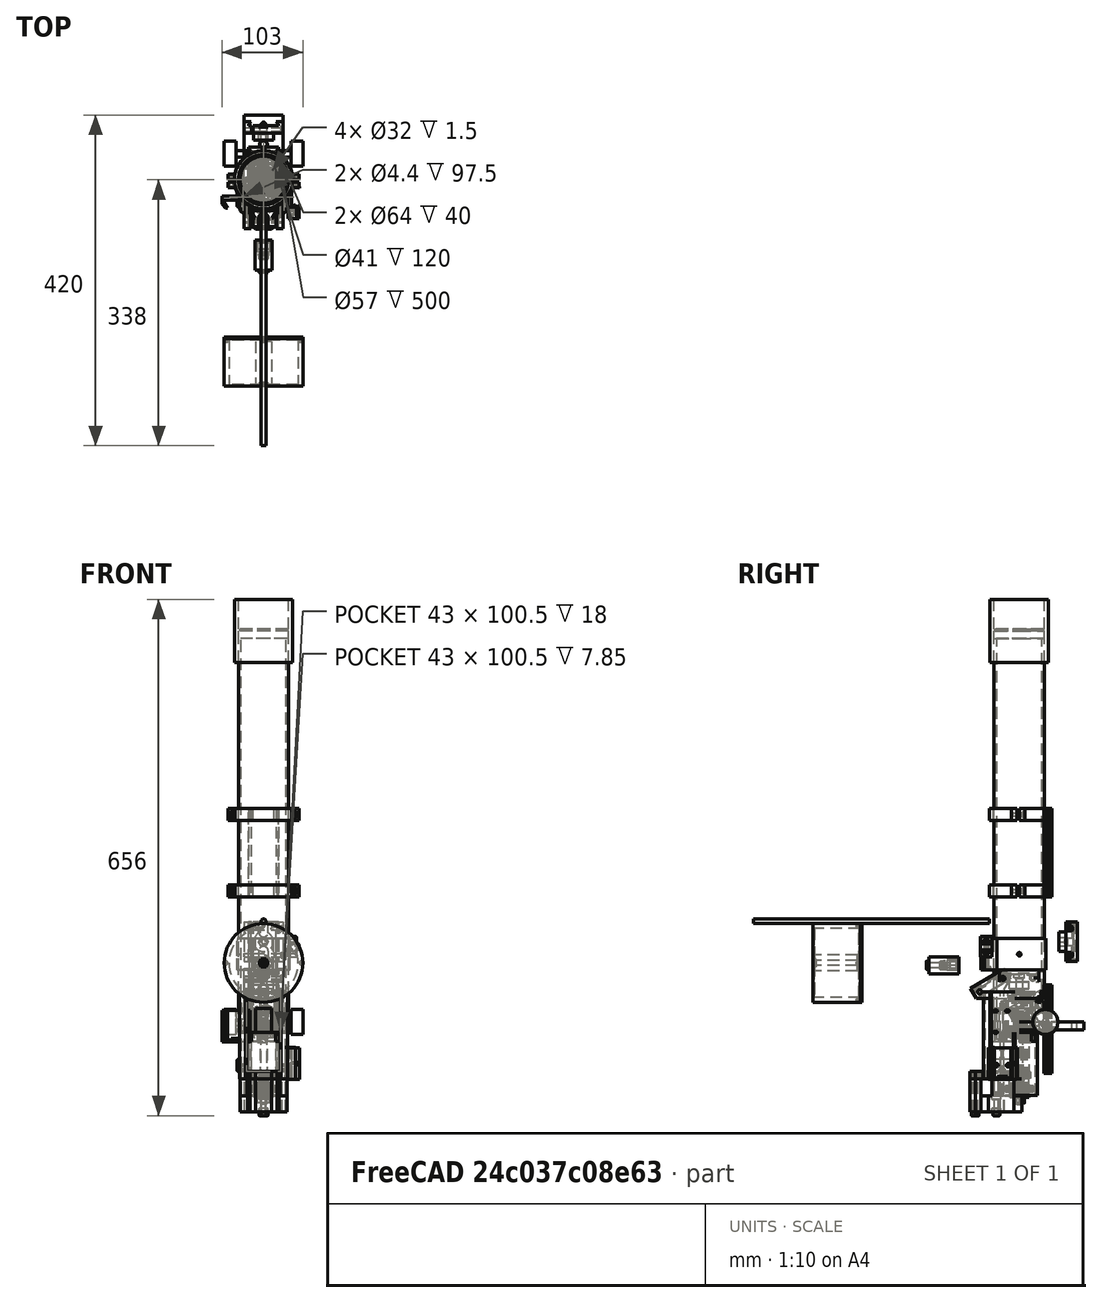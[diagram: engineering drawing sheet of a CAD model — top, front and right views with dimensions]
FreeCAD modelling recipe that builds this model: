
FCSTD DOCUMENT  (FreeCAD 0.17R12619 (Git))
Label: eq-mount-V1.2
License: All rights reserved
LicenseURL: http://en.wikipedia.org/wiki/All_rights_reserved
objects: Part::Cylinder×507, Part::MultiFuse×390, Part::Feature×377, Part::Cut×280, Part::Box×135, Part::FeaturePython×76, Part::Extrusion×70, App::Part×57, Sketcher::SketchObject×44, Part::Chamfer×20, Part::RegularPolygon×11, Part::Fillet×9
note: 1919 computed .brp shape members not serialized (recipe doc carries the construction recipe); baked Part::Feature solids carry a one-line shape summary decoded from their .brp

FEATURE [Part::FeaturePython] InvoluteGear007  # WARN: FeaturePython — macro-defined, semantics opaque (R4)
  backlash = 0
  beta = 0
  clearance = 0.25
  double_helix = false
  head = 0
  height = 5.5
  module = 1.2
  numpoints = 6
  pressure_angle = 20
  reversed_backlash = false
  shift = 0
  simple = false
  teeth = 27
  undercut = false
FEATURE [Part::FeaturePython] InvoluteGear006  # WARN: FeaturePython — macro-defined, semantics opaque (R4)
  backlash = 0
  beta = 0
  clearance = 0.25
  double_helix = false
  head = 0
  height = 5.5
  module = 1.2
  numpoints = 6
  pressure_angle = 20
  reversed_backlash = false
  shift = 0
  simple = false
  teeth = 27
  undercut = false
FEATURE [Part::FeaturePython] InvoluteGear005  # WARN: FeaturePython — macro-defined, semantics opaque (R4)
  backlash = 0
  beta = 0
  clearance = 0.25
  double_helix = false
  head = 0
  height = 5.5
  module = 1.2
  numpoints = 6
  pressure_angle = 20
  reversed_backlash = false
  shift = 0
  simple = false
  teeth = 27
  undercut = false
FEATURE [Part::Cylinder] Cylinder007  label="Válec007"
  Angle = 360
  AttacherType = Attacher::AttachEngine3D
  Height = 1.5
  Radius = 20
FEATURE [Part::Cylinder] Cylinder008  label="Válec008"
  Angle = 360
  AttacherType = Attacher::AttachEngine3D
  Height = 1.5
  Radius = 16
FEATURE [Part::Cylinder] Cylinder006  label="Válec006"
  Angle = 360
  AttacherType = Attacher::AttachEngine3D
  Height = 1.5
  Radius = 16
FEATURE [Part::Cut] Cut  label="Ring2"
  Base = -> Cylinder007
  Placement = pos=(0,0,5.5) rot=(0,0,1;0rad)
  Tool = -> Cylinder006
FEATURE [Part::Cylinder] Cylinder009  label="Válec009"
  Angle = 360
  AttacherType = Attacher::AttachEngine3D
  Height = 1.5
  Radius = 20
FEATURE [Part::Cut] Cut003  label="Ring003"
  Base = -> Cylinder009
  Placement = pos=(0,0,-1.5) rot=(0,0,1;0rad)
  Tool = -> Cylinder008
FEATURE [Part::Cylinder] Cylinder005  label="Válec005"
  Angle = 360
  AttacherType = Attacher::AttachEngine3D
  Height = 5.5
  Radius = 20
FEATURE [Part::Cut] Cut002  label="ring 001"
  Base = -> Cylinder005
  Tool = -> InvoluteGear005
FEATURE [Part::MultiFuse] Fusion  label="Ring zaklad Fin"
  Shapes = -> [Cut002,Cut,Cut003]
FEATURE [Sketcher::SketchObject] Sketch001
  MapMode = 45
  Placement = pos=(44.88,21.011,5.40003) rot=(0.707106,0.001666,0.707106;3.13826rad)
  sketch-geometry (7):
    g0: LineSegment StartX=5 StartY=0 StartZ=0 EndX=2.5 EndY=4.33013 EndZ=0
    g1: LineSegment StartX=2.5 StartY=4.33013 StartZ=0 EndX=-2.5 EndY=4.33013 EndZ=0
    g2: LineSegment StartX=-2.5 StartY=4.33013 StartZ=0 EndX=-5 EndY=0 EndZ=0
    g3: LineSegment StartX=-5 StartY=0 StartZ=0 EndX=-2.5 EndY=-4.33013 EndZ=0
    g4: LineSegment StartX=-2.5 StartY=-4.33013 StartZ=0 EndX=2.5 EndY=-4.33013 EndZ=0
    g5: LineSegment StartX=2.5 StartY=-4.33013 StartZ=0 EndX=5 EndY=0 EndZ=0
    g6: Circle [constr] CenterX=0 CenterY=0 CenterZ=0 NormalX=0 NormalY=0 NormalZ=1 AngleXU=0 Radius=5
  constraints (14):
    c: Coincident(g0,g1)
    c: Coincident(g1,g2)
    c: Coincident(g2,g3)
    c: Coincident(g3,g4)
    c: Coincident(g4,g5)
    c: Coincident(g5,g0)
    c: Equal(g0, g1-g5) x5
    c: PointOnObject(g0,g6)
    c: PointOnObject(g1,g6)
    c: PointOnObject(g2,g6)
    c: PointOnObject(g3,g6)
    c: PointOnObject(g4,g6)
    c: PointOnObject(g5,g6)
    c: PointOnObject(g6,g-1)
FEATURE [Part::Feature] Cut005_solid001_cs
  Placement = pos=(0,0,-11.25) rot=(0,0,1;0rad)
  shape: bbox 41 x 41 x 3e-07 mm, 0 faces, 0 solids (baked)
FEATURE [Part::Feature] Screw_solid003  label="M2x4-Screw (Solid)003"
  Placement = pos=(0,0,0) rot=(0,0,1;1.0472rad)
  shape: bbox 3.6 x 3.6 x 4 mm, 12 faces (baked)
FEATURE [Part::Feature] Cylinder014002  label="Válec014"
  Placement = pos=(0,0,0) rot=(0,0,1;4.18879rad)
  shape: bbox 16 x 16 x 10 mm, 3 faces (baked)
FEATURE [Part::Feature] Screw_solid004  label="M2x4-Screw (Solid)004"
  Placement = pos=(0,0,0) rot=(0,0,-1;1.0472rad)
  shape: bbox 3.6 x 3.6 x 4 mm, 12 faces (baked)
FEATURE [Part::Feature] Screw_solid005  label="M2x4-Screw (Solid)005"
  Placement = pos=(0,0,0) rot=(0,0,1;3.14159rad)
  shape: bbox 3.6 x 3.6 x 4 mm, 12 faces (baked)
FEATURE [Part::MultiFuse] Fusion004  label="srouby002"
  Shapes = -> [Screw_solid003,Screw_solid004,Screw_solid005]
FEATURE [Part::Feature] Cut008_solid  label="Planet001"
  shape: bbox 12.9 x 13.1 x 5 mm, 57 faces (baked)
FEATURE [Part::Feature] Cylinder014001  label="Válec013"
  Placement = pos=(0,0,0) rot=(0,0,1;2.0944rad)
  shape: bbox 16 x 16 x 10 mm, 3 faces (baked)
FEATURE [Part::Cylinder] Cylinder014005010  label="Unasec vrch001"
  Angle = 360
  AttacherType = Attacher::AttachEngine3D
  Height = 1.5
  Placement = pos=(0,0,5.5) rot=(0,0,1;0rad)
  Radius = 15.5
FEATURE [Part::Cylinder] Cylinder010  label="unasec spodek"
  Angle = 360
  AttacherType = Attacher::AttachEngine3D
  Height = 1.5
  Placement = pos=(0,0,-1.5) rot=(0,0,1;0rad)
  Radius = 15.5
FEATURE [Part::Cylinder] Cylinder  label="Válec"
  Angle = 360
  AttacherType = Attacher::AttachEngine3D
  Height = 10
  Placement = pos=(0,0,-3) rot=(0,0,1;0rad)
  Radius = 7
FEATURE [Part::Cylinder] Cylinder014005007  label="Válec024"
  Angle = 360
  AttacherType = Attacher::AttachEngine3D
  Height = 7.5
  Placement = pos=(0,0,-7) rot=(0,0,1;0rad)
  Radius = 6.5
FEATURE [Part::Cylinder] Cylinder013  label="Válec011"
  Angle = 360
  AttacherType = Attacher::AttachEngine3D
  Height = 10
  Placement = pos=(10.5,0,0) rot=(0,0,1;0rad)
  Radius = 8
FEATURE [Part::MultiFuse] Fusion001
  Shapes = -> [Cylinder,Cylinder013,Cylinder014002,Cylinder014001]
FEATURE [Part::Cylinder] Cylinder011  label="unasec stred"
  Angle = 360
  AttacherType = Attacher::AttachEngine3D
  Height = 7
  Placement = pos=(0,0,-1.5) rot=(0,0,1;0rad)
  Radius = 13.5
FEATURE [Part::MultiFuse] Fusion002
  Shapes = -> [Cylinder011,Cylinder010]
FEATURE [Part::Cut] Cut004  label="unasec spodek001"
  Base = -> Fusion002
  Tool = -> Fusion001
FEATURE [Part::Cut] Cut006  label="Uasec spodek"
  Base = -> Cut004
  Tool = -> Fusion004
FEATURE [Part::Cylinder] Cylinder014005008  label="Válec025"
  Angle = 360
  AttacherType = Attacher::AttachEngine3D
  Height = 15
  Placement = pos=(0,0,-8) rot=(0,0,1;0rad)
  Radius = 2.65
FEATURE [Part::Cylinder] Cylinder014005009  label="Válec026"
  Angle = 360
  AttacherType = Attacher::AttachEngine3D
  Height = 7
  Placement = pos=(0,0,-7) rot=(0,0,1;0rad)
  Radius = 12
FEATURE [Part::Extrusion] Extrude  label="box"
  Base = -> Cut005_solid001_cs
  Dir = (0,0,1)
  DirMode = 2
  FaceMakerClass = Part::FaceMakerBullseye
  LengthFwd = 19
  LengthRev = 0
  Placement = pos=(0,0,-11.5) rot=(0,0,1;0rad)
  Solid = true
  Symmetric = false
FEATURE [Part::RegularPolygon] RegularPolygon  label="Pravidelný n-úhelník"
  AttacherType = Attacher::AttachEngine3D
  Circumradius = 6
  Polygon = 6
FEATURE [Part::Extrusion] Extrude006
  Base = -> RegularPolygon
  Dir = (0,0,1)
  DirMode = 2
  FaceMakerClass = Part::FaceMakerBullseye
  LengthFwd = 8
  LengthRev = 0
  Placement = pos=(0,0,13) rot=(0,0,1;0rad)
  Solid = true
  Symmetric = false
FEATURE [Part::Extrusion] Extrude007
  Base = -> Sketch001
  Dir = (1,0,0)
  DirMode = 2
  FaceMakerClass = Part::FaceMakerBullseye
  LengthFwd = 5
  LengthRev = 0
  Placement = pos=(0,0,0.25) rot=(0,0,1;0rad)
  Solid = true
  Symmetric = false
FEATURE [Part::FeaturePython] InvoluteGear012  # WARN: FeaturePython — macro-defined, semantics opaque (R4)
  backlash = 0
  beta = 0
  clearance = 0.25
  double_helix = false
  head = 0
  height = 5.5
  module = 1.2
  numpoints = 6
  pressure_angle = 20
  reversed_backlash = false
  shift = 0
  simple = false
  teeth = 27
  undercut = false
FEATURE [Part::FeaturePython] InvoluteGear013  # WARN: FeaturePython — macro-defined, semantics opaque (R4)
  backlash = 0
  beta = 0
  clearance = 0.25
  double_helix = false
  head = 0
  height = 5.5
  module = 1.2
  numpoints = 6
  pressure_angle = 20
  reversed_backlash = false
  shift = 0
  simple = false
  teeth = 27
  undercut = false
FEATURE [Part::Feature] Cylinder014005025  label="Válec038"
  Placement = pos=(0,0,0) rot=(0,0,1;2.0944rad)
  shape: bbox 5 x 5 x 7 mm, 3 faces (baked)
FEATURE [Part::Feature] Cylinder014005026  label="Válec039"
  Placement = pos=(0,0,0) rot=(0,0,1;2.0944rad)
  shape: bbox 16 x 16 x 10 mm, 3 faces (baked)
FEATURE [Part::Feature] Cylinder014005024  label="Válec037"
  Placement = pos=(0,0,0) rot=(0,0,1;4.18879rad)
  shape: bbox 16 x 16 x 10 mm, 3 faces (baked)
FEATURE [Part::Feature] Screw_solid006  label="M2x4-Screw (Solid)006"
  Placement = pos=(0,0,0) rot=(0,0,1;1.0472rad)
  shape: bbox 3.6 x 3.6 x 4 mm, 12 faces (baked)
FEATURE [Part::Feature] Screw_solid007  label="M2x4-Screw (Solid)007"
  Placement = pos=(0,0,0) rot=(0,0,-1;1.0472rad)
  shape: bbox 3.6 x 3.6 x 4 mm, 12 faces (baked)
FEATURE [Part::Feature] Cylinder014005006  label="Válec023"
  Placement = pos=(0,0,0) rot=(0,0,1;4.18879rad)
  shape: bbox 5 x 5 x 7 mm, 3 faces (baked)
FEATURE [Part::Feature] Cut008_solid001  label="Planet002"
  Placement = pos=(0,0,0) rot=(0,0,1;2.0944rad)
  shape: bbox 12.9 x 13.1 x 5 mm, 57 faces (baked)
FEATURE [Part::Feature] Cut008_solid002  label="Planet003"
  Placement = pos=(0,0,0) rot=(0,0,1;4.18879rad)
  shape: bbox 12.9 x 13.1 x 5 mm, 57 faces (baked)
FEATURE [Part::Feature] Cut007_solid  label="Sun1"
  shape: bbox 12.9 x 13.1 x 5 mm, 57 faces (baked)
FEATURE [Part::MultiFuse] Fusion010
  Shapes = -> [Cut007_solid,Cylinder014005007,Cylinder014005009]
FEATURE [Part::Feature] Screw_solid008  label="M2x4-Screw (Solid)008"
  Placement = pos=(0,0,0) rot=(0,0,1;3.14159rad)
  shape: bbox 3.6 x 3.6 x 4 mm, 12 faces (baked)
FEATURE [Part::MultiFuse] Fusion011  label="srouby003"
  Placement = pos=(0,0,0.5) rot=(0,0,1;0rad)
  Shapes = -> [Screw_solid006,Screw_solid007,Screw_solid008]
FEATURE [Part::Cut] Cut012  label="unasec vrch001"
  Base = -> Cylinder014005010
  Tool = -> Fusion011
FEATURE [Part::Feature] Cylinder014005005  label="Válec022"
  Placement = pos=(0,0,0) rot=(0,0,1;2.0944rad)
  shape: bbox 5 x 5 x 7 mm, 3 faces (baked)
FEATURE [Part::Feature] Cylinder014005013  label="Válec029"
  Placement = pos=(0,0,0) rot=(0,0,1;2.0944rad)
  shape: bbox 5 x 5 x 7 mm, 3 faces (baked)
FEATURE [Part::Feature] Cylinder014005004  label="Válec021"
  shape: bbox 5 x 5 x 7 mm, 3 faces (baked)
FEATURE [Part::MultiFuse] Fusion006
  Shapes = -> [Cylinder014005006,Cylinder014005004,Cylinder014005005]
FEATURE [Part::MultiFuse] Fusion008  label="Unasec spdek final"
  Shapes = -> [Cut006,Fusion006]
FEATURE [Part::Feature] Cylinder014005012  label="Válec028"
  shape: bbox 5 x 5 x 7 mm, 3 faces (baked)
FEATURE [Part::Feature] Cylinder014005014  label="Válec030"
  Placement = pos=(0,0,0) rot=(0,0,1;4.18879rad)
  shape: bbox 5 x 5 x 7 mm, 3 faces (baked)
FEATURE [Part::MultiFuse] Fusion012
  Shapes = -> [Cylinder014005014,Cylinder014005012,Cylinder014005013]
FEATURE [Part::Feature] Cut008_solid003  label="Planet004"
  Placement = pos=(0,0,0) rot=(0,0,1;4.18879rad)
  shape: bbox 12.9 x 13.1 x 5 mm, 57 faces (baked)
FEATURE [Part::Cylinder] Cylinder014005016  label="unasec spodek003"
  Angle = 360
  AttacherType = Attacher::AttachEngine3D
  Height = 1.5
  Placement = pos=(0,0,-1.5) rot=(0,0,1;0rad)
  Radius = 15.5
FEATURE [Part::Cylinder] Cylinder014005035  label="Válec048"
  Angle = 360
  AttacherType = Attacher::AttachEngine3D
  Height = 18
  Radius = 2.6
FEATURE [Part::Cylinder] Cylinder014005032  label="Válec045"
  Angle = 360
  AttacherType = Attacher::AttachEngine3D
  Height = 1.5
  Radius = 16
FEATURE [Part::Cylinder] Cylinder014005015  label="Válec031"
  Angle = 360
  AttacherType = Attacher::AttachEngine3D
  Height = 10
  Placement = pos=(0,0,-3) rot=(0,0,1;0rad)
  Radius = 7
FEATURE [Part::Cylinder] Cylinder014005029  label="Válec042"
  Angle = 360
  AttacherType = Attacher::AttachEngine3D
  Height = 1.5
  Radius = 16
FEATURE [Part::Cylinder] Cylinder014005031  label="Válec044"
  Angle = 360
  AttacherType = Attacher::AttachEngine3D
  Height = 1.5
  Radius = 20
FEATURE [Part::Cut] Cut017  label="Ring005"
  Base = -> Cylinder014005031
  Placement = pos=(0,0,-1.5) rot=(0,0,1;0rad)
  Tool = -> Cylinder014005032
FEATURE [Part::Cylinder] Cylinder014005034  label="Válec047"
  Angle = 360
  AttacherType = Attacher::AttachEngine3D
  Height = 4
  Placement = pos=(0,0,7) rot=(0,0,1;0rad)
  Radius = 6.5
FEATURE [Part::Cylinder] Cylinder014005036  label="Válec049"
  Angle = 360
  AttacherType = Attacher::AttachEngine3D
  Height = 4
  Placement = pos=(0,0,7) rot=(0,0,1;0rad)
  Radius = 6.5
FEATURE [Part::Cylinder] Cylinder014005041  label="Unasec vrch003"
  Angle = 360
  AttacherType = Attacher::AttachEngine3D
  Height = 1.5
  Placement = pos=(0,0,5.5) rot=(0,0,1;0rad)
  Radius = 15.5
FEATURE [Part::Cylinder] Cylinder014005011  label="Válec027"
  Angle = 360
  AttacherType = Attacher::AttachEngine3D
  Height = 7
  Radius = 2.6
FEATURE [Part::MultiFuse] Fusion013
  Placement = pos=(0,0,1) rot=(0,0,1;0rad)
  Shapes = -> [Fusion012,Cylinder014005011]
FEATURE [Part::Cut] Cut011  label="Unasec Vrch zaklad001"
  Base = -> Cut012
  Tool = -> Fusion013
FEATURE [Part::Cylinder] Cylinder014005017  label="unasec stred001"
  Angle = 360
  AttacherType = Attacher::AttachEngine3D
  Height = 7
  Placement = pos=(0,0,-1.5) rot=(0,0,1;0rad)
  Radius = 13.5
FEATURE [Part::Cylinder] Cylinder014005018  label="Válec032"
  Angle = 360
  AttacherType = Attacher::AttachEngine3D
  Height = 10
  Placement = pos=(10.5,0,0) rot=(0,0,1;0rad)
  Radius = 8
FEATURE [Part::MultiFuse] Fusion017
  Shapes = -> [Cylinder014005015,Cylinder014005018,Cylinder014005024,Cylinder014005026]
FEATURE [Part::Cylinder] Cylinder014005030  label="Válec043"
  Angle = 360
  AttacherType = Attacher::AttachEngine3D
  Height = 1.5
  Radius = 20
FEATURE [Part::Cut] Cut014  label="Ring004"
  Base = -> Cylinder014005030
  Placement = pos=(0,0,5.5) rot=(0,0,1;0rad)
  Tool = -> Cylinder014005029
FEATURE [Part::Cylinder] Cylinder014005033  label="Válec046"
  Angle = 360
  AttacherType = Attacher::AttachEngine3D
  Height = 5.5
  Radius = 20
FEATURE [Part::Cut] Cut015  label="ring 002"
  Base = -> Cylinder014005033
  Tool = -> InvoluteGear006
FEATURE [Part::Cylinder] Cylinder014005037  label="Válec050"
  Angle = 360
  AttacherType = Attacher::AttachEngine3D
  Height = 18
  Radius = 2.6
FEATURE [Part::Cylinder] Cylinder014005051  label="Válec063"
  Angle = 360
  AttacherType = Attacher::AttachEngine3D
  Height = 7
  Radius = 2.6
FEATURE [Part::Cylinder] Cylinder014005052  label="Válec064"
  Angle = 360
  AttacherType = Attacher::AttachEngine3D
  Height = 10
  Placement = pos=(0,0,-3) rot=(0,0,1;0rad)
  Radius = 7
FEATURE [Part::Cylinder] Cylinder014005042  label="Válec054"
  Angle = 360
  AttacherType = Attacher::AttachEngine3D
  Height = 7
  Radius = 2.6
FEATURE [Part::Cylinder] Cylinder014005054  label="Válec065"
  Angle = 360
  AttacherType = Attacher::AttachEngine3D
  Height = 10
  Placement = pos=(10.5,0,0) rot=(0,0,1;0rad)
  Radius = 8
FEATURE [Part::Cylinder] Cylinder014005056  label="Válec066"
  Angle = 360
  AttacherType = Attacher::AttachEngine3D
  Height = 1.5
  Radius = 16
FEATURE [Part::Cylinder] Cylinder014005053  label="unasec stred002"
  Angle = 360
  AttacherType = Attacher::AttachEngine3D
  Height = 7
  Placement = pos=(0,0,-1.5) rot=(0,0,1;0rad)
  Radius = 13.5
FEATURE [Part::Cylinder] Cylinder014005057  label="Válec067"
  Angle = 360
  AttacherType = Attacher::AttachEngine3D
  Height = 4
  Placement = pos=(0,0,7) rot=(0,0,1;0rad)
  Radius = 6.5
FEATURE [Part::Cylinder] Cylinder014005055  label="unasec spodek005"
  Angle = 360
  AttacherType = Attacher::AttachEngine3D
  Height = 1.5
  Placement = pos=(0,0,-1.5) rot=(0,0,1;0rad)
  Radius = 15.5
FEATURE [Part::Feature] Screw_solid016  label="M2x4-Screw (Solid)016"
  Placement = pos=(0,0,0) rot=(0,0,1;3.14159rad)
  shape: bbox 3.6 x 3.6 x 4 mm, 12 faces (baked)
FEATURE [Part::Feature] Screw_solid014  label="M2x4-Screw (Solid)014"
  Placement = pos=(0,0,0) rot=(0,0,-1;1.0472rad)
  shape: bbox 3.6 x 3.6 x 4 mm, 12 faces (baked)
FEATURE [Part::Feature] Cylinder014005027  label="Válec040"
  shape: bbox 5 x 5 x 7 mm, 3 faces (baked)
FEATURE [Part::Feature] Screw_solid015  label="M2x4-Screw (Solid)015"
  Placement = pos=(0,0,0) rot=(0,0,-1;1.0472rad)
  shape: bbox 3.6 x 3.6 x 4 mm, 12 faces (baked)
FEATURE [Part::Feature] Screw_solid011  label="M2x4-Screw (Solid)011"
  Placement = pos=(0,0,0) rot=(0,0,1;3.14159rad)
  shape: bbox 3.6 x 3.6 x 4 mm, 12 faces (baked)
FEATURE [Part::Feature] Cut008_solid004  label="Planet005"
  shape: bbox 12.9 x 13.1 x 5 mm, 57 faces (baked)
FEATURE [Part::Feature] Cylinder014005028  label="Válec041"
  Placement = pos=(0,0,0) rot=(0,0,1;4.18879rad)
  shape: bbox 5 x 5 x 7 mm, 3 faces (baked)
FEATURE [Part::Feature] Cut007_solid001  label="Sun2"
  Placement = pos=(0,0,10.5) rot=(0,0,1;0rad)
  shape: bbox 12.9 x 13.1 x 5 mm, 57 faces (baked)
FEATURE [Part::Feature] Cut008_solid005  label="Planet006"
  Placement = pos=(0,0,0) rot=(0,0,1;2.0944rad)
  shape: bbox 12.9 x 13.1 x 5 mm, 57 faces (baked)
FEATURE [Part::Feature] Cut007_solid002  label="Sun003"
  Placement = pos=(0,0,10.5) rot=(0,0,1;0rad)
  shape: bbox 12.9 x 13.1 x 5 mm, 57 faces (baked)
FEATURE [Part::Feature] Screw_solid013  label="M2x4-Screw (Solid)013"
  Placement = pos=(0,0,0) rot=(0,0,1;1.0472rad)
  shape: bbox 3.6 x 3.6 x 4 mm, 12 faces (baked)
FEATURE [Part::MultiFuse] Fusion018
  Shapes = -> [Cylinder014005017,Cylinder014005016]
FEATURE [Part::Cut] Cut016  label="unasec spodek002"
  Base = -> Fusion018
  Tool = -> Fusion017
FEATURE [Part::MultiFuse] Fusion028  label="Tělo I"
  Shapes = -> [Extrude,Fusion]
FEATURE [Part::MultiFuse] Fusion019  label="srouby005"
  Shapes = -> [Screw_solid013,Screw_solid014,Screw_solid011]
FEATURE [Part::Cut] Cut018  label="Uasec spodek001"
  Base = -> Cut016
  Tool = -> Fusion019
FEATURE [Part::MultiFuse] Fusion023  label="unasec vrhch 2"
  Shapes = -> [Cut011,Cut007_solid001,Cylinder014005034]
FEATURE [Part::Cut] Cut020  label="Unasec + Sun"
  Base = -> Fusion023
  Tool = -> Cylinder014005035
FEATURE [Part::MultiFuse] Fusion021
  Shapes = -> [Cylinder014005028,Cylinder014005027,Cylinder014005025]
FEATURE [Part::MultiFuse] Fusion020  label="Unasec spdek final001"
  Shapes = -> [Cut018,Fusion021]
FEATURE [Part::MultiFuse] Fusion030
  Shapes = -> [Cylinder014005053,Cylinder014005055]
FEATURE [Part::MultiFuse] Fusion022  label="Ring zaklad Fin001"
  Shapes = -> [Cut015,Cut014,Cut017]
FEATURE [Part::Feature] Cut008_solid007  label="Planet008"
  shape: bbox 12.9 x 13.1 x 5 mm, 57 faces (baked)
FEATURE [Part::Feature] Screw_solid022  label="M2x4-Screw (Solid)022"
  Placement = pos=(0,0,0) rot=(0,0,1;3.14159rad)
  shape: bbox 3.6 x 3.6 x 4 mm, 12 faces (baked)
FEATURE [Part::Feature] Cylinder014005048  label="Válec060"
  Placement = pos=(0,0,0) rot=(0,0,1;4.18879rad)
  shape: bbox 16 x 16 x 10 mm, 3 faces (baked)
FEATURE [Part::Feature] Cylinder014005049  label="Válec061"
  Placement = pos=(0,0,0) rot=(0,0,1;2.0944rad)
  shape: bbox 5 x 5 x 7 mm, 3 faces (baked)
FEATURE [Part::Feature] Cylinder014005050  label="Válec062"
  Placement = pos=(0,0,0) rot=(0,0,1;2.0944rad)
  shape: bbox 16 x 16 x 10 mm, 3 faces (baked)
FEATURE [Part::MultiFuse] Fusion031
  Shapes = -> [Cylinder014005052,Cylinder014005054,Cylinder014005048,Cylinder014005050]
FEATURE [Part::Cut] Cut030  label="unasec spodek004"
  Base = -> Fusion030
  Tool = -> Fusion031
FEATURE [Part::Feature] Cylinder014005040  label="Válec053"
  Placement = pos=(0,0,0) rot=(0,0,1;2.0944rad)
  shape: bbox 5 x 5 x 7 mm, 3 faces (baked)
FEATURE [Part::Feature] Cylinder014005039  label="Válec052"
  shape: bbox 5 x 5 x 7 mm, 3 faces (baked)
FEATURE [Part::Feature] Screw_solid019  label="M2x4-Screw (Solid)019"
  Placement = pos=(0,0,0) rot=(0,0,-1;1.0472rad)
  shape: bbox 3.6 x 3.6 x 4 mm, 12 faces (baked)
FEATURE [Part::Feature] Cut008_solid008  label="Planet009"
  Placement = pos=(0,0,0) rot=(0,0,1;4.18879rad)
  shape: bbox 12.9 x 13.1 x 5 mm, 57 faces (baked)
FEATURE [Part::Feature] Cut005_solid001_cs003
  Placement = pos=(0,0,-11.25) rot=(0,0,1;0rad)
  shape: bbox 41 x 41 x 3e-07 mm, 0 faces, 0 solids (baked)
FEATURE [Part::Extrusion] Extrude002  label="box002"
  Base = -> Cut005_solid001_cs003
  Dir = (0,0,1)
  DirMode = 2
  FaceMakerClass = Part::FaceMakerBullseye
  LengthFwd = 10.5
  LengthRev = 0
  Placement = pos=(0,0,-3) rot=(0,0,1;0rad)
  Solid = true
  Symmetric = false
FEATURE [Part::Feature] Screw_solid023  label="M2x4-Screw (Solid)023"
  Placement = pos=(0,0,0) rot=(0,0,1;1.0472rad)
  shape: bbox 3.6 x 3.6 x 4 mm, 12 faces (baked)
FEATURE [Part::Feature] Cylinder014005046  label="Válec058"
  Placement = pos=(0,0,0) rot=(0,0,1;4.18879rad)
  shape: bbox 5 x 5 x 7 mm, 3 faces (baked)
FEATURE [Part::Feature] Cut005_solid001_cs002
  Placement = pos=(0,0,-11.25) rot=(0,0,1;0rad)
  shape: bbox 41 x 41 x 3e-07 mm, 0 faces, 0 solids (baked)
FEATURE [Part::Extrusion] Extrude001  label="box001"
  Base = -> Cut005_solid001_cs002
  Dir = (0,0,1)
  DirMode = 2
  FaceMakerClass = Part::FaceMakerBullseye
  LengthFwd = 10.5
  LengthRev = 0
  Placement = pos=(0,0,-3) rot=(0,0,1;0rad)
  Solid = true
  Symmetric = false
FEATURE [Part::MultiFuse] Fusion029  label="teloII"
  Shapes = -> [Fusion022,Extrude001]
FEATURE [Part::Feature] Screw_solid017  label="M2x4-Screw (Solid)017"
  Placement = pos=(0,0,0) rot=(0,0,1;1.0472rad)
  shape: bbox 3.6 x 3.6 x 4 mm, 12 faces (baked)
FEATURE [Part::MultiFuse] Fusion027  label="srouby006"
  Placement = pos=(0,0,0.5) rot=(0,0,1;0rad)
  Shapes = -> [Screw_solid017,Screw_solid015,Screw_solid016]
FEATURE [Part::Cut] Cut021  label="unasec vrch003"
  Base = -> Cylinder014005041
  Tool = -> Fusion027
FEATURE [Part::Feature] Cylinder014005045  label="Válec057"
  Placement = pos=(0,0,0) rot=(0,0,1;4.18879rad)
  shape: bbox 5 x 5 x 7 mm, 3 faces (baked)
FEATURE [Part::Feature] Cut007_solid003  label="Sun004"
  Placement = pos=(0,0,10.5) rot=(0,0,1;0rad)
  shape: bbox 12.9 x 13.1 x 5 mm, 57 faces (baked)
FEATURE [Part::Feature] Cylinder014005047  label="Válec059"
  shape: bbox 5 x 5 x 7 mm, 3 faces (baked)
FEATURE [Part::MultiFuse] Fusion033
  Shapes = -> [Cylinder014005045,Cylinder014005047,Cylinder014005049]
FEATURE [Part::Feature] Screw_solid021  label="M2x4-Screw (Solid)021"
  Placement = pos=(0,0,0) rot=(0,0,-1;1.0472rad)
  shape: bbox 3.6 x 3.6 x 4 mm, 12 faces (baked)
FEATURE [Part::MultiFuse] Fusion039  label="srouby008"
  Shapes = -> [Screw_solid023,Screw_solid021,Screw_solid022]
FEATURE [Part::Cut] Cut031  label="Uasec spodek002"
  Base = -> Cut030
  Tool = -> Fusion039
FEATURE [Part::MultiFuse] Fusion040  label="Unasec spdek final002"
  Shapes = -> [Cut031,Fusion033]
FEATURE [Part::Feature] Cylinder014005044  label="Válec056"
  Placement = pos=(0,0,0) rot=(0,0,1;2.0944rad)
  shape: bbox 5 x 5 x 7 mm, 3 faces (baked)
FEATURE [Part::Feature] Cylinder014005038  label="Válec051"
  Placement = pos=(0,0,0) rot=(0,0,1;4.18879rad)
  shape: bbox 5 x 5 x 7 mm, 3 faces (baked)
FEATURE [Part::MultiFuse] Fusion026
  Shapes = -> [Cylinder014005038,Cylinder014005039,Cylinder014005040]
FEATURE [Part::MultiFuse] Fusion025
  Placement = pos=(0,0,1) rot=(0,0,1;0rad)
  Shapes = -> [Fusion026,Cylinder014005042]
FEATURE [Part::Cut] Cut022  label="Unasec Vrch zaklad003"
  Base = -> Cut021
  Tool = -> Fusion025
FEATURE [Part::MultiFuse] Fusion024  label="unasec vrhch 003"
  Shapes = -> [Cut022,Cut007_solid002,Cylinder014005036]
FEATURE [Part::Cut] Cut023  label="Unasec + Sun001"
  Base = -> Fusion024
  Tool = -> Cylinder014005037
FEATURE [App::Part] Part  label="Part071"
  Group = -> [Cut016,Cut018,Cylinder014005015,Cylinder014005016,Cylinder014005017,Cylinder014005018,Cylinder014005024,Cylinder014005025,Cylinder014005026,Screw_solid011,Cylinder014005027,Screw_solid013,Cylinder014005028,Screw_solid014,Fusion017,Fusion018,Fusion019,Fusion021,Fusion020,Cut008_solid004,Cut008_solid005,Cut008_solid003,Screw_solid017,Cylinder014005039,Cylinder014005040,Screw_solid015,Screw_solid016,+26 more]
  License = CC BY 3.0
  LicenseURL = http://creativecommons.org/licenses/by/3.0/
  Origin = -> Origin
  Placement = pos=(0,0,10.5) rot=(0,0,1;0rad)
FEATURE [Part::Feature] Cut008_solid006  label="Planet007"
  Placement = pos=(0,0,0) rot=(0,0,1;2.0944rad)
  shape: bbox 12.9 x 13.1 x 5 mm, 57 faces (baked)
FEATURE [Part::Feature] Screw_solid020  label="M2x4-Screw (Solid)020"
  Placement = pos=(0,0,0) rot=(0,0,1;3.14159rad)
  shape: bbox 3.6 x 3.6 x 4 mm, 12 faces (baked)
FEATURE [Part::Feature] Cylinder014005043  label="Válec055"
  shape: bbox 5 x 5 x 7 mm, 3 faces (baked)
FEATURE [Part::MultiFuse] Fusion038
  Shapes = -> [Cylinder014005046,Cylinder014005043,Cylinder014005044]
FEATURE [Part::MultiFuse] Fusion035
  Placement = pos=(0,0,1) rot=(0,0,1;0rad)
  Shapes = -> [Fusion038,Cylinder014005051]
FEATURE [Part::Feature] Screw_solid018  label="M2x4-Screw (Solid)018"
  Placement = pos=(0,0,0) rot=(0,0,1;1.0472rad)
  shape: bbox 3.6 x 3.6 x 4 mm, 12 faces (baked)
FEATURE [Part::MultiFuse] Fusion036  label="srouby007"
  Placement = pos=(0,0,0.5) rot=(0,0,1;0rad)
  Shapes = -> [Screw_solid018,Screw_solid019,Screw_solid020]
FEATURE [Part::Cylinder] Cylinder014005060  label="Válec070"
  Angle = 360
  AttacherType = Attacher::AttachEngine3D
  Height = 5.5
  Radius = 20
FEATURE [Part::Cut] Cut024  label="ring 003"
  Base = -> Cylinder014005060
  Tool = -> InvoluteGear007
FEATURE [Part::Cylinder] Cylinder014005063  label="Válec072"
  Angle = 360
  AttacherType = Attacher::AttachEngine3D
  Height = 1.5
  Radius = 20
FEATURE [Part::Cut] Cut029  label="Ring007"
  Base = -> Cylinder014005063
  Placement = pos=(0,0,5.5) rot=(0,0,1;0rad)
  Tool = -> Cylinder014005056
FEATURE [Part::Cylinder] Cylinder014005058  label="Válec068"
  Angle = 360
  AttacherType = Attacher::AttachEngine3D
  Height = 1.5
  Radius = 16
FEATURE [Part::Cylinder] Cylinder014005059  label="Válec069"
  Angle = 360
  AttacherType = Attacher::AttachEngine3D
  Height = 18
  Radius = 2.6
FEATURE [Part::Cylinder] Cylinder014005062  label="Válec071"
  Angle = 360
  AttacherType = Attacher::AttachEngine3D
  Height = 1.5
  Radius = 20
FEATURE [Part::Cut] Cut025  label="Ring006"
  Base = -> Cylinder014005062
  Placement = pos=(0,0,-1.5) rot=(0,0,1;0rad)
  Tool = -> Cylinder014005058
FEATURE [Part::MultiFuse] Fusion034  label="Ring zaklad Fin002"
  Shapes = -> [Cut024,Cut029,Cut025]
FEATURE [Part::MultiFuse] Fusion032  label="teloII001"
  Shapes = -> [Fusion034,Extrude002]
FEATURE [Part::Cylinder] Cylinder014005061  label="Unasec vrch004"
  Angle = 360
  AttacherType = Attacher::AttachEngine3D
  Height = 1.5
  Placement = pos=(0,0,5.5) rot=(0,0,1;0rad)
  Radius = 15.5
FEATURE [Part::Cut] Cut028  label="unasec vrch004"
  Base = -> Cylinder014005061
  Tool = -> Fusion036
FEATURE [Part::Cut] Cut027  label="Unasec Vrch zaklad004"
  Base = -> Cut028
  Tool = -> Fusion035
FEATURE [Part::MultiFuse] Fusion037  label="unasec vrhch 004"
  Shapes = -> [Cut027,Cut007_solid003,Cylinder014005057]
FEATURE [Part::Cut] Cut026  label="Unasec + Sun002"
  Base = -> Fusion037
  Tool = -> Cylinder014005059
FEATURE [App::Part] Part002  label="Part070"
  Group = -> [Cut030,Cut031,Cylinder014005052,Cylinder014005055,Cylinder014005053,Cylinder014005054,Cylinder014005048,Cylinder014005049,Cylinder014005050,Screw_solid022,Cylinder014005047,Screw_solid023,Cylinder014005045,Screw_solid021,Fusion031,Fusion030,Fusion039,Fusion033,Fusion040,Cut008_solid007,Cut008_solid006,Cut008_solid008,Screw_solid018,Cylinder014005043,Cylinder014005044,Screw_solid019,Screw_solid020,+26 more]
  License = CC BY 3.0
  LicenseURL = http://creativecommons.org/licenses/by/3.0/
  Origin = -> Origin002
  Placement = pos=(0,0,21) rot=(0,0,1;0rad)
FEATURE [Part::Feature] Cut007_solid005  label="Sun006"
  Placement = pos=(0,0,10.5) rot=(0,0,1;0rad)
  shape: bbox 12.9 x 13.1 x 5 mm, 57 faces (baked)
FEATURE [Part::Feature] Cylinder014005109  label="Válec111"
  Placement = pos=(0,0,0) rot=(0,0,1;2.0944rad)
  shape: bbox 16 x 16 x 10 mm, 3 faces (baked)
FEATURE [Part::Feature] Cylinder014005108  label="Válec110"
  Placement = pos=(0,0,0) rot=(0,0,1;2.0944rad)
  shape: bbox 5 x 5 x 7 mm, 3 faces (baked)
FEATURE [Part::Feature] Cut008_solid013  label="Planet014"
  Placement = pos=(0,0,0) rot=(0,0,1;4.18879rad)
  shape: bbox 12.9 x 13.1 x 5 mm, 57 faces (baked)
FEATURE [Part::Feature] Cut008_solid014  label="Planet015"
  shape: bbox 12.9 x 13.1 x 5 mm, 57 faces (baked)
FEATURE [Part::Feature] Screw_solid038  label="M2x4-Screw (Solid)038"
  Placement = pos=(0,0,0) rot=(0,0,1;1.0472rad)
  shape: bbox 3.6 x 3.6 x 4 mm, 12 faces (baked)
FEATURE [Part::Feature] Cut005_solid001_cs005
  Placement = pos=(0,0,-11.25) rot=(0,0,1;0rad)
  shape: bbox 41 x 41 x 3e-07 mm, 0 faces, 0 solids (baked)
FEATURE [Part::Extrusion] Extrude004  label="box004"
  Base = -> Cut005_solid001_cs005
  Dir = (0,0,1)
  DirMode = 2
  FaceMakerClass = Part::FaceMakerBullseye
  LengthFwd = 10.5
  LengthRev = 0
  Placement = pos=(0,0,-3) rot=(0,0,1;0rad)
  Solid = true
  Symmetric = false
FEATURE [Part::Feature] Cylinder014005118  label="Válec119"
  shape: bbox 5 x 5 x 7 mm, 3 faces (baked)
FEATURE [Part::Feature] Cut007_solid006  label="Sun007"
  Placement = pos=(0,0,10.5) rot=(0,0,1;0rad)
  shape: bbox 12.9 x 13.1 x 5 mm, 57 faces (baked)
FEATURE [Part::Feature] Cylinder014005103  label="Válec105"
  Placement = pos=(0,0,0) rot=(0,0,1;2.0944rad)
  shape: bbox 5 x 5 x 7 mm, 3 faces (baked)
FEATURE [Part::Feature] Screw_solid035  label="M2x4-Screw (Solid)035"
  Placement = pos=(0,0,0) rot=(0,0,1;3.14159rad)
  shape: bbox 3.6 x 3.6 x 4 mm, 12 faces (baked)
FEATURE [Part::Feature] Cylinder014005102  label="Válec104"
  Placement = pos=(0,0,0) rot=(0,0,1;4.18879rad)
  shape: bbox 5 x 5 x 7 mm, 3 faces (baked)
FEATURE [Part::Feature] Cylinder014005106  label="Válec108"
  Placement = pos=(0,0,0) rot=(0,0,1;4.18879rad)
  shape: bbox 5 x 5 x 7 mm, 3 faces (baked)
FEATURE [Part::Feature] Screw_solid033  label="M2x4-Screw (Solid)033"
  Placement = pos=(0,0,0) rot=(0,0,1;1.0472rad)
  shape: bbox 3.6 x 3.6 x 4 mm, 12 faces (baked)
FEATURE [Part::Feature] Cut008_solid012  label="Planet013"
  Placement = pos=(0,0,0) rot=(0,0,1;2.0944rad)
  shape: bbox 12.9 x 13.1 x 5 mm, 57 faces (baked)
FEATURE [Part::Feature] Screw_solid036  label="M2x4-Screw (Solid)036"
  Placement = pos=(0,0,0) rot=(0,0,-1;1.0472rad)
  shape: bbox 3.6 x 3.6 x 4 mm, 12 faces (baked)
FEATURE [Part::Feature] Cylinder014005107  label="Válec109"
  shape: bbox 5 x 5 x 7 mm, 3 faces (baked)
FEATURE [Part::MultiFuse] Fusion063
  Shapes = -> [Cylinder014005106,Cylinder014005107,Cylinder014005103]
FEATURE [Part::Feature] Cylinder014005105  label="Válec107"
  Placement = pos=(0,0,0) rot=(0,0,1;4.18879rad)
  shape: bbox 16 x 16 x 10 mm, 3 faces (baked)
FEATURE [Part::Feature] Cylinder014005104  label="Válec106"
  shape: bbox 5 x 5 x 7 mm, 3 faces (baked)
FEATURE [Part::MultiFuse] Fusion062
  Shapes = -> [Cylinder014005102,Cylinder014005104,Cylinder014005108]
FEATURE [Part::Feature] Screw_solid037  label="M2x4-Screw (Solid)037"
  Placement = pos=(0,0,0) rot=(0,0,-1;1.0472rad)
  shape: bbox 3.6 x 3.6 x 4 mm, 12 faces (baked)
FEATURE [Part::MultiFuse] Fusion066  label="srouby013"
  Placement = pos=(0,0,0.5) rot=(0,0,1;0rad)
  Shapes = -> [Screw_solid033,Screw_solid037,Screw_solid035]
FEATURE [Part::Feature] Screw_solid034  label="M2x4-Screw (Solid)034"
  Placement = pos=(0,0,0) rot=(0,0,1;3.14159rad)
  shape: bbox 3.6 x 3.6 x 4 mm, 12 faces (baked)
FEATURE [Part::MultiFuse] Fusion065  label="srouby012"
  Shapes = -> [Screw_solid038,Screw_solid036,Screw_solid034]
FEATURE [Part::Cylinder] Cylinder014005101  label="Válec103"
  Angle = 360
  AttacherType = Attacher::AttachEngine3D
  Height = 10
  Placement = pos=(10.5,0,0) rot=(0,0,1;0rad)
  Radius = 8
FEATURE [Part::Cylinder] Cylinder014005110  label="Válec112"
  Angle = 360
  AttacherType = Attacher::AttachEngine3D
  Height = 1.5
  Radius = 16
FEATURE [Part::Cylinder] Cylinder014005098  label="Válec102"
  Angle = 360
  AttacherType = Attacher::AttachEngine3D
  Height = 10
  Placement = pos=(0,0,-3) rot=(0,0,1;0rad)
  Radius = 7
FEATURE [Part::MultiFuse] Fusion059
  Shapes = -> [Cylinder014005098,Cylinder014005101,Cylinder014005105,Cylinder014005109]
FEATURE [Part::Cylinder] Cylinder014005112  label="Válec114"
  Angle = 360
  AttacherType = Attacher::AttachEngine3D
  Height = 1.5
  Radius = 20
FEATURE [Part::Cylinder] Cylinder014005117  label="Válec118"
  Angle = 360
  AttacherType = Attacher::AttachEngine3D
  Height = 18
  Radius = 2.6
FEATURE [Part::Cylinder] Cylinder014005114  label="Válec116"
  Angle = 360
  AttacherType = Attacher::AttachEngine3D
  Height = 1.5
  Radius = 20
FEATURE [Part::Cut] Cut046  label="Ring011"
  Base = -> Cylinder014005114
  Placement = pos=(0,0,-1.5) rot=(0,0,1;0rad)
  Tool = -> Cylinder014005110
FEATURE [Part::Cylinder] Cylinder014005121  label="Válec122"
  Angle = 360
  AttacherType = Attacher::AttachEngine3D
  Height = 1.5
  Radius = 16
FEATURE [Part::Cylinder] Cylinder014005111  label="Válec113"
  Angle = 360
  AttacherType = Attacher::AttachEngine3D
  Height = 5.5
  Radius = 20
FEATURE [Part::Cut] Cut045  label="ring 005"
  Base = -> Cylinder014005111
  Tool = -> InvoluteGear012
FEATURE [Part::Cylinder] Cylinder014005119  label="Válec120"
  Angle = 360
  AttacherType = Attacher::AttachEngine3D
  Height = 1.5
  Radius = 20
FEATURE [Part::Cut] Cut054  label="Ring013"
  Base = -> Cylinder014005119
  Placement = pos=(0,0,5.5) rot=(0,0,1;0rad)
  Tool = -> Cylinder014005121
FEATURE [Part::Cylinder] Cylinder014005099  label="unasec stred005"
  Angle = 360
  AttacherType = Attacher::AttachEngine3D
  Height = 7
  Placement = pos=(0,0,-1.5) rot=(0,0,1;0rad)
  Radius = 13.5
FEATURE [Part::Cylinder] Cylinder014005097  label="Válec101"
  Angle = 360
  AttacherType = Attacher::AttachEngine3D
  Height = 7
  Radius = 2.6
FEATURE [Part::MultiFuse] Fusion068
  Placement = pos=(0,0,1) rot=(0,0,1;0rad)
  Shapes = -> [Fusion063,Cylinder014005097]
FEATURE [Part::Cylinder] Cylinder014005100  label="unasec spodek011"
  Angle = 360
  AttacherType = Attacher::AttachEngine3D
  Height = 1.5
  Placement = pos=(0,0,-1.5) rot=(0,0,1;0rad)
  Radius = 15.5
FEATURE [Part::MultiFuse] Fusion058
  Shapes = -> [Cylinder014005099,Cylinder014005100]
FEATURE [Part::Cut] Cut044  label="unasec spodek010"
  Base = -> Fusion058
  Tool = -> Fusion059
FEATURE [Part::Cut] Cut050  label="Uasec spodek005"
  Base = -> Cut044
  Tool = -> Fusion065
FEATURE [Part::MultiFuse] Fusion064  label="Unasec spdek final004"
  Shapes = -> [Cut050,Fusion062]
FEATURE [Part::Cylinder] Cylinder014005113  label="Válec115"
  Angle = 360
  AttacherType = Attacher::AttachEngine3D
  Height = 1.5
  Radius = 16
FEATURE [Part::Cut] Cut043  label="Ring010"
  Base = -> Cylinder014005112
  Placement = pos=(0,0,5.5) rot=(0,0,1;0rad)
  Tool = -> Cylinder014005113
FEATURE [Part::MultiFuse] Fusion061  label="Ring zaklad Fin004"
  Shapes = -> [Cut045,Cut043,Cut046]
FEATURE [Part::MultiFuse] Fusion060  label="teloII003"
  Shapes = -> [Fusion061,Extrude004]
FEATURE [Part::Cylinder] Cylinder014005115  label="Unasec vrch006"
  Angle = 360
  AttacherType = Attacher::AttachEngine3D
  Height = 1.5
  Placement = pos=(0,0,5.5) rot=(0,0,1;0rad)
  Radius = 15.5
FEATURE [Part::Cut] Cut049  label="unasec vrch006"
  Base = -> Cylinder014005115
  Tool = -> Fusion066
FEATURE [Part::Cut] Cut048  label="Unasec Vrch zaklad006"
  Base = -> Cut049
  Tool = -> Fusion068
FEATURE [Part::Cylinder] Cylinder014005116  label="Válec117"
  Angle = 360
  AttacherType = Attacher::AttachEngine3D
  Height = 4
  Placement = pos=(0,0,7) rot=(0,0,1;0rad)
  Radius = 6.5
FEATURE [Part::MultiFuse] Fusion067  label="unasec vrhch 006"
  Shapes = -> [Cut048,Cut007_solid005,Cylinder014005116]
FEATURE [Part::Cut] Cut047  label="Unasec + Sun004"
  Base = -> Fusion067
  Tool = -> Cylinder014005117
FEATURE [App::Part] Part004
  Group = -> [Cut044,Cut050,Cylinder014005098,Cylinder014005100,Cylinder014005099,Cylinder014005101,Cylinder014005105,Cylinder014005108,Cylinder014005109,Screw_solid034,Cylinder014005104,Screw_solid038,Cylinder014005102,Screw_solid036,Fusion059,Fusion058,Fusion065,Fusion062,Fusion064,Cut008_solid014,Cut008_solid012,Cut008_solid013,Screw_solid033,Cylinder014005107,Cylinder014005103,Screw_solid037,Screw_solid035,+26 more]
  License = CC BY 3.0
  LicenseURL = http://creativecommons.org/licenses/by/3.0/
  Origin = -> Origin004
  Placement = pos=(0,0,31.5) rot=(0,0,1;0rad)
FEATURE [Part::Cylinder] Cylinder014005120  label="Válec121"
  Angle = 360
  AttacherType = Attacher::AttachEngine3D
  Height = 5.5
  Radius = 20
FEATURE [Part::Cut] Cut051  label="ring 006"
  Base = -> Cylinder014005120
  Tool = -> InvoluteGear013
FEATURE [Part::Cylinder] Cylinder014005123  label="Válec124"
  Angle = 360
  AttacherType = Attacher::AttachEngine3D
  Height = 1.5
  Radius = 16
FEATURE [Part::Cylinder] Cylinder014005127  label="Válec127"
  Angle = 360
  AttacherType = Attacher::AttachEngine3D
  Height = 18
  Radius = 2.6
FEATURE [Part::Cylinder] Cylinder014005124  label="Válec125"
  Angle = 360
  AttacherType = Attacher::AttachEngine3D
  Height = 1.5
  Radius = 20
FEATURE [Part::Cut] Cut053  label="Ring012"
  Base = -> Cylinder014005124
  Placement = pos=(0,0,-1.5) rot=(0,0,1;0rad)
  Tool = -> Cylinder014005123
FEATURE [Part::MultiFuse] Fusion076  label="Ring zaklad Fin005"
  Shapes = -> [Cut051,Cut054,Cut053]
FEATURE [Part::Cylinder] Cylinder014005125  label="Unasec vrch007"
  Angle = 360
  AttacherType = Attacher::AttachEngine3D
  Height = 1.5
  Placement = pos=(0,0,5.5) rot=(0,0,1;0rad)
  Radius = 15.5
FEATURE [Part::Cylinder] Cylinder014005133  label="unasec stred006"
  Angle = 360
  AttacherType = Attacher::AttachEngine3D
  Height = 7
  Placement = pos=(0,0,-1.5) rot=(0,0,1;0rad)
  Radius = 13.5
FEATURE [Part::Cylinder] Cylinder014005122  label="Válec123"
  Angle = 360
  AttacherType = Attacher::AttachEngine3D
  Height = 10
  Placement = pos=(10.5,0,0) rot=(0,0,1;0rad)
  Radius = 8
FEATURE [Part::Cylinder] Cylinder014005126  label="Válec126"
  Angle = 360
  AttacherType = Attacher::AttachEngine3D
  Height = 4
  Placement = pos=(0,0,7) rot=(0,0,1;0rad)
  Radius = 6.5
FEATURE [Part::Cylinder] Cylinder014005134  label="unasec spodek013"
  Angle = 360
  AttacherType = Attacher::AttachEngine3D
  Height = 1.5
  Placement = pos=(0,0,-1.5) rot=(0,0,1;0rad)
  Radius = 15.5
FEATURE [Part::MultiFuse] Fusion077
  Shapes = -> [Cylinder014005133,Cylinder014005134]
FEATURE [Part::Feature] Cylinder014005131  label="Válec131"
  Placement = pos=(0,0,0) rot=(0,0,1;4.18879rad)
  shape: bbox 16 x 16 x 10 mm, 3 faces (baked)
FEATURE [Part::Feature] Cylinder014005138  label="Válec136"
  Placement = pos=(0,0,0) rot=(0,0,1;2.0944rad)
  shape: bbox 16 x 16 x 10 mm, 3 faces (baked)
FEATURE [Part::Feature] Screw_solid044  label="M2x4-Screw (Solid)044"
  Placement = pos=(0,0,0) rot=(0,0,1;1.0472rad)
  shape: bbox 3.6 x 3.6 x 4 mm, 12 faces (baked)
FEATURE [Part::Feature] Screw_solid043  label="M2x4-Screw (Solid)043"
  Placement = pos=(0,0,0) rot=(0,0,-1;1.0472rad)
  shape: bbox 3.6 x 3.6 x 4 mm, 12 faces (baked)
FEATURE [Part::Feature] Screw_solid042  label="M2x4-Screw (Solid)042"
  Placement = pos=(0,0,0) rot=(0,0,1;3.14159rad)
  shape: bbox 3.6 x 3.6 x 4 mm, 12 faces (baked)
FEATURE [Part::Feature] Screw_solid047  label="M2x4-Screw (Solid)047"
  Placement = pos=(0,0,0) rot=(0,0,-1;1.0472rad)
  shape: bbox 3.6 x 3.6 x 4 mm, 12 faces (baked)
FEATURE [Part::Feature] Cylinder014005128  label="Válec128"
  Placement = pos=(0,0,0) rot=(0,0,1;2.0944rad)
  shape: bbox 5 x 5 x 7 mm, 3 faces (baked)
FEATURE [Part::Feature] Cylinder014005129  label="Válec129"
  shape: bbox 5 x 5 x 7 mm, 3 faces (baked)
FEATURE [Part::Feature] Cut008_solid017  label="Planet018"
  shape: bbox 12.9 x 13.1 x 5 mm, 57 faces (baked)
FEATURE [Part::Feature] Cut061001  label="SUN I Final"
  shape: bbox 24 x 24 x 12.25 mm, 99 faces (baked)
FEATURE [App::Part] Part001
  Group = -> [Cut008_solid,Cut008_solid001,Cut008_solid002,Cylinder010,Cylinder,Cylinder013,Fusion001,Fusion002,Cylinder014005006,Cylinder014005005,Cylinder014002,Cylinder014001,Cylinder014005004,Cylinder011,Cut004,Cut006,Screw_solid005,Screw_solid003,Screw_solid004,Fusion006,Fusion004,Fusion008,Cylinder014005034,Cylinder014005035,Cut007_solid001,Cut012,Cut011,Screw_solid007,Screw_solid008,Cylinder014005014,+29 more]
  License = CC BY 3.0
  LicenseURL = http://creativecommons.org/licenses/by/3.0/
  Origin = -> Origin001
FEATURE [Part::Feature] Screw_solid045  label="M2x4-Screw (Solid)045"
  Placement = pos=(0,0,0) rot=(0,0,1;3.14159rad)
  shape: bbox 3.6 x 3.6 x 4 mm, 12 faces (baked)
FEATURE [Part::Feature] Cylinder014005130  label="Válec130"
  Placement = pos=(0,0,0) rot=(0,0,1;4.18879rad)
  shape: bbox 5 x 5 x 7 mm, 3 faces (baked)
FEATURE [Part::Feature] Screw_solid046  label="M2x4-Screw (Solid)046"
  Placement = pos=(0,0,0) rot=(0,0,1;1.0472rad)
  shape: bbox 3.6 x 3.6 x 4 mm, 12 faces (baked)
FEATURE [Part::MultiFuse] Fusion085  label="srouby016"
  Placement = pos=(0,0,0.5) rot=(0,0,1;0rad)
  Shapes = -> [Screw_solid046,Screw_solid047,Screw_solid045]
FEATURE [Part::Feature] Screw_solid040  label="M2x4-Screw (Solid)040"
  Placement = pos=(0,0,0) rot=(0,0,1;3.14159rad)
  shape: bbox 3.6 x 3.6 x 4 mm, 12 faces (baked)
FEATURE [Part::Feature] Cylinder014005132  label="Válec132"
  Placement = pos=(0,0,0) rot=(0,0,1;4.18879rad)
  shape: bbox 5 x 5 x 7 mm, 3 faces (baked)
FEATURE [Part::MultiFuse] Fusion075
  Shapes = -> [Cylinder014005132,Cylinder014005118,Cylinder014005128]
FEATURE [Part::Feature] Cut008_solid015  label="Planet016"
  Placement = pos=(0,0,0) rot=(0,0,1;2.0944rad)
  shape: bbox 12.9 x 13.1 x 5 mm, 57 faces (baked)
FEATURE [Part::Feature] Screw_solid041  label="M2x4-Screw (Solid)041"
  Placement = pos=(0,0,0) rot=(0,0,-1;1.0472rad)
  shape: bbox 3.6 x 3.6 x 4 mm, 12 faces (baked)
FEATURE [Part::MultiFuse] Fusion073  label="srouby015"
  Shapes = -> [Screw_solid044,Screw_solid041,Screw_solid042]
FEATURE [Part::Feature] Cut008_solid016  label="Planet017"
  Placement = pos=(0,0,0) rot=(0,0,1;4.18879rad)
  shape: bbox 12.9 x 13.1 x 5 mm, 57 faces (baked)
FEATURE [Part::Feature] Cylinder014005137  label="Válec135"
  Placement = pos=(0,0,0) rot=(0,0,1;2.0944rad)
  shape: bbox 5 x 5 x 7 mm, 3 faces (baked)
FEATURE [Part::MultiFuse] Fusion072
  Shapes = -> [Cylinder014005130,Cylinder014005129,Cylinder014005137]
FEATURE [Part::Feature] Cylinder014005149  label="Válec146"
  Placement = pos=(0,0,0) rot=(0,0,1;2.0944rad)
  shape: bbox 5 x 5 x 7 mm, 3 faces (baked)
FEATURE [Part::Feature] Cylinder014005150  label="Válec147"
  shape: bbox 5 x 5 x 7 mm, 3 faces (baked)
FEATURE [Part::Feature] Screw_solid039  label="M2x4-Screw (Solid)039"
  Placement = pos=(0,0,0) rot=(0,0,1;1.0472rad)
  shape: bbox 3.6 x 3.6 x 4 mm, 12 faces (baked)
FEATURE [Part::MultiFuse] Fusion071  label="srouby014"
  Placement = pos=(0,0,0.5) rot=(0,0,1;0rad)
  Shapes = -> [Screw_solid039,Screw_solid043,Screw_solid040]
FEATURE [Part::Cut] Cut057  label="unasec vrch007"
  Base = -> Cylinder014005125
  Tool = -> Fusion071
FEATURE [Part::Feature] Cut005_solid001_cs006
  Placement = pos=(0,0,-11.25) rot=(0,0,1;0rad)
  shape: bbox 41 x 41 x 3e-07 mm, 0 faces, 0 solids (baked)
FEATURE [Part::Extrusion] Extrude005  label="box005"
  Base = -> Cut005_solid001_cs006
  Dir = (0,0,1)
  DirMode = 2
  FaceMakerClass = Part::FaceMakerBullseye
  LengthFwd = 10.5
  LengthRev = 0
  Placement = pos=(0,0,-3) rot=(0,0,1;0rad)
  Solid = true
  Symmetric = false
FEATURE [Part::MultiFuse] Fusion078  label="teloII004"
  Shapes = -> [Fusion076,Extrude005]
FEATURE [Part::Cylinder] Cylinder014005135  label="Válec133"
  Angle = 360
  AttacherType = Attacher::AttachEngine3D
  Height = 7
  Radius = 2.6
FEATURE [Part::MultiFuse] Fusion079
  Placement = pos=(0,0,1) rot=(0,0,1;0rad)
  Shapes = -> [Fusion075,Cylinder014005135]
FEATURE [Part::Cylinder] Cylinder014005136  label="Válec134"
  Angle = 360
  AttacherType = Attacher::AttachEngine3D
  Height = 10
  Placement = pos=(0,0,-3) rot=(0,0,1;0rad)
  Radius = 7
FEATURE [Part::MultiFuse] Fusion069
  Shapes = -> [Cylinder014005136,Cylinder014005122,Cylinder014005131,Cylinder014005138]
FEATURE [Part::Cut] Cut052  label="unasec spodek012"
  Base = -> Fusion077
  Tool = -> Fusion069
FEATURE [Part::Cut] Cut056  label="Uasec spodek006"
  Base = -> Cut052
  Tool = -> Fusion073
FEATURE [Part::MultiFuse] Fusion074  label="Unasec spdek final005"
  Shapes = -> [Cut056,Fusion072]
FEATURE [Part::Cut] Cut058  label="Unasec Vrch zaklad007"
  Base = -> Cut057
  Tool = -> Fusion079
FEATURE [Part::MultiFuse] Fusion070  label="unasec vrhch 007"
  Shapes = -> [Cut058,Cut007_solid006,Cylinder014005126]
FEATURE [Part::Cut] Cut055  label="Unasec + Sun005 old"
  Base = -> Fusion070
  Tool = -> Cylinder014005127
FEATURE [Part::Cylinder] Cylinder014005148  label="Válec145"
  Angle = 360
  AttacherType = Attacher::AttachEngine3D
  Height = 22
  Radius = 2.6
FEATURE [Part::MultiFuse] Fusion090
  Shapes = -> [Cylinder014005148,Extrude007]
FEATURE [Part::Cylinder] Cylinder014005147  label="Válec144"
  Angle = 360
  AttacherType = Attacher::AttachEngine3D
  Height = 6
  Placement = pos=(0,0,7) rot=(0,0,1;0rad)
  Radius = 6.5
FEATURE [Part::Cylinder] Cylinder014005145  label="Válec143"
  Angle = 360
  AttacherType = Attacher::AttachEngine3D
  Height = 7
  Radius = 2.6
FEATURE [Part::Cylinder] Cylinder014005146  label="Unasec vrch008"
  Angle = 360
  AttacherType = Attacher::AttachEngine3D
  Height = 1.5
  Placement = pos=(0,0,5.5) rot=(0,0,1;0rad)
  Radius = 15.5
FEATURE [Part::Cut] Cut061004  label="unasec vrch008"
  Base = -> Cylinder014005146
  Tool = -> Fusion085
FEATURE [Part::Feature] Cylinder014005151  label="Válec148"
  Placement = pos=(0,0,0) rot=(0,0,1;4.18879rad)
  shape: bbox 5 x 5 x 7 mm, 3 faces (baked)
FEATURE [Part::MultiFuse] Fusion087
  Shapes = -> [Cylinder014005151,Cylinder014005150,Cylinder014005149]
FEATURE [Part::MultiFuse] Fusion088
  Placement = pos=(0,0,1) rot=(0,0,1;0rad)
  Shapes = -> [Fusion087,Cylinder014005145]
FEATURE [Part::Cut] Cut061003  label="Unasec Vrch zaklad008"
  Base = -> Cut061004
  Tool = -> Fusion088
FEATURE [Part::MultiFuse] Fusion089
  Shapes = -> [Cut061003,Cylinder014005147,Extrude006]
FEATURE [Part::Cut] Cut061005  label="unasec top"
  Base = -> Fusion089
  Tool = -> Fusion090
FEATURE [App::Part] Part005
  Group = -> [Cut052,Cut056,Cylinder014005136,Cylinder014005134,Cylinder014005133,Cylinder014005122,Cylinder014005131,Cylinder014005137,Cylinder014005138,Screw_solid042,Cylinder014005129,Screw_solid044,Cylinder014005130,Screw_solid041,Fusion069,Fusion077,Fusion073,Fusion072,Fusion074,Cut008_solid017,Cut008_solid015,Cut008_solid016,Screw_solid039,Cylinder014005118,Cylinder014005128,Screw_solid043,Screw_solid040,+48 more]
  License = CC BY 3.0
  LicenseURL = http://creativecommons.org/licenses/by/3.0/
  Origin = -> Origin005
  Placement = pos=(0,0,42) rot=(0,0,1;0rad)
FEATURE [App::Part] Part007  label="GearBOX 1024:1a"
  Group = -> [Part001,Part,Part002,Part004,Part005]
  License = CC BY 3.0
  LicenseURL = http://creativecommons.org/licenses/by/3.0/
  Origin = -> Origin007
FEATURE [Part::Box] Box009  label="Krychle008"
  AttacherType = Attacher::AttachEngine3D
  Height = 40
  Length = 41
  Placement = pos=(-20.5,-20.5,0) rot=(0,0,1;0rad)
  Width = 41
FEATURE [Part::Cylinder] Cylinder003  label="Válec003"
  Angle = 360
  AttacherType = Attacher::AttachEngine3D
  Height = 50
  Placement = pos=(-15.5,15.5,0) rot=(0,0,1;0rad)
  Radius = 1.6
FEATURE [Part::Cylinder] Cylinder002  label="Válec002"
  Angle = 360
  AttacherType = Attacher::AttachEngine3D
  Height = 50
  Placement = pos=(15.5,15.5,0) rot=(0,0,1;0rad)
  Radius = 1.6
FEATURE [Part::Cylinder] Cylinder014005153  label="Válec150"
  Angle = 360
  AttacherType = Attacher::AttachEngine3D
  Height = 50
  Placement = pos=(-15.5,-15.5,0) rot=(0,0,1;0rad)
  Radius = 1.6
FEATURE [Part::Cylinder] Cylinder004  label="Válec004"
  Angle = 360
  AttacherType = Attacher::AttachEngine3D
  Height = 50
  Placement = pos=(15.5,-15.5,0) rot=(0,0,1;0rad)
  Radius = 1.6
FEATURE [Part::MultiFuse] Fusion091  label="diry"
  Shapes = -> [Cylinder003,Cylinder002,Cylinder014005153,Cylinder004]
FEATURE [Part::Chamfer] Chamfer
  Base = -> Box009
  Edges = 4 edges r=5: [Edge1,Edge3,Edge5,Edge7]
FEATURE [Part::Cut] Cut061006
  Base = -> Chamfer
  Tool = -> Fusion091
FEATURE [App::Part] Part008  label="NEAM17  motor- 40mm"
  Group = -> [Chamfer,Fusion091,Box009,Cylinder003,Cylinder002,Cylinder014005153,Cylinder004,Cut061006]
  License = CC BY 3.0
  LicenseURL = http://creativecommons.org/licenses/by/3.0/
  Origin = -> Origin008
  Placement = pos=(0,0,-51.5) rot=(0,0,1;0rad)
FEATURE [Part::Box] Box010  label="Krychle009"
  AttacherType = Attacher::AttachEngine3D
  Height = 10
  Length = 43
  Placement = pos=(-21.5,-20.5,0) rot=(0,0,1;0rad)
  Width = 42
FEATURE [Part::Chamfer] Chamfer001
  Base = -> Box010
  Edges = 2 edges r=5: [Edge1,Edge5]
FEATURE [Part::Cylinder] Cylinder014005154  label="Válec151"
  Angle = 360
  AttacherType = Attacher::AttachEngine3D
  Height = 50
  Placement = pos=(-15.5,15.5,0) rot=(0,0,1;0rad)
  Radius = 1.6
FEATURE [Part::Cylinder] Cylinder014005155  label="Válec152"
  Angle = 360
  AttacherType = Attacher::AttachEngine3D
  Height = 50
  Placement = pos=(15.5,15.5,0) rot=(0,0,1;0rad)
  Radius = 1.6
FEATURE [Part::Cylinder] Cylinder014005156  label="dira stred001"
  Angle = 360
  AttacherType = Attacher::AttachEngine3D
  Height = 50
  Radius = 13
FEATURE [Part::Cylinder] Cylinder014005157  label="Válec153"
  Angle = 360
  AttacherType = Attacher::AttachEngine3D
  Height = 50
  Placement = pos=(-15.5,-15.5,0) rot=(0,0,1;0rad)
  Radius = 1.6
FEATURE [Part::Cylinder] Cylinder014005158  label="Válec154"
  Angle = 360
  AttacherType = Attacher::AttachEngine3D
  Height = 50
  Placement = pos=(15.5,-15.5,0) rot=(0,0,1;0rad)
  Radius = 1.6
FEATURE [Part::MultiFuse] Fusion092  label="diry001"
  Shapes = -> [Cylinder014005154,Cylinder014005155,Cylinder014005156,Cylinder014005157,Cylinder014005158]
FEATURE [Part::Cut] Cut061007  label="Horni ucjyt"
  Base = -> Chamfer001
  Placement = pos=(0,0,49.5) rot=(0,0,1;0rad)
  Tool = -> Fusion092
FEATURE [Part::Cylinder] Cylinder014005159  label="Válec155"
  Angle = 360
  AttacherType = Attacher::AttachEngine3D
  Height = 50
  Placement = pos=(15.5,-15.5,0) rot=(0,0,1;0rad)
  Radius = 1.6
FEATURE [Part::Cylinder] Cylinder014005160  label="Válec156"
  Angle = 360
  AttacherType = Attacher::AttachEngine3D
  Height = 50
  Placement = pos=(-15.5,-15.5,0) rot=(0,0,1;0rad)
  Radius = 1.6
FEATURE [Part::Box] Box011  label="Krychle010"
  AttacherType = Attacher::AttachEngine3D
  Height = 0.45
  Length = 41
  Placement = pos=(-20.5,-20.5,0) rot=(0,0,1;0rad)
  Width = 41
FEATURE [Part::Chamfer] Chamfer002
  Base = -> Box011
  Edges = 4 edges r=5: [Edge1,Edge3,Edge5,Edge7]
FEATURE [Part::Cylinder] Cylinder014005161  label="Válec157"
  Angle = 360
  AttacherType = Attacher::AttachEngine3D
  Height = 50
  Placement = pos=(-15.5,15.5,0) rot=(0,0,1;0rad)
  Radius = 1.6
FEATURE [Part::Cylinder] Cylinder014005162  label="dira stred002"
  Angle = 360
  AttacherType = Attacher::AttachEngine3D
  Height = 50
  Radius = 18
FEATURE [Part::Cylinder] Cylinder014005163  label="Válec158"
  Angle = 360
  AttacherType = Attacher::AttachEngine3D
  Height = 50
  Placement = pos=(15.5,15.5,0) rot=(0,0,1;0rad)
  Radius = 1.6
FEATURE [Part::MultiFuse] Fusion093  label="diry002"
  Shapes = -> [Cylinder014005161,Cylinder014005163,Cylinder014005162,Cylinder014005160,Cylinder014005159]
FEATURE [Part::Cut] Cut061008
  Base = -> Chamfer002
  Tool = -> Fusion093
FEATURE [Part::Box] Box  label="deska"
  AttacherType = Attacher::AttachEngine3D
  Height = 111
  Length = 43
  Placement = pos=(-21.5,21.5,-51.5) rot=(0,0,1;0rad)
  Width = 10
FEATURE [Part::Box] Box012  label="deska001"
  AttacherType = Attacher::AttachEngine3D
  Height = 111
  Length = 9
  Placement = pos=(-30.5,-14.5,-51.5) rot=(0,0,1;0rad)
  Width = 46
FEATURE [Part::Box] Box013  label="deska002"
  AttacherType = Attacher::AttachEngine3D
  Height = 111
  Length = 9
  Placement = pos=(21.5,-14.5,-51.5) rot=(0,0,1;0rad)
  Width = 46
FEATURE [Part::MultiFuse] Fusion094  label="motor drazak"
  Shapes = -> [Cut061007,Box013,Box,Box012]
FEATURE [Part::Box] Box014  label="Krychle"
  AttacherType = Attacher::AttachEngine3D
  Height = 112
  Length = 38
  Placement = pos=(-19,32,-52) rot=(0,0,1;0rad)
  Width = 10
FEATURE [Part::Box] Box015  label="Krychle011"
  AttacherType = Attacher::AttachEngine3D
  Height = 112
  Length = 38
  Placement = pos=(-19,34,-52) rot=(0,0,1;0rad)
  Width = 6
FEATURE [Part::Cut] Cut061009
  Base = -> Box014
  Tool = -> Box015
FEATURE [Sketcher::SketchObject] Sketch
  MapMode = 5
  Placement = pos=(0,0,60) rot=(0,0,1;0rad)
  sketch-geometry (6):
    g0: LineSegment StartX=-18.9734 StartY=34.0308 StartZ=0 EndX=-16.0253 EndY=36.9748 EndZ=0
    g1: LineSegment StartX=18.996 StartY=34.0308 StartZ=0 EndX=16.044 EndY=36.9748 EndZ=0
    g2: LineSegment StartX=18.996 StartY=34.0308 StartZ=0 EndX=-18.9734 EndY=34.0308 EndZ=0
    g3: LineSegment StartX=-18.9734 StartY=40.0311 StartZ=0 EndX=-16.0253 EndY=36.9748 EndZ=0
    g4: LineSegment StartX=16.044 StartY=36.9748 StartZ=0 EndX=18.9109 EndY=40.0311 EndZ=0
    g5: LineSegment StartX=-18.9734 StartY=40.0311 StartZ=0 EndX=18.9109 EndY=40.0311 EndZ=0
  constraints (7):
    c: Coincident(g2,g1)
    c: Coincident(g2,g0)
    c: Horizontal(g2)
    c: Coincident(g3,g0)
    c: Coincident(g5,g3)
    c: Coincident(g5,g4)
    c: Horizontal(g5)
FEATURE [Part::Extrusion] Extrude009
  Base = -> Sketch
  Dir = (0,0,1)
  DirMode = 2
  FaceMakerClass = Part::FaceMakerBullseye
  LengthFwd = -112
  LengthRev = 0
  Solid = true
  Symmetric = false
FEATURE [Part::MultiFuse] Fusion095  label="Arca plate base"
  Placement = pos=(0,-0.5,0) rot=(0,0,1;0rad)
  Shapes = -> [Extrude009,Cut061009]
FEATURE [Part::Box] Box016  label="Krychle012"
  AttacherType = Attacher::AttachEngine3D
  Height = 112
  Length = 38
  Placement = pos=(-19,32,-52) rot=(0,0,1;0rad)
  Width = 10
FEATURE [Part::Box] Box017  label="Krychle013"
  AttacherType = Attacher::AttachEngine3D
  Height = 112
  Length = 38
  Placement = pos=(-19,34,-52) rot=(0,0,1;0rad)
  Width = 6
FEATURE [Part::Cut] Cut061010
  Base = -> Box016
  Tool = -> Box017
FEATURE [Sketcher::SketchObject] Sketch002
  MapMode = 5
  Placement = pos=(0,0,60) rot=(0,0,1;0rad)
  sketch-geometry (6):
    g0: LineSegment StartX=-18.9734 StartY=34.0308 StartZ=0 EndX=-16.0253 EndY=36.9748 EndZ=0
    g1: LineSegment StartX=18.996 StartY=34.0308 StartZ=0 EndX=16.044 EndY=36.9748 EndZ=0
    g2: LineSegment StartX=18.996 StartY=34.0308 StartZ=0 EndX=-18.9734 EndY=34.0308 EndZ=0
    g3: LineSegment StartX=-18.9734 StartY=40.0311 StartZ=0 EndX=-16.0253 EndY=36.9748 EndZ=0
    g4: LineSegment StartX=16.044 StartY=36.9748 StartZ=0 EndX=18.9109 EndY=40.0311 EndZ=0
    g5: LineSegment StartX=-18.9734 StartY=40.0311 StartZ=0 EndX=18.9109 EndY=40.0311 EndZ=0
  constraints (7):
    c: Coincident(g2,g1)
    c: Coincident(g2,g0)
    c: Horizontal(g2)
    c: Coincident(g3,g0)
    c: Coincident(g5,g3)
    c: Coincident(g5,g4)
    c: Horizontal(g5)
FEATURE [Part::Extrusion] Extrude010
  Base = -> Sketch002
  Dir = (0,0,1)
  DirMode = 2
  FaceMakerClass = Part::FaceMakerBullseye
  LengthFwd = -112
  LengthRev = 0
  Solid = true
  Symmetric = false
FEATURE [Part::MultiFuse] Fusion096  label="Arca plate base001"
  Placement = pos=(0,-0.5,0) rot=(0,0,1;0rad)
  Shapes = -> [Extrude010,Cut061010]
FEATURE [Part::Cylinder] Cylinder014005164  label="DIRA8,2"
  Angle = 360
  AttacherType = Attacher::AttachEngine3D
  Height = 200
  Placement = pos=(0,29,-100) rot=(0,0,1;0rad)
  Radius = 4.2
FEATURE [Part::Cylinder] Cylinder014005165  label="Válec160"
  Angle = 360
  AttacherType = Attacher::AttachEngine3D
  Height = 10
  Placement = pos=(0,43,54.5) rot=(1,0,0;1.5708rad)
  Radius = 4
FEATURE [Part::Cylinder] Cylinder014005166  label="Válec161"
  Angle = 360
  AttacherType = Attacher::AttachEngine3D
  Height = 10
  Placement = pos=(0,43,-47) rot=(1,0,0;1.5708rad)
  Radius = 4
FEATURE [Part::MultiFuse] Fusion098  label="drzak s arca"
  Shapes = -> [Fusion094,Fusion096,Cylinder014005165,Cylinder014005166]
FEATURE [Part::Cylinder] Cylinder014005167  label="Válec162"
  Angle = 360
  AttacherType = Attacher::AttachEngine3D
  Height = 65
  Placement = pos=(-32,0,0) rot=(0,1,0;1.5708rad)
  Radius = 1.35
FEATURE [Part::Cylinder] Cylinder014005168  label="Válec163"
  Angle = 360
  AttacherType = Attacher::AttachEngine3D
  Height = 65
  Placement = pos=(-32,0,42) rot=(0,1,0;1.5708rad)
  Radius = 1.35
FEATURE [Part::Cylinder] Cylinder014005169  label="Válec164"
  Angle = 360
  AttacherType = Attacher::AttachEngine3D
  Height = 65
  Placement = pos=(-32,0,-27) rot=(0,1,0;1.5708rad)
  Radius = 1.35
FEATURE [Part::Box] Box024  label="Krychle017"
  AttacherType = Attacher::AttachEngine3D
  Height = 112
  Length = 38
  Placement = pos=(-19,32,-52) rot=(0,0,1;0rad)
  Width = 10
FEATURE [Part::Box] Box025  label="Krychle018"
  AttacherType = Attacher::AttachEngine3D
  Height = 112
  Length = 38
  Placement = pos=(-19,34,-52) rot=(0,0,1;0rad)
  Width = 6
FEATURE [Part::Cut] Cut061015
  Base = -> Box024
  Tool = -> Box025
FEATURE [Sketcher::SketchObject] Sketch004
  MapMode = 5
  Placement = pos=(0,0,60) rot=(0,0,1;0rad)
  sketch-geometry (6):
    g0: LineSegment StartX=-18.9734 StartY=34.0308 StartZ=0 EndX=-16.0253 EndY=36.9748 EndZ=0
    g1: LineSegment StartX=18.996 StartY=34.0308 StartZ=0 EndX=16.044 EndY=36.9748 EndZ=0
    g2: LineSegment StartX=18.996 StartY=34.0308 StartZ=0 EndX=-18.9734 EndY=34.0308 EndZ=0
    g3: LineSegment StartX=-18.9734 StartY=40.0311 StartZ=0 EndX=-16.0253 EndY=36.9748 EndZ=0
    g4: LineSegment StartX=16.044 StartY=36.9748 StartZ=0 EndX=18.9109 EndY=40.0311 EndZ=0
    g5: LineSegment StartX=-18.9734 StartY=40.0311 StartZ=0 EndX=18.9109 EndY=40.0311 EndZ=0
  constraints (7):
    c: Coincident(g2,g1)
    c: Coincident(g2,g0)
    c: Horizontal(g2)
    c: Coincident(g3,g0)
    c: Coincident(g5,g3)
    c: Coincident(g5,g4)
    c: Horizontal(g5)
FEATURE [Part::Extrusion] Extrude012
  Base = -> Sketch004
  Dir = (0,0,1)
  DirMode = 2
  FaceMakerClass = Part::FaceMakerBullseye
  LengthFwd = -112
  LengthRev = 0
  Solid = true
  Symmetric = false
FEATURE [Part::MultiFuse] Fusion108  label="Arca plate base003"
  Placement = pos=(0,-6.5,115.5) rot=(-1,0,0;1.5708rad)
  Shapes = -> [Extrude012,Cut061015]
FEATURE [Part::Box] Box026  label="Krychle019"
  AttacherType = Attacher::AttachEngine3D
  Height = 15
  Length = 50
  Placement = pos=(-25,-25,64) rot=(0,0,1;0rad)
  Width = 50
FEATURE [Part::Cut] Cut061016  label="Arca sw 1"
  Base = -> Box026
  Tool = -> Fusion108
FEATURE [Part::Box] Box027  label="Krychle020"
  AttacherType = Attacher::AttachEngine3D
  Height = 15
  Length = 2
  Placement = pos=(-15.5,-26,61) rot=(0,0,1;0rad)
  Width = 52
FEATURE [Part::Cut] Cut061017
  Base = -> Cut061016
  Tool = -> Box027
FEATURE [Sketcher::SketchObject] Sketch005
  MapMode = 45
  Placement = pos=(44.88,21.011,5.40003) rot=(0.707106,0.001666,0.707106;3.13826rad)
  sketch-geometry (7):
    g0: LineSegment StartX=5.21891 StartY=0.0364138 StartZ=0 EndX=2.62121 EndY=4.46293 EndZ=0
    g1: LineSegment StartX=2.62121 StartY=4.46293 StartZ=0 EndX=-2.51111 EndY=4.42651 EndZ=0
    g2: LineSegment StartX=-2.51111 StartY=4.42651 StartZ=0 EndX=-5.04574 EndY=-0.0364138 EndZ=0
    g3: LineSegment StartX=-5.04574 StartY=-0.0364138 StartZ=0 EndX=-2.44804 EndY=-4.46293 EndZ=0
    g4: LineSegment StartX=-2.44804 StartY=-4.46293 StartZ=0 EndX=2.68428 EndY=-4.42651 EndZ=0
    g5: LineSegment StartX=2.68428 StartY=-4.42651 StartZ=0 EndX=5.21891 EndY=0.0364138 EndZ=0
    g6: Circle [constr] CenterX=0.0865834 CenterY=0 CenterZ=0 NormalX=0 NormalY=0 NormalZ=1 AngleXU=0 Radius=5.13245
  constraints (14):
    c: Coincident(g0,g1)
    c: Coincident(g1,g2)
    c: Coincident(g2,g3)
    c: Coincident(g3,g4)
    c: Coincident(g4,g5)
    c: Coincident(g5,g0)
    c: Equal(g0, g1-g5) x5
    c: PointOnObject(g0,g6)
    c: PointOnObject(g1,g6)
    c: PointOnObject(g2,g6)
    c: PointOnObject(g3,g6)
    c: PointOnObject(g4,g6)
    c: PointOnObject(g5,g6)
    c: PointOnObject(g6,g-1)
FEATURE [Part::RegularPolygon] RegularPolygon001  label="Pravidelný n-úhelník001"
  AttacherType = Attacher::AttachEngine3D
  Circumradius = 6
  Polygon = 6
FEATURE [Part::Extrusion] Extrude013
  Base = -> Sketch005
  Dir = (1,0,0)
  DirMode = 2
  FaceMakerClass = Part::FaceMakerBullseye
  LengthFwd = 5
  LengthRev = 0
  Placement = pos=(0,0,0.25) rot=(0,0,1;0rad)
  Solid = true
  Symmetric = false
FEATURE [Part::Extrusion] Extrude014
  Base = -> RegularPolygon001
  Dir = (0,0,1)
  DirMode = 2
  FaceMakerClass = Part::FaceMakerBullseye
  LengthFwd = 8
  LengthRev = 0
  Placement = pos=(0,0,13) rot=(0,0,1;0rad)
  Solid = true
  Symmetric = false
FEATURE [Part::Feature] Screw_solid048  label="M2x4-Screw (Solid)048"
  Placement = pos=(0,0,0) rot=(0,0,1;3.14159rad)
  shape: bbox 3.6 x 3.6 x 4 mm, 12 faces (baked)
FEATURE [Part::Feature] Screw_solid049  label="M2x4-Screw (Solid)049"
  Placement = pos=(0,0,0) rot=(0,0,-1;1.0472rad)
  shape: bbox 3.6 x 3.6 x 4 mm, 12 faces (baked)
FEATURE [Part::Cylinder] Cylinder014005181  label="Válec175"
  Angle = 360
  AttacherType = Attacher::AttachEngine3D
  Height = 6
  Placement = pos=(0,0,7) rot=(0,0,1;0rad)
  Radius = 6.5
FEATURE [Part::Cylinder] Cylinder014005182  label="Válec176"
  Angle = 360
  AttacherType = Attacher::AttachEngine3D
  Height = 22
  Radius = 2.6
FEATURE [Part::MultiFuse] Fusion110
  Shapes = -> [Cylinder014005182,Extrude013]
FEATURE [Part::Cylinder] Cylinder014005183  label="Válec177"
  Angle = 360
  AttacherType = Attacher::AttachEngine3D
  Height = 7
  Radius = 2.6
FEATURE [Part::Cylinder] Cylinder014005184  label="Unasec vrch009"
  Angle = 360
  AttacherType = Attacher::AttachEngine3D
  Height = 1.5
  Placement = pos=(0,0,5.5) rot=(0,0,1;0rad)
  Radius = 15.5
FEATURE [Part::Feature] Cylinder014005185  label="Válec178"
  shape: bbox 5 x 5 x 7 mm, 3 faces (baked)
FEATURE [Part::Feature] Cylinder014005186  label="Válec179"
  Placement = pos=(0,0,0) rot=(0,0,1;2.0944rad)
  shape: bbox 5 x 5 x 7 mm, 3 faces (baked)
FEATURE [Part::Feature] Screw_solid050  label="M2x4-Screw (Solid)050"
  Placement = pos=(0,0,0) rot=(0,0,1;1.0472rad)
  shape: bbox 3.6 x 3.6 x 4 mm, 12 faces (baked)
FEATURE [Part::MultiFuse] Fusion112  label="srouby017"
  Placement = pos=(0,0,0.5) rot=(0,0,1;0rad)
  Shapes = -> [Screw_solid050,Screw_solid049,Screw_solid048]
FEATURE [Part::Cut] Cut061020  label="unasec vrch009"
  Base = -> Cylinder014005184
  Tool = -> Fusion112
FEATURE [Part::Feature] Cylinder014005187  label="Válec180"
  Placement = pos=(0,0,0) rot=(0,0,1;4.18879rad)
  shape: bbox 5 x 5 x 7 mm, 3 faces (baked)
FEATURE [Part::MultiFuse] Fusion109
  Shapes = -> [Cylinder014005187,Cylinder014005185,Cylinder014005186]
FEATURE [Part::MultiFuse] Fusion113
  Placement = pos=(0,0,1) rot=(0,0,1;0rad)
  Shapes = -> [Fusion109,Cylinder014005183]
FEATURE [Part::Cut] Cut061019  label="Unasec Vrch zaklad009"
  Base = -> Cut061020
  Tool = -> Fusion113
FEATURE [Part::MultiFuse] Fusion111
  Shapes = -> [Cut061019,Cylinder014005181,Extrude014]
FEATURE [Part::Cut] Cut061018  label="unasec top001"
  Base = -> Fusion111
  Placement = pos=(0,0,42) rot=(0,0,1;0rad)
  Tool = -> Fusion110
FEATURE [Part::Cylinder] Cylinder014005188  label="Válec181"
  Angle = 360
  AttacherType = Attacher::AttachEngine3D
  Height = 10
  Placement = pos=(0,0,55) rot=(0,0,1;0rad)
  Radius = 12.5
FEATURE [Part::Cylinder] Cylinder014005189  label="Válec182"
  Angle = 360
  AttacherType = Attacher::AttachEngine3D
  Height = 55
  Placement = pos=(0,0,35) rot=(0,0,1;0rad)
  Radius = 2.7
FEATURE [Part::Cylinder] Cylinder014005190  label="Válec183"
  Angle = 360
  AttacherType = Attacher::AttachEngine3D
  Height = 8
  Placement = pos=(0,0,66) rot=(0,0,1;0rad)
  Radius = 4.5
FEATURE [Part::MultiFuse] Fusion114
  Shapes = -> [Cylinder014005188,Cut061017]
FEATURE [Part::MultiFuse] Fusion115
  Shapes = -> [Cylinder014005189,Cut061018,Cylinder014005190]
FEATURE [Part::Cut] Cut061021
  Base = -> Fusion114
  Tool = -> Fusion115
FEATURE [Part::Cylinder] Cylinder014005191  label="Válec184"
  Angle = 360
  AttacherType = Attacher::AttachEngine3D
  Height = 60
  Placement = pos=(-30,17,69) rot=(0,1,0;1.5708rad)
  Radius = 2.7
FEATURE [Part::Cylinder] Cylinder014005192  label="Válec185"
  Angle = 360
  AttacherType = Attacher::AttachEngine3D
  Height = 60
  Placement = pos=(-30,-17,69) rot=(0,1,0;1.5708rad)
  Radius = 2.7
FEATURE [Part::FeaturePython] Nut005  label="M2-Nut"  # Fasteners workbench fastener (typed FeaturePython)
  Placement = pos=(22,17,69) rot=(0,1,0;1.5708rad)
  diameter = 2
  invert = false
  matchOuter = false
  offset = 0
  thread = false
  type = 1
FEATURE [Part::FeaturePython] Nut006  label="M2-Nut001"  # Fasteners workbench fastener (typed FeaturePython)
  Placement = pos=(22,-17,69) rot=(0,1,0;1.5708rad)
  diameter = 2
  invert = false
  matchOuter = false
  offset = 0
  thread = false
  type = 1
FEATURE [Part::MultiFuse] Fusion116
  Shapes = -> [Cylinder014005191,Cylinder014005192,Nut005,Nut006]
FEATURE [Part::Cut] Cut061022
  Base = -> Cut061021
  Tool = -> Fusion116
FEATURE [Part::Cylinder] Cylinder014005324  label="Válec300"
  Angle = 360
  AttacherType = Attacher::AttachEngine3D
  Height = 2.5
  Placement = pos=(0,-12,71) rot=(0,0,1;0rad)
  Radius = 6
FEATURE [Part::Box] Box033  label="Krychle026"
  AttacherType = Attacher::AttachEngine3D
  Height = 2.5
  Length = 12
  Placement = pos=(-6,-25,71) rot=(0,0,1;0rad)
  Width = 13
FEATURE [Part::MultiFuse] Fusion188
  Placement = pos=(0,-4,1) rot=(0,0,1;0rad)
  Shapes = -> [Box033,Cylinder014005324]
FEATURE [Part::Cylinder] Cylinder014005325  label="Válec301"
  Angle = 360
  AttacherType = Attacher::AttachEngine3D
  Height = 2.5
  Placement = pos=(0,-12,71) rot=(0,0,1;0rad)
  Radius = 6
FEATURE [Part::Box] Box034  label="Krychle027"
  AttacherType = Attacher::AttachEngine3D
  Height = 2.5
  Length = 12
  Placement = pos=(-6,-25,71) rot=(0,0,1;0rad)
  Width = 13
FEATURE [Part::MultiFuse] Fusion189
  Placement = pos=(0,4,1) rot=(0,0,1;3.14159rad)
  Shapes = -> [Box034,Cylinder014005325]
FEATURE [Part::MultiFuse] Fusion190
  Shapes = -> [Fusion188,Fusion189]
FEATURE [Part::Cut] Cut061076  label="Swis Arca1"
  Base = -> Cut061022
  Tool = -> Fusion190
FEATURE [Part::RegularPolygon] RegularPolygon004  label="Pravidelný n-úhelník004"
  AttacherType = Attacher::AttachEngine3D
  Circumradius = 6
  Polygon = 6
FEATURE [Part::Extrusion] Extrude027
  Base = -> RegularPolygon004
  Dir = (0,0,1)
  DirMode = 2
  FaceMakerClass = Part::FaceMakerBullseye
  LengthFwd = 8
  LengthRev = 0
  Placement = pos=(0,0,13) rot=(0,0,1;0rad)
  Solid = true
  Symmetric = false
FEATURE [Part::FeaturePython] Nut007  label="M4-Nut002"  # Fasteners workbench fastener (typed FeaturePython)
  Placement = pos=(22,17,69) rot=(0,1,0;1.5708rad)
  diameter = 6
  invert = false
  matchOuter = false
  offset = 0
  thread = false
  type = 1
FEATURE [Part::FeaturePython] Nut008  label="M4-Nut003"  # Fasteners workbench fastener (typed FeaturePython)
  Placement = pos=(22,-17,69) rot=(0,1,0;1.5708rad)
  diameter = 6
  invert = false
  matchOuter = false
  offset = 0
  thread = false
  type = 1
FEATURE [Sketcher::SketchObject] Sketch009
  MapMode = 5
  Placement = pos=(0,0,60) rot=(0,0,1;0rad)
  sketch-geometry (6):
    g0: LineSegment StartX=-18.9734 StartY=34.0308 StartZ=0 EndX=-16.0253 EndY=36.9748 EndZ=0
    g1: LineSegment StartX=18.996 StartY=34.0308 StartZ=0 EndX=16.044 EndY=36.9748 EndZ=0
    g2: LineSegment StartX=18.996 StartY=34.0308 StartZ=0 EndX=-18.9734 EndY=34.0308 EndZ=0
    g3: LineSegment StartX=-18.9734 StartY=40.0311 StartZ=0 EndX=-16.0253 EndY=36.9748 EndZ=0
    g4: LineSegment StartX=16.044 StartY=36.9748 StartZ=0 EndX=18.9109 EndY=40.0311 EndZ=0
    g5: LineSegment StartX=-18.9734 StartY=40.0311 StartZ=0 EndX=18.9109 EndY=40.0311 EndZ=0
  constraints (7):
    c: Coincident(g2,g1)
    c: Coincident(g2,g0)
    c: Horizontal(g2)
    c: Coincident(g3,g0)
    c: Coincident(g5,g3)
    c: Coincident(g5,g4)
    c: Horizontal(g5)
FEATURE [Part::Extrusion] Extrude025
  Base = -> Sketch009
  Dir = (0,0,1)
  DirMode = 2
  FaceMakerClass = Part::FaceMakerBullseye
  LengthFwd = -112
  LengthRev = 0
  Solid = true
  Symmetric = false
FEATURE [Sketcher::SketchObject] Sketch010
  MapMode = 45
  Placement = pos=(44.88,21.011,5.40003) rot=(0.707106,0.001666,0.707106;3.13826rad)
  sketch-geometry (7):
    g0: LineSegment StartX=5.21891 StartY=0.0364138 StartZ=0 EndX=2.62121 EndY=4.46293 EndZ=0
    g1: LineSegment StartX=2.62121 StartY=4.46293 StartZ=0 EndX=-2.51111 EndY=4.42651 EndZ=0
    g2: LineSegment StartX=-2.51111 StartY=4.42651 StartZ=0 EndX=-5.04574 EndY=-0.0364138 EndZ=0
    g3: LineSegment StartX=-5.04574 StartY=-0.0364138 StartZ=0 EndX=-2.44804 EndY=-4.46293 EndZ=0
    g4: LineSegment StartX=-2.44804 StartY=-4.46293 StartZ=0 EndX=2.68428 EndY=-4.42651 EndZ=0
    g5: LineSegment StartX=2.68428 StartY=-4.42651 StartZ=0 EndX=5.21891 EndY=0.0364138 EndZ=0
    g6: Circle [constr] CenterX=0.0865834 CenterY=0 CenterZ=0 NormalX=0 NormalY=0 NormalZ=1 AngleXU=0 Radius=5.13245
  constraints (14):
    c: Coincident(g0,g1)
    c: Coincident(g1,g2)
    c: Coincident(g2,g3)
    c: Coincident(g3,g4)
    c: Coincident(g4,g5)
    c: Coincident(g5,g0)
    c: Equal(g0, g1-g5) x5
    c: PointOnObject(g0,g6)
    c: PointOnObject(g1,g6)
    c: PointOnObject(g2,g6)
    c: PointOnObject(g3,g6)
    c: PointOnObject(g4,g6)
    c: PointOnObject(g5,g6)
    c: PointOnObject(g6,g-1)
FEATURE [Part::Extrusion] Extrude026
  Base = -> Sketch010
  Dir = (1,0,0)
  DirMode = 2
  FaceMakerClass = Part::FaceMakerBullseye
  LengthFwd = 5
  LengthRev = 0
  Placement = pos=(0,0,0.25) rot=(0,0,1;0rad)
  Solid = true
  Symmetric = false
FEATURE [Part::Feature] Screw_solid087  label="M2x4-Screw (Solid)087"
  Placement = pos=(0,0,0) rot=(0,0,1;3.14159rad)
  shape: bbox 3.6 x 3.6 x 4 mm, 12 faces (baked)
FEATURE [Part::Feature] Cylinder014005326  label="Válec302"
  Placement = pos=(0,0,0) rot=(0,0,1;2.0944rad)
  shape: bbox 5 x 5 x 7 mm, 3 faces (baked)
FEATURE [Part::Feature] Cylinder014005327  label="Válec303"
  Placement = pos=(0,0,0) rot=(0,0,1;4.18879rad)
  shape: bbox 5 x 5 x 7 mm, 3 faces (baked)
FEATURE [Part::Feature] Screw_solid088  label="M2x4-Screw (Solid)088"
  Placement = pos=(0,0,0) rot=(0,0,1;1.0472rad)
  shape: bbox 3.6 x 3.6 x 4 mm, 12 faces (baked)
FEATURE [Part::Feature] Cylinder014005328  label="Válec304"
  shape: bbox 5 x 5 x 7 mm, 3 faces (baked)
FEATURE [Part::MultiFuse] Fusion196
  Shapes = -> [Cylinder014005327,Cylinder014005328,Cylinder014005326]
FEATURE [Part::Feature] Screw_solid089  label="M2x4-Screw (Solid)089"
  Placement = pos=(0,0,0) rot=(0,0,-1;1.0472rad)
  shape: bbox 3.6 x 3.6 x 4 mm, 12 faces (baked)
FEATURE [Part::MultiFuse] Fusion199  label="srouby030"
  Placement = pos=(0,0,0.5) rot=(0,0,1;0rad)
  Shapes = -> [Screw_solid088,Screw_solid089,Screw_solid087]
FEATURE [Part::Box] Box035  label="Krychle028"
  AttacherType = Attacher::AttachEngine3D
  Height = 112
  Length = 38
  Placement = pos=(-19,32,-52) rot=(0,0,1;0rad)
  Width = 10
FEATURE [Part::Box] Box036  label="Krychle029"
  AttacherType = Attacher::AttachEngine3D
  Height = 112
  Length = 38
  Placement = pos=(-19,34,-52) rot=(0,0,1;0rad)
  Width = 6
FEATURE [Part::Cylinder] Cylinder014005329  label="Válec305"
  Angle = 360
  AttacherType = Attacher::AttachEngine3D
  Height = 22
  Radius = 2.6
FEATURE [Part::MultiFuse] Fusion195
  Shapes = -> [Cylinder014005329,Extrude026]
FEATURE [Part::Cylinder] Cylinder014005330  label="Válec306"
  Angle = 360
  AttacherType = Attacher::AttachEngine3D
  Height = 7
  Radius = 2.6
FEATURE [Part::MultiFuse] Fusion198
  Placement = pos=(0,0,1) rot=(0,0,1;0rad)
  Shapes = -> [Fusion196,Cylinder014005330]
FEATURE [Part::Cylinder] Cylinder014005331  label="Válec307"
  Angle = 360
  AttacherType = Attacher::AttachEngine3D
  Height = 8
  Placement = pos=(0,0,66) rot=(0,0,1;0rad)
  Radius = 4.5
FEATURE [Part::Box] Box037  label="Krychle030"
  AttacherType = Attacher::AttachEngine3D
  Height = 15
  Length = 50
  Placement = pos=(-25,-25,64) rot=(0,0,1;0rad)
  Width = 50
FEATURE [Part::Cylinder] Cylinder014005332  label="Válec308"
  Angle = 360
  AttacherType = Attacher::AttachEngine3D
  Height = 6
  Placement = pos=(0,0,7) rot=(0,0,1;0rad)
  Radius = 6.5
FEATURE [Part::Box] Box038  label="Krychle031"
  AttacherType = Attacher::AttachEngine3D
  Height = 15
  Length = 2
  Placement = pos=(-15.5,-26,61) rot=(0,0,1;0rad)
  Width = 52
FEATURE [Part::Cylinder] Cylinder014005333  label="Unasec vrch017"
  Angle = 360
  AttacherType = Attacher::AttachEngine3D
  Height = 1.5
  Placement = pos=(0,0,5.5) rot=(0,0,1;0rad)
  Radius = 15.5
FEATURE [Part::Cylinder] Cylinder014005334  label="Válec309"
  Angle = 360
  AttacherType = Attacher::AttachEngine3D
  Height = 55
  Placement = pos=(0,0,35) rot=(0,0,1;0rad)
  Radius = 2.7
FEATURE [Part::Cylinder] Cylinder014005335  label="Válec310"
  Angle = 360
  AttacherType = Attacher::AttachEngine3D
  Height = 9
  Placement = pos=(0,0,55) rot=(0,0,1;0rad)
  Radius = 12.5
FEATURE [Part::Cut] Cut061079  label="unasec vrch017"
  Base = -> Cylinder014005333
  Tool = -> Fusion199
FEATURE [Part::Cut] Cut061080
  Base = -> Box035
  Tool = -> Box036
FEATURE [Part::MultiFuse] Fusion194  label="Arca plate base004"
  Placement = pos=(0,-6.5,115.5) rot=(-1,0,0;1.5708rad)
  Shapes = -> [Extrude025,Cut061080]
FEATURE [Part::Cut] Cut061077  label="Arca sw 002"
  Base = -> Box037
  Tool = -> Fusion194
FEATURE [Part::Cut] Cut061083
  Base = -> Cut061077
  Tool = -> Box038
FEATURE [Part::MultiFuse] Fusion192
  Shapes = -> [Cylinder014005335,Cut061083]
FEATURE [Part::Cut] Cut061084  label="Unasec Vrch zaklad017"
  Base = -> Cut061079
  Tool = -> Fusion198
FEATURE [Part::MultiFuse] Fusion197
  Shapes = -> [Cut061084,Cylinder014005332,Extrude027]
FEATURE [Part::Cut] Cut061081  label="unasec top004"
  Base = -> Fusion197
  Placement = pos=(0,0,42) rot=(0,0,1;0rad)
  Tool = -> Fusion195
FEATURE [Part::MultiFuse] Fusion191
  Shapes = -> [Cylinder014005334,Cut061081,Cylinder014005331]
FEATURE [Part::Cut] Cut061082
  Base = -> Fusion192
  Tool = -> Fusion191
FEATURE [Part::Cylinder] Cylinder014005336  label="Válec311"
  Angle = 360
  AttacherType = Attacher::AttachEngine3D
  Height = 60
  Placement = pos=(-30,17,69) rot=(0,1,0;1.5708rad)
  Radius = 2.1
FEATURE [Part::Cylinder] Cylinder014005337  label="Válec312"
  Angle = 360
  AttacherType = Attacher::AttachEngine3D
  Height = 60
  Placement = pos=(-30,-17,69) rot=(0,1,0;1.5708rad)
  Radius = 2.1
FEATURE [Part::MultiFuse] Fusion193
  Shapes = -> [Cylinder014005336,Cylinder014005337,Nut007,Nut008]
FEATURE [Part::Cut] Cut061078
  Base = -> Cut061082
  Tool = -> Fusion193
FEATURE [Part::Cylinder] Cylinder014005338  label="Válec313"
  Angle = 360
  AttacherType = Attacher::AttachEngine3D
  Height = 2.5
  Placement = pos=(0,-12,71) rot=(0,0,1;0rad)
  Radius = 6
FEATURE [Part::Box] Box039  label="Krychle032"
  AttacherType = Attacher::AttachEngine3D
  Height = 2.5
  Length = 12
  Placement = pos=(-6,-25,71) rot=(0,0,1;0rad)
  Width = 13
FEATURE [Part::MultiFuse] Fusion201
  Placement = pos=(0,0,1) rot=(0,0,1;3.14159rad)
  Shapes = -> [Box039,Cylinder014005338]
FEATURE [Part::Cylinder] Cylinder014005339  label="Válec314"
  Angle = 360
  AttacherType = Attacher::AttachEngine3D
  Height = 2.5
  Placement = pos=(0,-12,71) rot=(0,0,1;0rad)
  Radius = 6
FEATURE [Part::Box] Box040  label="Krychle033"
  AttacherType = Attacher::AttachEngine3D
  Height = 2.5
  Length = 12
  Placement = pos=(-6,-25,71) rot=(0,0,1;0rad)
  Width = 13
FEATURE [Part::MultiFuse] Fusion200
  Placement = pos=(0,0,1) rot=(0,0,1;0rad)
  Shapes = -> [Box040,Cylinder014005339]
FEATURE [Part::MultiFuse] Fusion202
  Shapes = -> [Fusion200,Fusion201]
FEATURE [Part::Cut] Cut061085  label="Swis Arca002"
  Base = -> Cut061078
  Placement = pos=(0,-5,115) rot=(-1,0,0;1.5708rad)
  Tool = -> Fusion202
FEATURE [Part::Box] Box041  label="Krychle034"
  AttacherType = Attacher::AttachEngine3D
  Height = 2
  Length = 80
  Placement = pos=(-40,-30,59) rot=(0,0,1;0rad)
  Width = 80
FEATURE [Part::Box] Box042  label="Krychle035"
  AttacherType = Attacher::AttachEngine3D
  Height = 2
  Length = 80
  Placement = pos=(-40,-30,-53) rot=(0,0,1;0rad)
  Width = 80
FEATURE [Part::MultiFuse] Fusion203  label="Orez"
  Shapes = -> [Box041,Box042]
FEATURE [Part::Box] Box002  label="Krychle002"
  AttacherType = Attacher::AttachEngine3D
  Height = 3
  Length = 13
  Placement = pos=(-6.5,0,-3) rot=(0,0,1;0rad)
  Width = 4
FEATURE [Sketcher::SketchObject] Sketch011
  MapMode = 5
  Placement = pos=(0,40,0) rot=(0,0.707107,0.707107;3.14159rad)
  sketch-geometry (6):
    g0: LineSegment StartX=0 StartY=0 StartZ=0 EndX=0 EndY=3 EndZ=0
    g1: LineSegment StartX=0 StartY=3 StartZ=0 EndX=-4 EndY=10 EndZ=0
    g2: LineSegment StartX=-4 StartY=10 StartZ=0 EndX=-26 EndY=10 EndZ=0
    g3: LineSegment StartX=-26 StartY=10 StartZ=0 EndX=-30 EndY=3 EndZ=0
    g4: LineSegment StartX=-30 StartY=3 StartZ=0 EndX=-30 EndY=0 EndZ=0
    g5: LineSegment StartX=-30 StartY=0 StartZ=0 EndX=0 EndY=0 EndZ=0
  constraints (11):
    c: Coincident(g-1,g0)
    c: PointOnObject(g0,g-2)
    c: Coincident(g0,g1)
    c: Coincident(g1,g2)
    c: Horizontal(g2)
    c: Coincident(g2,g3)
    c: Coincident(g3,g4)
    c: PointOnObject(g4,g-1)
    c: Vertical(g4)
    c: Coincident(g4,g5)
    c: Coincident(g5,g0)
FEATURE [Part::Extrusion] Extrude028
  Base = -> Sketch011
  Dir = (0,1,0)
  DirMode = 2
  FaceMakerClass = Part::FaceMakerBullseye
  LengthFwd = -40
  LengthRev = 0
  Placement = pos=(-15,0,0) rot=(0,0,1;0rad)
  Solid = true
  Symmetric = false
FEATURE [Part::MultiFuse] Fusion206  label="Dovetal profile001"
  Shapes = -> [Extrude028,Box002]
FEATURE [Part::Cylinder] Cylinder014005340  label="Válec315"
  Angle = 360
  AttacherType = Attacher::AttachEngine3D
  Height = 10
  Placement = pos=(12,20,4) rot=(0,1,0;0.785398rad)
  Radius = 1.4
FEATURE [Part::Cylinder] Cylinder001  label="Válec001"
  Angle = 360
  AttacherType = Attacher::AttachEngine3D
  Height = 10
  Placement = pos=(-12,20,4) rot=(0,-1,0;0.785398rad)
  Radius = 1.4
FEATURE [Part::MultiFuse] Fusion205
  Shapes = -> [Cylinder014005340,Cylinder001]
FEATURE [Part::Box] Box001  label="Krychle001"
  AttacherType = Attacher::AttachEngine3D
  Height = 15
  Length = 36
  Placement = pos=(-18,0,-5) rot=(0,0,1;0rad)
  Width = 40
FEATURE [Part::Cut] Cut061088
  Base = -> Box001
  Tool = -> Fusion206
FEATURE [Part::Chamfer] Chamfer007
  Base = -> Cut061088
  Edges = 2 edges r=5: [Edge2,Edge29]
FEATURE [Part::Cut] Cut001  label="Dov holder"
  Base = -> Chamfer007
  Placement = pos=(-35,-26,-12) rot=(1,0,0;1.5708rad)
  Tool = -> Fusion205
FEATURE [Part::Cylinder] Cylinder014005345  label="tyč závaží"
  Angle = 360
  AttacherType = Attacher::AttachEngine3D
  Height = 300
  Placement = pos=(0,-38,141) rot=(1,0,0;1.5708rad)
  Radius = 3
FEATURE [Part::Cylinder] Cylinder014005346  label="Válec317"
  Angle = 360
  AttacherType = Attacher::AttachEngine3D
  Height = 60
  Placement = pos=(0,-200,88) rot=(1,0,0;1.5708rad)
  Radius = 50
FEATURE [Part::Cylinder] Cylinder014005347  label="Válec318"
  Angle = 360
  AttacherType = Attacher::AttachEngine3D
  Height = 58
  Placement = pos=(0,-200,88) rot=(1,0,0;1.5708rad)
  Radius = 44
FEATURE [Part::Cut] Cut061093
  Base = -> Cylinder014005346
  Tool = -> Cylinder014005347
FEATURE [Part::Cylinder] Cylinder014005348  label="Válec319"
  Angle = 360
  AttacherType = Attacher::AttachEngine3D
  Height = 56
  Placement = pos=(0,-203.5,88) rot=(1,0,0;1.5708rad)
  Radius = 10
FEATURE [Part::MultiFuse] Fusion217  label="Zavazí dno"
  Placement = pos=(0,-2,0) rot=(0,0,1;0rad)
  Shapes = -> [Cut061093,Cylinder014005348]
FEATURE [Part::Cylinder] Cylinder014005349  label="Válec320"
  Angle = 360
  AttacherType = Attacher::AttachEngine3D
  Height = 2
  Placement = pos=(0,-200,88) rot=(1,0,0;1.5708rad)
  Radius = 50
FEATURE [Part::Cylinder] Cylinder014005350  label="Válec321"
  Angle = 360
  AttacherType = Attacher::AttachEngine3D
  Height = 3.5
  Placement = pos=(0,-200,88) rot=(1,0,0;1.5708rad)
  Radius = 44
FEATURE [Part::MultiFuse] Fusion218  label="zaazi vyko"
  Shapes = -> [Cylinder014005350,Cylinder014005349]
FEATURE [Part::Cylinder] Cylinder014005351  label="tyč závaží001"
  Angle = 360
  AttacherType = Attacher::AttachEngine3D
  Height = 350
  Placement = pos=(0,85,88) rot=(1,0,0;1.5708rad)
  Radius = 3
FEATURE [Part::FeaturePython] Nut013  label="M6-Nut006"  # Fasteners workbench fastener (typed FeaturePython)
  Placement = pos=(0,-258,88) rot=(1,0,0;1.5708rad)
  diameter = 8
  invert = false
  matchOuter = false
  offset = 0
  thread = false
  type = 1
FEATURE [Part::Feature] Screw006_solid  label="vyko M2.5x8"
  Placement = pos=(0,0,10) rot=(0,0,1;0rad)
  shape: bbox 4.5 x 8.524 x 4.5 mm, 11 faces (baked)
FEATURE [Part::Feature] Screw006_solid001  label="vyko M2.5x009"
  Placement = pos=(0,0,104) rot=(0,0,1;0rad)
  shape: bbox 4.5 x 8.524 x 4.5 mm, 11 faces (baked)
FEATURE [Part::Feature] Screw006_solid002  label="vyko M2.5x010"
  Placement = pos=(47,0,57) rot=(0,0,1;0rad)
  shape: bbox 4.5 x 8.524 x 4.5 mm, 11 faces (baked)
FEATURE [Part::Feature] Screw006_solid003  label="vyko M2.5x011"
  Placement = pos=(-47,0,57) rot=(0,0,1;0rad)
  shape: bbox 4.5 x 8.524 x 4.5 mm, 11 faces (baked)
FEATURE [Part::MultiFuse] Fusion219  label="srouby diry zavazi"
  Shapes = -> [Cylinder014005351,Screw006_solid,Screw006_solid001,Screw006_solid002,Screw006_solid003,Nut013]
FEATURE [Part::Cut] Cut061094  label="Weight  bottom"
  Base = -> Fusion217
  Tool = -> Fusion219
FEATURE [Part::FeaturePython] Nut014  label="M6-Nut005"  # Fasteners workbench fastener (typed FeaturePython)
  Placement = pos=(0,-238,88) rot=(1,0,0;1.5708rad)
  diameter = 8
  invert = false
  matchOuter = false
  offset = 0
  thread = false
  type = 1
FEATURE [Part::Cylinder] Cylinder014005352  label="tyč závaží002"
  Angle = 360
  AttacherType = Attacher::AttachEngine3D
  Height = 300
  Placement = pos=(0,55,88) rot=(1,0,0;1.5708rad)
  Radius = 3
FEATURE [Part::Feature] Screw006_solid004  label="vyko M2.5x012"
  Placement = pos=(0,0,104) rot=(0,0,1;0rad)
  shape: bbox 4.5 x 8.524 x 4.5 mm, 11 faces (baked)
FEATURE [Part::Feature] Screw006_solid005  label="vyko M2.5x013"
  Placement = pos=(47,0,57) rot=(0,0,1;0rad)
  shape: bbox 4.5 x 8.524 x 4.5 mm, 11 faces (baked)
FEATURE [Part::Feature] Screw006_solid006  label="vyko M2.5x014"
  Placement = pos=(-47,0,57) rot=(0,0,1;0rad)
  shape: bbox 4.5 x 8.524 x 4.5 mm, 11 faces (baked)
FEATURE [Part::Feature] Screw006_solid007  label="vyko M2.5x015"
  Placement = pos=(0,0,10) rot=(0,0,1;0rad)
  shape: bbox 4.5 x 8.524 x 4.5 mm, 11 faces (baked)
FEATURE [Part::MultiFuse] Fusion220  label="srouby diry zavazi001"
  Shapes = -> [Cylinder014005352,Screw006_solid007,Screw006_solid004,Screw006_solid005,Screw006_solid006,Nut014]
FEATURE [Part::Cut] Cut061095  label="Weight top"
  Base = -> Fusion218
  Tool = -> Fusion220
FEATURE [App::Part] Part019  label="DriveA"
  Group = -> [Part008,Part007]
  License = CC BY 3.0
  LicenseURL = http://creativecommons.org/licenses/by/3.0/
  Origin = -> Origin019
  Placement = pos=(0,-29,0) rot=(1,0,0;3.14159rad)
FEATURE [App::Part] Part021  label="Weights"
  Group = -> [Fusion217,Nut013,Screw006_solid,Screw006_solid003,Screw006_solid001,Screw006_solid002,Cut061093,Cylinder014005351,Cylinder014005347,Cylinder014005346,Cylinder014005348,Fusion219,Cut061094,Nut014,Screw006_solid007,Screw006_solid004,Screw006_solid006,Screw006_solid005,Cylinder014005350,Cylinder014005349,Cylinder014005352,Fusion218,Fusion220,Cut061095]
  License = CC BY 3.0
  LicenseURL = http://creativecommons.org/licenses/by/3.0/
  Origin = -> Origin021
  Placement = pos=(0,-27,52) rot=(0,0,1;0rad)
FEATURE [Part::Cylinder] Cylinder014005356  label="Válec322"
  Angle = 360
  AttacherType = Attacher::AttachEngine3D
  Height = 200
  Placement = pos=(0,0,-100) rot=(0,0,1;0rad)
  Radius = 3.9
FEATURE [Sketcher::SketchObject] Sketch013
  MapMode = 45
  Placement = pos=(44.88,21.011,5.40003) rot=(0.707106,0.001666,0.707106;3.13826rad)
  sketch-geometry (7):
    g0: LineSegment StartX=5.21891 StartY=0.0364138 StartZ=0 EndX=2.62121 EndY=4.46293 EndZ=0
    g1: LineSegment StartX=2.62121 StartY=4.46293 StartZ=0 EndX=-2.51111 EndY=4.42651 EndZ=0
    g2: LineSegment StartX=-2.51111 StartY=4.42651 StartZ=0 EndX=-5.04574 EndY=-0.0364138 EndZ=0
    g3: LineSegment StartX=-5.04574 StartY=-0.0364138 StartZ=0 EndX=-2.44804 EndY=-4.46293 EndZ=0
    g4: LineSegment StartX=-2.44804 StartY=-4.46293 StartZ=0 EndX=2.68428 EndY=-4.42651 EndZ=0
    g5: LineSegment StartX=2.68428 StartY=-4.42651 StartZ=0 EndX=5.21891 EndY=0.0364138 EndZ=0
    g6: Circle [constr] CenterX=0.0865834 CenterY=0 CenterZ=0 NormalX=0 NormalY=0 NormalZ=1 AngleXU=0 Radius=5.13245
  constraints (14):
    c: Coincident(g0,g1)
    c: Coincident(g1,g2)
    c: Coincident(g2,g3)
    c: Coincident(g3,g4)
    c: Coincident(g4,g5)
    c: Coincident(g5,g0)
    c: Equal(g0, g1-g5) x5
    c: PointOnObject(g0,g6)
    c: PointOnObject(g1,g6)
    c: PointOnObject(g2,g6)
    c: PointOnObject(g3,g6)
    c: PointOnObject(g4,g6)
    c: PointOnObject(g5,g6)
    c: PointOnObject(g6,g-1)
FEATURE [Part::Extrusion] Extrude030
  Base = -> Sketch013
  Dir = (1,0,0)
  DirMode = 2
  FaceMakerClass = Part::FaceMakerBullseye
  LengthFwd = 5
  LengthRev = 0
  Placement = pos=(0,0,0.25) rot=(0,0,1;0rad)
  Solid = true
  Symmetric = false
FEATURE [Part::RegularPolygon] RegularPolygon005  label="Pravidelný n-úhelník005"
  AttacherType = Attacher::AttachEngine3D
  Circumradius = 6
  Polygon = 6
FEATURE [Part::Extrusion] Extrude031
  Base = -> RegularPolygon005
  Dir = (0,0,1)
  DirMode = 2
  FaceMakerClass = Part::FaceMakerBullseye
  LengthFwd = 8
  LengthRev = 0
  Placement = pos=(0,0,13) rot=(0,0,1;0rad)
  Solid = true
  Symmetric = false
FEATURE [Part::Feature] Screw_solid090  label="M2x4-Screw (Solid)090"
  Placement = pos=(0,0,0) rot=(0,0,-1;1.0472rad)
  shape: bbox 3.6 x 3.6 x 4 mm, 12 faces (baked)
FEATURE [Part::Feature] Cylinder014005357  label="Válec323"
  shape: bbox 5 x 5 x 7 mm, 3 faces (baked)
FEATURE [Part::Feature] Cylinder014005358  label="Válec324"
  Placement = pos=(0,0,0) rot=(0,0,1;4.18879rad)
  shape: bbox 5 x 5 x 7 mm, 3 faces (baked)
FEATURE [Part::Feature] Cylinder014005359  label="Válec325"
  Placement = pos=(0,0,0) rot=(0,0,1;2.0944rad)
  shape: bbox 5 x 5 x 7 mm, 3 faces (baked)
FEATURE [Part::MultiFuse] Fusion223
  Shapes = -> [Cylinder014005358,Cylinder014005357,Cylinder014005359]
FEATURE [Part::Feature] Screw_solid091  label="M2x4-Screw (Solid)091"
  Placement = pos=(0,0,0) rot=(0,0,1;1.0472rad)
  shape: bbox 3.6 x 3.6 x 4 mm, 12 faces (baked)
FEATURE [Part::Feature] Screw_solid092  label="M2x4-Screw (Solid)092"
  Placement = pos=(0,0,0) rot=(0,0,1;3.14159rad)
  shape: bbox 3.6 x 3.6 x 4 mm, 12 faces (baked)
FEATURE [Part::MultiFuse] Fusion226  label="srouby031"
  Placement = pos=(0,0,0.5) rot=(0,0,1;0rad)
  Shapes = -> [Screw_solid091,Screw_solid090,Screw_solid092]
FEATURE [Part::Cylinder] Cylinder014005360  label="Válec326"
  Angle = 360
  AttacherType = Attacher::AttachEngine3D
  Height = 6
  Placement = pos=(0,0,7) rot=(0,0,1;0rad)
  Radius = 6.5
FEATURE [Part::Cylinder] Cylinder014005361  label="Válec327"
  Angle = 360
  AttacherType = Attacher::AttachEngine3D
  Height = 7
  Radius = 2.6
FEATURE [Part::MultiFuse] Fusion222
  Placement = pos=(0,0,1) rot=(0,0,1;0rad)
  Shapes = -> [Fusion223,Cylinder014005361]
FEATURE [Part::Cylinder] Cylinder014005362  label="Válec328"
  Angle = 360
  AttacherType = Attacher::AttachEngine3D
  Height = 22
  Radius = 2.6
FEATURE [Part::MultiFuse] Fusion224
  Shapes = -> [Cylinder014005362,Extrude030]
FEATURE [Part::Cylinder] Cylinder014005363  label="Válec329"
  Angle = 360
  AttacherType = Attacher::AttachEngine3D
  Height = 55
  Placement = pos=(0,0,-82) rot=(0,0,1;0rad)
  Radius = 2.7
FEATURE [Part::Cylinder] Cylinder014005364  label="Unasec vrch018"
  Angle = 360
  AttacherType = Attacher::AttachEngine3D
  Height = 1.5
  Placement = pos=(0,0,5.5) rot=(0,0,1;0rad)
  Radius = 15.5
FEATURE [Part::Cut] Cut061100  label="unasec vrch018"
  Base = -> Cylinder014005364
  Tool = -> Fusion226
FEATURE [Part::Cut] Cut061099  label="Unasec Vrch zaklad018"
  Base = -> Cut061100
  Tool = -> Fusion222
FEATURE [Part::MultiFuse] Fusion225
  Shapes = -> [Cut061099,Cylinder014005360,Extrude031]
FEATURE [Part::Cylinder] Cylinder014005366  label="Válec331"
  Angle = 360
  AttacherType = Attacher::AttachEngine3D
  Height = 12.5
  Placement = pos=(0,0,-68) rot=(0,0,1;0rad)
  Radius = 12.5
FEATURE [Part::Cylinder] Cylinder014005367  label="Válec332"
  Angle = 360
  AttacherType = Attacher::AttachEngine3D
  Height = 11.5
  Placement = pos=(0,0,-76.1) rot=(0,0,1;0rad)
  Radius = 11
FEATURE [Part::Cut] Cut061098  label="unasec top005"
  Base = -> Fusion225
  Placement = pos=(0,0,-42) rot=(1,0,0;3.14159rad)
  Tool = -> Fusion224
FEATURE [Part::Cylinder] Cylinder014005368  label="Válec333"
  Angle = 360
  AttacherType = Attacher::AttachEngine3D
  Height = 9
  Placement = pos=(0,0,-77) rot=(0,0,1;0rad)
  Radius = 4.5
FEATURE [Part::MultiFuse] Fusion228
  Shapes = -> [Cylinder014005368,Cut061098,Cylinder014005363]
FEATURE [Part::Cylinder] Cylinder014005369  label="Lozisko1"
  Angle = 360
  AttacherType = Attacher::AttachEngine3D
  Height = 4
  Placement = pos=(0,29,-52.1) rot=(0,0,1;0rad)
  Radius = 7
FEATURE [Part::Cylinder] Cylinder014005370  label="Lozisko002"
  Angle = 360
  AttacherType = Attacher::AttachEngine3D
  Height = 4
  Placement = pos=(0,29,56) rot=(0,0,1;0rad)
  Radius = 7
FEATURE [Part::FeaturePython] InvoluteGear020  # WARN: FeaturePython — macro-defined, semantics opaque (R4)
  Placement = pos=(0,0,-71.9) rot=(0,0,1;0rad)
  backlash = 0
  beta = -20
  clearance = 0.25
  double_helix = true
  head = 0
  height = 8.2
  module = 1.16
  numpoints = 6
  pressure_angle = 20
  reversed_backlash = false
  shift = 0
  simple = false
  teeth = 20
  undercut = false
FEATURE [Part::Cylinder] Cylinder014005365  label="Válec330"
  Angle = 360
  AttacherType = Attacher::AttachEngine3D
  Height = 15
  Placement = pos=(0,0,-76.1) rot=(0,0,1;0rad)
  Radius = 5
FEATURE [Part::MultiFuse] Fusion229
  Shapes = -> [Cylinder014005365,Cylinder014005366,InvoluteGear020]
FEATURE [Part::Cut] Cut061101  label="Pinion"
  Base = -> Fusion229
  Tool = -> Fusion228
FEATURE [App::Part] Part022  label="Pinion20 A"
  Group = -> [Sketch013,Extrude030,RegularPolygon005,Extrude031,Cut061100,Cut061099,Cut061098,Cylinder014005361,Cylinder014005360,Cylinder014005368,Cylinder014005363,Cylinder014005364,Cylinder014005365,Cylinder014005366,Cylinder014005362,Screw_solid090,Screw_solid092,Cylinder014005358,Cylinder014005357,Screw_solid091,Cylinder014005359,Fusion225,Fusion224,Fusion228,Fusion223,Fusion222,Fusion226,InvoluteGear020,+2 more]
  License = CC BY 3.0
  LicenseURL = http://creativecommons.org/licenses/by/3.0/
  Origin = -> Origin022
  Placement = pos=(0,-29,0) rot=(0,0,1;0.017453rad)
FEATURE [Part::MultiFuse] Fusion230  label="DIRA OSA"
  Shapes = -> [Cylinder014005164,Cylinder014005369,Cylinder014005370]
FEATURE [Part::Cylinder] Cylinder014005371  label="Lozisko003"
  Angle = 360
  AttacherType = Attacher::AttachEngine3D
  Height = 4
  Placement = pos=(0,0,48) rot=(0,0,1;0rad)
  Radius = 7
FEATURE [Part::Cylinder] Cylinder014005372  label="Lozisko004"
  Angle = 360
  AttacherType = Attacher::AttachEngine3D
  Height = 4
  Placement = pos=(0,0,-60) rot=(0,0,1;0rad)
  Radius = 7
FEATURE [Part::Cylinder] Cylinder014005373  label="Válec334"
  Angle = 360
  AttacherType = Attacher::AttachEngine3D
  Height = 65
  Placement = pos=(-32,15,-27) rot=(0,1,0;1.5708rad)
  Radius = 1.35
FEATURE [Part::Cylinder] Cylinder014005374  label="Válec335"
  Angle = 360
  AttacherType = Attacher::AttachEngine3D
  Height = 65
  Placement = pos=(-32,15,42) rot=(0,1,0;1.5708rad)
  Radius = 1.35
FEATURE [Part::MultiFuse] Fusion231  label="diry 2,8"
  Shapes = -> [Cylinder014005374,Cylinder014005167,Cylinder014005168,Cylinder014005169,Cylinder014005373]
FEATURE [Part::MultiFuse] Fusion232  label="Diry orez"
  Shapes = -> [Fusion231,Fusion230,Fusion203]
FEATURE [Part::Cut] Cut061102  label="Blok A"
  Base = -> Fusion098
  Tool = -> Fusion232
FEATURE [Part::Chamfer] Chamfer008  label="Axis 1"
  Base = -> Cut061102
  Edges = 4 edges r=8: [Edge132,Edge133,Edge152,Edge153]
  Placement = pos=(0,-31,0) rot=(0,1,0;3.14159rad)
FEATURE [App::Part] Part023  label="Axis 002"
  Group = -> [Extrude010,Chamfer001,Sketch002,Fusion094,Fusion092,Fusion096,Fusion098,Fusion203,Cut061010,Cut061007,Cylinder014005154,Box010,Cylinder014005158,Cylinder014005157,Box,Cylinder014005156,Cylinder014005155,Box013,Box012,Box016,Box017,Cylinder014005166,Cylinder014005167,Cylinder014005165,Cylinder014005164,Cylinder014005168,Cylinder014005169,Box041,Box042,Cylinder014005370,Cylinder014005369,Fusion230,+6 more]
  License = CC BY 3.0
  LicenseURL = http://creativecommons.org/licenses/by/3.0/
  Origin = -> Origin023
FEATURE [Part::FeaturePython] Nut  label="M8-Nut"  # Fasteners workbench fastener (typed FeaturePython)
  Placement = pos=(0,0,-80) rot=(0,0,1;0rad)
  diameter = 9
  invert = false
  matchOuter = false
  offset = 0
  thread = false
  type = 3
FEATURE [Part::Cylinder] Cylinder014005375  label="Válec336"
  Angle = 360
  AttacherType = Attacher::AttachEngine3D
  Height = 15
  Placement = pos=(0,0,55) rot=(0,0,1;0rad)
  Radius = 11
FEATURE [Part::Cylinder] Cylinder014005376  label="Válec337"
  Angle = 360
  AttacherType = Attacher::AttachEngine3D
  Height = 15
  Placement = pos=(0,0,52) rot=(0,0,1;0rad)
  Radius = 5.5
FEATURE [Part::MultiFuse] Fusion233
  Shapes = -> [Cylinder014005375,Cylinder014005376,Cut061076]
FEATURE [Part::FeaturePython] Screw008  label="M8x160-Screw001"  # Fasteners workbench fastener (typed FeaturePython)
  Placement = pos=(0,0,68.4) rot=(0,0,1;0rad)
  diameter = 9
  invert = false
  length = 16
  matchOuter = false
  offset = 0
  thread = false
  type = 13
FEATURE [Part::Cut] Cut061103  label="Swiss Acra V2"
  Base = -> Fusion233
  Tool = -> Screw008
FEATURE [App::Part] Part024  label="Swiss arca A"
  Group = -> [Extrude013,Extrude012,Extrude014,RegularPolygon001,Nut005,Nut006,Sketch004,Sketch005,Screw008,Fusion189,Fusion190,Fusion188,Fusion108,Fusion109,Fusion111,Fusion114,Fusion110,Fusion116,Fusion115,Fusion113,Fusion112,Cut061019,Cut061016,Cut061021,Cut061022,Cut061018,Cut061020,Cut061017,Cut061015,Screw_solid050,Screw_solid049,Cylinder014005185,Screw_solid048,Cylinder014005187,Cylinder014005186,Box025,+22 more]
  License = CC BY 3.0
  LicenseURL = http://creativecommons.org/licenses/by/3.0/
  Origin = -> Origin024
FEATURE [Part::Cylinder] Cylinder014005377  label="diist podl"
  Angle = 360
  AttacherType = Attacher::AttachEngine3D
  Height = 4
  Placement = pos=(0,0,-64) rot=(0,0,1;0rad)
  Radius = 5.5
FEATURE [Part::FeaturePython] Nut015  label="M8-Nut007"  # Fasteners workbench fastener (typed FeaturePython)
  Placement = pos=(0,-88,85) rot=(1,0,0;1.5708rad)
  diameter = 9
  invert = false
  matchOuter = false
  offset = 0
  thread = false
  type = 3
FEATURE [Part::Cylinder] Cylinder014005378  label="diist podl001"
  Angle = 360
  AttacherType = Attacher::AttachEngine3D
  Height = 4
  Placement = pos=(0,0,-64) rot=(0,0,1;0rad)
  Radius = 4.2
FEATURE [Part::Cut] Cut061104  label="dist-11x8x4"
  Base = -> Cylinder014005377
  Tool = -> Cylinder014005378
FEATURE [Part::FeaturePython] Nut016  label="M8-Nut002"  # Fasteners workbench fastener (typed FeaturePython)
  Placement = pos=(0,0,-68) rot=(0,0,1;0rad)
  diameter = 9
  invert = false
  matchOuter = false
  offset = 0
  thread = false
  type = 3
FEATURE [Part::FeaturePython] InvoluteGear021  # WARN: FeaturePython — macro-defined, semantics opaque (R4)
  Placement = pos=(0,0,-72) rot=(0,0,1;0rad)
  backlash = 0
  beta = 20
  clearance = 0.25
  double_helix = true
  head = 0
  height = 8
  module = 1.16
  numpoints = 6
  pressure_angle = 20
  reversed_backlash = false
  shift = 0
  simple = false
  teeth = 27
  undercut = false
FEATURE [Part::MultiFuse] Fusion236
  Shapes = -> [Cylinder014005367,InvoluteGear021]
FEATURE [Sketcher::SketchObject] Sketch014
  MapMode = 5
  Placement = pos=(0,0,-64.6) rot=(0,0,1;0rad)
  Support = -> [Fusion236]
  sketch-geometry (7):
    g0: LineSegment StartX=-3.8831 StartY=6.55674 StartZ=0 EndX=-7.61986 EndY=-0.0844932 EndZ=0
    g1: LineSegment StartX=-7.61986 StartY=-0.0844932 StartZ=0 EndX=-3.73676 EndY=-6.64124 EndZ=0
    g2: LineSegment StartX=-3.73676 StartY=-6.64124 StartZ=0 EndX=3.8831 EndY=-6.55674 EndZ=0
    g3: LineSegment StartX=3.8831 StartY=-6.55674 StartZ=0 EndX=7.61986 EndY=0.0844932 EndZ=0
    g4: LineSegment StartX=7.61986 StartY=0.0844932 StartZ=0 EndX=3.73676 EndY=6.64124 EndZ=0
    g5: LineSegment StartX=3.73676 StartY=6.64124 StartZ=0 EndX=-3.8831 EndY=6.55674 EndZ=0
    g6: Circle [constr] CenterX=0 CenterY=0 CenterZ=0 NormalX=0 NormalY=0 NormalZ=1 AngleXU=0 Radius=7.62033
  constraints (14):
    c: Coincident(g0,g1)
    c: Coincident(g1,g2)
    c: Coincident(g2,g3)
    c: Coincident(g3,g4)
    c: Coincident(g4,g5)
    c: Coincident(g5,g0)
    c: Equal(g0, g1-g5) x5
    c: PointOnObject(g0,g6)
    c: PointOnObject(g1,g6)
    c: PointOnObject(g2,g6)
    c: PointOnObject(g3,g6)
    c: PointOnObject(g4,g6)
    c: PointOnObject(g5,g6)
    c: Coincident(g6,g-1)
FEATURE [Part::Extrusion] Extrude032
  Base = -> Sketch014
  Dir = (0,0,1)
  DirMode = 2
  FaceMakerClass = Part::FaceMakerBullseye
  LengthFwd = 5
  LengthRev = 0
  Placement = pos=(0,0,-5) rot=(0,0,1;0rad)
  Solid = true
  Symmetric = false
FEATURE [Part::MultiFuse] Fusion237
  Shapes = -> [Extrude032,Cylinder014005356]
FEATURE [Part::Cut] Cut061105  label="Gear A"
  Base = -> Fusion236
  Tool = -> Fusion237
FEATURE [App::Part] Part025  label="Gear27 A"
  Group = -> [Sketch014,Cylinder014005367,Cylinder014005356,Fusion237,Fusion236,InvoluteGear021,Extrude032,Cut061105,Nut016,Nut,Cylinder014005378,Cylinder014005377,Cut061104,Cylinder014005372]
  License = CC BY 3.0
  LicenseURL = http://creativecommons.org/licenses/by/3.0/
  Origin = -> Origin025
FEATURE [Sketcher::SketchObject] Sketch015
  MapMode = 5
  Placement = pos=(0,0,60) rot=(0,0,1;0rad)
  sketch-geometry (6):
    g0: LineSegment StartX=-18.9734 StartY=34.0308 StartZ=0 EndX=-16.0253 EndY=36.9748 EndZ=0
    g1: LineSegment StartX=18.996 StartY=34.0308 StartZ=0 EndX=16.044 EndY=36.9748 EndZ=0
    g2: LineSegment StartX=18.996 StartY=34.0308 StartZ=0 EndX=-18.9734 EndY=34.0308 EndZ=0
    g3: LineSegment StartX=-18.9734 StartY=40.0311 StartZ=0 EndX=-16.0253 EndY=36.9748 EndZ=0
    g4: LineSegment StartX=16.044 StartY=36.9748 StartZ=0 EndX=18.9109 EndY=40.0311 EndZ=0
    g5: LineSegment StartX=-18.9734 StartY=40.0311 StartZ=0 EndX=18.9109 EndY=40.0311 EndZ=0
  constraints (7):
    c: Coincident(g2,g1)
    c: Coincident(g2,g0)
    c: Horizontal(g2)
    c: Coincident(g3,g0)
    c: Coincident(g5,g3)
    c: Coincident(g5,g4)
    c: Horizontal(g5)
FEATURE [Part::Extrusion] Extrude033
  Base = -> Sketch015
  Dir = (0,0,1)
  DirMode = 2
  FaceMakerClass = Part::FaceMakerBullseye
  LengthFwd = -112
  LengthRev = 0
  Solid = true
  Symmetric = false
FEATURE [Part::Cylinder] Cylinder014005379  label="Válec338"
  Angle = 360
  AttacherType = Attacher::AttachEngine3D
  Height = 50
  Placement = pos=(15.5,15.5,0) rot=(0,0,1;0rad)
  Radius = 1.6
FEATURE [Part::Cylinder] Cylinder014005380  label="Válec339"
  Angle = 360
  AttacherType = Attacher::AttachEngine3D
  Height = 50
  Placement = pos=(-15.5,15.5,0) rot=(0,0,1;0rad)
  Radius = 1.6
FEATURE [Part::Cylinder] Cylinder014005381  label="Válec340"
  Angle = 360
  AttacherType = Attacher::AttachEngine3D
  Height = 50
  Placement = pos=(-15.5,-15.5,0) rot=(0,0,1;0rad)
  Radius = 1.6
FEATURE [Part::Box] Box052  label="Krychle043"
  AttacherType = Attacher::AttachEngine3D
  Height = 10
  Length = 43
  Placement = pos=(-21.5,-20.5,0) rot=(0,0,1;0rad)
  Width = 42
FEATURE [Part::Chamfer] Chamfer010
  Base = -> Box052
  Edges = 2 edges r=5: [Edge1,Edge5]
FEATURE [Part::Cylinder] Cylinder014005382  label="Válec341"
  Angle = 360
  AttacherType = Attacher::AttachEngine3D
  Height = 50
  Placement = pos=(15.5,-15.5,0) rot=(0,0,1;0rad)
  Radius = 1.6
FEATURE [Part::Cylinder] Cylinder014005383  label="dira stred004"
  Angle = 360
  AttacherType = Attacher::AttachEngine3D
  Height = 50
  Radius = 13
FEATURE [Part::MultiFuse] Fusion239  label="diry007"
  Shapes = -> [Cylinder014005380,Cylinder014005379,Cylinder014005383,Cylinder014005381,Cylinder014005382]
FEATURE [Part::Cut] Cut061106  label="Horni ucjyt002"
  Base = -> Chamfer010
  Placement = pos=(0,0,49.5) rot=(0,0,1;0rad)
  Tool = -> Fusion239
FEATURE [Part::Box] Box053  label="deska006"
  AttacherType = Attacher::AttachEngine3D
  Height = 111
  Length = 9
  Placement = pos=(-30.5,-14.5,-51.5) rot=(0,0,1;0rad)
  Width = 46
FEATURE [Part::Cylinder] Cylinder014005384  label="Válec342"
  Angle = 360
  AttacherType = Attacher::AttachEngine3D
  Height = 10
  Placement = pos=(0,43,54.5) rot=(1,0,0;1.5708rad)
  Radius = 4
FEATURE [Part::Box] Box054  label="Krychle044"
  AttacherType = Attacher::AttachEngine3D
  Height = 112
  Length = 38
  Placement = pos=(-19,32,-52) rot=(0,0,1;0rad)
  Width = 10
FEATURE [Part::Box] Box055  label="deska007"
  AttacherType = Attacher::AttachEngine3D
  Height = 111
  Length = 43
  Placement = pos=(-21.5,21.5,-51.5) rot=(0,0,1;0rad)
  Width = 10
FEATURE [Part::Box] Box056  label="deska008"
  AttacherType = Attacher::AttachEngine3D
  Height = 111
  Length = 9
  Placement = pos=(21.5,-14.5,-51.5) rot=(0,0,1;0rad)
  Width = 46
FEATURE [Part::MultiFuse] Fusion242  label="motor drazak002"
  Shapes = -> [Cut061106,Box056,Box055,Box053]
FEATURE [Part::Box] Box057  label="Krychle045"
  AttacherType = Attacher::AttachEngine3D
  Height = 112
  Length = 38
  Placement = pos=(-19,34,-52) rot=(0,0,1;0rad)
  Width = 6
FEATURE [Part::Cut] Cut061107
  Base = -> Box054
  Tool = -> Box057
FEATURE [Part::MultiFuse] Fusion240  label="Arca plate base006"
  Placement = pos=(0,-0.5,0) rot=(0,0,1;0rad)
  Shapes = -> [Extrude033,Cut061107]
FEATURE [Part::Cylinder] Cylinder014005385  label="DIRA8,003"
  Angle = 360
  AttacherType = Attacher::AttachEngine3D
  Height = 200
  Placement = pos=(0,29,-100) rot=(0,0,1;0rad)
  Radius = 4.2
FEATURE [Part::Cylinder] Cylinder014005386  label="Válec343"
  Angle = 360
  AttacherType = Attacher::AttachEngine3D
  Height = 10
  Placement = pos=(0,43,-47) rot=(1,0,0;1.5708rad)
  Radius = 4
FEATURE [Part::MultiFuse] Fusion241  label="drzak s arca002"
  Shapes = -> [Fusion242,Fusion240,Cylinder014005384,Cylinder014005386]
FEATURE [Part::Cylinder] Cylinder014005387  label="Válec344"
  Angle = 360
  AttacherType = Attacher::AttachEngine3D
  Height = 65
  Placement = pos=(-32,0,0) rot=(0,1,0;1.5708rad)
  Radius = 1.35
FEATURE [Part::Cylinder] Cylinder014005388  label="Válec345"
  Angle = 360
  AttacherType = Attacher::AttachEngine3D
  Height = 65
  Placement = pos=(-32,0,42) rot=(0,1,0;1.5708rad)
  Radius = 1.35
FEATURE [Part::Cylinder] Cylinder014005389  label="Válec346"
  Angle = 360
  AttacherType = Attacher::AttachEngine3D
  Height = 65
  Placement = pos=(-32,0,-27) rot=(0,1,0;1.5708rad)
  Radius = 1.35
FEATURE [Part::Box] Box058  label="Krychle046"
  AttacherType = Attacher::AttachEngine3D
  Height = 2
  Length = 80
  Placement = pos=(-40,-30,-53) rot=(0,0,1;0rad)
  Width = 80
FEATURE [Part::Box] Box059  label="Krychle047"
  AttacherType = Attacher::AttachEngine3D
  Height = 2
  Length = 80
  Placement = pos=(-40,-30,59) rot=(0,0,1;0rad)
  Width = 80
FEATURE [Part::MultiFuse] Fusion238  label="Orez001"
  Shapes = -> [Box059,Box058]
FEATURE [Part::Cylinder] Cylinder014005390  label="Lozisko005"
  Angle = 360
  AttacherType = Attacher::AttachEngine3D
  Height = 4
  Placement = pos=(0,29,-52.1) rot=(0,0,1;0rad)
  Radius = 7
FEATURE [Part::Cylinder] Cylinder014005391  label="Válec347"
  Angle = 360
  AttacherType = Attacher::AttachEngine3D
  Height = 65
  Placement = pos=(-32,15,42) rot=(0,1,0;1.5708rad)
  Radius = 1.35
FEATURE [Part::Cylinder] Cylinder014005392  label="Lozisko006"
  Angle = 360
  AttacherType = Attacher::AttachEngine3D
  Height = 4
  Placement = pos=(0,29,56) rot=(0,0,1;0rad)
  Radius = 7
FEATURE [Part::Cylinder] Cylinder014005393  label="Válec348"
  Angle = 360
  AttacherType = Attacher::AttachEngine3D
  Height = 65
  Placement = pos=(-32,15,-27) rot=(0,1,0;1.5708rad)
  Radius = 1.35
FEATURE [Part::MultiFuse] Fusion243  label="diry 2,007"
  Shapes = -> [Cylinder014005391,Cylinder014005387,Cylinder014005388,Cylinder014005389,Cylinder014005393]
FEATURE [Part::MultiFuse] Fusion244  label="DIRA OSA001"
  Shapes = -> [Cylinder014005385,Cylinder014005390,Cylinder014005392]
FEATURE [Part::MultiFuse] Fusion245  label="Diry orez001"
  Shapes = -> [Fusion243,Fusion244,Fusion238]
FEATURE [Part::Cut] Cut061108  label="Blok A001"
  Base = -> Fusion241
  Tool = -> Fusion245
FEATURE [Part::Chamfer] Chamfer009  label="Axis 003"
  Base = -> Cut061108
  Edges = 4 edges r=8: [Edge132,Edge133,Edge152,Edge153]
  Placement = pos=(0,-29,0) rot=(0,1,0;3.14159rad)
FEATURE [Part::FeaturePython] Screw009  label="M8x160-Screw002"  # Fasteners workbench fastener (typed FeaturePython)
  Placement = pos=(0,0,68.4) rot=(0,0,1;0rad)
  diameter = 9
  invert = false
  length = 16
  matchOuter = false
  offset = 0
  thread = false
  type = 13
FEATURE [Part::Cylinder] Cylinder014005394  label="Válec349"
  Angle = 360
  AttacherType = Attacher::AttachEngine3D
  Height = 10
  Placement = pos=(0,0,-3) rot=(0,0,1;0rad)
  Radius = 7
FEATURE [Part::Cylinder] Cylinder014005395  label="Válec350"
  Angle = 360
  AttacherType = Attacher::AttachEngine3D
  Height = 7.5
  Placement = pos=(0,0,-7) rot=(0,0,1;0rad)
  Radius = 6.5
FEATURE [Sketcher::SketchObject] Sketch016
  MapMode = 45
  Placement = pos=(44.88,21.011,5.40003) rot=(0.707106,0.001666,0.707106;3.13826rad)
  sketch-geometry (7):
    g0: LineSegment StartX=5 StartY=0 StartZ=0 EndX=2.5 EndY=4.33013 EndZ=0
    g1: LineSegment StartX=2.5 StartY=4.33013 StartZ=0 EndX=-2.5 EndY=4.33013 EndZ=0
    g2: LineSegment StartX=-2.5 StartY=4.33013 StartZ=0 EndX=-5 EndY=0 EndZ=0
    g3: LineSegment StartX=-5 StartY=0 StartZ=0 EndX=-2.5 EndY=-4.33013 EndZ=0
    g4: LineSegment StartX=-2.5 StartY=-4.33013 StartZ=0 EndX=2.5 EndY=-4.33013 EndZ=0
    g5: LineSegment StartX=2.5 StartY=-4.33013 StartZ=0 EndX=5 EndY=0 EndZ=0
    g6: Circle [constr] CenterX=0 CenterY=0 CenterZ=0 NormalX=0 NormalY=0 NormalZ=1 AngleXU=0 Radius=5
  constraints (14):
    c: Coincident(g0,g1)
    c: Coincident(g1,g2)
    c: Coincident(g2,g3)
    c: Coincident(g3,g4)
    c: Coincident(g4,g5)
    c: Coincident(g5,g0)
    c: Equal(g0, g1-g5) x5
    c: PointOnObject(g0,g6)
    c: PointOnObject(g1,g6)
    c: PointOnObject(g2,g6)
    c: PointOnObject(g3,g6)
    c: PointOnObject(g4,g6)
    c: PointOnObject(g5,g6)
    c: PointOnObject(g6,g-1)
FEATURE [Part::Extrusion] Extrude037
  Base = -> Sketch016
  Dir = (1,0,0)
  DirMode = 2
  FaceMakerClass = Part::FaceMakerBullseye
  LengthFwd = 5
  LengthRev = 0
  Placement = pos=(0,0,0.25) rot=(0,0,1;0rad)
  Solid = true
  Symmetric = false
FEATURE [Part::RegularPolygon] RegularPolygon006  label="Pravidelný n-úhelník006"
  AttacherType = Attacher::AttachEngine3D
  Circumradius = 6
  Polygon = 6
FEATURE [Part::Extrusion] Extrude040
  Base = -> RegularPolygon006
  Dir = (0,0,1)
  DirMode = 2
  FaceMakerClass = Part::FaceMakerBullseye
  LengthFwd = 8
  LengthRev = 0
  Placement = pos=(0,0,13) rot=(0,0,1;0rad)
  Solid = true
  Symmetric = false
FEATURE [Part::RegularPolygon] RegularPolygon007  label="Pravidelný n-úhelník007"
  AttacherType = Attacher::AttachEngine3D
  Circumradius = 6
  Polygon = 6
FEATURE [Part::Extrusion] Extrude043
  Base = -> RegularPolygon007
  Dir = (0,0,1)
  DirMode = 2
  FaceMakerClass = Part::FaceMakerBullseye
  LengthFwd = 8
  LengthRev = 0
  Placement = pos=(0,0,13) rot=(0,0,1;0rad)
  Solid = true
  Symmetric = false
FEATURE [Part::FeaturePython] InvoluteGear022  # WARN: FeaturePython — macro-defined, semantics opaque (R4)
  backlash = 0
  beta = 0
  clearance = 0.25
  double_helix = false
  head = 0
  height = 5.5
  module = 1.2
  numpoints = 6
  pressure_angle = 20
  reversed_backlash = false
  shift = 0
  simple = false
  teeth = 27
  undercut = false
FEATURE [Part::FeaturePython] InvoluteGear023  # WARN: FeaturePython — macro-defined, semantics opaque (R4)
  backlash = 0
  beta = 0
  clearance = 0.25
  double_helix = false
  head = 0
  height = 5.5
  module = 1.2
  numpoints = 6
  pressure_angle = 20
  reversed_backlash = false
  shift = 0
  simple = false
  teeth = 27
  undercut = false
FEATURE [Part::FeaturePython] Nut017  label="M4-Nut008"  # Fasteners workbench fastener (typed FeaturePython)
  Placement = pos=(22,17,69) rot=(0,1,0;1.5708rad)
  diameter = 6
  invert = false
  matchOuter = false
  offset = 0
  thread = false
  type = 1
FEATURE [Part::FeaturePython] Nut018  label="M4-Nut009"  # Fasteners workbench fastener (typed FeaturePython)
  Placement = pos=(22,-17,69) rot=(0,1,0;1.5708rad)
  diameter = 6
  invert = false
  matchOuter = false
  offset = 0
  thread = false
  type = 1
FEATURE [Part::FeaturePython] InvoluteGear024  # WARN: FeaturePython — macro-defined, semantics opaque (R4)
  backlash = 0
  beta = 0
  clearance = 0.25
  double_helix = false
  head = 0
  height = 5.5
  module = 1.2
  numpoints = 6
  pressure_angle = 20
  reversed_backlash = false
  shift = 0
  simple = false
  teeth = 27
  undercut = false
FEATURE [Sketcher::SketchObject] Sketch017
  MapMode = 5
  Placement = pos=(0,0,60) rot=(0,0,1;0rad)
  sketch-geometry (6):
    g0: LineSegment StartX=-18.9734 StartY=34.0308 StartZ=0 EndX=-16.0253 EndY=36.9748 EndZ=0
    g1: LineSegment StartX=18.996 StartY=34.0308 StartZ=0 EndX=16.044 EndY=36.9748 EndZ=0
    g2: LineSegment StartX=18.996 StartY=34.0308 StartZ=0 EndX=-18.9734 EndY=34.0308 EndZ=0
    g3: LineSegment StartX=-18.9734 StartY=40.0311 StartZ=0 EndX=-16.0253 EndY=36.9748 EndZ=0
    g4: LineSegment StartX=16.044 StartY=36.9748 StartZ=0 EndX=18.9109 EndY=40.0311 EndZ=0
    g5: LineSegment StartX=-18.9734 StartY=40.0311 StartZ=0 EndX=18.9109 EndY=40.0311 EndZ=0
  constraints (7):
    c: Coincident(g2,g1)
    c: Coincident(g2,g0)
    c: Horizontal(g2)
    c: Coincident(g3,g0)
    c: Coincident(g5,g3)
    c: Coincident(g5,g4)
    c: Horizontal(g5)
FEATURE [Part::Extrusion] Extrude039
  Base = -> Sketch017
  Dir = (0,0,1)
  DirMode = 2
  FaceMakerClass = Part::FaceMakerBullseye
  LengthFwd = -112
  LengthRev = 0
  Solid = true
  Symmetric = false
FEATURE [Sketcher::SketchObject] Sketch018
  MapMode = 45
  Placement = pos=(44.88,21.011,5.40003) rot=(0.707106,0.001666,0.707106;3.13826rad)
  sketch-geometry (7):
    g0: LineSegment StartX=5.21891 StartY=0.0364138 StartZ=0 EndX=2.62121 EndY=4.46293 EndZ=0
    g1: LineSegment StartX=2.62121 StartY=4.46293 StartZ=0 EndX=-2.51111 EndY=4.42651 EndZ=0
    g2: LineSegment StartX=-2.51111 StartY=4.42651 StartZ=0 EndX=-5.04574 EndY=-0.0364138 EndZ=0
    g3: LineSegment StartX=-5.04574 StartY=-0.0364138 StartZ=0 EndX=-2.44804 EndY=-4.46293 EndZ=0
    g4: LineSegment StartX=-2.44804 StartY=-4.46293 StartZ=0 EndX=2.68428 EndY=-4.42651 EndZ=0
    g5: LineSegment StartX=2.68428 StartY=-4.42651 StartZ=0 EndX=5.21891 EndY=0.0364138 EndZ=0
    g6: Circle [constr] CenterX=0.0865834 CenterY=0 CenterZ=0 NormalX=0 NormalY=0 NormalZ=1 AngleXU=0 Radius=5.13245
  constraints (14):
    c: Coincident(g0,g1)
    c: Coincident(g1,g2)
    c: Coincident(g2,g3)
    c: Coincident(g3,g4)
    c: Coincident(g4,g5)
    c: Coincident(g5,g0)
    c: Equal(g0, g1-g5) x5
    c: PointOnObject(g0,g6)
    c: PointOnObject(g1,g6)
    c: PointOnObject(g2,g6)
    c: PointOnObject(g3,g6)
    c: PointOnObject(g4,g6)
    c: PointOnObject(g5,g6)
    c: PointOnObject(g6,g-1)
FEATURE [Part::Extrusion] Extrude038
  Base = -> Sketch018
  Dir = (1,0,0)
  DirMode = 2
  FaceMakerClass = Part::FaceMakerBullseye
  LengthFwd = 5
  LengthRev = 0
  Placement = pos=(0,0,0.25) rot=(0,0,1;0rad)
  Solid = true
  Symmetric = false
FEATURE [Part::Feature] Cylinder014005396  label="Válec351"
  shape: bbox 5 x 5 x 7 mm, 3 faces (baked)
FEATURE [Part::Feature] Cylinder014005397  label="Válec352"
  Placement = pos=(0,0,0) rot=(0,0,1;4.18879rad)
  shape: bbox 16 x 16 x 10 mm, 3 faces (baked)
FEATURE [Part::Feature] Cylinder014005398  label="Válec353"
  Placement = pos=(0,0,0) rot=(0,0,1;4.18879rad)
  shape: bbox 5 x 5 x 7 mm, 3 faces (baked)
FEATURE [Part::Feature] Screw_solid093  label="M2x4-Screw (Solid)093"
  Placement = pos=(0,0,0) rot=(0,0,1;1.0472rad)
  shape: bbox 3.6 x 3.6 x 4 mm, 12 faces (baked)
FEATURE [Part::Feature] Cylinder014005399  label="Válec354"
  Placement = pos=(0,0,0) rot=(0,0,1;2.0944rad)
  shape: bbox 5 x 5 x 7 mm, 3 faces (baked)
FEATURE [Part::Feature] Cut008_solid033  label="Planet034"
  Placement = pos=(0,0,0) rot=(0,0,1;4.18879rad)
  shape: bbox 12.9 x 13.1 x 5 mm, 57 faces (baked)
FEATURE [Part::Feature] Cut007_solid013  label="Sun014"
  shape: bbox 12.9 x 13.1 x 5 mm, 57 faces (baked)
FEATURE [Part::Feature] Cut008_solid034  label="Planet035"
  shape: bbox 12.9 x 13.1 x 5 mm, 57 faces (baked)
FEATURE [Part::Feature] Screw_solid094  label="M2x4-Screw (Solid)094"
  Placement = pos=(0,0,0) rot=(0,0,1;3.14159rad)
  shape: bbox 3.6 x 3.6 x 4 mm, 12 faces (baked)
FEATURE [Part::Feature] Screw_solid095  label="M2x4-Screw (Solid)095"
  Placement = pos=(0,0,0) rot=(0,0,1;3.14159rad)
  shape: bbox 3.6 x 3.6 x 4 mm, 12 faces (baked)
FEATURE [Part::Feature] Cylinder014005400  label="Válec355"
  Placement = pos=(0,0,0) rot=(0,0,1;2.0944rad)
  shape: bbox 16 x 16 x 10 mm, 3 faces (baked)
FEATURE [Part::Feature] Cylinder014005401  label="Válec356"
  Placement = pos=(0,0,0) rot=(0,0,1;2.0944rad)
  shape: bbox 16 x 16 x 10 mm, 3 faces (baked)
FEATURE [Part::Feature] Cut008_solid035  label="Planet036"
  Placement = pos=(0,0,0) rot=(0,0,1;4.18879rad)
  shape: bbox 12.9 x 13.1 x 5 mm, 57 faces (baked)
FEATURE [Part::Feature] Cylinder014005402  label="Válec357"
  Placement = pos=(0,0,0) rot=(0,0,1;2.0944rad)
  shape: bbox 5 x 5 x 7 mm, 3 faces (baked)
FEATURE [Part::Feature] Screw_solid096  label="M2x4-Screw (Solid)096"
  Placement = pos=(0,0,0) rot=(0,0,-1;1.0472rad)
  shape: bbox 3.6 x 3.6 x 4 mm, 12 faces (baked)
FEATURE [Part::Feature] Cylinder014005403  label="Válec358"
  shape: bbox 5 x 5 x 7 mm, 3 faces (baked)
FEATURE [Part::Feature] Screw_solid097  label="M2x4-Screw (Solid)097"
  Placement = pos=(0,0,0) rot=(0,0,-1;1.0472rad)
  shape: bbox 3.6 x 3.6 x 4 mm, 12 faces (baked)
FEATURE [Part::Feature] Screw_solid098  label="M2x4-Screw (Solid)098"
  Placement = pos=(0,0,0) rot=(0,0,1;3.14159rad)
  shape: bbox 3.6 x 3.6 x 4 mm, 12 faces (baked)
FEATURE [Part::Feature] Screw_solid099  label="M2x4-Screw (Solid)099"
  Placement = pos=(0,0,0) rot=(0,0,1;3.14159rad)
  shape: bbox 3.6 x 3.6 x 4 mm, 12 faces (baked)
FEATURE [Part::Feature] Cylinder014005404  label="Válec359"
  Placement = pos=(0,0,0) rot=(0,0,1;2.0944rad)
  shape: bbox 5 x 5 x 7 mm, 3 faces (baked)
FEATURE [Part::Feature] Screw_solid100  label="M2x4-Screw (Solid)100"
  Placement = pos=(0,0,0) rot=(0,0,-1;1.0472rad)
  shape: bbox 3.6 x 3.6 x 4 mm, 12 faces (baked)
FEATURE [Part::Feature] Cylinder014005405  label="Válec360"
  Placement = pos=(0,0,0) rot=(0,0,1;4.18879rad)
  shape: bbox 5 x 5 x 7 mm, 3 faces (baked)
FEATURE [Part::Feature] Cylinder014005406  label="Válec361"
  shape: bbox 5 x 5 x 7 mm, 3 faces (baked)
FEATURE [Part::Feature] Cut008_solid036  label="Planet037"
  Placement = pos=(0,0,0) rot=(0,0,1;2.0944rad)
  shape: bbox 12.9 x 13.1 x 5 mm, 57 faces (baked)
FEATURE [Part::Cylinder] Cylinder014005407  label="Válec362"
  Angle = 360
  AttacherType = Attacher::AttachEngine3D
  Height = 18
  Radius = 2.6
FEATURE [Part::Cylinder] Cylinder014005408  label="Válec363"
  Angle = 360
  AttacherType = Attacher::AttachEngine3D
  Height = 10
  Placement = pos=(10.5,0,0) rot=(0,0,1;0rad)
  Radius = 8
FEATURE [Part::Cylinder] Cylinder014005409  label="Válec364"
  Angle = 360
  AttacherType = Attacher::AttachEngine3D
  Height = 1.5
  Radius = 16
FEATURE [Part::Cylinder] Cylinder014005410  label="Válec365"
  Angle = 360
  AttacherType = Attacher::AttachEngine3D
  Height = 1.5
  Radius = 16
FEATURE [Part::Cylinder] Cylinder014005411  label="Válec366"
  Angle = 360
  AttacherType = Attacher::AttachEngine3D
  Height = 1.5
  Radius = 20
FEATURE [Part::Cut] Cut061118  label="Ring026"
  Base = -> Cylinder014005411
  Placement = pos=(0,0,-1.5) rot=(0,0,1;0rad)
  Tool = -> Cylinder014005410
FEATURE [Part::Cylinder] Cylinder014005412  label="Válec367"
  Angle = 360
  AttacherType = Attacher::AttachEngine3D
  Height = 4
  Placement = pos=(0,0,7) rot=(0,0,1;0rad)
  Radius = 6.5
FEATURE [Part::Cylinder] Cylinder014005413  label="unasec stred012"
  Angle = 360
  AttacherType = Attacher::AttachEngine3D
  Height = 7
  Placement = pos=(0,0,-1.5) rot=(0,0,1;0rad)
  Radius = 13.5
FEATURE [Part::Cylinder] Cylinder014005414  label="Válec368"
  Angle = 360
  AttacherType = Attacher::AttachEngine3D
  Height = 15
  Placement = pos=(0,0,-8) rot=(0,0,1;0rad)
  Radius = 2.65
FEATURE [Part::Cylinder] Cylinder014005415  label="Válec369"
  Angle = 360
  AttacherType = Attacher::AttachEngine3D
  Height = 10
  Placement = pos=(0,0,-3) rot=(0,0,1;0rad)
  Radius = 7
FEATURE [Part::Cylinder] Cylinder014005416  label="unasec spodek027"
  Angle = 360
  AttacherType = Attacher::AttachEngine3D
  Height = 1.5
  Placement = pos=(0,0,-1.5) rot=(0,0,1;0rad)
  Radius = 15.5
FEATURE [Part::Cylinder] Cylinder014005417  label="Válec370"
  Angle = 360
  AttacherType = Attacher::AttachEngine3D
  Height = 4
  Placement = pos=(0,0,7) rot=(0,0,1;0rad)
  Radius = 6.5
FEATURE [Part::Cylinder] Cylinder014005418  label="Válec371"
  Angle = 360
  AttacherType = Attacher::AttachEngine3D
  Height = 7
  Placement = pos=(0,0,-7) rot=(0,0,1;0rad)
  Radius = 12
FEATURE [Part::FeaturePython] Nut019  label="M8-Nut003"  # Fasteners workbench fastener (typed FeaturePython)
  Placement = pos=(0,0,-68) rot=(0,0,1;0rad)
  diameter = 9
  invert = false
  matchOuter = false
  offset = 0
  thread = false
  type = 3
FEATURE [Part::FeaturePython] InvoluteGear025  # WARN: FeaturePython — macro-defined, semantics opaque (R4)
  backlash = 0
  beta = 0
  clearance = 0.25
  double_helix = false
  head = 0
  height = 5.5
  module = 1.2
  numpoints = 6
  pressure_angle = 20
  reversed_backlash = false
  shift = 0
  simple = false
  teeth = 27
  undercut = false
FEATURE [Part::FeaturePython] InvoluteGear026  # WARN: FeaturePython — macro-defined, semantics opaque (R4)
  backlash = 0
  beta = 0
  clearance = 0.25
  double_helix = false
  head = 0
  height = 5.5
  module = 1.2
  numpoints = 6
  pressure_angle = 20
  reversed_backlash = false
  shift = 0
  simple = false
  teeth = 27
  undercut = false
FEATURE [Part::Feature] Cylinder014005419  label="Válec372"
  Placement = pos=(0,0,0) rot=(0,0,1;4.18879rad)
  shape: bbox 16 x 16 x 10 mm, 3 faces (baked)
FEATURE [Part::Feature] Screw_solid101  label="M2x4-Screw (Solid)101"
  Placement = pos=(0,0,0) rot=(0,0,-1;1.0472rad)
  shape: bbox 3.6 x 3.6 x 4 mm, 12 faces (baked)
FEATURE [Part::Feature] Cut005_solid001_cs012
  Placement = pos=(0,0,-11.25) rot=(0,0,1;0rad)
  shape: bbox 41 x 41 x 3e-07 mm, 0 faces, 0 solids (baked)
FEATURE [Part::Extrusion] Extrude036  label="box013"
  Base = -> Cut005_solid001_cs012
  Dir = (0,0,1)
  DirMode = 2
  FaceMakerClass = Part::FaceMakerBullseye
  LengthFwd = 19
  LengthRev = 0
  Placement = pos=(0,0,-11.5) rot=(0,0,1;0rad)
  Solid = true
  Symmetric = false
FEATURE [Part::Feature] Screw_solid102  label="M2x4-Screw (Solid)102"
  Placement = pos=(0,0,0) rot=(0,0,1;1.0472rad)
  shape: bbox 3.6 x 3.6 x 4 mm, 12 faces (baked)
FEATURE [Part::MultiFuse] Fusion256
  Shapes = -> [Cylinder014005394,Cylinder014005408,Cylinder014005419,Cylinder014005400]
FEATURE [Part::MultiFuse] Fusion260  label="srouby035"
  Placement = pos=(0,0,0.5) rot=(0,0,1;0rad)
  Shapes = -> [Screw_solid093,Screw_solid100,Screw_solid095]
FEATURE [Part::MultiFuse] Fusion261
  Shapes = -> [Cut007_solid013,Cylinder014005395,Cylinder014005418]
FEATURE [Part::MultiFuse] Fusion263
  Shapes = -> [Cylinder014005398,Cylinder014005396,Cylinder014005399]
FEATURE [Part::MultiFuse] Fusion267  label="srouby036"
  Shapes = -> [Screw_solid102,Screw_solid101,Screw_solid099]
FEATURE [Part::MultiFuse] Fusion269
  Shapes = -> [Cylinder014005405,Cylinder014005406,Cylinder014005402]
FEATURE [Part::Cylinder] Cylinder014005420  label="unasec spodek030"
  Angle = 360
  AttacherType = Attacher::AttachEngine3D
  Height = 1.5
  Placement = pos=(0,0,-1.5) rot=(0,0,1;0rad)
  Radius = 15.5
FEATURE [Part::MultiFuse] Fusion266
  Shapes = -> [Cylinder014005413,Cylinder014005420]
FEATURE [Part::Cut] Cut061112  label="unasec spodek025"
  Base = -> Fusion266
  Tool = -> Fusion256
FEATURE [Part::Cut] Cut061117  label="Uasec spodek012"
  Base = -> Cut061112
  Tool = -> Fusion267
FEATURE [Part::MultiFuse] Fusion255  label="Unasec spdek final011"
  Shapes = -> [Cut061117,Fusion269]
FEATURE [Part::Cylinder] Cylinder014005421  label="Válec373"
  Angle = 360
  AttacherType = Attacher::AttachEngine3D
  Height = 1.5
  Radius = 20
FEATURE [Part::Cylinder] Cylinder014005422  label="Válec374"
  Angle = 360
  AttacherType = Attacher::AttachEngine3D
  Height = 1.5
  Radius = 20
FEATURE [Part::Cylinder] Cylinder014005423  label="Válec375"
  Angle = 360
  AttacherType = Attacher::AttachEngine3D
  Height = 1.5
  Radius = 16
FEATURE [Part::Cut] Cut061119  label="Ring027"
  Base = -> Cylinder014005421
  Placement = pos=(0,0,-1.5) rot=(0,0,1;0rad)
  Tool = -> Cylinder014005423
FEATURE [Part::Cylinder] Cylinder014005424  label="Válec376"
  Angle = 360
  AttacherType = Attacher::AttachEngine3D
  Height = 1.5
  Radius = 16
FEATURE [Part::Cut] Cut061110  label="Ring025"
  Base = -> Cylinder014005422
  Placement = pos=(0,0,5.5) rot=(0,0,1;0rad)
  Tool = -> Cylinder014005424
FEATURE [Part::Cylinder] Cylinder014005425  label="Válec377"
  Angle = 360
  AttacherType = Attacher::AttachEngine3D
  Height = 5.5
  Radius = 20
FEATURE [Part::Cut] Cut061115  label="ring 013"
  Base = -> Cylinder014005425
  Tool = -> InvoluteGear024
FEATURE [Part::MultiFuse] Fusion265  label="Ring zaklad Fin011"
  Shapes = -> [Cut061115,Cut061110,Cut061119]
FEATURE [Part::Cylinder] Cylinder014005426  label="Unasec vrch019"
  Angle = 360
  AttacherType = Attacher::AttachEngine3D
  Height = 1.5
  Placement = pos=(0,0,5.5) rot=(0,0,1;0rad)
  Radius = 15.5
FEATURE [Part::Cut] Cut061113  label="unasec vrch019"
  Base = -> Cylinder014005426
  Tool = -> Fusion260
FEATURE [Part::FeaturePython] Screw010  label="M8x160-Screw003"  # Fasteners workbench fastener (typed FeaturePython)
  Placement = pos=(0,0,68.4) rot=(0,0,1;0rad)
  diameter = 9
  invert = false
  length = 16
  matchOuter = false
  offset = 0
  thread = false
  type = 13
FEATURE [Part::Cylinder] Cylinder014005427  label="unasec stred013"
  Angle = 360
  AttacherType = Attacher::AttachEngine3D
  Height = 7
  Placement = pos=(0,0,-1.5) rot=(0,0,1;0rad)
  Radius = 13.5
FEATURE [Part::MultiFuse] Fusion248
  Shapes = -> [Cylinder014005427,Cylinder014005416]
FEATURE [Part::Cylinder] Cylinder014005428  label="Válec378"
  Angle = 360
  AttacherType = Attacher::AttachEngine3D
  Height = 10
  Placement = pos=(10.5,0,0) rot=(0,0,1;0rad)
  Radius = 8
FEATURE [Part::MultiFuse] Fusion257
  Shapes = -> [Cylinder014005415,Cylinder014005428,Cylinder014005397,Cylinder014005401]
FEATURE [Part::Cut] Cut061111  label="unasec spodek024"
  Base = -> Fusion248
  Tool = -> Fusion257
FEATURE [Part::Cylinder] Cylinder014005429  label="Válec379"
  Angle = 360
  AttacherType = Attacher::AttachEngine3D
  Height = 5.5
  Radius = 20
FEATURE [Part::Cut] Cut061114  label="ring 012"
  Base = -> Cylinder014005429
  Tool = -> InvoluteGear026
FEATURE [Part::Cylinder] Cylinder014005430  label="Unasec vrch020"
  Angle = 360
  AttacherType = Attacher::AttachEngine3D
  Height = 1.5
  Placement = pos=(0,0,5.5) rot=(0,0,1;0rad)
  Radius = 15.5
FEATURE [Part::Cylinder] Cylinder014005431  label="Válec380"
  Angle = 360
  AttacherType = Attacher::AttachEngine3D
  Height = 7
  Radius = 2.6
FEATURE [Part::MultiFuse] Fusion262
  Placement = pos=(0,0,1) rot=(0,0,1;0rad)
  Shapes = -> [Fusion263,Cylinder014005431]
FEATURE [Part::Cut] Cut061116  label="Unasec Vrch zaklad019"
  Base = -> Cut061113
  Tool = -> Fusion262
FEATURE [Part::Cylinder] Cylinder014005432  label="Válec381"
  Angle = 360
  AttacherType = Attacher::AttachEngine3D
  Height = 7
  Radius = 2.6
FEATURE [Part::Cylinder] Cylinder014005433  label="Válec382"
  Angle = 360
  AttacherType = Attacher::AttachEngine3D
  Height = 10
  Placement = pos=(0,0,-3) rot=(0,0,1;0rad)
  Radius = 7
FEATURE [Part::Cylinder] Cylinder014005434  label="Válec383"
  Angle = 360
  AttacherType = Attacher::AttachEngine3D
  Height = 18
  Radius = 2.6
FEATURE [Part::Cylinder] Cylinder014005435  label="Válec384"
  Angle = 360
  AttacherType = Attacher::AttachEngine3D
  Height = 1.5
  Radius = 20
FEATURE [Part::Cut] Cut061109  label="Ring024"
  Base = -> Cylinder014005435
  Placement = pos=(0,0,5.5) rot=(0,0,1;0rad)
  Tool = -> Cylinder014005409
FEATURE [Part::Cylinder] Cylinder014005436  label="Válec385"
  Angle = 360
  AttacherType = Attacher::AttachEngine3D
  Height = 1.5
  Radius = 16
FEATURE [Part::Cylinder] Cylinder014005437  label="Válec386"
  Angle = 360
  AttacherType = Attacher::AttachEngine3D
  Height = 7
  Radius = 2.6
FEATURE [Part::Cylinder] Cylinder014005438  label="Válec387"
  Angle = 360
  AttacherType = Attacher::AttachEngine3D
  Height = 10
  Placement = pos=(10.5,0,0) rot=(0,0,1;0rad)
  Radius = 8
FEATURE [Part::Cylinder] Cylinder014005439  label="Unasec vrch021"
  Angle = 360
  AttacherType = Attacher::AttachEngine3D
  Height = 1.5
  Placement = pos=(0,0,5.5) rot=(0,0,1;0rad)
  Radius = 15.5
FEATURE [Part::Cylinder] Cylinder014005440  label="unasec stred014"
  Angle = 360
  AttacherType = Attacher::AttachEngine3D
  Height = 7
  Placement = pos=(0,0,-1.5) rot=(0,0,1;0rad)
  Radius = 13.5
FEATURE [Part::Cylinder] Cylinder014005441  label="Válec388"
  Angle = 360
  AttacherType = Attacher::AttachEngine3D
  Height = 1.5
  Radius = 20
FEATURE [Part::Cylinder] Cylinder014005442  label="Válec389"
  Angle = 360
  AttacherType = Attacher::AttachEngine3D
  Height = 18
  Radius = 2.6
FEATURE [Part::Cylinder] Cylinder014005443  label="Válec390"
  Angle = 360
  AttacherType = Attacher::AttachEngine3D
  Height = 10
  Placement = pos=(10.5,0,0) rot=(0,0,1;0rad)
  Radius = 8
FEATURE [Part::Cylinder] Cylinder014005444  label="Válec391"
  Angle = 360
  AttacherType = Attacher::AttachEngine3D
  Height = 1.5
  Radius = 16
FEATURE [Part::Cylinder] Cylinder014005445  label="Válec392"
  Angle = 360
  AttacherType = Attacher::AttachEngine3D
  Height = 5.5
  Radius = 20
FEATURE [Part::Cut] Cut061120  label="ring 014"
  Base = -> Cylinder014005445
  Tool = -> InvoluteGear025
FEATURE [Part::Cylinder] Cylinder014005446  label="Válec393"
  Angle = 360
  AttacherType = Attacher::AttachEngine3D
  Height = 1.5
  Radius = 20
FEATURE [Part::Cylinder] Cylinder014005447  label="Válec394"
  Angle = 360
  AttacherType = Attacher::AttachEngine3D
  Height = 1.5
  Radius = 20
FEATURE [Part::Cut] Cut061129  label="Ring029"
  Base = -> Cylinder014005447
  Placement = pos=(0,0,5.5) rot=(0,0,1;0rad)
  Tool = -> Cylinder014005436
FEATURE [Part::Cylinder] Cylinder014005448  label="Válec395"
  Angle = 360
  AttacherType = Attacher::AttachEngine3D
  Height = 10
  Placement = pos=(0,0,-3) rot=(0,0,1;0rad)
  Radius = 7
FEATURE [Part::Cylinder] Cylinder014005449  label="unasec spodek031"
  Angle = 360
  AttacherType = Attacher::AttachEngine3D
  Height = 1.5
  Placement = pos=(0,0,-1.5) rot=(0,0,1;0rad)
  Radius = 15.5
FEATURE [Part::Cylinder] Cylinder014005450  label="Válec396"
  Angle = 360
  AttacherType = Attacher::AttachEngine3D
  Height = 4
  Placement = pos=(0,0,7) rot=(0,0,1;0rad)
  Radius = 6.5
FEATURE [Part::Cylinder] Cylinder014005451  label="Válec397"
  Angle = 360
  AttacherType = Attacher::AttachEngine3D
  Height = 1.5
  Radius = 16
FEATURE [Part::Cut] Cut061124  label="Ring028"
  Base = -> Cylinder014005446
  Placement = pos=(0,0,-1.5) rot=(0,0,1;0rad)
  Tool = -> Cylinder014005451
FEATURE [Part::Feature] Cylinder014005452  label="Válec398"
  shape: bbox 5 x 5 x 7 mm, 3 faces (baked)
FEATURE [Part::Feature] Screw_solid103  label="M2x4-Screw (Solid)103"
  Placement = pos=(0,0,0) rot=(0,0,-1;1.0472rad)
  shape: bbox 3.6 x 3.6 x 4 mm, 12 faces (baked)
FEATURE [Part::Feature] Cylinder014005453  label="Válec399"
  Placement = pos=(0,0,0) rot=(0,0,1;4.18879rad)
  shape: bbox 16 x 16 x 10 mm, 3 faces (baked)
FEATURE [Part::Feature] Cut008_solid037  label="Planet038"
  Placement = pos=(0,0,0) rot=(0,0,1;2.0944rad)
  shape: bbox 12.9 x 13.1 x 5 mm, 57 faces (baked)
FEATURE [Part::Feature] Cut007_solid014  label="Sun015"
  Placement = pos=(0,0,10.5) rot=(0,0,1;0rad)
  shape: bbox 12.9 x 13.1 x 5 mm, 57 faces (baked)
FEATURE [Part::Feature] Cylinder014005454  label="Válec400"
  Placement = pos=(0,0,0) rot=(0,0,1;2.0944rad)
  shape: bbox 5 x 5 x 7 mm, 3 faces (baked)
FEATURE [Part::Feature] Cut007_solid015  label="Sun016"
  Placement = pos=(0,0,10.5) rot=(0,0,1;0rad)
  shape: bbox 12.9 x 13.1 x 5 mm, 57 faces (baked)
FEATURE [Part::Feature] Cylinder014005455  label="Válec401"
  Placement = pos=(0,0,0) rot=(0,0,1;2.0944rad)
  shape: bbox 16 x 16 x 10 mm, 3 faces (baked)
FEATURE [Part::Feature] Cut005_solid001_cs013
  Placement = pos=(0,0,-11.25) rot=(0,0,1;0rad)
  shape: bbox 41 x 41 x 3e-07 mm, 0 faces, 0 solids (baked)
FEATURE [Part::Extrusion] Extrude041  label="box014"
  Base = -> Cut005_solid001_cs013
  Dir = (0,0,1)
  DirMode = 2
  FaceMakerClass = Part::FaceMakerBullseye
  LengthFwd = 10.5
  LengthRev = 0
  Placement = pos=(0,0,-3) rot=(0,0,1;0rad)
  Solid = true
  Symmetric = false
FEATURE [Part::Feature] Screw_solid104  label="M2x4-Screw (Solid)104"
  Placement = pos=(0,0,0) rot=(0,0,-1;1.0472rad)
  shape: bbox 3.6 x 3.6 x 4 mm, 12 faces (baked)
FEATURE [Part::Feature] Cylinder014005456  label="Válec402"
  Placement = pos=(0,0,0) rot=(0,0,1;2.0944rad)
  shape: bbox 5 x 5 x 7 mm, 3 faces (baked)
FEATURE [Part::Feature] Cut008_solid038  label="Planet039"
  shape: bbox 12.9 x 13.1 x 5 mm, 57 faces (baked)
FEATURE [Part::Feature] Screw_solid105  label="M2x4-Screw (Solid)105"
  Placement = pos=(0,0,0) rot=(0,0,1;1.0472rad)
  shape: bbox 3.6 x 3.6 x 4 mm, 12 faces (baked)
FEATURE [Part::Feature] Cylinder014005457  label="Válec403"
  Placement = pos=(0,0,0) rot=(0,0,1;4.18879rad)
  shape: bbox 5 x 5 x 7 mm, 3 faces (baked)
FEATURE [Part::Feature] Screw_solid106  label="M2x4-Screw (Solid)106"
  Placement = pos=(0,0,0) rot=(0,0,1;1.0472rad)
  shape: bbox 3.6 x 3.6 x 4 mm, 12 faces (baked)
FEATURE [Part::Feature] Screw_solid107  label="M2x4-Screw (Solid)107"
  Placement = pos=(0,0,0) rot=(0,0,1;3.14159rad)
  shape: bbox 3.6 x 3.6 x 4 mm, 12 faces (baked)
FEATURE [Part::Feature] Cut005_solid001_cs014
  Placement = pos=(0,0,-11.25) rot=(0,0,1;0rad)
  shape: bbox 41 x 41 x 3e-07 mm, 0 faces, 0 solids (baked)
FEATURE [Part::Extrusion] Extrude042  label="box015"
  Base = -> Cut005_solid001_cs014
  Dir = (0,0,1)
  DirMode = 2
  FaceMakerClass = Part::FaceMakerBullseye
  LengthFwd = 10.5
  LengthRev = 0
  Placement = pos=(0,0,-3) rot=(0,0,1;0rad)
  Solid = true
  Symmetric = false
FEATURE [Part::Feature] Cylinder014005458  label="Válec404"
  Placement = pos=(0,0,0) rot=(0,0,1;4.18879rad)
  shape: bbox 5 x 5 x 7 mm, 3 faces (baked)
FEATURE [Part::Feature] Cut008_solid039  label="Planet040"
  Placement = pos=(0,0,0) rot=(0,0,1;4.18879rad)
  shape: bbox 12.9 x 13.1 x 5 mm, 57 faces (baked)
FEATURE [Part::Feature] Cut008_solid040  label="Planet041"
  shape: bbox 12.9 x 13.1 x 5 mm, 57 faces (baked)
FEATURE [Part::Feature] Screw_solid108  label="M2x4-Screw (Solid)108"
  Placement = pos=(0,0,0) rot=(0,0,1;1.0472rad)
  shape: bbox 3.6 x 3.6 x 4 mm, 12 faces (baked)
FEATURE [Part::MultiFuse] Fusion254  label="srouby033"
  Shapes = -> [Screw_solid108,Screw_solid103,Screw_solid107]
FEATURE [Part::Feature] Cylinder014005459  label="Válec405"
  Placement = pos=(0,0,0) rot=(0,0,1;4.18879rad)
  shape: bbox 5 x 5 x 7 mm, 3 faces (baked)
FEATURE [Part::Feature] Cylinder014005460  label="Válec406"
  shape: bbox 5 x 5 x 7 mm, 3 faces (baked)
FEATURE [Part::Feature] Cut007_solid016  label="Sun017"
  Placement = pos=(0,0,10.5) rot=(0,0,1;0rad)
  shape: bbox 12.9 x 13.1 x 5 mm, 57 faces (baked)
FEATURE [Part::MultiFuse] Fusion279
  Shapes = -> [Cylinder014005457,Cylinder014005403,Cylinder014005404]
FEATURE [Part::MultiFuse] Fusion280  label="srouby038"
  Shapes = -> [Screw_solid106,Screw_solid096,Screw_solid098]
FEATURE [Part::Cut] Cut061122  label="Uasec spodek013"
  Base = -> Cut061111
  Tool = -> Fusion280
FEATURE [Part::MultiFuse] Fusion287  label="Tělo I002"
  Shapes = -> [Extrude036,Fusion265]
FEATURE [Part::MultiFuse] Fusion290  label="Unasec spdek final013"
  Shapes = -> [Cut061122,Fusion279]
FEATURE [Part::MultiFuse] Fusion293
  Shapes = -> [Cylinder014005440,Cylinder014005449]
FEATURE [Part::MultiFuse] Fusion294
  Shapes = -> [Cylinder014005458,Cylinder014005452,Cylinder014005454]
FEATURE [Part::MultiFuse] Fusion297  label="srouby040"
  Placement = pos=(0,0,0.5) rot=(0,0,1;0rad)
  Shapes = -> [Screw_solid105,Screw_solid097,Screw_solid094]
FEATURE [Part::Cut] Cut061128  label="unasec vrch020"
  Base = -> Cylinder014005430
  Tool = -> Fusion297
FEATURE [Part::MultiFuse] Fusion298  label="Ring zaklad Fin013"
  Shapes = -> [Cut061120,Cut061129,Cut061124]
FEATURE [Part::MultiFuse] Fusion292  label="teloII011"
  Shapes = -> [Fusion298,Extrude042]
FEATURE [Part::MultiFuse] Fusion301
  Shapes = -> [Cylinder014005433,Cylinder014005438,Cylinder014005453,Cylinder014005455]
FEATURE [Part::Cut] Cut061125  label="unasec spodek026"
  Base = -> Fusion293
  Tool = -> Fusion301
FEATURE [Part::Cut] Cut061126  label="Uasec spodek014"
  Base = -> Cut061125
  Tool = -> Fusion254
FEATURE [Part::MultiFuse] Fusion295  label="Unasec spdek final014"
  Shapes = -> [Cut061126,Fusion294]
FEATURE [Part::MultiFuse] Fusion303  label="unasec vrhch 016"
  Shapes = -> [Cut061116,Cut007_solid015,Cylinder014005417]
FEATURE [Part::Cut] Cut061130  label="Unasec + Sun011"
  Base = -> Fusion303
  Tool = -> Cylinder014005407
FEATURE [Part::MultiFuse] Fusion313  label="Ring zaklad Fin015"
  Shapes = -> [Cut061114,Cut061109,Cut061118]
FEATURE [Part::MultiFuse] Fusion268  label="teloII009"
  Shapes = -> [Fusion313,Extrude041]
FEATURE [Part::Feature] Cut008_solid041  label="Planet042"
  shape: bbox 12.9 x 13.1 x 5 mm, 57 faces (baked)
FEATURE [Part::Feature] Cylinder014005461  label="Válec407"
  shape: bbox 5 x 5 x 7 mm, 3 faces (baked)
FEATURE [Part::Feature] Cut007_solid017  label="Sun018"
  Placement = pos=(0,0,10.5) rot=(0,0,1;0rad)
  shape: bbox 12.9 x 13.1 x 5 mm, 57 faces (baked)
FEATURE [Part::Feature] Screw_solid109  label="M2x4-Screw (Solid)109"
  Placement = pos=(0,0,0) rot=(0,0,1;3.14159rad)
  shape: bbox 3.6 x 3.6 x 4 mm, 12 faces (baked)
FEATURE [Part::Feature] Screw_solid110  label="M2x4-Screw (Solid)110"
  Placement = pos=(0,0,0) rot=(0,0,1;1.0472rad)
  shape: bbox 3.6 x 3.6 x 4 mm, 12 faces (baked)
FEATURE [Part::Feature] Cylinder014005462  label="Válec408"
  Placement = pos=(0,0,0) rot=(0,0,1;2.0944rad)
  shape: bbox 5 x 5 x 7 mm, 3 faces (baked)
FEATURE [Part::Feature] Screw_solid111  label="M2x4-Screw (Solid)111"
  Placement = pos=(0,0,0) rot=(0,0,1;3.14159rad)
  shape: bbox 3.6 x 3.6 x 4 mm, 12 faces (baked)
FEATURE [Part::MultiFuse] Fusion309  label="srouby042"
  Placement = pos=(0,0,0.5) rot=(0,0,1;0rad)
  Shapes = -> [Screw_solid110,Screw_solid104,Screw_solid111]
FEATURE [Part::Cut] Cut061131  label="unasec vrch021"
  Base = -> Cylinder014005439
  Tool = -> Fusion309
FEATURE [Part::Feature] Cut008_solid042  label="Planet043"
  Placement = pos=(0,0,0) rot=(0,0,1;4.18879rad)
  shape: bbox 12.9 x 13.1 x 5 mm, 57 faces (baked)
FEATURE [Part::Feature] Screw_solid112  label="M2x4-Screw (Solid)112"
  Placement = pos=(0,0,0) rot=(0,0,1;1.0472rad)
  shape: bbox 3.6 x 3.6 x 4 mm, 12 faces (baked)
FEATURE [Part::Feature] Cut005_solid001_cs015
  Placement = pos=(0,0,-11.25) rot=(0,0,1;0rad)
  shape: bbox 41 x 41 x 3e-07 mm, 0 faces, 0 solids (baked)
FEATURE [Part::Extrusion] Extrude035  label="box012"
  Base = -> Cut005_solid001_cs015
  Dir = (0,0,1)
  DirMode = 2
  FaceMakerClass = Part::FaceMakerBullseye
  LengthFwd = 10.5
  LengthRev = 0
  Placement = pos=(0,0,-3) rot=(0,0,1;0rad)
  Solid = true
  Symmetric = false
FEATURE [Part::Feature] Cylinder014005463  label="Válec409"
  Placement = pos=(0,0,0) rot=(0,0,1;2.0944rad)
  shape: bbox 16 x 16 x 10 mm, 3 faces (baked)
FEATURE [Part::Feature] Cylinder014005464  label="Válec410"
  Placement = pos=(0,0,0) rot=(0,0,1;2.0944rad)
  shape: bbox 5 x 5 x 7 mm, 3 faces (baked)
FEATURE [Part::Feature] Cylinder014005465  label="Válec411"
  Placement = pos=(0,0,0) rot=(0,0,1;4.18879rad)
  shape: bbox 5 x 5 x 7 mm, 3 faces (baked)
FEATURE [Part::Feature] Cylinder014005466  label="Válec412"
  shape: bbox 5 x 5 x 7 mm, 3 faces (baked)
FEATURE [Part::MultiFuse] Fusion246
  Shapes = -> [Cylinder014005465,Cylinder014005466,Cylinder014005464]
FEATURE [Part::Feature] Screw_solid113  label="M2x4-Screw (Solid)113"
  Placement = pos=(0,0,0) rot=(0,0,1;1.0472rad)
  shape: bbox 3.6 x 3.6 x 4 mm, 12 faces (baked)
FEATURE [Part::Feature] Cut008_solid043  label="Planet044"
  Placement = pos=(0,0,0) rot=(0,0,1;2.0944rad)
  shape: bbox 12.9 x 13.1 x 5 mm, 57 faces (baked)
FEATURE [Part::Feature] Screw_solid114  label="M2x4-Screw (Solid)114"
  Placement = pos=(0,0,0) rot=(0,0,-1;1.0472rad)
  shape: bbox 3.6 x 3.6 x 4 mm, 12 faces (baked)
FEATURE [Part::Feature] Cylinder014005467  label="Válec413"
  Placement = pos=(0,0,0) rot=(0,0,1;4.18879rad)
  shape: bbox 16 x 16 x 10 mm, 3 faces (baked)
FEATURE [Part::MultiFuse] Fusion251
  Shapes = -> [Cylinder014005448,Cylinder014005443,Cylinder014005467,Cylinder014005463]
FEATURE [Part::Feature] Cylinder014005468  label="Válec414"
  Placement = pos=(0,0,0) rot=(0,0,1;4.18879rad)
  shape: bbox 5 x 5 x 7 mm, 3 faces (baked)
FEATURE [Part::MultiFuse] Fusion247
  Shapes = -> [Cylinder014005468,Cylinder014005460,Cylinder014005456]
FEATURE [Part::MultiFuse] Fusion291
  Placement = pos=(0,0,1) rot=(0,0,1;0rad)
  Shapes = -> [Fusion247,Cylinder014005437]
FEATURE [Part::Cut] Cut061127  label="Unasec Vrch zaklad020"
  Base = -> Cut061128
  Tool = -> Fusion291
FEATURE [Part::MultiFuse] Fusion252  label="unasec vrhch 014"
  Shapes = -> [Cut061127,Cut007_solid014,Cylinder014005412]
FEATURE [Part::Cut] Cut061121  label="Unasec + Sun009"
  Base = -> Fusion252
  Tool = -> Cylinder014005434
FEATURE [App::Part] Part030  label="Part074"
  Group = -> [Cut061111,Cut061122,Cylinder014005415,Cylinder014005416,Cylinder014005427,Cylinder014005428,Cylinder014005397,Cylinder014005404,Cylinder014005401,Screw_solid098,Cylinder014005403,Screw_solid106,Cylinder014005457,Screw_solid096,Fusion257,Fusion248,Fusion280,Fusion279,Fusion290,Cut008_solid038,Cut008_solid037,Cut008_solid033,Screw_solid105,Cylinder014005460,Cylinder014005456,Screw_solid097,+27 more]
  License = CC BY 3.0
  LicenseURL = http://creativecommons.org/licenses/by/3.0/
  Origin = -> Origin027
  Placement = pos=(0,0,10.5) rot=(0,0,1;0rad)
FEATURE [Part::Feature] Cylinder014005469  label="Válec415"
  Placement = pos=(0,0,0) rot=(0,0,1;4.18879rad)
  shape: bbox 5 x 5 x 7 mm, 3 faces (baked)
FEATURE [Part::Feature] Cylinder014005470  label="Válec416"
  Placement = pos=(0,0,0) rot=(0,0,1;2.0944rad)
  shape: bbox 5 x 5 x 7 mm, 3 faces (baked)
FEATURE [Part::Feature] Cut007_solid018  label="Sun019"
  Placement = pos=(0,0,10.5) rot=(0,0,1;0rad)
  shape: bbox 12.9 x 13.1 x 5 mm, 57 faces (baked)
FEATURE [Part::Feature] Cut008_solid044  label="Planet045"
  Placement = pos=(0,0,0) rot=(0,0,1;2.0944rad)
  shape: bbox 12.9 x 13.1 x 5 mm, 57 faces (baked)
FEATURE [Part::Feature] Cylinder014005471  label="Válec417"
  shape: bbox 5 x 5 x 7 mm, 3 faces (baked)
FEATURE [Part::MultiFuse] Fusion253
  Shapes = -> [Cylinder014005459,Cylinder014005471,Cylinder014005470]
FEATURE [Part::MultiFuse] Fusion278
  Placement = pos=(0,0,1) rot=(0,0,1;0rad)
  Shapes = -> [Fusion253,Cylinder014005432]
FEATURE [Part::Cut] Cut061132  label="Unasec Vrch zaklad021"
  Base = -> Cut061131
  Tool = -> Fusion278
FEATURE [Part::MultiFuse] Fusion299  label="unasec vrhch 015"
  Shapes = -> [Cut061132,Cut007_solid016,Cylinder014005450]
FEATURE [Part::Cut] Cut061123  label="Unasec + Sun010"
  Base = -> Fusion299
  Tool = -> Cylinder014005442
FEATURE [App::Part] Part029  label="Part073"
  Group = -> [Cut061125,Cut061126,Cylinder014005433,Cylinder014005449,Cylinder014005440,Cylinder014005438,Cylinder014005453,Cylinder014005454,Cylinder014005455,Screw_solid107,Cylinder014005452,Screw_solid108,Cylinder014005458,Screw_solid103,Fusion301,Fusion293,Fusion254,Fusion294,Fusion295,Cut008_solid040,Cut008_solid044,Cut008_solid039,Screw_solid110,Cylinder014005471,Cylinder014005470,Screw_solid104,+27 more]
  License = CC BY 3.0
  LicenseURL = http://creativecommons.org/licenses/by/3.0/
  Origin = -> Origin028
  Placement = pos=(0,0,21) rot=(0,0,1;0rad)
FEATURE [Part::Feature] Screw_solid115  label="M2x4-Screw (Solid)115"
  Placement = pos=(0,0,0) rot=(0,0,1;3.14159rad)
  shape: bbox 3.6 x 3.6 x 4 mm, 12 faces (baked)
FEATURE [Part::MultiFuse] Fusion250  label="srouby032"
  Shapes = -> [Screw_solid112,Screw_solid114,Screw_solid115]
FEATURE [Part::Feature] Screw_solid116  label="M2x4-Screw (Solid)116"
  Placement = pos=(0,0,0) rot=(0,0,1;3.14159rad)
  shape: bbox 3.6 x 3.6 x 4 mm, 12 faces (baked)
FEATURE [Part::Feature] Screw_solid117  label="M2x4-Screw (Solid)117"
  Placement = pos=(0,0,0) rot=(0,0,1;3.14159rad)
  shape: bbox 3.6 x 3.6 x 4 mm, 12 faces (baked)
FEATURE [Part::Feature] Screw_solid118  label="M2x4-Screw (Solid)118"
  Placement = pos=(0,0,0) rot=(0,0,1;1.0472rad)
  shape: bbox 3.6 x 3.6 x 4 mm, 12 faces (baked)
FEATURE [Part::Feature] Cut061152  label="SUN I Final002"
  shape: bbox 24 x 24 x 12.25 mm, 99 faces (baked)
FEATURE [App::Part] Part031
  Group = -> [Cut008_solid034,Cut008_solid036,Cut008_solid035,Cylinder014005420,Cylinder014005394,Cylinder014005408,Fusion256,Fusion266,Cylinder014005405,Cylinder014005402,Cylinder014005419,Cylinder014005400,Cylinder014005406,Cylinder014005413,Cut061112,Cut061117,Screw_solid099,Screw_solid102,Screw_solid101,Fusion269,Fusion267,Fusion255,Cylinder014005417,Cylinder014005407,Cut007_solid015,Cut061113,Cut061116,+32 more]
  License = CC BY 3.0
  LicenseURL = http://creativecommons.org/licenses/by/3.0/
  Origin = -> Origin029
FEATURE [Part::Feature] Screw_solid119  label="M2x4-Screw (Solid)119"
  Placement = pos=(0,0,0) rot=(0,0,1;3.14159rad)
  shape: bbox 3.6 x 3.6 x 4 mm, 12 faces (baked)
FEATURE [Part::Feature] Cylinder014005472  label="Válec418"
  Placement = pos=(0,0,0) rot=(0,0,1;4.18879rad)
  shape: bbox 16 x 16 x 10 mm, 3 faces (baked)
FEATURE [Part::Feature] Screw_solid120  label="M2x4-Screw (Solid)120"
  Placement = pos=(0,0,0) rot=(0,0,1;1.0472rad)
  shape: bbox 3.6 x 3.6 x 4 mm, 12 faces (baked)
FEATURE [Part::Feature] Cylinder014005473  label="Válec419"
  Placement = pos=(0,0,0) rot=(0,0,1;4.18879rad)
  shape: bbox 5 x 5 x 7 mm, 3 faces (baked)
FEATURE [Part::Feature] Cut008_solid045  label="Planet046"
  Placement = pos=(0,0,0) rot=(0,0,1;4.18879rad)
  shape: bbox 12.9 x 13.1 x 5 mm, 57 faces (baked)
FEATURE [Part::Feature] Cut008_solid046  label="Planet047"
  Placement = pos=(0,0,0) rot=(0,0,1;2.0944rad)
  shape: bbox 12.9 x 13.1 x 5 mm, 57 faces (baked)
FEATURE [Part::Feature] Cylinder014005474  label="Válec420"
  Placement = pos=(0,0,0) rot=(0,0,1;4.18879rad)
  shape: bbox 5 x 5 x 7 mm, 3 faces (baked)
FEATURE [Part::Feature] Cylinder014005475  label="Válec421"
  shape: bbox 5 x 5 x 7 mm, 3 faces (baked)
FEATURE [Part::MultiFuse] Fusion300
  Shapes = -> [Cylinder014005469,Cylinder014005475,Cylinder014005462]
FEATURE [Part::Feature] Cylinder014005476  label="Válec422"
  Placement = pos=(0,0,0) rot=(0,0,1;2.0944rad)
  shape: bbox 5 x 5 x 7 mm, 3 faces (baked)
FEATURE [Part::Feature] Cylinder014005477  label="Válec423"
  Placement = pos=(0,0,0) rot=(0,0,1;2.0944rad)
  shape: bbox 5 x 5 x 7 mm, 3 faces (baked)
FEATURE [Part::Feature] Screw_solid121  label="M2x4-Screw (Solid)121"
  Placement = pos=(0,0,0) rot=(0,0,-1;1.0472rad)
  shape: bbox 3.6 x 3.6 x 4 mm, 12 faces (baked)
FEATURE [Part::MultiFuse] Fusion277  label="srouby037"
  Shapes = -> [Screw_solid120,Screw_solid121,Screw_solid116]
FEATURE [Part::Feature] Cylinder014005478  label="Válec424"
  shape: bbox 5 x 5 x 7 mm, 3 faces (baked)
FEATURE [Part::Feature] Screw_solid122  label="M2x4-Screw (Solid)122"
  Placement = pos=(0,0,0) rot=(0,0,-1;1.0472rad)
  shape: bbox 3.6 x 3.6 x 4 mm, 12 faces (baked)
FEATURE [Part::Feature] Screw_solid123  label="M2x4-Screw (Solid)123"
  Placement = pos=(0,0,0) rot=(0,0,-1;1.0472rad)
  shape: bbox 3.6 x 3.6 x 4 mm, 12 faces (baked)
FEATURE [Part::MultiFuse] Fusion306  label="srouby041"
  Placement = pos=(0,0,0.5) rot=(0,0,1;0rad)
  Shapes = -> [Screw_solid113,Screw_solid123,Screw_solid109]
FEATURE [Part::Feature] Cylinder014005479  label="Válec425"
  Placement = pos=(0,0,0) rot=(0,0,1;2.0944rad)
  shape: bbox 16 x 16 x 10 mm, 3 faces (baked)
FEATURE [Part::Feature] Screw_solid124  label="M2x4-Screw (Solid)124"
  Placement = pos=(0,0,0) rot=(0,0,-1;1.0472rad)
  shape: bbox 3.6 x 3.6 x 4 mm, 12 faces (baked)
FEATURE [Part::MultiFuse] Fusion310  label="srouby043"
  Placement = pos=(0,0,0.5) rot=(0,0,1;0rad)
  Shapes = -> [Screw_solid118,Screw_solid124,Screw_solid117]
FEATURE [Part::Feature] Cylinder014005480  label="Válec426"
  Placement = pos=(0,0,0) rot=(0,0,1;2.0944rad)
  shape: bbox 5 x 5 x 7 mm, 3 faces (baked)
FEATURE [Part::MultiFuse] Fusion275
  Shapes = -> [Cylinder014005473,Cylinder014005461,Cylinder014005480]
FEATURE [Part::Feature] Cylinder014005481  label="Válec427"
  shape: bbox 5 x 5 x 7 mm, 3 faces (baked)
FEATURE [Part::MultiFuse] Fusion305
  Shapes = -> [Cylinder014005474,Cylinder014005481,Cylinder014005476]
FEATURE [Part::Feature] Cut008_solid047  label="Planet048"
  shape: bbox 12.9 x 13.1 x 5 mm, 57 faces (baked)
FEATURE [Part::Cylinder] Cylinder014005482  label="Válec428"
  Angle = 360
  AttacherType = Attacher::AttachEngine3D
  Height = 7
  Radius = 2.6
FEATURE [Part::MultiFuse] Fusion288
  Placement = pos=(0,0,1) rot=(0,0,1;0rad)
  Shapes = -> [Fusion246,Cylinder014005482]
FEATURE [Part::Cylinder] Cylinder014005483  label="Válec429"
  Angle = 360
  AttacherType = Attacher::AttachEngine3D
  Height = 4
  Placement = pos=(0,0,7) rot=(0,0,1;0rad)
  Radius = 6.5
FEATURE [Part::Cylinder] Cylinder014005484  label="Válec430"
  Angle = 360
  AttacherType = Attacher::AttachEngine3D
  Height = 5.5
  Radius = 20
FEATURE [Part::Cut] Cut061140  label="ring 016"
  Base = -> Cylinder014005484
  Tool = -> InvoluteGear023
FEATURE [Part::Cylinder] Cylinder014005485  label="Válec431"
  Angle = 360
  AttacherType = Attacher::AttachEngine3D
  Height = 1.5
  Radius = 20
FEATURE [Part::Cylinder] Cylinder014005486  label="Válec432"
  Angle = 360
  AttacherType = Attacher::AttachEngine3D
  Height = 1.5
  Radius = 20
FEATURE [Part::Cut] Cut061137  label="Ring031"
  Base = -> Cylinder014005486
  Placement = pos=(0,0,-1.5) rot=(0,0,1;0rad)
  Tool = -> Cylinder014005444
FEATURE [Part::Cylinder] Cylinder014005487  label="Válec433"
  Angle = 360
  AttacherType = Attacher::AttachEngine3D
  Height = 1.5
  Radius = 16
FEATURE [Part::Cut] Cut061149  label="Ring033"
  Base = -> Cylinder014005485
  Placement = pos=(0,0,5.5) rot=(0,0,1;0rad)
  Tool = -> Cylinder014005487
FEATURE [Part::Cylinder] Cylinder014005488  label="Unasec vrch022"
  Angle = 360
  AttacherType = Attacher::AttachEngine3D
  Height = 1.5
  Placement = pos=(0,0,5.5) rot=(0,0,1;0rad)
  Radius = 15.5
FEATURE [Part::Cut] Cut061139  label="unasec vrch022"
  Base = -> Cylinder014005488
  Tool = -> Fusion306
FEATURE [Part::Cut] Cut061141  label="Unasec Vrch zaklad023"
  Base = -> Cut061139
  Tool = -> Fusion288
FEATURE [Part::MultiFuse] Fusion249  label="unasec vrhch 013"
  Shapes = -> [Cut061141,Cut007_solid018,Cylinder014005483]
FEATURE [Part::Cylinder] Cylinder014005489  label="Válec434"
  Angle = 360
  AttacherType = Attacher::AttachEngine3D
  Height = 18
  Radius = 2.6
FEATURE [Part::Cut] Cut061134  label="Unasec + Sun012"
  Base = -> Fusion249
  Tool = -> Cylinder014005489
FEATURE [Part::Cylinder] Cylinder014005490  label="unasec spodek032"
  Angle = 360
  AttacherType = Attacher::AttachEngine3D
  Height = 1.5
  Placement = pos=(0,0,-1.5) rot=(0,0,1;0rad)
  Radius = 15.5
FEATURE [Part::Cylinder] Cylinder014005491  label="unasec stred015"
  Angle = 360
  AttacherType = Attacher::AttachEngine3D
  Height = 7
  Placement = pos=(0,0,-1.5) rot=(0,0,1;0rad)
  Radius = 13.5
FEATURE [Part::MultiFuse] Fusion286
  Shapes = -> [Cylinder014005491,Cylinder014005490]
FEATURE [Part::Cut] Cut061148  label="unasec spodek028"
  Base = -> Fusion286
  Tool = -> Fusion251
FEATURE [Part::Cut] Cut061135  label="Uasec spodek015"
  Base = -> Cut061148
  Tool = -> Fusion250
FEATURE [Part::MultiFuse] Fusion314  label="Unasec spdek final015"
  Shapes = -> [Cut061135,Fusion300]
FEATURE [Part::Cylinder] Cylinder014005492  label="Válec435"
  Angle = 360
  AttacherType = Attacher::AttachEngine3D
  Height = 1.5
  Radius = 16
FEATURE [Part::Cut] Cut061136  label="Ring030"
  Base = -> Cylinder014005441
  Placement = pos=(0,0,5.5) rot=(0,0,1;0rad)
  Tool = -> Cylinder014005492
FEATURE [Part::Cylinder] Cylinder014005493  label="Válec436"
  Angle = 360
  AttacherType = Attacher::AttachEngine3D
  Height = 5.5
  Radius = 20
FEATURE [Part::Cut] Cut061133  label="ring 015"
  Base = -> Cylinder014005493
  Tool = -> InvoluteGear022
FEATURE [Part::MultiFuse] Fusion302  label="Ring zaklad Fin014"
  Shapes = -> [Cut061133,Cut061136,Cut061137]
FEATURE [Part::MultiFuse] Fusion281  label="teloII010"
  Shapes = -> [Fusion302,Extrude035]
FEATURE [App::Part] Part033
  Group = -> [Cut061148,Cut061135,Cylinder014005448,Cylinder014005490,Cylinder014005491,Cylinder014005443,Cylinder014005467,Cylinder014005462,Cylinder014005463,Screw_solid115,Cylinder014005475,Screw_solid112,Cylinder014005469,Screw_solid114,Fusion251,Fusion286,Fusion250,Fusion300,Fusion314,Cut008_solid041,Cut008_solid043,Cut008_solid042,Screw_solid113,Cylinder014005466,Cylinder014005464,Screw_solid123,+27 more]
  License = CC BY 3.0
  LicenseURL = http://creativecommons.org/licenses/by/3.0/
  Origin = -> Origin033
  Placement = pos=(0,0,31.5) rot=(0,0,1;0rad)
FEATURE [Part::Cylinder] Cylinder014005494  label="Unasec vrch023"
  Angle = 360
  AttacherType = Attacher::AttachEngine3D
  Height = 1.5
  Placement = pos=(0,0,5.5) rot=(0,0,1;0rad)
  Radius = 15.5
FEATURE [Part::Cut] Cut061145  label="unasec vrch024"
  Base = -> Cylinder014005494
  Tool = -> Fusion310
FEATURE [Part::Cylinder] Cylinder014005495  label="Válec437"
  Angle = 360
  AttacherType = Attacher::AttachEngine3D
  Height = 10
  Placement = pos=(0,0,-3) rot=(0,0,1;0rad)
  Radius = 7
FEATURE [Part::Cylinder] Cylinder014005496  label="Válec438"
  Angle = 360
  AttacherType = Attacher::AttachEngine3D
  Height = 6
  Placement = pos=(0,0,7) rot=(0,0,1;0rad)
  Radius = 6.5
FEATURE [Part::Cylinder] Cylinder014005497  label="Válec439"
  Angle = 360
  AttacherType = Attacher::AttachEngine3D
  Height = 1.5
  Radius = 20
FEATURE [Part::Cylinder] Cylinder014005498  label="Válec440"
  Angle = 360
  AttacherType = Attacher::AttachEngine3D
  Height = 4
  Placement = pos=(0,0,7) rot=(0,0,1;0rad)
  Radius = 6.5
FEATURE [Part::Cylinder] Cylinder014005499  label="Válec441"
  Angle = 360
  AttacherType = Attacher::AttachEngine3D
  Height = 18
  Radius = 2.6
FEATURE [Part::Cylinder] Cylinder014005500  label="Válec442"
  Angle = 360
  AttacherType = Attacher::AttachEngine3D
  Height = 7
  Radius = 2.6
FEATURE [Part::MultiFuse] Fusion308
  Placement = pos=(0,0,1) rot=(0,0,1;0rad)
  Shapes = -> [Fusion275,Cylinder014005500]
FEATURE [Part::Cylinder] Cylinder014005501  label="Válec443"
  Angle = 360
  AttacherType = Attacher::AttachEngine3D
  Height = 22
  Radius = 2.6
FEATURE [Part::MultiFuse] Fusion276
  Shapes = -> [Cylinder014005501,Extrude037]
FEATURE [Part::Cylinder] Cylinder014005502  label="Unasec vrch024"
  Angle = 360
  AttacherType = Attacher::AttachEngine3D
  Height = 1.5
  Placement = pos=(0,0,5.5) rot=(0,0,1;0rad)
  Radius = 15.5
FEATURE [Part::Cylinder] Cylinder014005503  label="Válec444"
  Angle = 360
  AttacherType = Attacher::AttachEngine3D
  Height = 1.5
  Radius = 16
FEATURE [Part::Cut] Cut061144  label="Ring032"
  Base = -> Cylinder014005497
  Placement = pos=(0,0,-1.5) rot=(0,0,1;0rad)
  Tool = -> Cylinder014005503
FEATURE [Part::MultiFuse] Fusion283  label="Ring zaklad Fin012"
  Shapes = -> [Cut061140,Cut061149,Cut061144]
FEATURE [Part::Cylinder] Cylinder014005504  label="Válec445"
  Angle = 360
  AttacherType = Attacher::AttachEngine3D
  Height = 10
  Placement = pos=(10.5,0,0) rot=(0,0,1;0rad)
  Radius = 8
FEATURE [Part::MultiFuse] Fusion284
  Shapes = -> [Cylinder014005495,Cylinder014005504,Cylinder014005472,Cylinder014005479]
FEATURE [Part::Cylinder] Cylinder014005505  label="unasec stred016"
  Angle = 360
  AttacherType = Attacher::AttachEngine3D
  Height = 7
  Placement = pos=(0,0,-1.5) rot=(0,0,1;0rad)
  Radius = 13.5
FEATURE [Part::Cylinder] Cylinder014005506  label="unasec spodek033"
  Angle = 360
  AttacherType = Attacher::AttachEngine3D
  Height = 1.5
  Placement = pos=(0,0,-1.5) rot=(0,0,1;0rad)
  Radius = 15.5
FEATURE [Part::MultiFuse] Fusion312
  Shapes = -> [Cylinder014005505,Cylinder014005506]
FEATURE [Part::Cut] Cut061151  label="unasec spodek029"
  Base = -> Fusion312
  Tool = -> Fusion284
FEATURE [Part::Cut] Cut061150  label="Uasec spodek016"
  Base = -> Cut061151
  Tool = -> Fusion277
FEATURE [Part::MultiFuse] Fusion289  label="Unasec spdek final012"
  Shapes = -> [Cut061150,Fusion305]
FEATURE [Part::Cylinder] Cylinder014005507  label="Válec446"
  Angle = 360
  AttacherType = Attacher::AttachEngine3D
  Height = 7
  Radius = 2.6
FEATURE [Part::Box] Box060  label="Krychle048"
  AttacherType = Attacher::AttachEngine3D
  Height = 40
  Length = 41
  Placement = pos=(-20.5,-20.5,0) rot=(0,0,1;0rad)
  Width = 41
FEATURE [Part::Chamfer] Chamfer011
  Base = -> Box060
  Edges = 4 edges r=5: [Edge1,Edge3,Edge5,Edge7]
FEATURE [Part::Cylinder] Cylinder014005508  label="Válec447"
  Angle = 360
  AttacherType = Attacher::AttachEngine3D
  Height = 50
  Placement = pos=(-15.5,-15.5,0) rot=(0,0,1;0rad)
  Radius = 1.6
FEATURE [Part::Cylinder] Cylinder014005509  label="Válec448"
  Angle = 360
  AttacherType = Attacher::AttachEngine3D
  Height = 50
  Placement = pos=(15.5,15.5,0) rot=(0,0,1;0rad)
  Radius = 1.6
FEATURE [Part::Cylinder] Cylinder014005510  label="Válec449"
  Angle = 360
  AttacherType = Attacher::AttachEngine3D
  Height = 50
  Placement = pos=(15.5,-15.5,0) rot=(0,0,1;0rad)
  Radius = 1.6
FEATURE [Part::Cylinder] Cylinder014005511  label="Válec450"
  Angle = 360
  AttacherType = Attacher::AttachEngine3D
  Height = 50
  Placement = pos=(-15.5,15.5,0) rot=(0,0,1;0rad)
  Radius = 1.6
FEATURE [Part::MultiFuse] Fusion315  label="diry008"
  Shapes = -> [Cylinder014005511,Cylinder014005509,Cylinder014005508,Cylinder014005510]
FEATURE [Part::Cut] Cut061155
  Base = -> Chamfer011
  Tool = -> Fusion315
FEATURE [App::Part] Part027  label="NEAM17  motor- 40mm002"
  Group = -> [Chamfer011,Fusion315,Box060,Cylinder014005511,Cylinder014005509,Cylinder014005508,Cylinder014005510,Cut061155]
  License = CC BY 3.0
  LicenseURL = http://creativecommons.org/licenses/by/3.0/
  Origin = -> Origin031
  Placement = pos=(0,0,-51.5) rot=(0,0,1;0rad)
FEATURE [Part::Feature] Screw_solid125  label="M2x4-Screw (Solid)125"
  Placement = pos=(0,0,0) rot=(0,0,1;1.0472rad)
  shape: bbox 3.6 x 3.6 x 4 mm, 12 faces (baked)
FEATURE [Part::MultiFuse] Fusion282  label="srouby039"
  Placement = pos=(0,0,0.5) rot=(0,0,1;0rad)
  Shapes = -> [Screw_solid125,Screw_solid122,Screw_solid119]
FEATURE [Part::Cut] Cut061143  label="unasec vrch023"
  Base = -> Cylinder014005502
  Tool = -> Fusion282
FEATURE [Part::Cut] Cut061146  label="Unasec Vrch zaklad024"
  Base = -> Cut061143
  Tool = -> Fusion308
FEATURE [Part::MultiFuse] Fusion304  label="unasec vrhch 017"
  Shapes = -> [Cut061146,Cut007_solid017,Cylinder014005498]
FEATURE [Part::Cut] Cut061142  label="Unasec + Sun005 old002"
  Base = -> Fusion304
  Tool = -> Cylinder014005499
FEATURE [Part::Feature] Cut005_solid001_cs016
  Placement = pos=(0,0,-11.25) rot=(0,0,1;0rad)
  shape: bbox 41 x 41 x 3e-07 mm, 0 faces, 0 solids (baked)
FEATURE [Part::Extrusion] Extrude034  label="box011"
  Base = -> Cut005_solid001_cs016
  Dir = (0,0,1)
  DirMode = 2
  FaceMakerClass = Part::FaceMakerBullseye
  LengthFwd = 10.5
  LengthRev = 0
  Placement = pos=(0,0,-3) rot=(0,0,1;0rad)
  Solid = true
  Symmetric = false
FEATURE [Part::MultiFuse] Fusion296  label="teloII012"
  Shapes = -> [Fusion283,Extrude034]
FEATURE [Part::Feature] Screw_solid126  label="M2x4-Screw (Solid)126"
  Placement = pos=(0,0,0) rot=(0,0,1;1.0472rad)
  shape: bbox 3.6 x 3.6 x 4 mm, 12 faces (baked)
FEATURE [Part::Feature] Screw_solid127  label="M2x4-Screw (Solid)127"
  Placement = pos=(0,0,0) rot=(0,0,-1;1.0472rad)
  shape: bbox 3.6 x 3.6 x 4 mm, 12 faces (baked)
FEATURE [Part::Feature] Cylinder014005512  label="Válec451"
  shape: bbox 5 x 5 x 7 mm, 3 faces (baked)
FEATURE [Part::Feature] Cylinder014005513  label="Válec452"
  Placement = pos=(0,0,0) rot=(0,0,1;4.18879rad)
  shape: bbox 5 x 5 x 7 mm, 3 faces (baked)
FEATURE [Part::MultiFuse] Fusion311
  Shapes = -> [Cylinder014005513,Cylinder014005478,Cylinder014005477]
FEATURE [Part::MultiFuse] Fusion285
  Placement = pos=(0,0,1) rot=(0,0,1;0rad)
  Shapes = -> [Fusion311,Cylinder014005507]
FEATURE [Part::Cut] Cut061138  label="Unasec Vrch zaklad022"
  Base = -> Cut061145
  Tool = -> Fusion285
FEATURE [Part::MultiFuse] Fusion307
  Shapes = -> [Cut061138,Cylinder014005496,Extrude040]
FEATURE [Part::Cut] Cut061147  label="unasec top006"
  Base = -> Fusion307
  Tool = -> Fusion276
FEATURE [App::Part] Part028  label="Part072"
  Group = -> [Cut061151,Cut061150,Cylinder014005495,Cylinder014005506,Cylinder014005505,Cylinder014005504,Cylinder014005472,Cylinder014005476,Cylinder014005479,Screw_solid116,Cylinder014005481,Screw_solid120,Cylinder014005474,Screw_solid121,Fusion284,Fusion312,Fusion277,Fusion305,Fusion289,Cut008_solid047,Cut008_solid046,Cut008_solid045,Screw_solid125,Cylinder014005461,Cylinder014005480,Screw_solid122,+49 more]
  License = CC BY 3.0
  LicenseURL = http://creativecommons.org/licenses/by/3.0/
  Origin = -> Origin032
  Placement = pos=(0,0,42) rot=(0,0,1;0rad)
FEATURE [App::Part] Part034  label="GearBOX 1024:1a001"
  Group = -> [Part031,Part030,Part029,Part033,Part028]
  License = CC BY 3.0
  LicenseURL = http://creativecommons.org/licenses/by/3.0/
  Origin = -> Origin030
FEATURE [App::Part] Part032  label="DriveA001"
  Group = -> [Part027,Part034]
  License = CC BY 3.0
  LicenseURL = http://creativecommons.org/licenses/by/3.0/
  Origin = -> Origin034
  Placement = pos=(0,-29,0) rot=(1,0,0;3.14159rad)
FEATURE [Part::Feature] Screw_solid128  label="M2x4-Screw (Solid)128"
  Placement = pos=(0,0,0) rot=(0,0,1;3.14159rad)
  shape: bbox 3.6 x 3.6 x 4 mm, 12 faces (baked)
FEATURE [Part::MultiFuse] Fusion324  label="srouby044"
  Placement = pos=(0,0,0.5) rot=(0,0,1;0rad)
  Shapes = -> [Screw_solid126,Screw_solid127,Screw_solid128]
FEATURE [Part::Feature] Cylinder014005514  label="Válec453"
  Placement = pos=(0,0,0) rot=(0,0,1;4.18879rad)
  shape: bbox 5 x 5 x 7 mm, 3 faces (baked)
FEATURE [Part::Feature] Cylinder014005515  label="Válec454"
  Placement = pos=(0,0,0) rot=(0,0,1;2.0944rad)
  shape: bbox 5 x 5 x 7 mm, 3 faces (baked)
FEATURE [Part::MultiFuse] Fusion317
  Shapes = -> [Cylinder014005514,Cylinder014005512,Cylinder014005515]
FEATURE [Part::Box] Box061  label="Krychle049"
  AttacherType = Attacher::AttachEngine3D
  Height = 112
  Length = 38
  Placement = pos=(-19,34,-52) rot=(0,0,1;0rad)
  Width = 6
FEATURE [Part::Box] Box062  label="Krychle050"
  AttacherType = Attacher::AttachEngine3D
  Height = 112
  Length = 38
  Placement = pos=(-19,32,-52) rot=(0,0,1;0rad)
  Width = 10
FEATURE [Part::Cut] Cut061161
  Base = -> Box062
  Tool = -> Box061
FEATURE [Part::MultiFuse] Fusion316  label="Arca plate base007"
  Placement = pos=(0,-6.5,115.5) rot=(-1,0,0;1.5708rad)
  Shapes = -> [Extrude039,Cut061161]
FEATURE [Part::Cylinder] Cylinder014005516  label="Válec455"
  Angle = 360
  AttacherType = Attacher::AttachEngine3D
  Height = 22
  Radius = 2.6
FEATURE [Part::MultiFuse] Fusion320
  Shapes = -> [Cylinder014005516,Extrude038]
FEATURE [Part::Cylinder] Cylinder014005517  label="Unasec vrch025"
  Angle = 360
  AttacherType = Attacher::AttachEngine3D
  Height = 1.5
  Placement = pos=(0,0,5.5) rot=(0,0,1;0rad)
  Radius = 15.5
FEATURE [Part::Cut] Cut061159  label="unasec vrch025"
  Base = -> Cylinder014005517
  Tool = -> Fusion324
FEATURE [Part::Cylinder] Cylinder014005518  label="Válec456"
  Angle = 360
  AttacherType = Attacher::AttachEngine3D
  Height = 8
  Placement = pos=(0,0,66) rot=(0,0,1;0rad)
  Radius = 4.5
FEATURE [Part::Cylinder] Cylinder014005519  label="Válec457"
  Angle = 360
  AttacherType = Attacher::AttachEngine3D
  Height = 6
  Placement = pos=(0,0,7) rot=(0,0,1;0rad)
  Radius = 6.5
FEATURE [Part::Cylinder] Cylinder014005520  label="Válec458"
  Angle = 360
  AttacherType = Attacher::AttachEngine3D
  Height = 10
  Placement = pos=(0,0,55) rot=(0,0,1;0rad)
  Radius = 12.5
FEATURE [Part::Cylinder] Cylinder014005521  label="Válec459"
  Angle = 360
  AttacherType = Attacher::AttachEngine3D
  Height = 55
  Placement = pos=(0,0,35) rot=(0,0,1;0rad)
  Radius = 2.7
FEATURE [Part::Box] Box063  label="Krychle051"
  AttacherType = Attacher::AttachEngine3D
  Height = 15
  Length = 50
  Placement = pos=(-25,-25,64) rot=(0,0,1;0rad)
  Width = 50
FEATURE [Part::Cut] Cut061154  label="Arca sw 003"
  Base = -> Box063
  Tool = -> Fusion316
FEATURE [Part::Cylinder] Cylinder014005522  label="Válec460"
  Angle = 360
  AttacherType = Attacher::AttachEngine3D
  Height = 7
  Radius = 2.6
FEATURE [Part::MultiFuse] Fusion323
  Placement = pos=(0,0,1) rot=(0,0,1;0rad)
  Shapes = -> [Fusion317,Cylinder014005522]
FEATURE [Part::Cut] Cut061153  label="Unasec Vrch zaklad025"
  Base = -> Cut061159
  Tool = -> Fusion323
FEATURE [Part::MultiFuse] Fusion318
  Shapes = -> [Cut061153,Cylinder014005519,Extrude043]
FEATURE [Part::Cut] Cut061158  label="unasec top007"
  Base = -> Fusion318
  Placement = pos=(0,0,42) rot=(0,0,1;0rad)
  Tool = -> Fusion320
FEATURE [Part::MultiFuse] Fusion322
  Shapes = -> [Cylinder014005521,Cut061158,Cylinder014005518]
FEATURE [Part::Box] Box064  label="Krychle052"
  AttacherType = Attacher::AttachEngine3D
  Height = 15
  Length = 2
  Placement = pos=(-15.5,-26,61) rot=(0,0,1;0rad)
  Width = 52
FEATURE [Part::Cut] Cut061160
  Base = -> Cut061154
  Tool = -> Box064
FEATURE [Part::MultiFuse] Fusion319
  Shapes = -> [Cylinder014005520,Cut061160]
FEATURE [Part::Cut] Cut061156
  Base = -> Fusion319
  Tool = -> Fusion322
FEATURE [Part::Cylinder] Cylinder014005523  label="Válec461"
  Angle = 360
  AttacherType = Attacher::AttachEngine3D
  Height = 60
  Placement = pos=(-30,-17,69) rot=(0,1,0;1.5708rad)
  Radius = 2.1
FEATURE [Part::Cylinder] Cylinder014005524  label="Válec462"
  Angle = 360
  AttacherType = Attacher::AttachEngine3D
  Height = 60
  Placement = pos=(-30,17,69) rot=(0,1,0;1.5708rad)
  Radius = 2.1
FEATURE [Part::MultiFuse] Fusion321
  Shapes = -> [Cylinder014005524,Cylinder014005523,Nut017,Nut018]
FEATURE [Part::Cut] Cut061157
  Base = -> Cut061156
  Tool = -> Fusion321
FEATURE [Part::RegularPolygon] RegularPolygon008  label="Pravidelný n-úhelník008"
  AttacherType = Attacher::AttachEngine3D
  Circumradius = 6
  Polygon = 6
FEATURE [Part::Extrusion] Extrude045
  Base = -> RegularPolygon008
  Dir = (0,0,1)
  DirMode = 2
  FaceMakerClass = Part::FaceMakerBullseye
  LengthFwd = 8
  LengthRev = 0
  Placement = pos=(0,0,13) rot=(0,0,1;0rad)
  Solid = true
  Symmetric = false
FEATURE [Part::Cylinder] Cylinder014005525  label="Válec463"
  Angle = 360
  AttacherType = Attacher::AttachEngine3D
  Height = 2.5
  Placement = pos=(0,-12,71) rot=(0,0,1;0rad)
  Radius = 6
FEATURE [Part::Box] Box065  label="Krychle053"
  AttacherType = Attacher::AttachEngine3D
  Height = 2.5
  Length = 12
  Placement = pos=(-6,-25,71) rot=(0,0,1;0rad)
  Width = 13
FEATURE [Part::MultiFuse] Fusion270
  Placement = pos=(0,4,1) rot=(0,0,1;3.14159rad)
  Shapes = -> [Box065,Cylinder014005525]
FEATURE [Part::Cylinder] Cylinder014005526  label="Válec464"
  Angle = 360
  AttacherType = Attacher::AttachEngine3D
  Height = 2.5
  Placement = pos=(0,-12,71) rot=(0,0,1;0rad)
  Radius = 6
FEATURE [Part::Box] Box066  label="Krychle054"
  AttacherType = Attacher::AttachEngine3D
  Height = 2.5
  Length = 12
  Placement = pos=(-6,-25,71) rot=(0,0,1;0rad)
  Width = 13
FEATURE [Part::MultiFuse] Fusion272
  Placement = pos=(0,-4,1) rot=(0,0,1;0rad)
  Shapes = -> [Box066,Cylinder014005526]
FEATURE [Part::MultiFuse] Fusion271
  Shapes = -> [Fusion272,Fusion270]
FEATURE [Part::Cut] Cut061164  label="Swis Arca003"
  Base = -> Cut061157
  Tool = -> Fusion271
FEATURE [Part::Feature] Cylinder014005527  label="Válec465"
  Placement = pos=(0,0,0) rot=(0,0,1;2.0944rad)
  shape: bbox 5 x 5 x 7 mm, 3 faces (baked)
FEATURE [Part::Feature] Screw_solid129  label="M2x4-Screw (Solid)129"
  Placement = pos=(0,0,0) rot=(0,0,1;3.14159rad)
  shape: bbox 3.6 x 3.6 x 4 mm, 12 faces (baked)
FEATURE [Part::Feature] Cylinder014005528  label="Válec466"
  shape: bbox 5 x 5 x 7 mm, 3 faces (baked)
FEATURE [Part::Feature] Cylinder014005529  label="Válec467"
  Placement = pos=(0,0,0) rot=(0,0,1;4.18879rad)
  shape: bbox 5 x 5 x 7 mm, 3 faces (baked)
FEATURE [Part::MultiFuse] Fusion274
  Shapes = -> [Cylinder014005529,Cylinder014005528,Cylinder014005527]
FEATURE [Part::Feature] Screw_solid130  label="M2x4-Screw (Solid)130"
  Placement = pos=(0,0,0) rot=(0,0,-1;1.0472rad)
  shape: bbox 3.6 x 3.6 x 4 mm, 12 faces (baked)
FEATURE [Part::Feature] Screw_solid131  label="M2x4-Screw (Solid)131"
  Placement = pos=(0,0,0) rot=(0,0,1;1.0472rad)
  shape: bbox 3.6 x 3.6 x 4 mm, 12 faces (baked)
FEATURE [Part::MultiFuse] Fusion259  label="srouby034"
  Placement = pos=(0,0,0.5) rot=(0,0,1;0rad)
  Shapes = -> [Screw_solid131,Screw_solid130,Screw_solid129]
FEATURE [Part::FeaturePython] Nut020  label="M8-Nut004"  # Fasteners workbench fastener (typed FeaturePython)
  Placement = pos=(0,0,-80) rot=(0,0,1;0rad)
  diameter = 9
  invert = false
  matchOuter = false
  offset = 0
  thread = false
  type = 3
FEATURE [Part::FeaturePython] InvoluteGear027  # WARN: FeaturePython — macro-defined, semantics opaque (R4)
  Placement = pos=(0,0,-71.9) rot=(0,0,1;0rad)
  backlash = 0
  beta = -20
  clearance = 0.25
  double_helix = true
  head = 0
  height = 8.2
  module = 1.16
  numpoints = 6
  pressure_angle = 20
  reversed_backlash = false
  shift = 0
  simple = false
  teeth = 20
  undercut = false
FEATURE [Part::Cylinder] Cylinder014005530  label="Válec468"
  Angle = 360
  AttacherType = Attacher::AttachEngine3D
  Height = 7
  Radius = 2.6
FEATURE [Part::MultiFuse] Fusion273
  Placement = pos=(0,0,1) rot=(0,0,1;0rad)
  Shapes = -> [Fusion274,Cylinder014005530]
FEATURE [Part::Cylinder] Cylinder014005531  label="Válec469"
  Angle = 360
  AttacherType = Attacher::AttachEngine3D
  Height = 11.5
  Placement = pos=(0,0,-76.1) rot=(0,0,1;0rad)
  Radius = 11
FEATURE [Part::Cylinder] Cylinder014005532  label="Válec470"
  Angle = 360
  AttacherType = Attacher::AttachEngine3D
  Height = 22
  Radius = 2.6
FEATURE [Part::Cylinder] Cylinder014005533  label="Válec471"
  Angle = 360
  AttacherType = Attacher::AttachEngine3D
  Height = 200
  Placement = pos=(0,0,-100) rot=(0,0,1;0rad)
  Radius = 3.9
FEATURE [Part::Cylinder] Cylinder014005534  label="Válec472"
  Angle = 360
  AttacherType = Attacher::AttachEngine3D
  Height = 6
  Placement = pos=(0,0,7) rot=(0,0,1;0rad)
  Radius = 6.5
FEATURE [Part::Cylinder] Cylinder014005535  label="Válec473"
  Angle = 360
  AttacherType = Attacher::AttachEngine3D
  Height = 55
  Placement = pos=(0,0,-82) rot=(0,0,1;0rad)
  Radius = 2.7
FEATURE [Part::Cylinder] Cylinder014005536  label="Unasec vrch026"
  Angle = 360
  AttacherType = Attacher::AttachEngine3D
  Height = 1.5
  Placement = pos=(0,0,5.5) rot=(0,0,1;0rad)
  Radius = 15.5
FEATURE [Part::Cut] Cut061163  label="unasec vrch026"
  Base = -> Cylinder014005536
  Tool = -> Fusion259
FEATURE [Part::Cut] Cut061166  label="Unasec Vrch zaklad026"
  Base = -> Cut061163
  Tool = -> Fusion273
FEATURE [Part::MultiFuse] Fusion264
  Shapes = -> [Cut061166,Cylinder014005534,Extrude045]
FEATURE [Part::Cylinder] Cylinder014005537  label="Válec474"
  Angle = 360
  AttacherType = Attacher::AttachEngine3D
  Height = 12.5
  Placement = pos=(0,0,-68) rot=(0,0,1;0rad)
  Radius = 12.5
FEATURE [Part::Cylinder] Cylinder014005538  label="Lozisko007"
  Angle = 360
  AttacherType = Attacher::AttachEngine3D
  Height = 4
  Placement = pos=(0,0,48) rot=(0,0,1;0rad)
  Radius = 7
FEATURE [Part::Cylinder] Cylinder014005539  label="Válec475"
  Angle = 360
  AttacherType = Attacher::AttachEngine3D
  Height = 9
  Placement = pos=(0,0,-77) rot=(0,0,1;0rad)
  Radius = 4.5
FEATURE [Part::Cylinder] Cylinder014005540  label="Válec476"
  Angle = 360
  AttacherType = Attacher::AttachEngine3D
  Height = 15
  Placement = pos=(0,0,-76.1) rot=(0,0,1;0rad)
  Radius = 5
FEATURE [Part::Cylinder] Cylinder014005541  label="Lozisko008"
  Angle = 360
  AttacherType = Attacher::AttachEngine3D
  Height = 4
  Placement = pos=(0,0,-60) rot=(0,0,1;0rad)
  Radius = 7
FEATURE [Sketcher::SketchObject] Sketch020
  MapMode = 45
  Placement = pos=(44.88,21.011,5.40003) rot=(0.707106,0.001666,0.707106;3.13826rad)
  sketch-geometry (7):
    g0: LineSegment StartX=5.21891 StartY=0.0364138 StartZ=0 EndX=2.62121 EndY=4.46293 EndZ=0
    g1: LineSegment StartX=2.62121 StartY=4.46293 StartZ=0 EndX=-2.51111 EndY=4.42651 EndZ=0
    g2: LineSegment StartX=-2.51111 StartY=4.42651 StartZ=0 EndX=-5.04574 EndY=-0.0364138 EndZ=0
    g3: LineSegment StartX=-5.04574 StartY=-0.0364138 StartZ=0 EndX=-2.44804 EndY=-4.46293 EndZ=0
    g4: LineSegment StartX=-2.44804 StartY=-4.46293 StartZ=0 EndX=2.68428 EndY=-4.42651 EndZ=0
    g5: LineSegment StartX=2.68428 StartY=-4.42651 StartZ=0 EndX=5.21891 EndY=0.0364138 EndZ=0
    g6: Circle [constr] CenterX=0.0865834 CenterY=0 CenterZ=0 NormalX=0 NormalY=0 NormalZ=1 AngleXU=0 Radius=5.13245
  constraints (14):
    c: Coincident(g0,g1)
    c: Coincident(g1,g2)
    c: Coincident(g2,g3)
    c: Coincident(g3,g4)
    c: Coincident(g4,g5)
    c: Coincident(g5,g0)
    c: Equal(g0, g1-g5) x5
    c: PointOnObject(g0,g6)
    c: PointOnObject(g1,g6)
    c: PointOnObject(g2,g6)
    c: PointOnObject(g3,g6)
    c: PointOnObject(g4,g6)
    c: PointOnObject(g5,g6)
    c: PointOnObject(g6,g-1)
FEATURE [Part::Extrusion] Extrude044
  Base = -> Sketch020
  Dir = (1,0,0)
  DirMode = 2
  FaceMakerClass = Part::FaceMakerBullseye
  LengthFwd = 5
  LengthRev = 0
  Placement = pos=(0,0,0.25) rot=(0,0,1;0rad)
  Solid = true
  Symmetric = false
FEATURE [Part::MultiFuse] Fusion258
  Shapes = -> [Cylinder014005532,Extrude044]
FEATURE [Part::Cut] Cut061165  label="unasec top008"
  Base = -> Fusion264
  Placement = pos=(0,0,-42) rot=(1,0,0;3.14159rad)
  Tool = -> Fusion258
FEATURE [Part::MultiFuse] Fusion325
  Shapes = -> [Cylinder014005539,Cut061165,Cylinder014005535]
FEATURE [Part::MultiFuse] Fusion326
  Shapes = -> [Cylinder014005540,Cylinder014005537,InvoluteGear027]
FEATURE [Part::Cut] Cut061162  label="Pinion001"
  Base = -> Fusion326
  Tool = -> Fusion325
FEATURE [App::Part] Part035  label="Pinion20 A001"
  Group = -> [Sketch020,Extrude044,RegularPolygon008,Extrude045,Cut061163,Cut061166,Cut061165,Cylinder014005530,Cylinder014005534,Cylinder014005539,Cylinder014005535,Cylinder014005536,Cylinder014005540,Cylinder014005537,Cylinder014005532,Screw_solid130,Screw_solid129,Cylinder014005529,Cylinder014005528,Screw_solid131,Cylinder014005527,Fusion264,Fusion258,Fusion325,Fusion274,Fusion273,Fusion259,InvoluteGear027,+2 more]
  License = CC BY 3.0
  LicenseURL = http://creativecommons.org/licenses/by/3.0/
  Origin = -> Origin035
  Placement = pos=(0,-29,0) rot=(0,0,1;0.017453rad)
FEATURE [Part::Cylinder] Cylinder014005542  label="diist podl002"
  Angle = 360
  AttacherType = Attacher::AttachEngine3D
  Height = 4
  Placement = pos=(0,0,-64) rot=(0,0,1;0rad)
  Radius = 4.2
FEATURE [Part::Cylinder] Cylinder014005543  label="Válec477"
  Angle = 360
  AttacherType = Attacher::AttachEngine3D
  Height = 15
  Placement = pos=(0,0,55) rot=(0,0,1;0rad)
  Radius = 11
FEATURE [Part::Cylinder] Cylinder014005544  label="Válec478"
  Angle = 360
  AttacherType = Attacher::AttachEngine3D
  Height = 15
  Placement = pos=(0,0,52) rot=(0,0,1;0rad)
  Radius = 5.5
FEATURE [Part::MultiFuse] Fusion329
  Shapes = -> [Cylinder014005543,Cylinder014005544,Cut061164]
FEATURE [Part::Cut] Cut061168  label="Swiss Acra V003"
  Base = -> Fusion329
  Tool = -> Screw010
FEATURE [App::Part] Part036  label="Swiss arca A001"
  Group = -> [Extrude038,Extrude039,Extrude043,RegularPolygon007,Nut017,Nut018,Sketch017,Sketch018,Screw010,Fusion270,Fusion271,Fusion272,Fusion316,Fusion317,Fusion318,Fusion319,Fusion320,Fusion321,Fusion322,Fusion323,Fusion324,Cut061153,Cut061154,Cut061156,Cut061157,Cut061158,Cut061159,Cut061160,Cut061161,Screw_solid126,Screw_solid127,Cylinder014005512,Screw_solid128,Cylinder014005514,Cylinder014005515,Box061,+22 more]
  License = CC BY 3.0
  LicenseURL = http://creativecommons.org/licenses/by/3.0/
  Origin = -> Origin036
FEATURE [Part::Cylinder] Cylinder014005545  label="diist podl003"
  Angle = 360
  AttacherType = Attacher::AttachEngine3D
  Height = 4
  Placement = pos=(0,0,-64) rot=(0,0,1;0rad)
  Radius = 5.5
FEATURE [Part::Cut] Cut061167  label="dist-11x8x005"
  Base = -> Cylinder014005545
  Tool = -> Cylinder014005542
FEATURE [Part::FeaturePython] InvoluteGear028  # WARN: FeaturePython — macro-defined, semantics opaque (R4)
  Placement = pos=(0,0,-72) rot=(0,0,1;0rad)
  backlash = 0
  beta = 20
  clearance = 0.25
  double_helix = true
  head = 0
  height = 8
  module = 1.16
  numpoints = 6
  pressure_angle = 20
  reversed_backlash = false
  shift = 0
  simple = false
  teeth = 27
  undercut = false
FEATURE [Part::MultiFuse] Fusion328
  Shapes = -> [Cylinder014005531,InvoluteGear028]
FEATURE [Sketcher::SketchObject] Sketch019
  MapMode = 5
  Placement = pos=(0,0,-64.6) rot=(0,0,1;0rad)
  Support = -> [Fusion328]
  sketch-geometry (7):
    g0: LineSegment StartX=-3.8831 StartY=6.55674 StartZ=0 EndX=-7.61986 EndY=-0.0844932 EndZ=0
    g1: LineSegment StartX=-7.61986 StartY=-0.0844932 StartZ=0 EndX=-3.73676 EndY=-6.64124 EndZ=0
    g2: LineSegment StartX=-3.73676 StartY=-6.64124 StartZ=0 EndX=3.8831 EndY=-6.55674 EndZ=0
    g3: LineSegment StartX=3.8831 StartY=-6.55674 StartZ=0 EndX=7.61986 EndY=0.0844932 EndZ=0
    g4: LineSegment StartX=7.61986 StartY=0.0844932 StartZ=0 EndX=3.73676 EndY=6.64124 EndZ=0
    g5: LineSegment StartX=3.73676 StartY=6.64124 StartZ=0 EndX=-3.8831 EndY=6.55674 EndZ=0
    g6: Circle [constr] CenterX=0 CenterY=0 CenterZ=0 NormalX=0 NormalY=0 NormalZ=1 AngleXU=0 Radius=7.62033
  constraints (14):
    c: Coincident(g0,g1)
    c: Coincident(g1,g2)
    c: Coincident(g2,g3)
    c: Coincident(g3,g4)
    c: Coincident(g4,g5)
    c: Coincident(g5,g0)
    c: Equal(g0, g1-g5) x5
    c: PointOnObject(g0,g6)
    c: PointOnObject(g1,g6)
    c: PointOnObject(g2,g6)
    c: PointOnObject(g3,g6)
    c: PointOnObject(g4,g6)
    c: PointOnObject(g5,g6)
    c: Coincident(g6,g-1)
FEATURE [Part::FeaturePython] Screw011  label="M8x160-Screw004"  # Fasteners workbench fastener (typed FeaturePython)
  Placement = pos=(0,0,68.4) rot=(0,0,1;0rad)
  diameter = 9
  invert = false
  length = 16
  matchOuter = false
  offset = 0
  thread = false
  type = 13
FEATURE [Part::Extrusion] Extrude046
  Base = -> Sketch019
  Dir = (0,0,1)
  DirMode = 2
  FaceMakerClass = Part::FaceMakerBullseye
  LengthFwd = 5
  LengthRev = 0
  Placement = pos=(0,0,-5) rot=(0,0,1;0rad)
  Solid = true
  Symmetric = false
FEATURE [Part::MultiFuse] Fusion327
  Shapes = -> [Extrude046,Cylinder014005533]
FEATURE [Part::Cut] Cut061169  label="Gear A001"
  Base = -> Fusion328
  Tool = -> Fusion327
FEATURE [App::Part] Part038  label="Gear27 A001"
  Group = -> [Sketch019,Cylinder014005531,Cylinder014005533,Fusion327,Fusion328,InvoluteGear028,Extrude046,Cut061169,Nut019,Nut020,Cylinder014005542,Cylinder014005545,Cut061167,Cylinder014005541]
  License = CC BY 3.0
  LicenseURL = http://creativecommons.org/licenses/by/3.0/
  Origin = -> Origin037
FEATURE [Part::Box] Box067  label="Krychle055"
  AttacherType = Attacher::AttachEngine3D
  Height = 4
  Length = 13
  Placement = pos=(30.5,-27,-59) rot=(0,0,1;1.5708rad)
  Width = 3
FEATURE [Part::Feature] Cut061170  label="Dov holder002"
  Placement = pos=(4.5,14.5,-47) rot=(0,0,1;1.5708rad)
  shape: bbox 15 x 36 x 40 mm, 20 faces (baked)
FEATURE [Part::MultiFuse] Fusion330
  Shapes = -> [Cut061170,Chamfer009]
FEATURE [Part::Cut] Cut061171  label="Axix RA"
  Base = -> Fusion330
  Tool = -> Box067
FEATURE [App::Part] Part039  label="Asix 1 RA"
  Group = -> [Sketch015,Cylinder014005384,Box056,Cylinder014005383,Box053,Box054,Box055,Fusion330,Cut061170,Chamfer009,Chamfer010,Fusion239,Fusion240,Fusion241,Fusion238,Fusion244,Fusion242,Fusion243,Fusion245,Box052,Cylinder014005382,Cylinder014005380,Cylinder014005379,Cylinder014005381,Cut061106,Cut061108,Cut061107,Extrude033,Cylinder014005389,Cylinder014005386,Cylinder014005385,Cylinder014005387,Box057,+9 more]
  License = CC BY 3.0
  LicenseURL = http://creativecommons.org/licenses/by/3.0/
  Origin = -> Origin039
FEATURE [Sketcher::SketchObject] Sketch021
  MapMode = 5
  Placement = pos=(0,40,0) rot=(0,0.707107,0.707107;3.14159rad)
  sketch-geometry (6):
    g0: LineSegment StartX=0 StartY=0 StartZ=0 EndX=0 EndY=3 EndZ=0
    g1: LineSegment StartX=0 StartY=3 StartZ=0 EndX=-4 EndY=10 EndZ=0
    g2: LineSegment StartX=-4 StartY=10 StartZ=0 EndX=-26 EndY=10 EndZ=0
    g3: LineSegment StartX=-26 StartY=10 StartZ=0 EndX=-30 EndY=3 EndZ=0
    g4: LineSegment StartX=-30 StartY=3 StartZ=0 EndX=-30 EndY=0 EndZ=0
    g5: LineSegment StartX=-30 StartY=0 StartZ=0 EndX=0 EndY=0 EndZ=0
  constraints (11):
    c: Coincident(g-1,g0)
    c: PointOnObject(g0,g-2)
    c: Coincident(g0,g1)
    c: Coincident(g1,g2)
    c: Horizontal(g2)
    c: Coincident(g2,g3)
    c: Coincident(g3,g4)
    c: PointOnObject(g4,g-1)
    c: Vertical(g4)
    c: Coincident(g4,g5)
    c: Coincident(g5,g0)
FEATURE [Sketcher::SketchObject] Sketch022
  MapMode = 5
  Placement = pos=(0,0,60) rot=(0,0,1;0rad)
  sketch-geometry (6):
    g0: LineSegment StartX=-18.9734 StartY=34.0308 StartZ=0 EndX=-16.0253 EndY=36.9748 EndZ=0
    g1: LineSegment StartX=18.996 StartY=34.0308 StartZ=0 EndX=16.044 EndY=36.9748 EndZ=0
    g2: LineSegment StartX=18.996 StartY=34.0308 StartZ=0 EndX=-18.9734 EndY=34.0308 EndZ=0
    g3: LineSegment StartX=-18.9734 StartY=40.0311 StartZ=0 EndX=-16.0253 EndY=36.9748 EndZ=0
    g4: LineSegment StartX=16.044 StartY=36.9748 StartZ=0 EndX=18.9109 EndY=40.0311 EndZ=0
    g5: LineSegment StartX=-18.9734 StartY=40.0311 StartZ=0 EndX=18.9109 EndY=40.0311 EndZ=0
  constraints (7):
    c: Coincident(g2,g1)
    c: Coincident(g2,g0)
    c: Horizontal(g2)
    c: Coincident(g3,g0)
    c: Coincident(g5,g3)
    c: Coincident(g5,g4)
    c: Horizontal(g5)
FEATURE [Part::FeaturePython] Screw012  label="M4x20-Screw004"  # Fasteners workbench fastener (typed FeaturePython)
  Placement = pos=(-40.5,-9,53) rot=(1,0,0;1.5708rad)
  diameter = 4
  invert = false
  length = 5
  matchOuter = false
  offset = 0
  thread = false
  type = 5
FEATURE [Part::FeaturePython] Nut021  label="M4-Nut010"  # Fasteners workbench fastener (typed FeaturePython)
  Placement = pos=(-40.2,7,53) rot=(1,0,0;1.5708rad)
  diameter = 6
  invert = false
  matchOuter = false
  offset = 0
  thread = false
  type = 1
FEATURE [Part::Box] Box068  label="Krychle056"
  AttacherType = Attacher::AttachEngine3D
  Height = 15
  Length = 90
  Placement = pos=(-45,-10,45) rot=(0,0,1;0rad)
  Width = 17
FEATURE [Part::Box] Box069  label="mezara002"
  AttacherType = Attacher::AttachEngine3D
  Height = 15
  Length = 90
  Placement = pos=(-45,-3,45) rot=(0,0,1;0rad)
  Width = 3
FEATURE [Part::Cylinder] Cylinder014005546  label="tubus003"
  Angle = 360
  AttacherType = Attacher::AttachEngine3D
  Height = 112
  Placement = pos=(0,-1,-52) rot=(0,0,1;0rad)
  Radius = 32
FEATURE [Part::Cylinder] Cylinder014005547  label="tubus004"
  Angle = 360
  AttacherType = Attacher::AttachEngine3D
  Height = 15
  Placement = pos=(0,-1,-52) rot=(0,0,1;0rad)
  Radius = 37
FEATURE [Part::Cylinder] Cylinder014005548  label="tubus005"
  Angle = 360
  AttacherType = Attacher::AttachEngine3D
  Height = 15
  Placement = pos=(0,-1,45) rot=(0,0,1;0rad)
  Radius = 37
FEATURE [Part::FeaturePython] Screw013  label="M4x20-Screw005"  # Fasteners workbench fastener (typed FeaturePython)
  Placement = pos=(-40.5,-9,53) rot=(1,0,0;1.5708rad)
  diameter = 4
  invert = false
  length = 5
  matchOuter = false
  offset = 0
  thread = false
  type = 5
FEATURE [Part::Box] Box070  label="Krychle057"
  AttacherType = Attacher::AttachEngine3D
  Height = 112
  Length = 38
  Placement = pos=(-19,32,-52) rot=(0,0,1;0rad)
  Width = 10
FEATURE [Part::Box] Box071  label="Krychle058"
  AttacherType = Attacher::AttachEngine3D
  Height = 112
  Length = 38
  Placement = pos=(-19,34,-52) rot=(0,0,1;0rad)
  Width = 6
FEATURE [Part::Cut] Cut061179
  Base = -> Box070
  Tool = -> Box071
FEATURE [Part::Box] Box072  label="mezara003"
  AttacherType = Attacher::AttachEngine3D
  Height = 15
  Length = 90
  Placement = pos=(-45,-3,-52) rot=(0,0,1;0rad)
  Width = 3
FEATURE [Part::Box] Box073  label="Krychle059"
  AttacherType = Attacher::AttachEngine3D
  Height = 15
  Length = 90
  Placement = pos=(-45,-10,-52) rot=(0,0,1;0rad)
  Width = 17
FEATURE [Part::MultiFuse] Fusion097
  Shapes = -> [Box069,Box072,Cylinder014005546]
FEATURE [Part::Extrusion] Extrude047
  Base = -> Sketch022
  Dir = (0,0,1)
  DirMode = 2
  FaceMakerClass = Part::FaceMakerBullseye
  LengthFwd = -112
  LengthRev = 0
  Solid = true
  Symmetric = false
FEATURE [Part::MultiFuse] Fusion335  label="Arca plate base008"
  Placement = pos=(0,-0.5,0) rot=(0,0,1;0rad)
  Shapes = -> [Extrude047,Cut061179]
FEATURE [Part::MultiFuse] Fusion337
  Shapes = -> [Fusion335,Cylinder014005547,Cylinder014005548,Box068,Box073]
FEATURE [Part::Cut] Cut061178
  Base = -> Fusion337
  Tool = -> Fusion097
FEATURE [Part::Extrusion] Extrude003
  Base = -> Sketch021
  Dir = (0,1,0)
  DirMode = 2
  FaceMakerClass = Part::FaceMakerBullseye
  LengthFwd = -40
  LengthRev = 0
  Placement = pos=(-15,0,0) rot=(0,0,1;0rad)
  Solid = true
  Symmetric = false
FEATURE [Part::FeaturePython] Nut022  label="M4-Nut011"  # Fasteners workbench fastener (typed FeaturePython)
  Placement = pos=(-40.2,7,53) rot=(1,0,0;1.5708rad)
  diameter = 6
  invert = false
  matchOuter = false
  offset = 0
  thread = false
  type = 1
FEATURE [Part::MultiFuse] Fusion336  label="Srouby005"
  Placement = pos=(0,0,-0.5) rot=(0,0,1;0rad)
  Shapes = -> [Screw013,Nut022]
FEATURE [Part::FeaturePython] Nut001  label="M4-Nut012"  # Fasteners workbench fastener (typed FeaturePython)
  Placement = pos=(-40.2,7,53) rot=(1,0,0;1.5708rad)
  diameter = 6
  invert = false
  matchOuter = false
  offset = 0
  thread = false
  type = 1
FEATURE [Part::MultiFuse] Fusion099  label="Srouby006"
  Placement = pos=(80.5,0,-0.5) rot=(0,0,1;0rad)
  Shapes = -> [Screw012,Nut001]
FEATURE [Part::FeaturePython] Screw014  label="M4x20-Screw006"  # Fasteners workbench fastener (typed FeaturePython)
  Placement = pos=(-40.5,-9,53) rot=(1,0,0;1.5708rad)
  diameter = 4
  invert = false
  length = 5
  matchOuter = false
  offset = 0
  thread = false
  type = 5
FEATURE [Part::MultiFuse] Fusion100  label="Srouby007"
  Placement = pos=(0,0,-97.5) rot=(0,0,1;0rad)
  Shapes = -> [Screw014,Nut021]
FEATURE [Part::FeaturePython] Screw015  label="M4x20-Screw007"  # Fasteners workbench fastener (typed FeaturePython)
  Placement = pos=(-40.5,-9,53) rot=(1,0,0;1.5708rad)
  diameter = 4
  invert = false
  length = 5
  matchOuter = false
  offset = 0
  thread = false
  type = 5
FEATURE [Part::FeaturePython] Nut023  label="M4-Nut013"  # Fasteners workbench fastener (typed FeaturePython)
  Placement = pos=(-40.2,7,53) rot=(1,0,0;1.5708rad)
  diameter = 6
  invert = false
  matchOuter = false
  offset = 0
  thread = false
  type = 1
FEATURE [Part::MultiFuse] Fusion331  label="Srouby004"
  Placement = pos=(80.5,0,-97.5) rot=(0,0,1;0rad)
  Shapes = -> [Screw015,Nut023]
FEATURE [Part::MultiFuse] Fusion332
  Shapes = -> [Fusion336,Fusion099,Fusion100,Fusion331]
FEATURE [Part::Cut] Cut061172  label="Swiss Arca holder"
  Base = -> Cut061178
  Placement = pos=(0,0,224) rot=(0,0,1;0rad)
  Tool = -> Fusion332
FEATURE [Part::FeaturePython] Screw016  label="M2.5x8-Screw001"  # Fasteners workbench fastener (typed FeaturePython)
  Placement = pos=(-34,0,20) rot=(0,-1,0;1.5708rad)
  diameter = 3
  invert = false
  length = 3
  matchOuter = false
  offset = 0
  thread = false
  type = 12
FEATURE [Part::FeaturePython] Screw017  label="M2.5x8-Screw002"  # Fasteners workbench fastener (typed FeaturePython)
  Placement = pos=(34,0,20) rot=(0,1,0;1.5708rad)
  diameter = 3
  invert = false
  length = 3
  matchOuter = false
  offset = 0
  thread = false
  type = 12
FEATURE [Part::MultiFuse] Fusion009
  Shapes = -> [Screw017,Screw016]
FEATURE [Part::Cylinder] Cylinder014005549  label="Válec479"
  Angle = 360
  AttacherType = Attacher::AttachEngine3D
  Height = 10
  Placement = pos=(-12,20,4) rot=(0,-1,0;0.785398rad)
  Radius = 1.4
FEATURE [Part::Cylinder] Cylinder014005550  label="Válec480"
  Angle = 360
  AttacherType = Attacher::AttachEngine3D
  Height = 10
  Placement = pos=(12,20,4) rot=(0,1,0;0.785398rad)
  Radius = 1.4
FEATURE [Part::MultiFuse] Fusion334
  Shapes = -> [Cylinder014005550,Cylinder014005549]
FEATURE [Part::Box] Box008  label="Krychle060"
  AttacherType = Attacher::AttachEngine3D
  Height = 15
  Length = 36
  Placement = pos=(-18,0,-5) rot=(0,0,1;0rad)
  Width = 40
FEATURE [Part::Cylinder] Cylinder014005551  label="Válec481"
  Angle = 360
  AttacherType = Attacher::AttachEngine3D
  Height = 500
  Radius = 28.5
FEATURE [Part::Cylinder] Cylinder014005552  label="Válec482"
  Angle = 360
  AttacherType = Attacher::AttachEngine3D
  Height = 500
  Radius = 32
FEATURE [Part::Cut] Cut061176  label="tubus !"
  Base = -> Cylinder014005552
  Tool = -> Cylinder014005551
FEATURE [Part::Box] Box074  label="Krychle061"
  AttacherType = Attacher::AttachEngine3D
  Height = 3
  Length = 13
  Placement = pos=(-6.5,0,-3) rot=(0,0,1;0rad)
  Width = 4
FEATURE [Part::MultiFuse] Fusion007  label="Dovecot profile002"
  Shapes = -> [Extrude003,Box074]
FEATURE [Part::Cut] Cut061175
  Base = -> Box008
  Tool = -> Fusion007
FEATURE [Part::Box] Box075  label="Krychle062"
  AttacherType = Attacher::AttachEngine3D
  Height = 30
  Length = 24
  Placement = pos=(-12,25,0) rot=(0,0,1;0rad)
  Width = 12
FEATURE [Part::Box] Box076  label="Krychle063"
  AttacherType = Attacher::AttachEngine3D
  Height = 30
  Length = 20
  Placement = pos=(-10,-32,0) rot=(0,0,1;0rad)
  Width = 5
FEATURE [Part::MultiFuse] Fusion121
  Shapes = -> [Box076,Box075]
FEATURE [Part::Cut] Cut061173  label="Tubus"
  Base = -> Cut061176
  Tool = -> Fusion121
FEATURE [Part::Cylinder] Cylinder014005553  label="Válec483"
  Angle = 360
  AttacherType = Attacher::AttachEngine3D
  Height = 40
  Placement = pos=(0,0,0) rot=(0,0,1;0.872665rad)
  Radius = 32
FEATURE [Part::Box] Box077  label="Krychle064"
  AttacherType = Attacher::AttachEngine3D
  Height = 40
  Length = 36
  Placement = pos=(-18,-36,0) rot=(0,0,1;0rad)
  Width = 10
FEATURE [Part::Cylinder] Cylinder014005554  label="Válec010"
  Angle = 360
  AttacherType = Attacher::AttachEngine3D
  Height = 40
  Placement = pos=(0,0,0) rot=(0,0,1;3.83972rad)
  Radius = 33.5
FEATURE [Part::Chamfer] Chamfer012
  Base = -> Cut061175
  Edges = 2 edges r=5: [Edge2,Edge29]
FEATURE [Part::Cut] Cut005  label="Dov holder003"
  Base = -> Chamfer012
  Placement = pos=(0,-39,0) rot=(1,0,0;1.5708rad)
  Tool = -> Fusion334
FEATURE [Part::MultiFuse] Fusion333
  Shapes = -> [Cylinder014005554,Cut005,Box077]
FEATURE [Part::Cut] Cut061174
  Base = -> Fusion333
  Tool = -> Cylinder014005553
FEATURE [Part::Cut] Cut007  label="Telscop dovetail holder"
  Base = -> Cut061174
  Placement = pos=(0,0,79) rot=(0,0,1;0rad)
  Tool = -> Fusion009
FEATURE [Part::Cylinder] Cylinder014005555  label="Válec484"
  Angle = 360
  AttacherType = Attacher::AttachEngine3D
  Height = 100
  Placement = pos=(-50,33,13) rot=(0,1,0;1.5708rad)
  Radius = 4
FEATURE [Part::Cylinder] Cylinder014005556  label="Válec485"
  Angle = 360
  AttacherType = Attacher::AttachEngine3D
  Height = 15
  Placement = pos=(-50,33,13) rot=(0,1,0;1.5708rad)
  Radius = 16
FEATURE [Part::Cylinder] Cylinder014005557  label="LensH001"
  Angle = 360
  AttacherType = Attacher::AttachEngine3D
  Height = 80
  Placement = pos=(0,0,500) rot=(0,0,1;0rad)
  Radius = 32
FEATURE [Part::Cylinder] Cylinder014005558  label="Lens"
  Angle = 360
  AttacherType = Attacher::AttachEngine3D
  Height = 10
  Placement = pos=(0,0,500) rot=(0,0,1;0rad)
  Radius = 32
FEATURE [Part::Box] Box078  label="Krychle065"
  AttacherType = Attacher::AttachEngine3D
  Height = 30
  Length = 20
  Placement = pos=(-10,-32,0) rot=(0,0,1;0rad)
  Width = 5
FEATURE [Part::Box] Box079  label="Krychle066"
  AttacherType = Attacher::AttachEngine3D
  Height = 30
  Length = 24
  Placement = pos=(-12,25,0) rot=(0,0,1;0rad)
  Width = 12
FEATURE [Part::Cylinder] Cylinder014005559  label="Válec486"
  Angle = 360
  AttacherType = Attacher::AttachEngine3D
  Height = 30
  Radius = 28
FEATURE [Part::MultiFuse] Fusion122
  Shapes = -> [Box079,Box078,Cylinder014005559]
FEATURE [Part::Cylinder] Cylinder014005560  label="Válec487"
  Angle = 360
  AttacherType = Attacher::AttachEngine3D
  Height = 120
  Placement = pos=(0,0,-80) rot=(0,0,1;0rad)
  Radius = 23
FEATURE [Part::Cylinder] Cylinder014005561  label="Válec488"
  Angle = 360
  AttacherType = Attacher::AttachEngine3D
  Height = 30
  Radius = 23
FEATURE [Part::Cut] Cut061177
  Base = -> Fusion122
  Tool = -> Cylinder014005561
FEATURE [Part::Cylinder] Cylinder014005562  label="LensH"
  Angle = 360
  AttacherType = Attacher::AttachEngine3D
  Height = 80
  Placement = pos=(0,0,500) rot=(0,0,1;0rad)
  Radius = 37
FEATURE [Part::Cut] Cut061024
  Base = -> Cylinder014005562
  Placement = pos=(0,0,-30) rot=(0,0,1;0rad)
  Tool = -> Cylinder014005557
FEATURE [Part::Cylinder] Cylinder014005563  label="Válec489"
  Angle = 360
  AttacherType = Attacher::AttachEngine3D
  Height = 15
  Placement = pos=(35,33,13) rot=(0,1,0;1.5708rad)
  Radius = 16
FEATURE [Part::Cylinder] Cylinder014005564  label="Válec490"
  Angle = 360
  AttacherType = Attacher::AttachEngine3D
  Height = 120
  Placement = pos=(0,0,-80) rot=(0,0,1;0rad)
  Radius = 20.5
FEATURE [Part::Cut] Cut061023
  Base = -> Cylinder014005560
  Tool = -> Cylinder014005564
FEATURE [Part::MultiFuse] Fusion123  label="Focuser"
  Shapes = -> [Cut061023,Cut061177,Cylinder014005555,Cylinder014005556,Cylinder014005563]
FEATURE [Part::Cylinder] Cylinder014005565  label="Lens001"
  Angle = 360
  AttacherType = Attacher::AttachEngine3D
  Height = 2
  Placement = pos=(0,0,510) rot=(0,0,1;0rad)
  Radius = 32
FEATURE [Part::Cylinder] Cylinder014005566  label="Lens002"
  Angle = 360
  AttacherType = Attacher::AttachEngine3D
  Height = 2
  Placement = pos=(0,0,510) rot=(0,0,1;0rad)
  Radius = 30
FEATURE [Part::Cut] Cut061025
  Base = -> Cylinder014005565
  Tool = -> Cylinder014005566
FEATURE [Part::MultiFuse] Fusion124
  Shapes = -> [Cut061025,Cut061024]
FEATURE [App::Part] Part040  label="DIY telescope"
  Group = -> [Cut061176,Cylinder014005551,Cylinder014005552,Box076,Box075,Fusion121,Cut061173,Cylinder014005556,Cylinder014005561,Cylinder014005564,Cylinder014005563,Cylinder014005559,Cylinder014005555,Cylinder014005560,Box079,Cut061023,Cut061177,Box078,Fusion122,Fusion123,Cylinder014005558,Cylinder014005562,Cylinder014005565,Cylinder014005557,Cut061024,Cut061025,Cylinder014005566,Fusion124,Fusion097,Fusion099,+48 more]
  License = CC BY 3.0
  LicenseURL = http://creativecommons.org/licenses/by/3.0/
  Origin = -> Origin040
  Placement = pos=(0,115,-142) rot=(0,0,1;3.14159rad)
FEATURE [Part::FeaturePython] Nut024  label="M6-Nut"  # Fasteners workbench fastener (typed FeaturePython)
  Placement = pos=(0,-97,85) rot=(1,0,0;1.5708rad)
  diameter = 8
  invert = false
  matchOuter = false
  offset = 0
  thread = false
  type = 3
FEATURE [Part::FeaturePython] Nut025  label="M6-Nut007"  # Fasteners workbench fastener (typed FeaturePython)
  Placement = pos=(0,-115,85) rot=(1,0,0;1.5708rad)
  diameter = 8
  invert = false
  matchOuter = false
  offset = 0
  thread = false
  type = 3
FEATURE [Part::Cylinder] Cylinder014005567  label="Válec491"
  Angle = 360
  AttacherType = Attacher::AttachEngine3D
  Height = 38
  Placement = pos=(0,-77,85) rot=(1,0,0;1.5708rad)
  Radius = 11
FEATURE [Sketcher::SketchObject] Sketch023
  MapMode = 5
  Placement = pos=(0,-92,85) rot=(1,0,0;1.5708rad)
  Support = -> [Nut015]
  sketch-geometry (7):
    g0: LineSegment StartX=-4 StartY=6.58103 StartZ=0 EndX=-7.69934 EndY=-0.173586 EndZ=0
    g1: LineSegment StartX=-7.69934 StartY=-0.173586 StartZ=0 EndX=-3.69934 EndY=-6.75462 EndZ=0
    g2: LineSegment StartX=-3.69934 StartY=-6.75462 StartZ=0 EndX=4 EndY=-6.58103 EndZ=0
    g3: LineSegment StartX=4 StartY=-6.58103 StartZ=0 EndX=7.69934 EndY=0.173586 EndZ=0
    g4: LineSegment StartX=7.69934 StartY=0.173586 StartZ=0 EndX=3.69934 EndY=6.75462 EndZ=0
    g5: LineSegment StartX=3.69934 StartY=6.75462 StartZ=0 EndX=-4 EndY=6.58103 EndZ=0
    g6: Circle [constr] CenterX=0 CenterY=0 CenterZ=0 NormalX=0 NormalY=0 NormalZ=1 AngleXU=0 Radius=7.7013
  constraints (14):
    c: Coincident(g0,g1)
    c: Coincident(g1,g2)
    c: Coincident(g2,g3)
    c: Coincident(g3,g4)
    c: Coincident(g4,g5)
    c: Coincident(g5,g0)
    c: Equal(g0, g1-g5) x5
    c: PointOnObject(g0,g6)
    c: PointOnObject(g1,g6)
    c: PointOnObject(g2,g6)
    c: PointOnObject(g3,g6)
    c: PointOnObject(g4,g6)
    c: PointOnObject(g5,g6)
    c: Coincident(g6,g-1)
FEATURE [Part::Extrusion] Extrude048
  Base = -> Sketch023
  Dir = (0,-1,0)
  DirMode = 2
  FaceMakerClass = Part::FaceMakerBullseye
  LengthFwd = 18
  LengthRev = 0
  Placement = pos=(0,15,0) rot=(0,0,1;0rad)
  Solid = true
  Symmetric = false
FEATURE [Sketcher::SketchObject] Sketch024
  MapMode = 2
  Placement = pos=(0,-76,85) rot=(1,0,0;1.5708rad)
  sketch-geometry (7):
    g0: LineSegment StartX=-3.75 StartY=6.42629 StartZ=0 EndX=-7.50855 EndY=-0.0738358 EndZ=0
    g1: LineSegment StartX=-7.50855 StartY=-0.0738358 StartZ=0 EndX=-3.75855 EndY=-6.5789 EndZ=0
    g2: LineSegment StartX=-3.75855 StartY=-6.5789 StartZ=0 EndX=3.75 EndY=-6.58384 EndZ=0
    g3: LineSegment StartX=3.75 StartY=-6.58384 StartZ=0 EndX=7.50855 EndY=-0.0837102 EndZ=0
    g4: LineSegment StartX=7.50855 StartY=-0.0837102 StartZ=0 EndX=3.75855 EndY=6.42135 EndZ=0
    g5: LineSegment StartX=3.75855 StartY=6.42135 StartZ=0 EndX=-3.75 EndY=6.42629 EndZ=0
    g6: Circle [constr] CenterX=0 CenterY=-0.078773 CenterZ=0 NormalX=0 NormalY=0 NormalZ=1 AngleXU=0 Radius=7.50855
  constraints (13):
    c: Coincident(g0,g1)
    c: Coincident(g1,g2)
    c: Coincident(g2,g3)
    c: Coincident(g3,g4)
    c: Coincident(g4,g5)
    c: Coincident(g5,g0)
    c: Equal(g0, g1-g5) x5
    c: PointOnObject(g0,g6)
    c: PointOnObject(g1,g6)
    c: PointOnObject(g2,g6)
    c: PointOnObject(g3,g6)
    c: PointOnObject(g4,g6)
    c: PointOnObject(g5,g6)
FEATURE [Part::Extrusion] Extrude049  label="vnitrek"
  Base = -> Sketch024
  Dir = (0,-1,0)
  DirMode = 2
  FaceMakerClass = Part::FaceMakerBullseye
  LengthFwd = 8
  LengthRev = 0
  Placement = pos=(0,-4,0) rot=(0,0,1;0rad)
  Solid = true
  Symmetric = false
FEATURE [Part::Cylinder] Cylinder014005568  label="Válec492"
  Angle = 360
  AttacherType = Attacher::AttachEngine3D
  Height = 35
  Placement = pos=(0,-77,85) rot=(1,0,0;1.5708rad)
  Radius = 4.2
FEATURE [Part::Cut] Cut061180  label="Nut M8-Fix"
  Base = -> Extrude049
  Tool = -> Cylinder014005568
FEATURE [Sketcher::SketchObject] Sketch025
  MapMode = 5
  Placement = pos=(0,-97,85) rot=(-1,0,0;1.5708rad)
  Support = -> [Nut024]
  sketch-geometry (7):
    g0: LineSegment StartX=-2.87741 StartY=5.0504 StartZ=0 EndX=-5.81248 EndY=0.0332934 EndZ=0
    g1: LineSegment StartX=-5.81248 StartY=0.0332934 StartZ=0 EndX=-2.93507 EndY=-5.01711 EndZ=0
    g2: LineSegment StartX=-2.93507 StartY=-5.01711 StartZ=0 EndX=2.87741 EndY=-5.0504 EndZ=0
    g3: LineSegment StartX=2.87741 StartY=-5.0504 StartZ=0 EndX=5.81248 EndY=-0.0332934 EndZ=0
    g4: LineSegment StartX=5.81248 StartY=-0.0332934 StartZ=0 EndX=2.93507 EndY=5.01711 EndZ=0
    g5: LineSegment StartX=2.93507 StartY=5.01711 StartZ=0 EndX=-2.87741 EndY=5.0504 EndZ=0
    g6: Circle [constr] CenterX=0 CenterY=0 CenterZ=0 NormalX=0 NormalY=0 NormalZ=1 AngleXU=0 Radius=5.81257
  constraints (14):
    c: Coincident(g0,g1)
    c: Coincident(g1,g2)
    c: Coincident(g2,g3)
    c: Coincident(g3,g4)
    c: Coincident(g4,g5)
    c: Coincident(g5,g0)
    c: Equal(g0, g1-g5) x5
    c: PointOnObject(g0,g6)
    c: PointOnObject(g1,g6)
    c: PointOnObject(g2,g6)
    c: PointOnObject(g3,g6)
    c: PointOnObject(g4,g6)
    c: PointOnObject(g5,g6)
    c: Coincident(g6,g-1)
FEATURE [Part::Extrusion] Extrude050
  Base = -> Sketch025
  Dir = (0,1,0)
  DirMode = 2
  FaceMakerClass = Part::FaceMakerBullseye
  LengthFwd = 10
  LengthRev = 0
  Placement = pos=(0,-4,0) rot=(0,0,1;0rad)
  Solid = true
  Symmetric = false
FEATURE [Part::Cylinder] Cylinder014005569  label="tyč závaží003"
  Angle = 360
  AttacherType = Attacher::AttachEngine3D
  Height = 200
  Placement = pos=(0,-91,85) rot=(1,0,0;1.5708rad)
  Radius = 3
FEATURE [Part::MultiFuse] Fusion338
  Shapes = -> [Cylinder014005569,Extrude050,Extrude048]
FEATURE [Part::Cut] Cut061181  label="Clutch"
  Base = -> Cylinder014005567
  Tool = -> Fusion338
FEATURE [Part::Box] Box080  label="Krychle067"
  AttacherType = Attacher::AttachEngine3D
  Height = 20
  Length = 50
  Placement = pos=(-25,0,-17) rot=(0,0,1;0rad)
  Width = 82
FEATURE [Part::Cylinder] Cylinder014005343  label="Válec493"
  Angle = 360
  AttacherType = Attacher::AttachEngine3D
  Height = 33
  Placement = pos=(0,34.5,-9) rot=(1,0,0;0.523599rad)
  Radius = 14
FEATURE [Part::Box] Box081  label="Krychle068"
  AttacherType = Attacher::AttachEngine3D
  Height = 112
  Length = 38
  Placement = pos=(-19,32,-52) rot=(0,0,1;0rad)
  Width = 10
FEATURE [Part::Cylinder] Cylinder014005570  label="Válec494"
  Angle = 360
  AttacherType = Attacher::AttachEngine3D
  Height = 22
  Radius = 2.6
FEATURE [Part::Box] Box082  label="Krychle069"
  AttacherType = Attacher::AttachEngine3D
  Height = 15
  Length = 50
  Placement = pos=(-25,-25,64) rot=(0,0,1;0rad)
  Width = 50
FEATURE [Part::Cylinder] Cylinder014005571  label="Válec495"
  Angle = 360
  AttacherType = Attacher::AttachEngine3D
  Height = 6
  Placement = pos=(0,0,7) rot=(0,0,1;0rad)
  Radius = 6.5
FEATURE [Part::Cylinder] Cylinder014005572  label="Válec496"
  Angle = 360
  AttacherType = Attacher::AttachEngine3D
  Height = 8
  Placement = pos=(0,0,66) rot=(0,0,1;0rad)
  Radius = 4.5
FEATURE [Part::Box] Box083  label="Krychle070"
  AttacherType = Attacher::AttachEngine3D
  Height = 112
  Length = 38
  Placement = pos=(-19,34,-52) rot=(0,0,1;0rad)
  Width = 6
FEATURE [Part::Cylinder] Cylinder014005573  label="Válec497"
  Angle = 360
  AttacherType = Attacher::AttachEngine3D
  Height = 7
  Radius = 2.6
FEATURE [Part::Box] Box084  label="Krychle071"
  AttacherType = Attacher::AttachEngine3D
  Height = 10
  Length = 50
  Placement = pos=(-25,0,3) rot=(0,0,1;0rad)
  Width = 82
FEATURE [Part::Cylinder] Cylinder014005574  label="Válec498"
  Angle = 360
  AttacherType = Attacher::AttachEngine3D
  Height = 100
  Placement = pos=(0,34.5,-9) rot=(1,0,0;0.523599rad)
  Radius = 2.6
FEATURE [Part::Cylinder] Cylinder014005341  label="Válec316"
  Angle = 360
  AttacherType = Attacher::AttachEngine3D
  Height = 18
  Placement = pos=(0,70,0) rot=(0,0,1;0rad)
  Radius = 3
FEATURE [Part::Cylinder] Cylinder014005575  label="Válec499"
  Angle = 360
  AttacherType = Attacher::AttachEngine3D
  Height = 18
  Placement = pos=(0,45,3) rot=(0,0,1;0rad)
  Radius = 4.35
FEATURE [Part::Cylinder] Cylinder014005342  label="Válec500"
  Angle = 360
  AttacherType = Attacher::AttachEngine3D
  Height = 18
  Placement = pos=(0,45,6) rot=(0,0,1;0rad)
  Radius = 4.9
FEATURE [Sketcher::SketchObject] Sketch026
  MapMode = 5
  Placement = pos=(0,29.25,0) rot=(1,0,0;3.66519rad)
  sketch-geometry (7):
    g0: LineSegment StartX=-2.35665 StartY=4 StartZ=0 EndX=-4.64243 EndY=-0.0409205 EndZ=0
    g1: LineSegment StartX=-4.64243 StartY=-0.0409205 StartZ=0 EndX=-2.28578 EndY=-4.04092 EndZ=0
    g2: LineSegment StartX=-2.28578 StartY=-4.04092 StartZ=0 EndX=2.35665 EndY=-4 EndZ=0
    g3: LineSegment StartX=2.35665 StartY=-4 StartZ=0 EndX=4.64243 EndY=0.0409205 EndZ=0
    g4: LineSegment StartX=4.64243 StartY=0.0409205 StartZ=0 EndX=2.28578 EndY=4.04092 EndZ=0
    g5: LineSegment StartX=2.28578 StartY=4.04092 StartZ=0 EndX=-2.35665 EndY=4 EndZ=0
    g6: Circle [constr] CenterX=0 CenterY=0 CenterZ=0 NormalX=0 NormalY=0 NormalZ=1 AngleXU=0 Radius=4.64261
  constraints (14):
    c: Coincident(g0,g1)
    c: Coincident(g1,g2)
    c: Coincident(g2,g3)
    c: Coincident(g3,g4)
    c: Coincident(g4,g5)
    c: Coincident(g5,g0)
    c: Equal(g0, g1-g5) x5
    c: PointOnObject(g0,g6)
    c: PointOnObject(g1,g6)
    c: PointOnObject(g2,g6)
    c: PointOnObject(g3,g6)
    c: PointOnObject(g4,g6)
    c: PointOnObject(g5,g6)
    c: Coincident(g6,g-1)
FEATURE [Part::Feature] Screw_solid132  label="M2x4-Screw (Solid)132"
  Placement = pos=(0,0,0) rot=(0,0,-1;1.0472rad)
  shape: bbox 3.6 x 3.6 x 4 mm, 12 faces (baked)
FEATURE [Part::Feature] Cylinder014005576  label="Válec501"
  shape: bbox 5 x 5 x 7 mm, 3 faces (baked)
FEATURE [Part::Feature] Screw_solid133  label="M2x4-Screw (Solid)133"
  Placement = pos=(0,0,0) rot=(0,0,1;3.14159rad)
  shape: bbox 3.6 x 3.6 x 4 mm, 12 faces (baked)
FEATURE [Part::Feature] Cylinder014005577  label="Válec502"
  Placement = pos=(0,0,0) rot=(0,0,1;2.0944rad)
  shape: bbox 5 x 5 x 7 mm, 3 faces (baked)
FEATURE [Part::Feature] Cylinder014005578  label="Válec503"
  Placement = pos=(0,0,0) rot=(0,0,1;4.18879rad)
  shape: bbox 5 x 5 x 7 mm, 3 faces (baked)
FEATURE [Part::Feature] Screw_solid134  label="M2x4-Screw (Solid)134"
  Placement = pos=(0,0,0) rot=(0,0,1;1.0472rad)
  shape: bbox 3.6 x 3.6 x 4 mm, 12 faces (baked)
FEATURE [Part::Box] Box085  label="Krychle072"
  AttacherType = Attacher::AttachEngine3D
  Height = 15
  Length = 2
  Placement = pos=(-15.5,-26,61) rot=(0,0,1;0rad)
  Width = 52
FEATURE [Part::Cylinder] Cylinder014005579  label="Válec504"
  Angle = 360
  AttacherType = Attacher::AttachEngine3D
  Height = 55
  Placement = pos=(0,0,35) rot=(0,0,1;0rad)
  Radius = 2.7
FEATURE [Part::Cylinder] Cylinder014005580  label="Válec505"
  Angle = 360
  AttacherType = Attacher::AttachEngine3D
  Height = 2.5
  Placement = pos=(0,-12,71) rot=(0,0,1;0rad)
  Radius = 6
FEATURE [Part::Box] Box086  label="Krychle073"
  AttacherType = Attacher::AttachEngine3D
  Height = 2.5
  Length = 12
  Placement = pos=(-6,-25,71) rot=(0,0,1;0rad)
  Width = 13
FEATURE [Part::Cylinder] Cylinder014005581  label="Válec506"
  Angle = 360
  AttacherType = Attacher::AttachEngine3D
  Height = 9
  Placement = pos=(0,0,55) rot=(0,0,1;0rad)
  Radius = 12.5
FEATURE [Part::Cylinder] Cylinder014005582  label="Válec507"
  Angle = 360
  AttacherType = Attacher::AttachEngine3D
  Height = 60
  Placement = pos=(-30,-17,69) rot=(0,1,0;1.5708rad)
  Radius = 2.1
FEATURE [Part::Box] Box087  label="Krychle074"
  AttacherType = Attacher::AttachEngine3D
  Height = 2.5
  Length = 12
  Placement = pos=(-6,-25,71) rot=(0,0,1;0rad)
  Width = 13
FEATURE [Part::Cylinder] Cylinder014005583  label="Unasec vrch027"
  Angle = 360
  AttacherType = Attacher::AttachEngine3D
  Height = 1.5
  Placement = pos=(0,0,5.5) rot=(0,0,1;0rad)
  Radius = 15.5
FEATURE [Part::Cylinder] Cylinder014005584  label="Válec508"
  Angle = 360
  AttacherType = Attacher::AttachEngine3D
  Height = 60
  Placement = pos=(-30,17,69) rot=(0,1,0;1.5708rad)
  Radius = 2.1
FEATURE [Part::Cylinder] Cylinder014005585  label="Válec509"
  Angle = 360
  AttacherType = Attacher::AttachEngine3D
  Height = 2.5
  Placement = pos=(0,-12,71) rot=(0,0,1;0rad)
  Radius = 6
FEATURE [Part::Extrusion] Extrude052
  Base = -> Sketch026
  Dir = (0,0.5,-0.866025)
  DirMode = 2
  FaceMakerClass = Part::FaceMakerBullseye
  LengthFwd = -10
  LengthRev = 0
  Solid = true
  Symmetric = false
FEATURE [Part::MultiFuse] Fusion339
  Shapes = -> [Extrude052,Cylinder014005574]
FEATURE [Part::RegularPolygon] RegularPolygon009  label="Pravidelný n-úhelník009"
  AttacherType = Attacher::AttachEngine3D
  Circumradius = 6
  Polygon = 6
FEATURE [Part::Extrusion] Extrude055
  Base = -> RegularPolygon009
  Dir = (0,0,1)
  DirMode = 2
  FaceMakerClass = Part::FaceMakerBullseye
  LengthFwd = 8
  LengthRev = 0
  Placement = pos=(0,0,13) rot=(0,0,1;0rad)
  Solid = true
  Symmetric = false
FEATURE [Part::FeaturePython] Nut026  label="M4-Nut014"  # Fasteners workbench fastener (typed FeaturePython)
  Placement = pos=(22,-17,69) rot=(0,1,0;1.5708rad)
  diameter = 6
  invert = false
  matchOuter = false
  offset = 0
  thread = false
  type = 1
FEATURE [Part::MultiFuse] Fusion340
  Placement = pos=(0,0,1) rot=(0,0,1;0rad)
  Shapes = -> [Box086,Cylinder014005580]
FEATURE [Part::MultiFuse] Fusion341
  Shapes = -> [Cylinder014005578,Cylinder014005576,Cylinder014005577]
FEATURE [Part::MultiFuse] Fusion343
  Placement = pos=(0,0,1) rot=(0,0,1;0rad)
  Shapes = -> [Fusion341,Cylinder014005573]
FEATURE [Part::MultiFuse] Fusion347
  Placement = pos=(0,0,1) rot=(0,0,1;3.14159rad)
  Shapes = -> [Box087,Cylinder014005585]
FEATURE [Part::MultiFuse] Fusion349
  Shapes = -> [Fusion340,Fusion347]
FEATURE [Part::MultiFuse] Fusion350  label="srouby045"
  Placement = pos=(0,0,0.5) rot=(0,0,1;0rad)
  Shapes = -> [Screw_solid134,Screw_solid132,Screw_solid133]
FEATURE [Part::Cut] Cut061182
  Base = -> Box081
  Tool = -> Box083
FEATURE [Part::Cut] Cut061185  label="unasec vrch027"
  Base = -> Cylinder014005583
  Tool = -> Fusion350
FEATURE [Part::Cut] Cut061187  label="Unasec Vrch zaklad027"
  Base = -> Cut061185
  Tool = -> Fusion343
FEATURE [Part::MultiFuse] Fusion348
  Shapes = -> [Cut061187,Cylinder014005571,Extrude055]
FEATURE [Sketcher::SketchObject] Sketch028
  MapMode = 45
  Placement = pos=(44.88,21.011,5.40003) rot=(0.707106,0.001666,0.707106;3.13826rad)
  sketch-geometry (7):
    g0: LineSegment StartX=5.21891 StartY=0.0364138 StartZ=0 EndX=2.62121 EndY=4.46293 EndZ=0
    g1: LineSegment StartX=2.62121 StartY=4.46293 StartZ=0 EndX=-2.51111 EndY=4.42651 EndZ=0
    g2: LineSegment StartX=-2.51111 StartY=4.42651 StartZ=0 EndX=-5.04574 EndY=-0.0364138 EndZ=0
    g3: LineSegment StartX=-5.04574 StartY=-0.0364138 StartZ=0 EndX=-2.44804 EndY=-4.46293 EndZ=0
    g4: LineSegment StartX=-2.44804 StartY=-4.46293 StartZ=0 EndX=2.68428 EndY=-4.42651 EndZ=0
    g5: LineSegment StartX=2.68428 StartY=-4.42651 StartZ=0 EndX=5.21891 EndY=0.0364138 EndZ=0
    g6: Circle [constr] CenterX=0.0865834 CenterY=0 CenterZ=0 NormalX=0 NormalY=0 NormalZ=1 AngleXU=0 Radius=5.13245
  constraints (14):
    c: Coincident(g0,g1)
    c: Coincident(g1,g2)
    c: Coincident(g2,g3)
    c: Coincident(g3,g4)
    c: Coincident(g4,g5)
    c: Coincident(g5,g0)
    c: Equal(g0, g1-g5) x5
    c: PointOnObject(g0,g6)
    c: PointOnObject(g1,g6)
    c: PointOnObject(g2,g6)
    c: PointOnObject(g3,g6)
    c: PointOnObject(g4,g6)
    c: PointOnObject(g5,g6)
    c: PointOnObject(g6,g-1)
FEATURE [Part::Extrusion] Extrude054
  Base = -> Sketch028
  Dir = (1,0,0)
  DirMode = 2
  FaceMakerClass = Part::FaceMakerBullseye
  LengthFwd = 5
  LengthRev = 0
  Placement = pos=(0,0,0.25) rot=(0,0,1;0rad)
  Solid = true
  Symmetric = false
FEATURE [Part::MultiFuse] Fusion351
  Shapes = -> [Cylinder014005570,Extrude054]
FEATURE [Part::Cut] Cut061189  label="unasec top009"
  Base = -> Fusion348
  Placement = pos=(0,0,42) rot=(0,0,1;0rad)
  Tool = -> Fusion351
FEATURE [Part::MultiFuse] Fusion346
  Shapes = -> [Cylinder014005579,Cut061189,Cylinder014005572]
FEATURE [Sketcher::SketchObject] Sketch029
  MapMode = 5
  Placement = pos=(0,0,60) rot=(0,0,1;0rad)
  sketch-geometry (6):
    g0: LineSegment StartX=-18.9734 StartY=34.0308 StartZ=0 EndX=-16.0253 EndY=36.9748 EndZ=0
    g1: LineSegment StartX=18.996 StartY=34.0308 StartZ=0 EndX=16.044 EndY=36.9748 EndZ=0
    g2: LineSegment StartX=18.996 StartY=34.0308 StartZ=0 EndX=-18.9734 EndY=34.0308 EndZ=0
    g3: LineSegment StartX=-18.9734 StartY=40.0311 StartZ=0 EndX=-16.0253 EndY=36.9748 EndZ=0
    g4: LineSegment StartX=16.044 StartY=36.9748 StartZ=0 EndX=18.9109 EndY=40.0311 EndZ=0
    g5: LineSegment StartX=-18.9734 StartY=40.0311 StartZ=0 EndX=18.9109 EndY=40.0311 EndZ=0
  constraints (7):
    c: Coincident(g2,g1)
    c: Coincident(g2,g0)
    c: Horizontal(g2)
    c: Coincident(g3,g0)
    c: Coincident(g5,g3)
    c: Coincident(g5,g4)
    c: Horizontal(g5)
FEATURE [Part::Extrusion] Extrude053
  Base = -> Sketch029
  Dir = (0,0,1)
  DirMode = 2
  FaceMakerClass = Part::FaceMakerBullseye
  LengthFwd = -112
  LengthRev = 0
  Solid = true
  Symmetric = false
FEATURE [Part::MultiFuse] Fusion344  label="Arca plate base009"
  Placement = pos=(0,-6.5,115.5) rot=(-1,0,0;1.5708rad)
  Shapes = -> [Extrude053,Cut061182]
FEATURE [Part::Cut] Cut061186  label="Arca sw 004"
  Base = -> Box082
  Tool = -> Fusion344
FEATURE [Part::Cut] Cut061191
  Base = -> Cut061186
  Tool = -> Box085
FEATURE [Part::MultiFuse] Fusion342
  Shapes = -> [Cylinder014005581,Cut061191]
FEATURE [Part::Cut] Cut061188
  Base = -> Fusion342
  Tool = -> Fusion346
FEATURE [Part::MultiFuse] Fusion204
  Shapes = -> [Box080,Fusion339,Cylinder014005341,Cylinder014005342,Cylinder014005575]
FEATURE [Part::FeaturePython] Nut027  label="M4-Nut015"  # Fasteners workbench fastener (typed FeaturePython)
  Placement = pos=(22,17,69) rot=(0,1,0;1.5708rad)
  diameter = 6
  invert = false
  matchOuter = false
  offset = 0
  thread = false
  type = 1
FEATURE [Part::MultiFuse] Fusion345
  Shapes = -> [Cylinder014005584,Cylinder014005582,Nut027,Nut026]
FEATURE [Part::Cut] Cut061183
  Base = -> Cut061188
  Tool = -> Fusion345
FEATURE [Part::Cut] Cut061190  label="Swis Arca004"
  Base = -> Cut061183
  Placement = pos=(0,45,-27) rot=(1,0,0;0.523599rad)
  Tool = -> Fusion349
FEATURE [Sketcher::SketchObject] Sketch027
  MapMode = 5
  Placement = pos=(0,17.5,20.6314) rot=(1,0,0;3.66519rad)
  Support = -> [Cut061190]
  sketch-geometry (7):
    g0: LineSegment StartX=-2.94789 StartY=5.06305 StartZ=0 EndX=-5.85868 EndY=-0.0214232 EndZ=0
    g1: LineSegment StartX=-5.85868 StartY=-0.0214232 StartZ=0 EndX=-2.91079 EndY=-5.08448 EndZ=0
    g2: LineSegment StartX=-2.91079 StartY=-5.08448 StartZ=0 EndX=2.94789 EndY=-5.06305 EndZ=0
    g3: LineSegment StartX=2.94789 StartY=-5.06305 StartZ=0 EndX=5.85868 EndY=0.0214232 EndZ=0
    g4: LineSegment StartX=5.85868 StartY=0.0214232 StartZ=0 EndX=2.91079 EndY=5.08448 EndZ=0
    g5: LineSegment StartX=2.91079 StartY=5.08448 StartZ=0 EndX=-2.94789 EndY=5.06305 EndZ=0
    g6: Circle [constr] CenterX=0 CenterY=0 CenterZ=0 NormalX=0 NormalY=0 NormalZ=1 AngleXU=0 Radius=5.85872
  constraints (13):
    c: Coincident(g0,g1)
    c: Coincident(g1,g2)
    c: Coincident(g2,g3)
    c: Coincident(g3,g4)
    c: Coincident(g4,g5)
    c: Coincident(g5,g0)
    c: Equal(g0, g1-g5) x5
    c: PointOnObject(g0,g6)
    c: PointOnObject(g1,g6)
    c: PointOnObject(g2,g6)
    c: PointOnObject(g3,g6)
    c: PointOnObject(g4,g6)
    c: PointOnObject(g5,g6)
FEATURE [Part::Extrusion] Extrude051
  Base = -> Sketch027
  Dir = (0,0.5,-0.866025)
  DirMode = 2
  FaceMakerClass = Part::FaceMakerBullseye
  LengthFwd = 20
  LengthRev = 0
  Placement = pos=(0,-4,7) rot=(0,0,1;0rad)
  Solid = true
  Symmetric = false
FEATURE [Part::MultiFuse] Fusion352
  Shapes = -> [Cylinder014005343,Extrude051,Box084]
FEATURE [Part::Cut] Cut061184  label="For wood-tripod-plate"
  Base = -> Fusion352
  Tool = -> Fusion204
FEATURE [App::Part] Part043  label="for wood tripod"
  Group = -> [Box080,Cylinder014005343,Box081,Cylinder014005570,Box082,Cylinder014005571,Cylinder014005572,Box083,Cylinder014005573,Box084,Cylinder014005574,Cylinder014005341,Cylinder014005575,Cylinder014005342,Sketch026,Screw_solid132,Cylinder014005576,Screw_solid133,Cylinder014005577,Cylinder014005578,Screw_solid134,Box085,Cylinder014005579,Cylinder014005580,Box086,Cylinder014005581,Cylinder014005582,Box087,+39 more]
  License = CC BY 3.0
  LicenseURL = http://creativecommons.org/licenses/by/3.0/
  Origin = -> Origin043
  Placement = pos=(0,0,0) rot=(0,0,1;3.14159rad)
FEATURE [App::Part] Part010  label="Distance001"
  Group = -> [Chamfer002,Fusion093,Box011,Cylinder014005161,Cylinder014005163,Cylinder014005162,Cylinder014005160,Cylinder014005159,Cut061008,Part043]
  License = CC BY 3.0
  LicenseURL = http://creativecommons.org/licenses/by/3.0/
  Origin = -> Origin010
  Placement = pos=(0,0,49.5) rot=(0,0,1;0rad)
FEATURE [Part::FeaturePython] Nut028  label="M6-Nut010"  # Fasteners workbench fastener (typed FeaturePython)
  Placement = pos=(0,-1,-0.5) rot=(0,0,1;0rad)
  diameter = 2
  invert = false
  matchOuter = false
  offset = 0
  thread = false
  type = 2
FEATURE [Part::Cylinder] Cylinder014005586  label="Válec510"
  Angle = 360
  AttacherType = Attacher::AttachEngine3D
  Height = 20
  Placement = pos=(0,-1,0) rot=(0,0,1;0rad)
  Radius = 3.2
FEATURE [Part::Cylinder] Cylinder014005587  label="Válec511"
  Angle = 360
  AttacherType = Attacher::AttachEngine3D
  Height = 7
  Placement = pos=(7.5,7.5,7.5) rot=(1,0,0;1.5708rad)
  Radius = 2.9
FEATURE [Part::Box] Box043  label="Krychle075"
  AttacherType = Attacher::AttachEngine3D
  Height = 15
  Length = 26
  Placement = pos=(-13,-7.5,0) rot=(0,0,1;0rad)
  Width = 14
FEATURE [Part::Cylinder] Cylinder014005588  label="Válec512"
  Angle = 360
  AttacherType = Attacher::AttachEngine3D
  Height = 15
  Placement = pos=(7.5,7.5,7.5) rot=(1,0,0;1.5708rad)
  Radius = 1.7
FEATURE [Part::Cylinder] Cylinder014005589  label="Válec513"
  Angle = 360
  AttacherType = Attacher::AttachEngine3D
  Height = 6
  Placement = pos=(-7.5,7.5,7.5) rot=(1,0,0;1.5708rad)
  Radius = 2.9
FEATURE [Part::Cylinder] Cylinder014005590  label="Válec514"
  Angle = 360
  AttacherType = Attacher::AttachEngine3D
  Height = 15
  Placement = pos=(-7.5,7.5,7.5) rot=(1,0,0;1.5708rad)
  Radius = 1.7
FEATURE [Part::Box] Box088  label="Krychle076"
  AttacherType = Attacher::AttachEngine3D
  Height = 15
  Length = 9
  Placement = pos=(4,3.5,0) rot=(0,0,1;0rad)
  Width = 4
FEATURE [Part::Fillet] Fillet
  Base = -> Box088
  Edges = 1 edges r=1.5: [Edge1]
FEATURE [Part::Box] Box044  label="Krychle077"
  AttacherType = Attacher::AttachEngine3D
  Height = 15
  Length = 9
  Placement = pos=(4,3.5,0) rot=(0,0,1;0rad)
  Width = 4
FEATURE [Part::Fillet] Fillet001
  Base = -> Box044
  Edges = 1 edges r=1.5: [Edge1]
  Placement = pos=(0,0,15) rot=(0,1,0;3.14159rad)
FEATURE [Part::MultiFuse] Fusion353
  Shapes = -> [Fillet,Fillet001,Cylinder014005590,Cylinder014005588,Cylinder014005587,Cylinder014005589,Nut028,Cylinder014005586]
FEATURE [Part::Cut] Cut061192
  Base = -> Box043
  Tool = -> Fusion353
FEATURE [Part::Fillet] Fillet002  label="wieghts holder"
  Base = -> Cut061192
  Edges = 4 edges r=1.25: [Edge2,Edge39,Edge40,Edge45]
  Placement = pos=(0,0,0) rot=(-0.579113,-0.576467,-0.576467;2.0944rad)
FEATURE [Part::Cylinder] Cylinder014005602  label="Válec522"
  Angle = 360
  AttacherType = Attacher::AttachEngine3D
  Height = 15
  Placement = pos=(-7.5,7.5,7.5) rot=(1,0,0;1.5708rad)
  Radius = 1.7
FEATURE [Part::Cylinder] Cylinder014005603  label="Válec523"
  Angle = 360
  AttacherType = Attacher::AttachEngine3D
  Height = 20
  Placement = pos=(0,-1,0) rot=(0,0,1;0rad)
  Radius = 3.2
FEATURE [Part::Cylinder] Cylinder014005604  label="Válec524"
  Angle = 360
  AttacherType = Attacher::AttachEngine3D
  Height = 15
  Placement = pos=(7.5,7.5,7.5) rot=(1,0,0;1.5708rad)
  Radius = 1.7
FEATURE [Part::Cylinder] Cylinder014005605  label="Válec525"
  Angle = 360
  AttacherType = Attacher::AttachEngine3D
  Height = 7
  Placement = pos=(7.5,7.5,7.5) rot=(1,0,0;1.5708rad)
  Radius = 2.9
FEATURE [Part::Box] Box089  label="Krychle078"
  AttacherType = Attacher::AttachEngine3D
  Height = 15
  Length = 26
  Placement = pos=(-13,-7.5,0) rot=(0,0,1;0rad)
  Width = 14
FEATURE [Part::Cylinder] Cylinder014005606  label="Válec526"
  Angle = 360
  AttacherType = Attacher::AttachEngine3D
  Height = 6
  Placement = pos=(-7.5,7.5,7.5) rot=(1,0,0;1.5708rad)
  Radius = 2.9
FEATURE [Part::Box] Box090  label="Krychle079"
  AttacherType = Attacher::AttachEngine3D
  Height = 15
  Length = 9
  Placement = pos=(4,3.5,0) rot=(0,0,1;0rad)
  Width = 4
FEATURE [Part::Fillet] Fillet004
  Base = -> Box090
  Edges = 1 edges r=1.5: [Edge1]
FEATURE [Part::Box] Box091  label="Krychle080"
  AttacherType = Attacher::AttachEngine3D
  Height = 15
  Length = 9
  Placement = pos=(4,3.5,0) rot=(0,0,1;0rad)
  Width = 4
FEATURE [Part::Fillet] Fillet003
  Base = -> Box091
  Edges = 1 edges r=1.5: [Edge1]
  Placement = pos=(0,0,15) rot=(0,1,0;3.14159rad)
FEATURE [Part::FeaturePython] Nut034  label="M6-Nut009"  # Fasteners workbench fastener (typed FeaturePython)
  Placement = pos=(0,-1,-0.5) rot=(0,0,1;0rad)
  diameter = 2
  invert = false
  matchOuter = false
  offset = 0
  thread = false
  type = 2
FEATURE [Part::MultiFuse] Fusion359
  Shapes = -> [Fillet004,Fillet003,Cylinder014005602,Cylinder014005604,Cylinder014005605,Cylinder014005606,Nut034,Cylinder014005603]
FEATURE [Part::Cut] Cut061198
  Base = -> Box089
  Tool = -> Fusion359
FEATURE [Part::Fillet] Fillet005  label="wieghts holder001"
  Base = -> Cut061198
  Edges = 4 edges r=1.25: [Edge2,Edge39,Edge40,Edge45]
  Placement = pos=(38.5,-49.5,108.5) rot=(0.57735,0.57735,0.57735;4.18879rad)
FEATURE [App::Part] Part045  label="Part075"
  Group = -> [Fillet001,Fillet,Fusion353,Cylinder014005590,Cylinder014005586,Cylinder014005588,Cylinder014005587,Box043,Cylinder014005589,Box088,Box044,Cut061192,Nut028,Fillet002]
  License = CC BY 3.0
  LicenseURL = http://creativecommons.org/licenses/by/3.0/
  Origin = -> Origin045
  Placement = pos=(38.5,35,108.2) rot=(1,0,0;3.14159rad)
FEATURE [App::Part] Part046  label="Part076"
  Group = -> [Fusion359,Fillet003,Fillet004,Cylinder014005603,Cylinder014005605,Box089,Cylinder014005606,Box090,Cylinder014005602,Cylinder014005604,Box091,Cut061198,Nut034,Fillet005]
  License = CC BY 3.0
  LicenseURL = http://creativecommons.org/licenses/by/3.0/
  Origin = -> Origin046
FEATURE [App::Part] Part047  label="Holder"
  Group = -> [Part045,Part046]
  License = CC BY 3.0
  LicenseURL = http://creativecommons.org/licenses/by/3.0/
  Origin = -> Origin047
FEATURE [App::Part] Part041  label="Weights complet"
  Group = -> [Cylinder014005345,Part021,Part047]
  License = CC BY 3.0
  LicenseURL = http://creativecommons.org/licenses/by/3.0/
  Origin = -> Origin041
FEATURE [Part::FeaturePython] InvoluteGear029  # WARN: FeaturePython — macro-defined, semantics opaque (R4)
  Placement = pos=(0,0,-72) rot=(0,0,1;0rad)
  backlash = 0
  beta = 20
  clearance = 0.25
  double_helix = true
  head = 0
  height = 8
  module = 1.16
  numpoints = 6
  pressure_angle = 20
  reversed_backlash = false
  shift = 0
  simple = false
  teeth = 27
  undercut = false
FEATURE [Part::Cylinder] Cylinder014005626  label="Válec545"
  Angle = 360
  AttacherType = Attacher::AttachEngine3D
  Height = 25
  Placement = pos=(0,0,-85) rot=(0,0,1;0rad)
  Radius = 4.2
FEATURE [Part::Cylinder] Cylinder014005627  label="Válec546"
  Angle = 360
  AttacherType = Attacher::AttachEngine3D
  Height = 200
  Placement = pos=(0,0,-100) rot=(0,0,1;0rad)
  Radius = 3.9
FEATURE [Part::Cylinder] Cylinder014005628  label="Válec547"
  Angle = 360
  AttacherType = Attacher::AttachEngine3D
  Height = 11.5
  Placement = pos=(0,0,-76.1) rot=(0,0,1;0rad)
  Radius = 11
FEATURE [Part::MultiFuse] Fusion376
  Shapes = -> [Cylinder014005628,InvoluteGear029]
FEATURE [Sketcher::SketchObject] Sketch034
  MapMode = 5
  Placement = pos=(0,0,-64.6) rot=(0,0,1;0rad)
  Support = -> [Fusion376]
  sketch-geometry (7):
    g0: LineSegment StartX=-3.8831 StartY=6.55674 StartZ=0 EndX=-7.61986 EndY=-0.0844932 EndZ=0
    g1: LineSegment StartX=-7.61986 StartY=-0.0844932 StartZ=0 EndX=-3.73676 EndY=-6.64124 EndZ=0
    g2: LineSegment StartX=-3.73676 StartY=-6.64124 StartZ=0 EndX=3.8831 EndY=-6.55674 EndZ=0
    g3: LineSegment StartX=3.8831 StartY=-6.55674 StartZ=0 EndX=7.61986 EndY=0.0844932 EndZ=0
    g4: LineSegment StartX=7.61986 StartY=0.0844932 StartZ=0 EndX=3.73676 EndY=6.64124 EndZ=0
    g5: LineSegment StartX=3.73676 StartY=6.64124 StartZ=0 EndX=-3.8831 EndY=6.55674 EndZ=0
    g6: Circle [constr] CenterX=0 CenterY=0 CenterZ=0 NormalX=0 NormalY=0 NormalZ=1 AngleXU=0 Radius=7.62033
  constraints (14):
    c: Coincident(g0,g1)
    c: Coincident(g1,g2)
    c: Coincident(g2,g3)
    c: Coincident(g3,g4)
    c: Coincident(g4,g5)
    c: Coincident(g5,g0)
    c: Equal(g0, g1-g5) x5
    c: PointOnObject(g0,g6)
    c: PointOnObject(g1,g6)
    c: PointOnObject(g2,g6)
    c: PointOnObject(g3,g6)
    c: PointOnObject(g4,g6)
    c: PointOnObject(g5,g6)
    c: Coincident(g6,g-1)
FEATURE [Part::Extrusion] Extrude061
  Base = -> Sketch034
  Dir = (0,0,1)
  DirMode = 2
  FaceMakerClass = Part::FaceMakerBullseye
  LengthFwd = 5
  LengthRev = 0
  Placement = pos=(0,0,-5) rot=(0,0,1;0rad)
  Solid = true
  Symmetric = false
FEATURE [Part::MultiFuse] Fusion375
  Shapes = -> [Extrude061,Cylinder014005627]
FEATURE [Part::Cut] Cut061209  label="Gear A002"
  Base = -> Fusion376
  Tool = -> Fusion375
FEATURE [Part::Feature] Cut007_solid019  label="Sun020"
  shape: bbox 12.9 x 13.1 x 5 mm, 57 faces (baked)
FEATURE [Part::Feature] Cut061210  label="SUN I Final003"
  shape: bbox 24 x 24 x 12.25 mm, 99 faces (baked)
FEATURE [Part::Cut] Cut061211
  Base = -> Cut061210
  Placement = pos=(0,0,-76) rot=(0,0,1;0rad)
  Tool = -> Cut007_solid019
FEATURE [Part::MultiFuse] Fusion377
  Shapes = -> [Cut061209,Cut061211]
FEATURE [Part::Cut] Cut061212  label="Gear27b"
  Base = -> Fusion377
  Tool = -> Cylinder014005626
FEATURE [App::Part] Part049  label="Gear27 A002"
  Group = -> [InvoluteGear029,Cylinder014005626,Sketch034,Fusion375,Fusion376,Fusion377,Cut061209,Extrude061,Cylinder014005627,Cylinder014005628,Cut007_solid019,Cut061210,Cut061211,Cut061212]
  License = CC BY 3.0
  LicenseURL = http://creativecommons.org/licenses/by/3.0/
  Origin = -> Origin049
FEATURE [Part::FeaturePython] InvoluteGear030  # WARN: FeaturePython — macro-defined, semantics opaque (R4)
  Placement = pos=(0,0,-72) rot=(0,0,1;0rad)
  backlash = 0
  beta = 20
  clearance = 0.25
  double_helix = true
  head = 0
  height = 8
  module = 1.16
  numpoints = 6
  pressure_angle = 20
  reversed_backlash = false
  shift = 0
  simple = false
  teeth = 27
  undercut = false
FEATURE [Part::Cylinder] Cylinder014005629  label="Válec548"
  Angle = 360
  AttacherType = Attacher::AttachEngine3D
  Height = 25
  Placement = pos=(0,0,-85) rot=(0,0,1;0rad)
  Radius = 4.2
FEATURE [Part::Cylinder] Cylinder014005630  label="Válec549"
  Angle = 360
  AttacherType = Attacher::AttachEngine3D
  Height = 200
  Placement = pos=(0,0,-100) rot=(0,0,1;0rad)
  Radius = 3.9
FEATURE [Part::Cylinder] Cylinder014005631  label="Válec550"
  Angle = 360
  AttacherType = Attacher::AttachEngine3D
  Height = 11.5
  Placement = pos=(0,0,-76.1) rot=(0,0,1;0rad)
  Radius = 11
FEATURE [Part::MultiFuse] Fusion379
  Shapes = -> [Cylinder014005631,InvoluteGear030]
FEATURE [Sketcher::SketchObject] Sketch035
  MapMode = 5
  Placement = pos=(0,0,-64.6) rot=(0,0,1;0rad)
  Support = -> [Fusion379]
  sketch-geometry (7):
    g0: LineSegment StartX=-3.8831 StartY=6.55674 StartZ=0 EndX=-7.61986 EndY=-0.0844932 EndZ=0
    g1: LineSegment StartX=-7.61986 StartY=-0.0844932 StartZ=0 EndX=-3.73676 EndY=-6.64124 EndZ=0
    g2: LineSegment StartX=-3.73676 StartY=-6.64124 StartZ=0 EndX=3.8831 EndY=-6.55674 EndZ=0
    g3: LineSegment StartX=3.8831 StartY=-6.55674 StartZ=0 EndX=7.61986 EndY=0.0844932 EndZ=0
    g4: LineSegment StartX=7.61986 StartY=0.0844932 StartZ=0 EndX=3.73676 EndY=6.64124 EndZ=0
    g5: LineSegment StartX=3.73676 StartY=6.64124 StartZ=0 EndX=-3.8831 EndY=6.55674 EndZ=0
    g6: Circle [constr] CenterX=0 CenterY=0 CenterZ=0 NormalX=0 NormalY=0 NormalZ=1 AngleXU=0 Radius=7.62033
  constraints (14):
    c: Coincident(g0,g1)
    c: Coincident(g1,g2)
    c: Coincident(g2,g3)
    c: Coincident(g3,g4)
    c: Coincident(g4,g5)
    c: Coincident(g5,g0)
    c: Equal(g0, g1-g5) x5
    c: PointOnObject(g0,g6)
    c: PointOnObject(g1,g6)
    c: PointOnObject(g2,g6)
    c: PointOnObject(g3,g6)
    c: PointOnObject(g4,g6)
    c: PointOnObject(g5,g6)
    c: Coincident(g6,g-1)
FEATURE [Part::Extrusion] Extrude062
  Base = -> Sketch035
  Dir = (0,0,1)
  DirMode = 2
  FaceMakerClass = Part::FaceMakerBullseye
  LengthFwd = 5
  LengthRev = 0
  Placement = pos=(0,0,-5) rot=(0,0,1;0rad)
  Solid = true
  Symmetric = false
FEATURE [Part::MultiFuse] Fusion378
  Shapes = -> [Extrude062,Cylinder014005630]
FEATURE [Part::Cut] Cut061213  label="Gear A003"
  Base = -> Fusion379
  Tool = -> Fusion378
FEATURE [Part::Feature] Cut007_solid020  label="Sun021"
  shape: bbox 12.9 x 13.1 x 5 mm, 57 faces (baked)
FEATURE [Part::Feature] Cut061214  label="SUN I Final004"
  shape: bbox 24 x 24 x 12.25 mm, 99 faces (baked)
FEATURE [Part::Cut] Cut061215
  Base = -> Cut061214
  Placement = pos=(0,0,-76) rot=(0,0,1;0rad)
  Tool = -> Cut007_solid020
FEATURE [Part::MultiFuse] Fusion380
  Shapes = -> [Cut061213,Cut061215]
FEATURE [Part::Cut] Cut061216  label="Gear27b001"
  Base = -> Fusion380
  Tool = -> Cylinder014005629
FEATURE [App::Part] Part050  label="Gear27 A003"
  Group = -> [InvoluteGear030,Cylinder014005629,Sketch035,Fusion378,Fusion379,Fusion380,Cut061213,Extrude062,Cylinder014005630,Cylinder014005631,Cut007_solid020,Cut061214,Cut061215,Cut061216]
  License = CC BY 3.0
  LicenseURL = http://creativecommons.org/licenses/by/3.0/
  Origin = -> Origin050
FEATURE [Part::FeaturePython] InvoluteGear031  # WARN: FeaturePython — macro-defined, semantics opaque (R4)
  Placement = pos=(0,0,-72) rot=(0,0,1;0rad)
  backlash = 0
  beta = 20
  clearance = 0.25
  double_helix = true
  head = 0
  height = 8
  module = 1.16
  numpoints = 6
  pressure_angle = 20
  reversed_backlash = false
  shift = 0
  simple = false
  teeth = 27
  undercut = false
FEATURE [Part::Cylinder] Cylinder014005632  label="Válec551"
  Angle = 360
  AttacherType = Attacher::AttachEngine3D
  Height = 25
  Placement = pos=(0,0,-85) rot=(0,0,1;0rad)
  Radius = 4.2
FEATURE [Part::Cylinder] Cylinder014005633  label="Válec552"
  Angle = 360
  AttacherType = Attacher::AttachEngine3D
  Height = 200
  Placement = pos=(0,0,-100) rot=(0,0,1;0rad)
  Radius = 3.9
FEATURE [Part::Cylinder] Cylinder014005634  label="Válec553"
  Angle = 360
  AttacherType = Attacher::AttachEngine3D
  Height = 11.5
  Placement = pos=(0,0,-76.1) rot=(0,0,1;0rad)
  Radius = 11
FEATURE [Part::MultiFuse] Fusion382
  Shapes = -> [Cylinder014005634,InvoluteGear031]
FEATURE [Sketcher::SketchObject] Sketch036
  MapMode = 5
  Placement = pos=(0,0,-64.6) rot=(0,0,1;0rad)
  Support = -> [Fusion382]
  sketch-geometry (7):
    g0: LineSegment StartX=-3.8831 StartY=6.55674 StartZ=0 EndX=-7.61986 EndY=-0.0844932 EndZ=0
    g1: LineSegment StartX=-7.61986 StartY=-0.0844932 StartZ=0 EndX=-3.73676 EndY=-6.64124 EndZ=0
    g2: LineSegment StartX=-3.73676 StartY=-6.64124 StartZ=0 EndX=3.8831 EndY=-6.55674 EndZ=0
    g3: LineSegment StartX=3.8831 StartY=-6.55674 StartZ=0 EndX=7.61986 EndY=0.0844932 EndZ=0
    g4: LineSegment StartX=7.61986 StartY=0.0844932 StartZ=0 EndX=3.73676 EndY=6.64124 EndZ=0
    g5: LineSegment StartX=3.73676 StartY=6.64124 StartZ=0 EndX=-3.8831 EndY=6.55674 EndZ=0
    g6: Circle [constr] CenterX=0 CenterY=0 CenterZ=0 NormalX=0 NormalY=0 NormalZ=1 AngleXU=0 Radius=7.62033
  constraints (14):
    c: Coincident(g0,g1)
    c: Coincident(g1,g2)
    c: Coincident(g2,g3)
    c: Coincident(g3,g4)
    c: Coincident(g4,g5)
    c: Coincident(g5,g0)
    c: Equal(g0, g1-g5) x5
    c: PointOnObject(g0,g6)
    c: PointOnObject(g1,g6)
    c: PointOnObject(g2,g6)
    c: PointOnObject(g3,g6)
    c: PointOnObject(g4,g6)
    c: PointOnObject(g5,g6)
    c: Coincident(g6,g-1)
FEATURE [Part::Extrusion] Extrude063
  Base = -> Sketch036
  Dir = (0,0,1)
  DirMode = 2
  FaceMakerClass = Part::FaceMakerBullseye
  LengthFwd = 5
  LengthRev = 0
  Placement = pos=(0,0,-5) rot=(0,0,1;0rad)
  Solid = true
  Symmetric = false
FEATURE [Part::MultiFuse] Fusion381
  Shapes = -> [Extrude063,Cylinder014005633]
FEATURE [Part::Cut] Cut061217  label="Gear A004"
  Base = -> Fusion382
  Tool = -> Fusion381
FEATURE [Part::Feature] Cut007_solid021  label="Sun022"
  shape: bbox 12.9 x 13.1 x 5 mm, 57 faces (baked)
FEATURE [Part::Feature] Cut061218  label="SUN I Final005"
  shape: bbox 24 x 24 x 12.25 mm, 99 faces (baked)
FEATURE [Part::Cut] Cut061219
  Base = -> Cut061218
  Placement = pos=(0,0,-76) rot=(0,0,1;0rad)
  Tool = -> Cut007_solid021
FEATURE [Part::MultiFuse] Fusion383
  Shapes = -> [Cut061217,Cut061219]
FEATURE [Part::Cut] Cut061221  label="Gear27b002"
  Base = -> Fusion383
  Tool = -> Cylinder014005632
FEATURE [Part::Cylinder] Cylinder014005635  label="Válec554"
  Angle = 360
  AttacherType = Attacher::AttachEngine3D
  Height = 6
  Placement = pos=(0,0,-68.1) rot=(0,0,1;0rad)
  Radius = 19
FEATURE [Part::Cut] Cut061220  label="Gear27"
  Base = -> Cut061221
  Tool = -> Cylinder014005635
FEATURE [App::Part] Part051  label="Gear27 A004"
  Group = -> [InvoluteGear031,Cylinder014005632,Sketch036,Fusion381,Fusion382,Fusion383,Cut061217,Extrude063,Cylinder014005633,Cylinder014005634,Cut007_solid021,Cut061218,Cut061219,Cut061221,Cylinder014005635,Cut061220]
  License = CC BY 3.0
  LicenseURL = http://creativecommons.org/licenses/by/3.0/
  Origin = -> Origin051
FEATURE [App::Part] Part037  label="RA-OLD"
  Group = -> [Part035,Part036,Part038,Screw011,Part032,Part039,Part050,Part051]
  License = CC BY 3.0
  LicenseURL = http://creativecommons.org/licenses/by/3.0/
  Origin = -> Origin038
  Placement = pos=(0,-20,0) rot=(0,0,1;3.14159rad)
FEATURE [Part::FeaturePython] InvoluteGear032  # WARN: FeaturePython — macro-defined, semantics opaque (R4)
  Placement = pos=(0,0,-72) rot=(0,0,1;0rad)
  backlash = 0
  beta = 20
  clearance = 0.25
  double_helix = true
  head = 0
  height = 8
  module = 1.16
  numpoints = 6
  pressure_angle = 20
  reversed_backlash = false
  shift = 0
  simple = false
  teeth = 27
  undercut = false
FEATURE [Part::Cylinder] Cylinder014005636  label="Válec555"
  Angle = 360
  AttacherType = Attacher::AttachEngine3D
  Height = 25
  Placement = pos=(0,0,-85) rot=(0,0,1;0rad)
  Radius = 4.2
FEATURE [Part::Cylinder] Cylinder014005637  label="Válec556"
  Angle = 360
  AttacherType = Attacher::AttachEngine3D
  Height = 200
  Placement = pos=(0,0,-100) rot=(0,0,1;0rad)
  Radius = 3.9
FEATURE [Part::Cylinder] Cylinder014005638  label="Válec557"
  Angle = 360
  AttacherType = Attacher::AttachEngine3D
  Height = 11.5
  Placement = pos=(0,0,-76.1) rot=(0,0,1;0rad)
  Radius = 11
FEATURE [Part::MultiFuse] Fusion385
  Shapes = -> [Cylinder014005638,InvoluteGear032]
FEATURE [Sketcher::SketchObject] Sketch037
  MapMode = 5
  Placement = pos=(0,0,-64.6) rot=(0,0,1;0rad)
  Support = -> [Fusion385]
  sketch-geometry (7):
    g0: LineSegment StartX=-3.8831 StartY=6.55674 StartZ=0 EndX=-7.61986 EndY=-0.0844932 EndZ=0
    g1: LineSegment StartX=-7.61986 StartY=-0.0844932 StartZ=0 EndX=-3.73676 EndY=-6.64124 EndZ=0
    g2: LineSegment StartX=-3.73676 StartY=-6.64124 StartZ=0 EndX=3.8831 EndY=-6.55674 EndZ=0
    g3: LineSegment StartX=3.8831 StartY=-6.55674 StartZ=0 EndX=7.61986 EndY=0.0844932 EndZ=0
    g4: LineSegment StartX=7.61986 StartY=0.0844932 StartZ=0 EndX=3.73676 EndY=6.64124 EndZ=0
    g5: LineSegment StartX=3.73676 StartY=6.64124 StartZ=0 EndX=-3.8831 EndY=6.55674 EndZ=0
    g6: Circle [constr] CenterX=0 CenterY=0 CenterZ=0 NormalX=0 NormalY=0 NormalZ=1 AngleXU=0 Radius=7.62033
  constraints (14):
    c: Coincident(g0,g1)
    c: Coincident(g1,g2)
    c: Coincident(g2,g3)
    c: Coincident(g3,g4)
    c: Coincident(g4,g5)
    c: Coincident(g5,g0)
    c: Equal(g0, g1-g5) x5
    c: PointOnObject(g0,g6)
    c: PointOnObject(g1,g6)
    c: PointOnObject(g2,g6)
    c: PointOnObject(g3,g6)
    c: PointOnObject(g4,g6)
    c: PointOnObject(g5,g6)
    c: Coincident(g6,g-1)
FEATURE [Part::Extrusion] Extrude064
  Base = -> Sketch037
  Dir = (0,0,1)
  DirMode = 2
  FaceMakerClass = Part::FaceMakerBullseye
  LengthFwd = 5
  LengthRev = 0
  Placement = pos=(0,0,-5) rot=(0,0,1;0rad)
  Solid = true
  Symmetric = false
FEATURE [Part::MultiFuse] Fusion384
  Shapes = -> [Extrude064,Cylinder014005637]
FEATURE [Part::Cut] Cut061222  label="Gear A005"
  Base = -> Fusion385
  Tool = -> Fusion384
FEATURE [Part::Feature] Cut007_solid022  label="Sun023"
  shape: bbox 12.9 x 13.1 x 5 mm, 57 faces (baked)
FEATURE [Part::Feature] Cut061223  label="SUN I Final006"
  shape: bbox 24 x 24 x 12.25 mm, 99 faces (baked)
FEATURE [Part::Cut] Cut061224
  Base = -> Cut061223
  Placement = pos=(0,0,-76) rot=(0,0,1;0rad)
  Tool = -> Cut007_solid022
FEATURE [Part::MultiFuse] Fusion386
  Shapes = -> [Cut061222,Cut061224]
FEATURE [Part::Cut] Cut061226  label="Gear27b003"
  Base = -> Fusion386
  Tool = -> Cylinder014005636
FEATURE [Part::Cylinder] Cylinder014005639  label="Válec558"
  Angle = 360
  AttacherType = Attacher::AttachEngine3D
  Height = 6
  Placement = pos=(0,0,-68.1) rot=(0,0,1;0rad)
  Radius = 19
FEATURE [Part::Cut] Cut061225  label="Gear028"
  Base = -> Cut061226
  Tool = -> Cylinder014005639
FEATURE [App::Part] Part052  label="Gear27 A005"
  Group = -> [InvoluteGear032,Cylinder014005636,Sketch037,Fusion384,Fusion385,Fusion386,Cut061222,Extrude064,Cylinder014005637,Cylinder014005638,Cut007_solid022,Cut061223,Cut061224,Cut061226,Cylinder014005639,Cut061225]
  License = CC BY 3.0
  LicenseURL = http://creativecommons.org/licenses/by/3.0/
  Origin = -> Origin052
FEATURE [Part::Cylinder] Cylinder014005353  label="Válec559"
  Angle = 360
  AttacherType = Attacher::AttachEngine3D
  Height = 60
  Placement = pos=(-30,17,69) rot=(0,1,0;1.5708rad)
  Radius = 2.7
FEATURE [Part::Box] Box100  label="Krychle089"
  AttacherType = Attacher::AttachEngine3D
  Height = 112
  Length = 38
  Placement = pos=(-19,32,-52) rot=(0,0,1;0rad)
  Width = 10
FEATURE [Part::Box] Box101  label="Krychle090"
  AttacherType = Attacher::AttachEngine3D
  Height = 112
  Length = 38
  Placement = pos=(-19,34,-52) rot=(0,0,1;0rad)
  Width = 6
FEATURE [Part::Box] Box102  label="Krychle091"
  AttacherType = Attacher::AttachEngine3D
  Height = 15
  Length = 50
  Placement = pos=(-25,-25,64) rot=(0,0,1;0rad)
  Width = 50
FEATURE [Part::Cylinder] Cylinder014005640  label="Válec560"
  Angle = 360
  AttacherType = Attacher::AttachEngine3D
  Height = 2.5
  Placement = pos=(0,-12,71) rot=(0,0,1;0rad)
  Radius = 6
FEATURE [Part::Box] Box103  label="Krychle092"
  AttacherType = Attacher::AttachEngine3D
  Height = 20
  Length = 60
  Placement = pos=(-14,-30,62) rot=(0,0,1;0rad)
  Width = 60
FEATURE [Part::Cylinder] Cylinder014005641  label="Válec561"
  Angle = 360
  AttacherType = Attacher::AttachEngine3D
  Height = 2.5
  Placement = pos=(0,-12,71) rot=(0,0,1;0rad)
  Radius = 6
FEATURE [Part::Box] Box051  label="Krychle093"
  AttacherType = Attacher::AttachEngine3D
  Height = 15
  Length = 50
  Placement = pos=(-25,-25,64) rot=(0,0,1;0rad)
  Width = 50
FEATURE [Part::Cylinder] Cylinder014005642  label="Válec562"
  Angle = 360
  AttacherType = Attacher::AttachEngine3D
  Height = 2.5
  Placement = pos=(0,-12,71) rot=(0,0,1;0rad)
  Radius = 6
FEATURE [Part::Cut] Cut061230
  Base = -> Box100
  Tool = -> Box101
FEATURE [Part::Box] Box104  label="Krychle094"
  AttacherType = Attacher::AttachEngine3D
  Height = 112
  Length = 38
  Placement = pos=(-19,34,-52) rot=(0,0,1;0rad)
  Width = 6
FEATURE [Part::Box] Box105  label="Krychle095"
  AttacherType = Attacher::AttachEngine3D
  Height = 15
  Length = 2
  Placement = pos=(-15.5,-26,61) rot=(0,0,1;0rad)
  Width = 52
FEATURE [Part::Box] Box106  label="Krychle096"
  AttacherType = Attacher::AttachEngine3D
  Height = 2.5
  Length = 12
  Placement = pos=(-6,-25,71) rot=(0,0,1;0rad)
  Width = 13
FEATURE [Part::Box] Box107  label="Krychle097"
  AttacherType = Attacher::AttachEngine3D
  Height = 2.5
  Length = 12
  Placement = pos=(-6,-25,71) rot=(0,0,1;0rad)
  Width = 13
FEATURE [Sketcher::SketchObject] Sketch039
  MapMode = 5
  Placement = pos=(0,0,60) rot=(0,0,1;0rad)
  sketch-geometry (6):
    g0: LineSegment StartX=-18.9734 StartY=34.0308 StartZ=0 EndX=-16.0253 EndY=36.9748 EndZ=0
    g1: LineSegment StartX=18.996 StartY=34.0308 StartZ=0 EndX=16.044 EndY=36.9748 EndZ=0
    g2: LineSegment StartX=18.996 StartY=34.0308 StartZ=0 EndX=-18.9734 EndY=34.0308 EndZ=0
    g3: LineSegment StartX=-18.9734 StartY=40.0311 StartZ=0 EndX=-16.0253 EndY=36.9748 EndZ=0
    g4: LineSegment StartX=16.044 StartY=36.9748 StartZ=0 EndX=18.9109 EndY=40.0311 EndZ=0
    g5: LineSegment StartX=-18.9734 StartY=40.0311 StartZ=0 EndX=18.9109 EndY=40.0311 EndZ=0
  constraints (7):
    c: Coincident(g2,g1)
    c: Coincident(g2,g0)
    c: Horizontal(g2)
    c: Coincident(g3,g0)
    c: Coincident(g5,g3)
    c: Coincident(g5,g4)
    c: Horizontal(g5)
FEATURE [Part::Extrusion] Extrude065
  Base = -> Sketch039
  Dir = (0,0,1)
  DirMode = 2
  FaceMakerClass = Part::FaceMakerBullseye
  LengthFwd = -112
  LengthRev = 0
  Solid = true
  Symmetric = false
FEATURE [Part::Cylinder] Cylinder014005643  label="Válec563"
  Angle = 360
  AttacherType = Attacher::AttachEngine3D
  Height = 18
  Placement = pos=(0,70,0) rot=(0,0,1;0rad)
  Radius = 3
FEATURE [Part::Cylinder] Cylinder014005644  label="Válec564"
  Angle = 360
  AttacherType = Attacher::AttachEngine3D
  Height = 60
  Placement = pos=(-30,17,69) rot=(0,1,0;1.5708rad)
  Radius = 2.7
FEATURE [Part::Box] Box108  label="Krychle098"
  AttacherType = Attacher::AttachEngine3D
  Height = 0.6
  Length = 15
  Placement = pos=(-28.5,-30,63.6) rot=(0,0,1;0rad)
  Width = 60
FEATURE [Part::Box] Box109  label="Krychle099"
  AttacherType = Attacher::AttachEngine3D
  Height = 8
  Length = 50
  Placement = pos=(-25,0,3) rot=(0,0,1;0rad)
  Width = 82
FEATURE [Part::Cylinder] Cylinder014005645  label="Válec565"
  Angle = 360
  AttacherType = Attacher::AttachEngine3D
  Height = 18
  Placement = pos=(0,45,6) rot=(0,0,1;0rad)
  Radius = 4.9
FEATURE [Part::Box] Box110  label="Krychle100"
  AttacherType = Attacher::AttachEngine3D
  Height = 15
  Length = 2
  Placement = pos=(-15.5,-26,64) rot=(0,0,1;0rad)
  Width = 52
FEATURE [Part::Cylinder] Cylinder014005646  label="Válec566"
  Angle = 360
  AttacherType = Attacher::AttachEngine3D
  Height = 18
  Placement = pos=(0,45,3) rot=(0,0,1;0rad)
  Radius = 4.35
FEATURE [Part::Cylinder] Cylinder014005647  label="Válec567"
  Angle = 360
  AttacherType = Attacher::AttachEngine3D
  Height = 2.5
  Placement = pos=(0,-12,71) rot=(0,0,1;0rad)
  Radius = 6
FEATURE [Part::Cylinder] Cylinder014005648  label="Válec568"
  Angle = 360
  AttacherType = Attacher::AttachEngine3D
  Height = 60
  Placement = pos=(-30,-17,69) rot=(0,1,0;1.5708rad)
  Radius = 2.7
FEATURE [Part::Cylinder] Cylinder014005649  label="Válec569"
  Angle = 360
  AttacherType = Attacher::AttachEngine3D
  Height = 10
  Placement = pos=(0,15,48) rot=(0,0,1;0rad)
  Radius = 5.2
FEATURE [Sketcher::SketchObject] Sketch040
  MapMode = 5
  Placement = pos=(0,0,60) rot=(0,0,1;0rad)
  sketch-geometry (6):
    g0: LineSegment StartX=-18.9734 StartY=34.0308 StartZ=0 EndX=-16.0253 EndY=36.9748 EndZ=0
    g1: LineSegment StartX=18.996 StartY=34.0308 StartZ=0 EndX=16.044 EndY=36.9748 EndZ=0
    g2: LineSegment StartX=18.996 StartY=34.0308 StartZ=0 EndX=-18.9734 EndY=34.0308 EndZ=0
    g3: LineSegment StartX=-18.9734 StartY=40.0311 StartZ=0 EndX=-16.0253 EndY=36.9748 EndZ=0
    g4: LineSegment StartX=16.044 StartY=36.9748 StartZ=0 EndX=18.9109 EndY=40.0311 EndZ=0
    g5: LineSegment StartX=-18.9734 StartY=40.0311 StartZ=0 EndX=18.9109 EndY=40.0311 EndZ=0
  constraints (7):
    c: Coincident(g2,g1)
    c: Coincident(g2,g0)
    c: Horizontal(g2)
    c: Coincident(g3,g0)
    c: Coincident(g5,g3)
    c: Coincident(g5,g4)
    c: Horizontal(g5)
FEATURE [Part::Box] Box048  label="Krychle041"
  AttacherType = Attacher::AttachEngine3D
  Height = 15
  Length = 50
  Placement = pos=(-25,-25,64) rot=(0,0,1;0rad)
  Width = 50
FEATURE [Part::Box] Box050  label="Krychle101"
  AttacherType = Attacher::AttachEngine3D
  Height = 20
  Length = 60
  Placement = pos=(-14,-30,62) rot=(0,0,1;0rad)
  Width = 60
FEATURE [Part::Cylinder] Cylinder014005650  label="Válec570"
  Angle = 360
  AttacherType = Attacher::AttachEngine3D
  Height = 2.5
  Placement = pos=(0,-12,71) rot=(0,0,1;0rad)
  Radius = 6
FEATURE [Part::Box] Box111  label="Krychle102"
  AttacherType = Attacher::AttachEngine3D
  Height = 112
  Length = 38
  Placement = pos=(-19,32,-52) rot=(0,0,1;0rad)
  Width = 10
FEATURE [Part::Cylinder] Cylinder014005651  label="Válec571"
  Angle = 360
  AttacherType = Attacher::AttachEngine3D
  Height = 2.5
  Placement = pos=(0,-12,71) rot=(0,0,1;0rad)
  Radius = 6
FEATURE [Part::Box] Box049  label="Krychle042"
  AttacherType = Attacher::AttachEngine3D
  Height = 112
  Length = 38
  Placement = pos=(-19,34,-52) rot=(0,0,1;0rad)
  Width = 6
FEATURE [Part::Box] Box046  label="Krychle039"
  AttacherType = Attacher::AttachEngine3D
  Height = 15
  Length = 2
  Placement = pos=(-15.5,-26,61) rot=(0,0,1;0rad)
  Width = 52
FEATURE [Part::Box] Box112  label="Krychle037"
  AttacherType = Attacher::AttachEngine3D
  Height = 2.5
  Length = 12
  Placement = pos=(-6,-25,71) rot=(0,0,1;0rad)
  Width = 13
FEATURE [Part::MultiFuse] Fusion209
  Placement = pos=(0,0,1) rot=(0,0,1;3.14159rad)
  Shapes = -> [Box112,Cylinder014005651]
FEATURE [Part::Box] Box045  label="Krychle038"
  AttacherType = Attacher::AttachEngine3D
  Height = 2.5
  Length = 12
  Placement = pos=(-6,-25,71) rot=(0,0,1;0rad)
  Width = 13
FEATURE [Part::MultiFuse] Fusion207
  Placement = pos=(0,0,1) rot=(0,0,1;0rad)
  Shapes = -> [Box045,Cylinder014005650,Fusion209]
FEATURE [Part::Cylinder] Cylinder014005652  label="Válec572"
  Angle = 360
  AttacherType = Attacher::AttachEngine3D
  Height = 60
  Placement = pos=(-30,-17,69) rot=(0,1,0;1.5708rad)
  Radius = 2.7
FEATURE [Part::Cylinder] Cylinder014005653  label="Válec573"
  Angle = 360
  AttacherType = Attacher::AttachEngine3D
  Height = 60
  Placement = pos=(-30,17,69) rot=(0,1,0;1.5708rad)
  Radius = 2.7
FEATURE [Part::MultiFuse] Fusion210
  Shapes = -> [Cylinder014005653,Cylinder014005652]
FEATURE [Part::MultiFuse] Fusion211  label="diry009"
  Shapes = -> [Fusion210,Fusion207]
FEATURE [Part::Box] Box047  label="Krychle040"
  AttacherType = Attacher::AttachEngine3D
  Height = 112
  Length = 38
  Placement = pos=(-19,32,-52) rot=(0,0,1;0rad)
  Width = 10
FEATURE [Part::Cut] Cut061091
  Base = -> Box047
  Tool = -> Box049
FEATURE [Part::Cut] Cut061237
  Base = -> Box111
  Tool = -> Box104
FEATURE [Part::MultiFuse] Fusion215
  Placement = pos=(0,0,1) rot=(0,0,1;3.14159rad)
  Shapes = -> [Box107,Cylinder014005641]
FEATURE [Part::MultiFuse] Fusion214
  Placement = pos=(0,0,1) rot=(0,0,1;0rad)
  Shapes = -> [Box106,Cylinder014005642,Fusion215]
FEATURE [Part::Extrusion] Extrude066
  Base = -> Sketch040
  Dir = (0,0,1)
  DirMode = 2
  FaceMakerClass = Part::FaceMakerBullseye
  LengthFwd = -112
  LengthRev = 0
  Solid = true
  Symmetric = false
FEATURE [Part::MultiFuse] Fusion208  label="Arca plate base005"
  Placement = pos=(0,-6.5,115.5) rot=(-1,0,0;1.5708rad)
  Shapes = -> [Extrude066,Cut061091]
FEATURE [Part::Cut] Cut061234  label="Arca sw 007"
  Base = -> Box048
  Tool = -> Fusion208
FEATURE [Part::Cut] Cut061087
  Base = -> Cut061234
  Tool = -> Box046
FEATURE [Part::Cut] Cut061092
  Base = -> Cut061087
  Tool = -> Fusion211
FEATURE [Part::Cut] Cut061233  label="SwissAcaB"
  Base = -> Cut061092
  Placement = pos=(0,-1,0) rot=(1,0,0;0.523599rad)
  Tool = -> Box050
FEATURE [Part::Cylinder] Cylinder014005654  label="Válec574"
  Angle = 360
  AttacherType = Attacher::AttachEngine3D
  Height = 60
  Placement = pos=(-30,-17,69) rot=(0,1,0;1.5708rad)
  Radius = 2.7
FEATURE [Part::MultiFuse] Fusion212
  Shapes = -> [Cylinder014005353,Cylinder014005654]
FEATURE [Part::MultiFuse] Fusion213  label="diry010"
  Shapes = -> [Fusion212,Fusion214]
FEATURE [Sketcher::SketchObject] Sketch012
  MapMode = 5
  Placement = pos=(0,0,60) rot=(0,0,1;0rad)
  sketch-geometry (6):
    g0: LineSegment StartX=-18.9734 StartY=34.0308 StartZ=0 EndX=-16.0253 EndY=36.9748 EndZ=0
    g1: LineSegment StartX=18.996 StartY=34.0308 StartZ=0 EndX=16.044 EndY=36.9748 EndZ=0
    g2: LineSegment StartX=18.996 StartY=34.0308 StartZ=0 EndX=-18.9734 EndY=34.0308 EndZ=0
    g3: LineSegment StartX=-18.9734 StartY=40.0311 StartZ=0 EndX=-16.0253 EndY=36.9748 EndZ=0
    g4: LineSegment StartX=16.044 StartY=36.9748 StartZ=0 EndX=18.9109 EndY=40.0311 EndZ=0
    g5: LineSegment StartX=-18.9734 StartY=40.0311 StartZ=0 EndX=18.9109 EndY=40.0311 EndZ=0
  constraints (7):
    c: Coincident(g2,g1)
    c: Coincident(g2,g0)
    c: Horizontal(g2)
    c: Coincident(g3,g0)
    c: Coincident(g5,g3)
    c: Coincident(g5,g4)
    c: Horizontal(g5)
FEATURE [Part::Extrusion] Extrude067
  Base = -> Sketch012
  Dir = (0,0,1)
  DirMode = 2
  FaceMakerClass = Part::FaceMakerBullseye
  LengthFwd = -112
  LengthRev = 0
  Solid = true
  Symmetric = false
FEATURE [Part::MultiFuse] Fusion216  label="Arca plate base011"
  Placement = pos=(0,-6.5,115.5) rot=(-1,0,0;1.5708rad)
  Shapes = -> [Extrude067,Cut061237]
FEATURE [Part::Cut] Cut061236  label="Arca sw 008"
  Base = -> Box051
  Tool = -> Fusion216
FEATURE [Part::Cut] Cut061097
  Base = -> Cut061236
  Tool = -> Box105
FEATURE [Part::Cut] Cut061235
  Base = -> Cut061097
  Tool = -> Fusion213
FEATURE [Part::Cut] Cut061096  label="SwissAcaB001"
  Base = -> Cut061235
  Placement = pos=(0,-1,0) rot=(1,0,0;0.523599rad)
  Tool = -> Box103
FEATURE [Part::MultiFuse] Fusion387
  Shapes = -> [Cylinder014005644,Cylinder014005648]
FEATURE [Part::MultiFuse] Fusion389
  Shapes = -> [Cylinder014005643,Cylinder014005645,Cylinder014005646]
FEATURE [Part::Cut] Cut061232  label="deska009"
  Base = -> Box109
  Placement = pos=(0,-26.5,61.5) rot=(-1,0,0;0.523599rad)
  Tool = -> Fusion389
FEATURE [Part::MultiFuse] Fusion391
  Shapes = -> [Box108,Box110]
FEATURE [Part::MultiFuse] Fusion393  label="Arca plate base012"
  Placement = pos=(0,-6.5,115.5) rot=(-1,0,0;1.5708rad)
  Shapes = -> [Extrude065,Cut061230]
FEATURE [Part::Cut] Cut061231  label="Arca sw 006"
  Base = -> Box102
  Tool = -> Fusion393
FEATURE [Part::Box] Box113  label="Krychle103"
  AttacherType = Attacher::AttachEngine3D
  Height = 2.5
  Length = 12
  Placement = pos=(-6,-25,71) rot=(0,0,1;0rad)
  Width = 13
FEATURE [Part::Box] Box114  label="Krychle104"
  AttacherType = Attacher::AttachEngine3D
  Height = 15
  Length = 2
  Placement = pos=(-15.5,-26,61) rot=(0,0,1;0rad)
  Width = 52
FEATURE [Part::Cut] Cut061227
  Base = -> Cut061231
  Tool = -> Box114
FEATURE [Sketcher::SketchObject] Sketch038
  MapMode = 5
  Placement = pos=(25,0,0) rot=(0.57735,0.57735,0.57735;2.0944rad)
  Support = -> [Cut061227]
  sketch-geometry (3):
    g0: LineSegment StartX=-8.69466 StartY=63.7145 StartZ=0 EndX=24.7095 EndY=63.7145 EndZ=0
    g1: LineSegment StartX=24.7095 StartY=63.7145 StartZ=0 EndX=8 EndY=54 EndZ=0
    g2: LineSegment StartX=8 StartY=54 StartZ=0 EndX=-8.69466 EndY=63.7145 EndZ=0
  constraints (4):
    c: Horizontal(g0)
    c: Coincident(g0,g1)
    c: Coincident(g1,g2)
    c: Coincident(g2,g0)
FEATURE [Part::Box] Box115  label="Krychle105"
  AttacherType = Attacher::AttachEngine3D
  Height = 2.5
  Length = 12
  Placement = pos=(-6,-25,71) rot=(0,0,1;0rad)
  Width = 13
FEATURE [Part::MultiFuse] Fusion394
  Placement = pos=(0,0,1) rot=(0,0,1;3.14159rad)
  Shapes = -> [Box115,Cylinder014005640]
FEATURE [Part::MultiFuse] Fusion392
  Placement = pos=(0,0,1) rot=(0,0,1;0rad)
  Shapes = -> [Box113,Cylinder014005647,Fusion394]
FEATURE [Part::MultiFuse] Fusion390  label="diry011"
  Shapes = -> [Fusion387,Fusion392]
FEATURE [Part::Extrusion] Extrude068
  Base = -> Sketch038
  Dir = (1,0,0)
  DirMode = 2
  FaceMakerClass = Part::FaceMakerBullseye
  LengthFwd = -50
  LengthRev = 0
  Placement = pos=(0,-0.5,0.5) rot=(0,0,1;0rad)
  Solid = true
  Symmetric = false
FEATURE [Part::MultiFuse] Fusion388
  Shapes = -> [Cut061227,Extrude068,Cut061232]
FEATURE [Part::Cut] Cut061228
  Base = -> Fusion388
  Tool = -> Fusion390
FEATURE [Part::Cut] Cut061229  label="wood-tripod-plate"
  Base = -> Cut061228
  Placement = pos=(0,-1,0) rot=(1,0,0;0.523599rad)
  Tool = -> Fusion391
FEATURE [Part::Cut] Cut061086  label="wod-tripod-plate"
  Base = -> Cut061229
  Tool = -> Cylinder014005649
FEATURE [Part::Cut] Cut061238  label="wood-tripod-arca"
  Base = -> Cut061086
  Tool = -> Cut061233
FEATURE [App::Part] Part053  label="wood-tripod-plate001"
  Group = -> [Box100,Box101,Box102,Cylinder014005640,Fusion210,Fusion211,Fusion207,Fusion209,Extrude065,Cut061227,Cut061228,Cut061229,Cut061230,Cut061231,Cut061232,Sketch038,Sketch039,Cylinder014005643,Cylinder014005644,Box108,Box109,Cylinder014005645,Box110,Cylinder014005646,Cylinder014005647,Cylinder014005648,Cylinder014005649,Cut061092,Cut061233,Cut061086,Cut061087,Cut061234,Cut061091,Fusion208,Sketch040,+48 more]
  License = CC BY 3.0
  LicenseURL = http://creativecommons.org/licenses/by/3.0/
  Origin = -> Origin053
  Placement = pos=(0,-34,-37) rot=(0,0,1;3.14159rad)
FEATURE [Part::Cylinder] Cylinder014005655  label="Válec575"
  Angle = 360
  AttacherType = Attacher::AttachEngine3D
  Height = 20
  Placement = pos=(0,-1,0) rot=(0,0,1;0rad)
  Radius = 3.2
FEATURE [Part::Cylinder] Cylinder014005656  label="Válec576"
  Angle = 360
  AttacherType = Attacher::AttachEngine3D
  Height = 15
  Placement = pos=(7.5,7.5,7.5) rot=(1,0,0;1.5708rad)
  Radius = 1.7
FEATURE [Part::Cylinder] Cylinder014005659  label="Válec579"
  Angle = 360
  AttacherType = Attacher::AttachEngine3D
  Height = 15
  Placement = pos=(-7.5,7.5,7.5) rot=(1,0,0;1.5708rad)
  Radius = 1.7
FEATURE [Part::Box] Box117  label="Krychle107"
  AttacherType = Attacher::AttachEngine3D
  Height = 15
  Length = 26
  Placement = pos=(-13,-5.5,0) rot=(0,0,1;0rad)
  Width = 14
FEATURE [Part::Box] Box118  label="Krychle108"
  AttacherType = Attacher::AttachEngine3D
  Height = 15
  Length = 26
  Placement = pos=(-13,-3.5,0) rot=(0,0,1;0rad)
  Width = 14
FEATURE [Part::MultiFuse] Fusion395
  Shapes = -> [Cylinder014005659,Cylinder014005656,Cylinder014005655,Box118]
FEATURE [Part::Cut] Cut061239
  Base = -> Box117
  Tool = -> Fusion395
FEATURE [Part::Fillet] Fillet006  label="Kabel holder"
  Base = -> Cut061239
  Edges = 4 edges r=1: [Edge4,Edge9,Edge16,Edge17]
  Placement = pos=(-28,-21.5,-49.5) rot=(0,0,-1;1.5708rad)
FEATURE [Part::FeaturePython] Nut035  label="M4-Nut"  # Fasteners workbench fastener (typed FeaturePython)
  Placement = pos=(26,-22,0) rot=(0,0,1;0rad)
  diameter = 6
  invert = false
  matchOuter = false
  offset = 0
  thread = false
  type = 1
FEATURE [Part::Box] Box119  label="Krychle109"
  AttacherType = Attacher::AttachEngine3D
  Height = 20
  Length = 60
  Placement = pos=(-30,-49,-59) rot=(0,0,1;0rad)
  Width = 52
FEATURE [Part::FeaturePython] Nut036  label="M6-Nut011"  # Fasteners workbench fastener (typed FeaturePython)
  Placement = pos=(0,-56,-53) rot=(0,0,1;0rad)
  diameter = 8
  invert = false
  matchOuter = false
  offset = 0
  thread = false
  type = 1
FEATURE [Sketcher::SketchObject] Sketch041
  MapMode = 5
  Placement = pos=(0,0,60) rot=(0,0,1;0rad)
  sketch-geometry (6):
    g0: LineSegment StartX=-18.9734 StartY=34.0308 StartZ=0 EndX=-16.0253 EndY=36.9748 EndZ=0
    g1: LineSegment StartX=18.996 StartY=34.0308 StartZ=0 EndX=16.044 EndY=36.9748 EndZ=0
    g2: LineSegment StartX=18.996 StartY=34.0308 StartZ=0 EndX=-18.9734 EndY=34.0308 EndZ=0
    g3: LineSegment StartX=-18.9734 StartY=40.0311 StartZ=0 EndX=-16.0253 EndY=36.9748 EndZ=0
    g4: LineSegment StartX=16.044 StartY=36.9748 StartZ=0 EndX=18.9109 EndY=40.0311 EndZ=0
    g5: LineSegment StartX=-18.9734 StartY=40.0311 StartZ=0 EndX=18.9109 EndY=40.0311 EndZ=0
  constraints (7):
    c: Coincident(g2,g1)
    c: Coincident(g2,g0)
    c: Horizontal(g2)
    c: Coincident(g3,g0)
    c: Coincident(g5,g3)
    c: Coincident(g5,g4)
    c: Horizontal(g5)
FEATURE [Part::Box] Box120  label="deska010"
  AttacherType = Attacher::AttachEngine3D
  Height = 111
  Length = 43
  Placement = pos=(-21.5,21.5,-51.5) rot=(0,0,1;0rad)
  Width = 10
FEATURE [Part::Cylinder] Cylinder014005660  label="Válec580"
  Angle = 360
  AttacherType = Attacher::AttachEngine3D
  Height = 50
  Placement = pos=(15.5,15.5,0) rot=(0,0,1;0rad)
  Radius = 1.6
FEATURE [Part::Cylinder] Cylinder014005661  label="DIRA8,004"
  Angle = 360
  AttacherType = Attacher::AttachEngine3D
  Height = 200
  Placement = pos=(0,29,-100) rot=(0,0,1;0rad)
  Radius = 4.2
FEATURE [Part::Cylinder] Cylinder014005662  label="Válec581"
  Angle = 360
  AttacherType = Attacher::AttachEngine3D
  Height = 10
  Placement = pos=(0,43,-47) rot=(1,0,0;1.5708rad)
  Radius = 4
FEATURE [Part::Cylinder] Cylinder014005663  label="dira stred005"
  Angle = 360
  AttacherType = Attacher::AttachEngine3D
  Height = 50
  Radius = 13
FEATURE [Part::Cylinder] Cylinder014005664  label="Válec582"
  Angle = 360
  AttacherType = Attacher::AttachEngine3D
  Height = 10
  Placement = pos=(0,43,54.5) rot=(1,0,0;1.5708rad)
  Radius = 4
FEATURE [Part::Box] Box121  label="Krychle110"
  AttacherType = Attacher::AttachEngine3D
  Height = 112
  Length = 38
  Placement = pos=(-19,34,-52) rot=(0,0,1;0rad)
  Width = 6
FEATURE [Sketcher::SketchObject] Sketch042
  MapMode = 45
  Placement = pos=(44.88,21.011,5.40003) rot=(0.707106,0.001666,0.707106;3.13826rad)
  sketch-geometry (7):
    g0: LineSegment StartX=5 StartY=0 StartZ=0 EndX=2.5 EndY=4.33013 EndZ=0
    g1: LineSegment StartX=2.5 StartY=4.33013 StartZ=0 EndX=-2.5 EndY=4.33013 EndZ=0
    g2: LineSegment StartX=-2.5 StartY=4.33013 StartZ=0 EndX=-5 EndY=0 EndZ=0
    g3: LineSegment StartX=-5 StartY=0 StartZ=0 EndX=-2.5 EndY=-4.33013 EndZ=0
    g4: LineSegment StartX=-2.5 StartY=-4.33013 StartZ=0 EndX=2.5 EndY=-4.33013 EndZ=0
    g5: LineSegment StartX=2.5 StartY=-4.33013 StartZ=0 EndX=5 EndY=0 EndZ=0
    g6: Circle [constr] CenterX=0 CenterY=0 CenterZ=0 NormalX=0 NormalY=0 NormalZ=1 AngleXU=0 Radius=5
  constraints (14):
    c: Coincident(g0,g1)
    c: Coincident(g1,g2)
    c: Coincident(g2,g3)
    c: Coincident(g3,g4)
    c: Coincident(g4,g5)
    c: Coincident(g5,g0)
    c: Equal(g0, g1-g5) x5
    c: PointOnObject(g0,g6)
    c: PointOnObject(g1,g6)
    c: PointOnObject(g2,g6)
    c: PointOnObject(g3,g6)
    c: PointOnObject(g4,g6)
    c: PointOnObject(g5,g6)
    c: PointOnObject(g6,g-1)
FEATURE [Part::RegularPolygon] RegularPolygon010  label="Pravidelný n-úhelník010"
  AttacherType = Attacher::AttachEngine3D
  Circumradius = 6
  Polygon = 6
FEATURE [Part::RegularPolygon] RegularPolygon011  label="Pravidelný n-úhelník011"
  AttacherType = Attacher::AttachEngine3D
  Circumradius = 6
  Polygon = 6
FEATURE [Part::Extrusion] Extrude075
  Base = -> RegularPolygon010
  Dir = (0,0,1)
  DirMode = 2
  FaceMakerClass = Part::FaceMakerBullseye
  LengthFwd = 8
  LengthRev = 0
  Placement = pos=(0,0,13) rot=(0,0,1;0rad)
  Solid = true
  Symmetric = false
FEATURE [Part::Extrusion] Extrude079
  Base = -> Sketch042
  Dir = (1,0,0)
  DirMode = 2
  FaceMakerClass = Part::FaceMakerBullseye
  LengthFwd = 5
  LengthRev = 0
  Placement = pos=(0,0,0.25) rot=(0,0,1;0rad)
  Solid = true
  Symmetric = false
FEATURE [Part::Extrusion] Extrude081
  Base = -> RegularPolygon011
  Dir = (0,0,1)
  DirMode = 2
  FaceMakerClass = Part::FaceMakerBullseye
  LengthFwd = 8
  LengthRev = 0
  Placement = pos=(0,0,13) rot=(0,0,1;0rad)
  Solid = true
  Symmetric = false
FEATURE [Part::RegularPolygon] RegularPolygon012  label="Pravidelný n-úhelník012"
  AttacherType = Attacher::AttachEngine3D
  Circumradius = 6
  Polygon = 6
FEATURE [Part::Extrusion] Extrude082
  Base = -> Sketch041
  Dir = (0,0,1)
  DirMode = 2
  FaceMakerClass = Part::FaceMakerBullseye
  LengthFwd = -112
  LengthRev = 0
  Solid = true
  Symmetric = false
FEATURE [Part::Extrusion] Extrude084
  Base = -> RegularPolygon012
  Dir = (0,0,1)
  DirMode = 2
  FaceMakerClass = Part::FaceMakerBullseye
  LengthFwd = 8
  LengthRev = 0
  Placement = pos=(0,0,13) rot=(0,0,1;0rad)
  Solid = true
  Symmetric = false
FEATURE [Part::Chamfer] Chamfer019
  Base = -> Box119
  Edges = 4 edges r=10: [Edge1,Edge3,Edge5,Edge7]
FEATURE [Part::FeaturePython] InvoluteGear033 .. InvoluteGear036  x4 (patterned run collapsed; names and placements below)
  backlash = 0
  beta = 0
  clearance = 0.25
  double_helix = false
  head = 0
  height = 5.5
  module = 1.2
  numpoints = 6
  pressure_angle = 20
  reversed_backlash = false
  shift = 0
  simple = false
  teeth = 27
  undercut = false
FEATURE [Part::FeaturePython] Nut037  label="M4-Nut016"  # Fasteners workbench fastener (typed FeaturePython)
  Placement = pos=(22,17,69) rot=(0,1,0;1.5708rad)
  diameter = 6
  invert = false
  matchOuter = false
  offset = 0
  thread = false
  type = 1
FEATURE [Part::FeaturePython] InvoluteGear037  # WARN: FeaturePython — macro-defined, semantics opaque (R4)
  Placement = pos=(0,0,-72) rot=(0,0,1;0rad)
  backlash = 0
  beta = 20
  clearance = 0.25
  double_helix = true
  head = 0
  height = 8
  module = 1.16
  numpoints = 6
  pressure_angle = 20
  reversed_backlash = false
  shift = 0
  simple = false
  teeth = 27
  undercut = false
FEATURE [Part::FeaturePython] InvoluteGear038  # WARN: FeaturePython — macro-defined, semantics opaque (R4)
  Placement = pos=(0,0,-71.9) rot=(0,0,1;0rad)
  backlash = 0
  beta = -20
  clearance = 0.25
  double_helix = true
  head = 0
  height = 8.2
  module = 1.16
  numpoints = 6
  pressure_angle = 20
  reversed_backlash = false
  shift = 0
  simple = false
  teeth = 20
  undercut = false
FEATURE [Part::FeaturePython] Screw018  label="M8x160-Screw005"  # Fasteners workbench fastener (typed FeaturePython)
  Placement = pos=(0,0,68.4) rot=(0,0,1;0rad)
  diameter = 9
  invert = false
  length = 16
  matchOuter = false
  offset = 0
  thread = false
  type = 13
FEATURE [Part::FeaturePython] Nut038  label="M8-Nut008"  # Fasteners workbench fastener (typed FeaturePython)
  Placement = pos=(0,0,-90) rot=(0,0,1;0rad)
  diameter = 9
  invert = false
  matchOuter = false
  offset = 0
  thread = false
  type = 1
FEATURE [Part::FeaturePython] Nut039  label="M4-Nut017"  # Fasteners workbench fastener (typed FeaturePython)
  Placement = pos=(22,-17,69) rot=(0,1,0;1.5708rad)
  diameter = 6
  invert = false
  matchOuter = false
  offset = 0
  thread = false
  type = 1
FEATURE [Part::FeaturePython] Nut040  label="M6-Nut001"  # Fasteners workbench fastener (typed FeaturePython)
  Placement = pos=(0,-56,-106) rot=(0,0,1;0rad)
  diameter = 8
  invert = false
  matchOuter = false
  offset = 0
  thread = false
  type = 1
FEATURE [Part::FeaturePython] Nut041  label="M5-Nut"  # Fasteners workbench fastener (typed FeaturePython)
  Placement = pos=(0,-29,-80) rot=(0,0,1;0rad)
  diameter = 7
  invert = false
  matchOuter = false
  offset = 0
  thread = false
  type = 1
FEATURE [Part::FeaturePython] Screw019  label="M8x160-Screw006"  # Fasteners workbench fastener (typed FeaturePython)
  Placement = pos=(0,0,68.4) rot=(0,0,1;0rad)
  diameter = 9
  invert = false
  length = 16
  matchOuter = false
  offset = 0
  thread = false
  type = 13
FEATURE [Part::FeaturePython] InvoluteGear039  # WARN: FeaturePython — macro-defined, semantics opaque (R4)
  backlash = 0
  beta = 0
  clearance = 0.25
  double_helix = false
  head = 0
  height = 5.5
  module = 1.2
  numpoints = 6
  pressure_angle = 20
  reversed_backlash = false
  shift = 0
  simple = false
  teeth = 27
  undercut = false
FEATURE [Part::Box] Box122  label="Krychle111"
  AttacherType = Attacher::AttachEngine3D
  Height = 112
  Length = 38
  Placement = pos=(-19,32,-52) rot=(0,0,1;0rad)
  Width = 10
FEATURE [Part::Cut] Cut061267
  Base = -> Box122
  Tool = -> Box121
FEATURE [Part::MultiFuse] Fusion423  label="Arca plate base013"
  Placement = pos=(0,-0.5,0) rot=(0,0,1;0rad)
  Shapes = -> [Extrude082,Cut061267]
FEATURE [Part::Cylinder] Cylinder014005665  label="Válec583"
  Angle = 360
  AttacherType = Attacher::AttachEngine3D
  Height = 65
  Placement = pos=(-32,0,-27) rot=(0,1,0;1.5708rad)
  Radius = 1.35
FEATURE [Part::Box] Box123  label="Krychle112"
  AttacherType = Attacher::AttachEngine3D
  Height = 2
  Length = 80
  Placement = pos=(-40,-30,-53) rot=(0,0,1;0rad)
  Width = 80
FEATURE [Part::Cylinder] Cylinder014005666  label="Válec584"
  Angle = 360
  AttacherType = Attacher::AttachEngine3D
  Height = 50
  Placement = pos=(-15.5,-15.5,0) rot=(0,0,1;0rad)
  Radius = 1.6
FEATURE [Part::Cylinder] Cylinder014005667  label="Válec585"
  Angle = 360
  AttacherType = Attacher::AttachEngine3D
  Height = 50
  Placement = pos=(-15.5,15.5,0) rot=(0,0,1;0rad)
  Radius = 1.6
FEATURE [Part::Cylinder] Cylinder014005668  label="Válec586"
  Angle = 360
  AttacherType = Attacher::AttachEngine3D
  Height = 50
  Placement = pos=(15.5,-15.5,0) rot=(0,0,1;0rad)
  Radius = 1.6
FEATURE [Part::MultiFuse] Fusion450  label="diry012"
  Shapes = -> [Cylinder014005667,Cylinder014005660,Cylinder014005663,Cylinder014005666,Cylinder014005668]
FEATURE [Part::Cylinder] Cylinder014005669  label="Válec587"
  Angle = 360
  AttacherType = Attacher::AttachEngine3D
  Height = 65
  Placement = pos=(-32,0,0) rot=(0,1,0;1.5708rad)
  Radius = 1.35
FEATURE [Part::Box] Box124  label="deska011"
  AttacherType = Attacher::AttachEngine3D
  Height = 111
  Length = 9
  Placement = pos=(21.5,-14.5,-51.5) rot=(0,0,1;0rad)
  Width = 46
FEATURE [Part::Box] Box125  label="Krychle113"
  AttacherType = Attacher::AttachEngine3D
  Height = 2
  Length = 80
  Placement = pos=(-40,-30,59) rot=(0,0,1;0rad)
  Width = 80
FEATURE [Part::MultiFuse] Fusion449  label="Orez002"
  Shapes = -> [Box125,Box123]
FEATURE [Part::Cylinder] Cylinder014005670  label="Lozisko009"
  Angle = 360
  AttacherType = Attacher::AttachEngine3D
  Height = 4
  Placement = pos=(0,29,-52.1) rot=(0,0,1;0rad)
  Radius = 7
FEATURE [Part::Box] Box126  label="Krychle114"
  AttacherType = Attacher::AttachEngine3D
  Height = 10
  Length = 43
  Placement = pos=(-21.5,-20.5,0) rot=(0,0,1;0rad)
  Width = 42
FEATURE [Part::Chamfer] Chamfer016
  Base = -> Box126
  Edges = 2 edges r=5: [Edge1,Edge5]
FEATURE [Part::Cut] Cut061256  label="Horni ucjyt003"
  Base = -> Chamfer016
  Placement = pos=(0,0,49.5) rot=(0,0,1;0rad)
  Tool = -> Fusion450
FEATURE [Part::Box] Box127  label="deska012"
  AttacherType = Attacher::AttachEngine3D
  Height = 111
  Length = 9
  Placement = pos=(-30.5,-14.5,-51.5) rot=(0,0,1;0rad)
  Width = 46
FEATURE [Part::MultiFuse] Fusion448  label="motor drazak003"
  Shapes = -> [Cut061256,Box124,Box120,Box127]
FEATURE [Part::MultiFuse] Fusion418  label="drzak s arca003"
  Shapes = -> [Fusion448,Fusion423,Cylinder014005664,Cylinder014005662]
FEATURE [Part::Cylinder] Cylinder014005671  label="Válec588"
  Angle = 360
  AttacherType = Attacher::AttachEngine3D
  Height = 65
  Placement = pos=(-32,0,42) rot=(0,1,0;1.5708rad)
  Radius = 1.35
FEATURE [Part::Cylinder] Cylinder014005672  label="Válec589"
  Angle = 360
  AttacherType = Attacher::AttachEngine3D
  Height = 18
  Radius = 2.6
FEATURE [Part::Cylinder] Cylinder014005673  label="Válec590"
  Angle = 360
  AttacherType = Attacher::AttachEngine3D
  Height = 65
  Placement = pos=(-32,15,-27) rot=(0,1,0;1.5708rad)
  Radius = 1.35
FEATURE [Part::Cylinder] Cylinder014005674  label="unasec spodek039"
  Angle = 360
  AttacherType = Attacher::AttachEngine3D
  Height = 1.5
  Placement = pos=(0,0,-1.5) rot=(0,0,1;0rad)
  Radius = 15.5
FEATURE [Part::Cylinder] Cylinder014005675  label="Válec591"
  Angle = 360
  AttacherType = Attacher::AttachEngine3D
  Height = 1.5
  Radius = 16
FEATURE [Part::Cylinder] Cylinder014005676  label="Válec592"
  Angle = 360
  AttacherType = Attacher::AttachEngine3D
  Height = 10
  Placement = pos=(10.5,0,0) rot=(0,0,1;0rad)
  Radius = 8
FEATURE [Part::Cylinder] Cylinder014005677  label="Válec593"
  Angle = 360
  AttacherType = Attacher::AttachEngine3D
  Height = 1.5
  Radius = 20
FEATURE [Part::Cylinder] Cylinder014005678  label="Válec594"
  Angle = 360
  AttacherType = Attacher::AttachEngine3D
  Height = 10
  Placement = pos=(0,0,-3) rot=(0,0,1;0rad)
  Radius = 7
FEATURE [Part::Cylinder] Cylinder014005679  label="Válec595"
  Angle = 360
  AttacherType = Attacher::AttachEngine3D
  Height = 4
  Placement = pos=(0,0,7) rot=(0,0,1;0rad)
  Radius = 6.5
FEATURE [Part::Cylinder] Cylinder014005680  label="unasec stred017"
  Angle = 360
  AttacherType = Attacher::AttachEngine3D
  Height = 7
  Placement = pos=(0,0,-1.5) rot=(0,0,1;0rad)
  Radius = 13.5
FEATURE [Part::Cylinder] Cylinder014005681  label="Válec596"
  Angle = 360
  AttacherType = Attacher::AttachEngine3D
  Height = 10
  Placement = pos=(0,0,-3) rot=(0,0,1;0rad)
  Radius = 7
FEATURE [Part::Cylinder] Cylinder014005682  label="Lozisko010"
  Angle = 360
  AttacherType = Attacher::AttachEngine3D
  Height = 4
  Placement = pos=(0,29,56) rot=(0,0,1;0rad)
  Radius = 7
FEATURE [Part::MultiFuse] Fusion451  label="DIRA OSA002"
  Shapes = -> [Cylinder014005661,Cylinder014005670,Cylinder014005682]
FEATURE [Part::Cylinder] Cylinder014005683  label="Válec597"
  Angle = 360
  AttacherType = Attacher::AttachEngine3D
  Height = 1.5
  Radius = 16
FEATURE [Part::Cut] Cut061289  label="Ring043"
  Base = -> Cylinder014005677
  Placement = pos=(0,0,-1.5) rot=(0,0,1;0rad)
  Tool = -> Cylinder014005683
FEATURE [Part::Cylinder] Cylinder014005684  label="Válec598"
  Angle = 360
  AttacherType = Attacher::AttachEngine3D
  Height = 65
  Placement = pos=(-32,15,42) rot=(0,1,0;1.5708rad)
  Radius = 1.35
FEATURE [Part::MultiFuse] Fusion416  label="diry 2,008"
  Shapes = -> [Cylinder014005684,Cylinder014005669,Cylinder014005671,Cylinder014005665,Cylinder014005673]
FEATURE [Part::MultiFuse] Fusion417  label="Diry orez002"
  Shapes = -> [Fusion416,Fusion451,Fusion449]
FEATURE [Part::Cut] Cut061262  label="Blok A002"
  Base = -> Fusion418
  Tool = -> Fusion417
FEATURE [Part::Chamfer] Chamfer017  label="Axis 004"
  Base = -> Cut061262
  Edges = 4 edges r=8: [Edge132,Edge133,Edge152,Edge153]
  Placement = pos=(0,-29,0) rot=(0,1,0;3.14159rad)
FEATURE [Part::Cylinder] Cylinder014005685  label="Válec599"
  Angle = 360
  AttacherType = Attacher::AttachEngine3D
  Height = 7.5
  Placement = pos=(0,0,-7) rot=(0,0,1;0rad)
  Radius = 6.5
FEATURE [Part::Cylinder] Cylinder014005686  label="Válec600"
  Angle = 360
  AttacherType = Attacher::AttachEngine3D
  Height = 15
  Placement = pos=(0,0,-8) rot=(0,0,1;0rad)
  Radius = 2.65
FEATURE [Part::Cylinder] Cylinder014005687  label="Válec601"
  Angle = 360
  AttacherType = Attacher::AttachEngine3D
  Height = 4
  Placement = pos=(0,0,7) rot=(0,0,1;0rad)
  Radius = 6.5
FEATURE [Part::Cylinder] Cylinder014005688  label="Válec602"
  Angle = 360
  AttacherType = Attacher::AttachEngine3D
  Height = 1.5
  Radius = 16
FEATURE [Part::Cylinder] Cylinder014005689  label="Unasec vrch028"
  Angle = 360
  AttacherType = Attacher::AttachEngine3D
  Height = 1.5
  Placement = pos=(0,0,5.5) rot=(0,0,1;0rad)
  Radius = 15.5
FEATURE [Part::Cylinder] Cylinder014005690  label="unasec spodek040"
  Angle = 360
  AttacherType = Attacher::AttachEngine3D
  Height = 1.5
  Placement = pos=(0,0,-1.5) rot=(0,0,1;0rad)
  Radius = 15.5
FEATURE [Part::MultiFuse] Fusion426
  Shapes = -> [Cylinder014005680,Cylinder014005690]
FEATURE [Part::Cylinder] Cylinder014005691  label="Válec603"
  Angle = 360
  AttacherType = Attacher::AttachEngine3D
  Height = 1.5
  Radius = 16
FEATURE [Part::Cylinder] Cylinder014005692  label="Unasec vrch029"
  Angle = 360
  AttacherType = Attacher::AttachEngine3D
  Height = 1.5
  Placement = pos=(0,0,5.5) rot=(0,0,1;0rad)
  Radius = 15.5
FEATURE [Part::Cylinder] Cylinder014005693  label="Válec604"
  Angle = 360
  AttacherType = Attacher::AttachEngine3D
  Height = 1.5
  Radius = 20
FEATURE [Part::Cut] Cut061246  label="Ring035"
  Base = -> Cylinder014005693
  Placement = pos=(0,0,5.5) rot=(0,0,1;0rad)
  Tool = -> Cylinder014005691
FEATURE [Part::Cylinder] Cylinder014005694  label="Válec605"
  Angle = 360
  AttacherType = Attacher::AttachEngine3D
  Height = 5.5
  Radius = 20
FEATURE [Part::Cut] Cut061250  label="ring 017"
  Base = -> Cylinder014005694
  Tool = -> InvoluteGear036
FEATURE [Part::Cylinder] Cylinder014005695  label="Válec606"
  Angle = 360
  AttacherType = Attacher::AttachEngine3D
  Height = 1.5
  Radius = 20
FEATURE [Part::Cut] Cut061275  label="Ring039"
  Base = -> Cylinder014005695
  Placement = pos=(0,0,-1.5) rot=(0,0,1;0rad)
  Tool = -> Cylinder014005688
FEATURE [Part::Cylinder] Cylinder014005696  label="Válec607"
  Angle = 360
  AttacherType = Attacher::AttachEngine3D
  Height = 5.5
  Radius = 20
FEATURE [Part::Cut] Cut061261  label="ring 019"
  Base = -> Cylinder014005696
  Tool = -> InvoluteGear039
FEATURE [Part::MultiFuse] Fusion408  label="Ring zaklad Fin016"
  Shapes = -> [Cut061261,Cut061246,Cut061275]
FEATURE [Part::Cylinder] Cylinder014005697  label="Válec608"
  Angle = 360
  AttacherType = Attacher::AttachEngine3D
  Height = 7
  Radius = 2.6
FEATURE [Part::Cylinder] Cylinder014005698  label="Válec609"
  Angle = 360
  AttacherType = Attacher::AttachEngine3D
  Height = 10
  Placement = pos=(0,0,-3) rot=(0,0,1;0rad)
  Radius = 7
FEATURE [Part::Cylinder] Cylinder014005699  label="Válec610"
  Angle = 360
  AttacherType = Attacher::AttachEngine3D
  Height = 10
  Placement = pos=(10.5,0,0) rot=(0,0,1;0rad)
  Radius = 8
FEATURE [Part::Cylinder] Cylinder014005700  label="Válec611"
  Angle = 360
  AttacherType = Attacher::AttachEngine3D
  Height = 7
  Placement = pos=(0,0,-7) rot=(0,0,1;0rad)
  Radius = 12
FEATURE [Part::Cylinder] Cylinder014005701  label="Válec612"
  Angle = 360
  AttacherType = Attacher::AttachEngine3D
  Height = 10
  Placement = pos=(10.5,0,0) rot=(0,0,1;0rad)
  Radius = 8
FEATURE [Part::Cylinder] Cylinder014005702  label="unasec stred018"
  Angle = 360
  AttacherType = Attacher::AttachEngine3D
  Height = 7
  Placement = pos=(0,0,-1.5) rot=(0,0,1;0rad)
  Radius = 13.5
FEATURE [Part::MultiFuse] Fusion420
  Shapes = -> [Cylinder014005702,Cylinder014005674]
FEATURE [Part::Cylinder] Cylinder014005703  label="Válec613"
  Angle = 360
  AttacherType = Attacher::AttachEngine3D
  Height = 7
  Radius = 2.6
FEATURE [Part::Cylinder] Cylinder014005704  label="Válec614"
  Angle = 360
  AttacherType = Attacher::AttachEngine3D
  Height = 1.5
  Radius = 20
FEATURE [Part::Cut] Cut061245  label="Ring034"
  Base = -> Cylinder014005704
  Placement = pos=(0,0,5.5) rot=(0,0,1;0rad)
  Tool = -> Cylinder014005675
FEATURE [Part::Cylinder] Cylinder014005705  label="Válec615"
  Angle = 360
  AttacherType = Attacher::AttachEngine3D
  Height = 7
  Radius = 2.6
FEATURE [Part::Cylinder] Cylinder014005706  label="Unasec vrch030"
  Angle = 360
  AttacherType = Attacher::AttachEngine3D
  Height = 1.5
  Placement = pos=(0,0,5.5) rot=(0,0,1;0rad)
  Radius = 15.5
FEATURE [Part::Cylinder] Cylinder014005707  label="unasec stred019"
  Angle = 360
  AttacherType = Attacher::AttachEngine3D
  Height = 7
  Placement = pos=(0,0,-1.5) rot=(0,0,1;0rad)
  Radius = 13.5
FEATURE [Part::Cylinder] Cylinder014005708  label="Válec616"
  Angle = 360
  AttacherType = Attacher::AttachEngine3D
  Height = 1.5
  Radius = 20
FEATURE [Part::Cylinder] Cylinder014005709  label="Válec617"
  Angle = 360
  AttacherType = Attacher::AttachEngine3D
  Height = 1.5
  Radius = 16
FEATURE [Part::Cylinder] Cylinder014005710  label="Válec618"
  Angle = 360
  AttacherType = Attacher::AttachEngine3D
  Height = 1.5
  Radius = 16
FEATURE [Part::Feature] Screw_solid135  label="M2x4-Screw (Solid)135"
  Placement = pos=(0,0,0) rot=(0,0,1;3.14159rad)
  shape: bbox 3.6 x 3.6 x 4 mm, 12 faces (baked)
FEATURE [Part::Feature] Screw_solid136  label="M2x4-Screw (Solid)136"
  Placement = pos=(0,0,0) rot=(0,0,1;1.0472rad)
  shape: bbox 3.6 x 3.6 x 4 mm, 12 faces (baked)
FEATURE [Part::Feature] Cut007_solid023  label="Sun024"
  shape: bbox 12.9 x 13.1 x 5 mm, 57 faces (baked)
FEATURE [Part::MultiFuse] Fusion406
  Shapes = -> [Cut007_solid023,Cylinder014005685,Cylinder014005700]
FEATURE [Part::Feature] Cylinder014005711  label="Válec619"
  Placement = pos=(0,0,0) rot=(0,0,1;2.0944rad)
  shape: bbox 5 x 5 x 7 mm, 3 faces (baked)
FEATURE [Part::Feature] Screw_solid137  label="M2x4-Screw (Solid)137"
  Placement = pos=(0,0,0) rot=(0,0,-1;1.0472rad)
  shape: bbox 3.6 x 3.6 x 4 mm, 12 faces (baked)
FEATURE [Part::Feature] Screw_solid138  label="M2x4-Screw (Solid)138"
  Placement = pos=(0,0,0) rot=(0,0,-1;1.0472rad)
  shape: bbox 3.6 x 3.6 x 4 mm, 12 faces (baked)
FEATURE [Part::Feature] Cylinder014005712  label="Válec620"
  shape: bbox 5 x 5 x 7 mm, 3 faces (baked)
FEATURE [Part::Feature] Screw_solid139  label="M2x4-Screw (Solid)139"
  Placement = pos=(0,0,0) rot=(0,0,1;3.14159rad)
  shape: bbox 3.6 x 3.6 x 4 mm, 12 faces (baked)
FEATURE [Part::Feature] Cylinder014005713  label="Válec621"
  shape: bbox 5 x 5 x 7 mm, 3 faces (baked)
FEATURE [Part::Feature] Cut007_solid024  label="Sun025"
  Placement = pos=(0,0,10.5) rot=(0,0,1;0rad)
  shape: bbox 12.9 x 13.1 x 5 mm, 57 faces (baked)
FEATURE [Part::Feature] Cylinder014005714  label="Válec622"
  Placement = pos=(0,0,0) rot=(0,0,1;2.0944rad)
  shape: bbox 5 x 5 x 7 mm, 3 faces (baked)
FEATURE [Part::Feature] Screw_solid140  label="M2x4-Screw (Solid)140"
  Placement = pos=(0,0,0) rot=(0,0,1;3.14159rad)
  shape: bbox 3.6 x 3.6 x 4 mm, 12 faces (baked)
FEATURE [Part::Feature] Cylinder014005715  label="Válec623"
  Placement = pos=(0,0,0) rot=(0,0,1;4.18879rad)
  shape: bbox 5 x 5 x 7 mm, 3 faces (baked)
FEATURE [Part::Feature] Cut008_solid048  label="Planet049"
  Placement = pos=(0,0,0) rot=(0,0,1;2.0944rad)
  shape: bbox 12.9 x 13.1 x 5 mm, 57 faces (baked)
FEATURE [Part::Feature] Screw_solid141  label="M2x4-Screw (Solid)141"
  Placement = pos=(0,0,0) rot=(0,0,-1;1.0472rad)
  shape: bbox 3.6 x 3.6 x 4 mm, 12 faces (baked)
FEATURE [Part::Feature] Cut061307  label="SUN I Final007"
  shape: bbox 24 x 24 x 12.25 mm, 99 faces (baked)
FEATURE [Part::Feature] Cylinder014005716  label="Válec624"
  Placement = pos=(0,0,0) rot=(0,0,1;4.18879rad)
  shape: bbox 16 x 16 x 10 mm, 3 faces (baked)
FEATURE [Part::Feature] Cut008_solid049  label="Planet050"
  Placement = pos=(0,0,0) rot=(0,0,1;4.18879rad)
  shape: bbox 12.9 x 13.1 x 5 mm, 57 faces (baked)
FEATURE [Part::Feature] Screw_solid142  label="M2x4-Screw (Solid)142"
  Placement = pos=(0,0,0) rot=(0,0,1;3.14159rad)
  shape: bbox 3.6 x 3.6 x 4 mm, 12 faces (baked)
FEATURE [Part::Feature] Cylinder014005717  label="Válec625"
  shape: bbox 5 x 5 x 7 mm, 3 faces (baked)
FEATURE [Part::Feature] Cylinder014005718  label="Válec626"
  Placement = pos=(0,0,0) rot=(0,0,1;2.0944rad)
  shape: bbox 5 x 5 x 7 mm, 3 faces (baked)
FEATURE [Part::MultiFuse] Fusion400
  Shapes = -> [Cylinder014005715,Cylinder014005712,Cylinder014005718]
FEATURE [Part::Feature] Cut005_solid001_cs017
  Placement = pos=(0,0,-11.25) rot=(0,0,1;0rad)
  shape: bbox 41 x 41 x 3e-07 mm, 0 faces, 0 solids (baked)
FEATURE [Part::Extrusion] Extrude072  label="box017"
  Base = -> Cut005_solid001_cs017
  Dir = (0,0,1)
  DirMode = 2
  FaceMakerClass = Part::FaceMakerBullseye
  LengthFwd = 19
  LengthRev = 0
  Placement = pos=(0,0,-11.5) rot=(0,0,1;0rad)
  Solid = true
  Symmetric = false
FEATURE [Part::MultiFuse] Fusion411  label="Tělo I003"
  Shapes = -> [Extrude072,Fusion408]
FEATURE [Part::Feature] Cut007_solid025  label="Sun026"
  Placement = pos=(0,0,10.5) rot=(0,0,1;0rad)
  shape: bbox 12.9 x 13.1 x 5 mm, 57 faces (baked)
FEATURE [Part::Feature] Cylinder014005719  label="Válec627"
  Placement = pos=(0,0,0) rot=(0,0,1;4.18879rad)
  shape: bbox 16 x 16 x 10 mm, 3 faces (baked)
FEATURE [Part::Feature] Cylinder014005720  label="Válec628"
  Placement = pos=(0,0,0) rot=(0,0,1;2.0944rad)
  shape: bbox 5 x 5 x 7 mm, 3 faces (baked)
FEATURE [Part::Feature] Screw_solid143  label="M2x4-Screw (Solid)143"
  Placement = pos=(0,0,0) rot=(0,0,-1;1.0472rad)
  shape: bbox 3.6 x 3.6 x 4 mm, 12 faces (baked)
FEATURE [Part::Feature] Cut007_solid026  label="Sun027"
  Placement = pos=(0,0,10.5) rot=(0,0,1;0rad)
  shape: bbox 12.9 x 13.1 x 5 mm, 57 faces (baked)
FEATURE [Part::Feature] Cylinder014005721  label="Válec629"
  shape: bbox 5 x 5 x 7 mm, 3 faces (baked)
FEATURE [Part::Feature] Cylinder014005722  label="Válec630"
  Placement = pos=(0,0,0) rot=(0,0,1;4.18879rad)
  shape: bbox 16 x 16 x 10 mm, 3 faces (baked)
FEATURE [Part::Feature] Cylinder014005723  label="Válec631"
  Placement = pos=(0,0,0) rot=(0,0,1;2.0944rad)
  shape: bbox 16 x 16 x 10 mm, 3 faces (baked)
FEATURE [Part::MultiFuse] Fusion447
  Shapes = -> [Cylinder014005678,Cylinder014005676,Cylinder014005719,Cylinder014005723]
FEATURE [Part::Cut] Cut061266  label="unasec spodek035"
  Base = -> Fusion426
  Tool = -> Fusion447
FEATURE [Part::Feature] Cut007_solid027  label="Sun028"
  Placement = pos=(0,0,10.5) rot=(0,0,1;0rad)
  shape: bbox 12.9 x 13.1 x 5 mm, 57 faces (baked)
FEATURE [Part::Feature] Cut005_solid001_cs018
  Placement = pos=(0,0,-11.25) rot=(0,0,1;0rad)
  shape: bbox 41 x 41 x 3e-07 mm, 0 faces, 0 solids (baked)
FEATURE [Part::Extrusion] Extrude077  label="box020"
  Base = -> Cut005_solid001_cs018
  Dir = (0,0,1)
  DirMode = 2
  FaceMakerClass = Part::FaceMakerBullseye
  LengthFwd = 10.5
  LengthRev = 0
  Placement = pos=(0,0,-3) rot=(0,0,1;0rad)
  Solid = true
  Symmetric = false
FEATURE [Part::Feature] Cylinder014005724  label="Válec632"
  shape: bbox 5 x 5 x 7 mm, 3 faces (baked)
FEATURE [Part::Feature] Cut008_solid050  label="Planet051"
  Placement = pos=(0,0,0) rot=(0,0,1;2.0944rad)
  shape: bbox 12.9 x 13.1 x 5 mm, 57 faces (baked)
FEATURE [Part::Feature] Screw_solid144  label="M2x4-Screw (Solid)144"
  Placement = pos=(0,0,0) rot=(0,0,1;1.0472rad)
  shape: bbox 3.6 x 3.6 x 4 mm, 12 faces (baked)
FEATURE [Part::MultiFuse] Fusion409  label="srouby046"
  Shapes = -> [Screw_solid144,Screw_solid137,Screw_solid135]
FEATURE [Part::Cut] Cut061273  label="Uasec spodek019"
  Base = -> Cut061266
  Tool = -> Fusion409
FEATURE [Part::MultiFuse] Fusion457  label="Unasec spdek final018"
  Shapes = -> [Cut061273,Fusion400]
FEATURE [Part::Feature] Screw_solid145  label="M2x4-Screw (Solid)145"
  Placement = pos=(0,0,0) rot=(0,0,1;3.14159rad)
  shape: bbox 3.6 x 3.6 x 4 mm, 12 faces (baked)
FEATURE [Part::Feature] Cylinder014005725  label="Válec633"
  Placement = pos=(0,0,0) rot=(0,0,1;2.0944rad)
  shape: bbox 16 x 16 x 10 mm, 3 faces (baked)
FEATURE [Part::MultiFuse] Fusion445
  Shapes = -> [Cylinder014005681,Cylinder014005701,Cylinder014005722,Cylinder014005725]
FEATURE [Part::Cut] Cut061248  label="unasec spodek034"
  Base = -> Fusion420
  Tool = -> Fusion445
FEATURE [Part::Feature] Cut008_solid051  label="Planet052"
  Placement = pos=(0,0,0) rot=(0,0,1;4.18879rad)
  shape: bbox 12.9 x 13.1 x 5 mm, 57 faces (baked)
FEATURE [Part::Feature] Cylinder014005726  label="Válec634"
  Placement = pos=(0,0,0) rot=(0,0,1;2.0944rad)
  shape: bbox 16 x 16 x 10 mm, 3 faces (baked)
FEATURE [Part::MultiFuse] Fusion432
  Shapes = -> [Cylinder014005698,Cylinder014005699,Cylinder014005716,Cylinder014005726]
FEATURE [Part::Feature] Screw_solid146  label="M2x4-Screw (Solid)146"
  Placement = pos=(0,0,0) rot=(0,0,-1;1.0472rad)
  shape: bbox 3.6 x 3.6 x 4 mm, 12 faces (baked)
FEATURE [Part::MultiFuse] Fusion444  label="srouby052"
  Placement = pos=(0,0,0.5) rot=(0,0,1;0rad)
  Shapes = -> [Screw_solid136,Screw_solid146,Screw_solid142]
FEATURE [Part::Cut] Cut061264  label="unasec vrch032"
  Base = -> Cylinder014005692
  Tool = -> Fusion444
FEATURE [Part::Feature] Screw_solid147  label="M2x4-Screw (Solid)147"
  Placement = pos=(0,0,0) rot=(0,0,-1;1.0472rad)
  shape: bbox 3.6 x 3.6 x 4 mm, 12 faces (baked)
FEATURE [Part::Feature] Screw_solid148  label="M2x4-Screw (Solid)148"
  Placement = pos=(0,0,0) rot=(0,0,1;1.0472rad)
  shape: bbox 3.6 x 3.6 x 4 mm, 12 faces (baked)
FEATURE [Part::MultiFuse] Fusion464  label="srouby054"
  Shapes = -> [Screw_solid148,Screw_solid138,Screw_solid140]
FEATURE [Part::Cut] Cut061277  label="Uasec spodek020"
  Base = -> Cut061248
  Tool = -> Fusion464
FEATURE [Part::Feature] Screw_solid149  label="M2x4-Screw (Solid)149"
  Placement = pos=(0,0,0) rot=(0,0,1;1.0472rad)
  shape: bbox 3.6 x 3.6 x 4 mm, 12 faces (baked)
FEATURE [Part::Feature] Cut007_solid028  label="Sun029"
  Placement = pos=(0,0,10.5) rot=(0,0,1;0rad)
  shape: bbox 12.9 x 13.1 x 5 mm, 57 faces (baked)
FEATURE [Part::Feature] Cylinder014005727  label="Válec635"
  Placement = pos=(0,0,0) rot=(0,0,1;4.18879rad)
  shape: bbox 5 x 5 x 7 mm, 3 faces (baked)
FEATURE [Part::MultiFuse] Fusion431
  Shapes = -> [Cylinder014005727,Cylinder014005717,Cylinder014005711]
FEATURE [Part::MultiFuse] Fusion407
  Placement = pos=(0,0,1) rot=(0,0,1;0rad)
  Shapes = -> [Fusion431,Cylinder014005703]
FEATURE [Part::Cut] Cut061244  label="Unasec Vrch zaklad029"
  Base = -> Cut061264
  Tool = -> Fusion407
FEATURE [Part::Feature] Cut008_solid052  label="Planet053"
  Placement = pos=(0,0,0) rot=(0,0,1;4.18879rad)
  shape: bbox 12.9 x 13.1 x 5 mm, 57 faces (baked)
FEATURE [Part::Feature] Cut008_solid053  label="Planet054"
  shape: bbox 12.9 x 13.1 x 5 mm, 57 faces (baked)
FEATURE [Part::Feature] Cut008_solid054  label="Planet055"
  Placement = pos=(0,0,0) rot=(0,0,1;4.18879rad)
  shape: bbox 12.9 x 13.1 x 5 mm, 57 faces (baked)
FEATURE [Sketcher::SketchObject] Sketch044
  MapMode = 5
  Placement = pos=(0,0,60) rot=(0,0,1;0rad)
  sketch-geometry (6):
    g0: LineSegment StartX=-18.9734 StartY=34.0308 StartZ=0 EndX=-16.0253 EndY=36.9748 EndZ=0
    g1: LineSegment StartX=18.996 StartY=34.0308 StartZ=0 EndX=16.044 EndY=36.9748 EndZ=0
    g2: LineSegment StartX=18.996 StartY=34.0308 StartZ=0 EndX=-18.9734 EndY=34.0308 EndZ=0
    g3: LineSegment StartX=-18.9734 StartY=40.0311 StartZ=0 EndX=-16.0253 EndY=36.9748 EndZ=0
    g4: LineSegment StartX=16.044 StartY=36.9748 StartZ=0 EndX=18.9109 EndY=40.0311 EndZ=0
    g5: LineSegment StartX=-18.9734 StartY=40.0311 StartZ=0 EndX=18.9109 EndY=40.0311 EndZ=0
  constraints (7):
    c: Coincident(g2,g1)
    c: Coincident(g2,g0)
    c: Horizontal(g2)
    c: Coincident(g3,g0)
    c: Coincident(g5,g3)
    c: Coincident(g5,g4)
    c: Horizontal(g5)
FEATURE [Part::Extrusion] Extrude076
  Base = -> Sketch044
  Dir = (0,0,1)
  DirMode = 2
  FaceMakerClass = Part::FaceMakerBullseye
  LengthFwd = -112
  LengthRev = 0
  Solid = true
  Symmetric = false
FEATURE [Sketcher::SketchObject] Sketch045
  MapMode = 45
  Placement = pos=(44.88,21.011,5.40003) rot=(0.707106,0.001666,0.707106;3.13826rad)
  sketch-geometry (7):
    g0: LineSegment StartX=5.21891 StartY=0.0364138 StartZ=0 EndX=2.62121 EndY=4.46293 EndZ=0
    g1: LineSegment StartX=2.62121 StartY=4.46293 StartZ=0 EndX=-2.51111 EndY=4.42651 EndZ=0
    g2: LineSegment StartX=-2.51111 StartY=4.42651 StartZ=0 EndX=-5.04574 EndY=-0.0364138 EndZ=0
    g3: LineSegment StartX=-5.04574 StartY=-0.0364138 StartZ=0 EndX=-2.44804 EndY=-4.46293 EndZ=0
    g4: LineSegment StartX=-2.44804 StartY=-4.46293 StartZ=0 EndX=2.68428 EndY=-4.42651 EndZ=0
    g5: LineSegment StartX=2.68428 StartY=-4.42651 StartZ=0 EndX=5.21891 EndY=0.0364138 EndZ=0
    g6: Circle [constr] CenterX=0.0865834 CenterY=0 CenterZ=0 NormalX=0 NormalY=0 NormalZ=1 AngleXU=0 Radius=5.13245
  constraints (14):
    c: Coincident(g0,g1)
    c: Coincident(g1,g2)
    c: Coincident(g2,g3)
    c: Coincident(g3,g4)
    c: Coincident(g4,g5)
    c: Coincident(g5,g0)
    c: Equal(g0, g1-g5) x5
    c: PointOnObject(g0,g6)
    c: PointOnObject(g1,g6)
    c: PointOnObject(g2,g6)
    c: PointOnObject(g3,g6)
    c: PointOnObject(g4,g6)
    c: PointOnObject(g5,g6)
    c: PointOnObject(g6,g-1)
FEATURE [Part::Extrusion] Extrude078
  Base = -> Sketch045
  Dir = (1,0,0)
  DirMode = 2
  FaceMakerClass = Part::FaceMakerBullseye
  LengthFwd = 5
  LengthRev = 0
  Placement = pos=(0,0,0.25) rot=(0,0,1;0rad)
  Solid = true
  Symmetric = false
FEATURE [Sketcher::SketchObject] Sketch046
  MapMode = 45
  Placement = pos=(44.88,21.011,5.40003) rot=(0.707106,0.001666,0.707106;3.13826rad)
  sketch-geometry (7):
    g0: LineSegment StartX=5.21891 StartY=0.0364138 StartZ=0 EndX=2.62121 EndY=4.46293 EndZ=0
    g1: LineSegment StartX=2.62121 StartY=4.46293 StartZ=0 EndX=-2.51111 EndY=4.42651 EndZ=0
    g2: LineSegment StartX=-2.51111 StartY=4.42651 StartZ=0 EndX=-5.04574 EndY=-0.0364138 EndZ=0
    g3: LineSegment StartX=-5.04574 StartY=-0.0364138 StartZ=0 EndX=-2.44804 EndY=-4.46293 EndZ=0
    g4: LineSegment StartX=-2.44804 StartY=-4.46293 StartZ=0 EndX=2.68428 EndY=-4.42651 EndZ=0
    g5: LineSegment StartX=2.68428 StartY=-4.42651 StartZ=0 EndX=5.21891 EndY=0.0364138 EndZ=0
    g6: Circle [constr] CenterX=0.0865834 CenterY=0 CenterZ=0 NormalX=0 NormalY=0 NormalZ=1 AngleXU=0 Radius=5.13245
  constraints (14):
    c: Coincident(g0,g1)
    c: Coincident(g1,g2)
    c: Coincident(g2,g3)
    c: Coincident(g3,g4)
    c: Coincident(g4,g5)
    c: Coincident(g5,g0)
    c: Equal(g0, g1-g5) x5
    c: PointOnObject(g0,g6)
    c: PointOnObject(g1,g6)
    c: PointOnObject(g2,g6)
    c: PointOnObject(g3,g6)
    c: PointOnObject(g4,g6)
    c: PointOnObject(g5,g6)
    c: PointOnObject(g6,g-1)
FEATURE [Part::Extrusion] Extrude080
  Base = -> Sketch046
  Dir = (1,0,0)
  DirMode = 2
  FaceMakerClass = Part::FaceMakerBullseye
  LengthFwd = 5
  LengthRev = 0
  Placement = pos=(0,0,0.25) rot=(0,0,1;0rad)
  Solid = true
  Symmetric = false
FEATURE [Sketcher::SketchObject] Sketch047
  MapMode = 5
  Placement = pos=(26,-22,0) rot=(1,0,0;3.14159rad)
  Support = -> [Nut035]
  sketch-geometry (7):
    g0: LineSegment StartX=2 StartY=3.50262 StartZ=0 EndX=-2.03336 EndY=3.48336 EndZ=0
    g1: LineSegment StartX=-2.03336 StartY=3.48336 StartZ=0 EndX=-4.03336 EndY=-0.0192577 EndZ=0
    g2: LineSegment StartX=-4.03336 StartY=-0.0192577 StartZ=0 EndX=-2 EndY=-3.50262 EndZ=0
    g3: LineSegment StartX=-2 StartY=-3.50262 StartZ=0 EndX=2.03336 EndY=-3.48336 EndZ=0
    g4: LineSegment StartX=2.03336 StartY=-3.48336 StartZ=0 EndX=4.03336 EndY=0.0192577 EndZ=0
    g5: LineSegment StartX=4.03336 StartY=0.0192577 StartZ=0 EndX=2 EndY=3.50262 EndZ=0
    g6: Circle [constr] CenterX=0 CenterY=0 CenterZ=0 NormalX=0 NormalY=0 NormalZ=1 AngleXU=0 Radius=4.0334
  constraints (14):
    c: Coincident(g0,g1)
    c: Coincident(g1,g2)
    c: Coincident(g2,g3)
    c: Coincident(g3,g4)
    c: Coincident(g4,g5)
    c: Coincident(g5,g0)
    c: Equal(g0, g1-g5) x5
    c: PointOnObject(g0,g6)
    c: PointOnObject(g1,g6)
    c: PointOnObject(g2,g6)
    c: PointOnObject(g3,g6)
    c: PointOnObject(g4,g6)
    c: PointOnObject(g5,g6)
    c: Coincident(g6,g-1)
FEATURE [Part::Extrusion] Extrude069
  Base = -> Sketch047
  Dir = (0,0,-1)
  DirMode = 2
  FaceMakerClass = Part::FaceMakerBullseye
  LengthFwd = -3.5
  LengthRev = 0
  Solid = true
  Symmetric = false
FEATURE [Part::MultiFuse] Fusion491  label="unasec vrhch 022"
  Shapes = -> [Cut061244,Cut007_solid024,Cylinder014005687]
FEATURE [Part::Cut] Cut061280  label="Unasec + Sun014"
  Base = -> Fusion491
  Tool = -> Cylinder014005672
FEATURE [App::Part] Part060  label="Part079"
  Group = -> [Cut008_solid053,Cut008_solid050,Cut008_solid049,Cylinder014005690,Cylinder014005678,Cylinder014005676,Fusion447,Fusion426,Cylinder014005715,Cylinder014005718,Cylinder014005719,Cylinder014005723,Cylinder014005712,Cylinder014005680,Cut061266,Cut061273,Screw_solid135,Screw_solid144,Screw_solid137,Fusion400,Fusion409,Fusion457,Cylinder014005687,Cylinder014005672,Cut007_solid024,Cut061264,Cut061244,+32 more]
  License = CC BY 3.0
  LicenseURL = http://creativecommons.org/licenses/by/3.0/
  Origin = -> Origin060
FEATURE [Part::MultiFuse] Fusion494  label="Ring zaklad Fin020"
  Shapes = -> [Cut061250,Cut061245,Cut061289]
FEATURE [Part::MultiFuse] Fusion401  label="teloII013"
  Shapes = -> [Fusion494,Extrude077]
FEATURE [Part::Cylinder] Cylinder014005728  label="unasec spodek041"
  Angle = 360
  AttacherType = Attacher::AttachEngine3D
  Height = 1.5
  Placement = pos=(0,0,-1.5) rot=(0,0,1;0rad)
  Radius = 15.5
FEATURE [Part::MultiFuse] Fusion463
  Shapes = -> [Cylinder014005707,Cylinder014005728]
FEATURE [Part::Cut] Cut061271  label="unasec spodek037"
  Base = -> Fusion463
  Tool = -> Fusion432
FEATURE [Part::Cylinder] Cylinder014005729  label="Unasec vrch031"
  Angle = 360
  AttacherType = Attacher::AttachEngine3D
  Height = 1.5
  Placement = pos=(0,0,5.5) rot=(0,0,1;0rad)
  Radius = 15.5
FEATURE [Part::Cylinder] Cylinder014005730  label="Válec636"
  Angle = 360
  AttacherType = Attacher::AttachEngine3D
  Height = 18
  Radius = 2.6
FEATURE [Part::Cylinder] Cylinder014005731  label="Válec637"
  Angle = 360
  AttacherType = Attacher::AttachEngine3D
  Height = 1.5
  Radius = 20
FEATURE [Part::Cut] Cut061252  label="Ring037"
  Base = -> Cylinder014005731
  Placement = pos=(0,0,-1.5) rot=(0,0,1;0rad)
  Tool = -> Cylinder014005710
FEATURE [Part::Cylinder] Cylinder014005732  label="Válec638"
  Angle = 360
  AttacherType = Attacher::AttachEngine3D
  Height = 10
  Placement = pos=(0,0,-3) rot=(0,0,1;0rad)
  Radius = 7
FEATURE [Part::Cylinder] Cylinder014005733  label="Válec639"
  Angle = 360
  AttacherType = Attacher::AttachEngine3D
  Height = 5.5
  Radius = 20
FEATURE [Part::Cut] Cut061284  label="ring 021"
  Base = -> Cylinder014005733
  Tool = -> InvoluteGear035
FEATURE [Part::Cylinder] Cylinder014005734  label="Válec640"
  Angle = 360
  AttacherType = Attacher::AttachEngine3D
  Height = 18
  Radius = 2.6
FEATURE [Part::Cylinder] Cylinder014005735  label="Válec641"
  Angle = 360
  AttacherType = Attacher::AttachEngine3D
  Height = 1.5
  Radius = 20
FEATURE [Part::Cut] Cut061283  label="Ring041"
  Base = -> Cylinder014005735
  Placement = pos=(0,0,5.5) rot=(0,0,1;0rad)
  Tool = -> Cylinder014005709
FEATURE [Part::Cylinder] Cylinder014005736  label="Válec642"
  Angle = 360
  AttacherType = Attacher::AttachEngine3D
  Height = 4
  Placement = pos=(0,0,7) rot=(0,0,1;0rad)
  Radius = 6.5
FEATURE [Part::Cylinder] Cylinder014005737  label="Válec643"
  Angle = 360
  AttacherType = Attacher::AttachEngine3D
  Height = 5.5
  Radius = 20
FEATURE [Part::Cut] Cut061272  label="ring 020"
  Base = -> Cylinder014005737
  Tool = -> InvoluteGear033
FEATURE [Part::Cylinder] Cylinder014005738  label="Válec644"
  Angle = 360
  AttacherType = Attacher::AttachEngine3D
  Height = 1.5
  Radius = 16
FEATURE [Part::Cylinder] Cylinder014005739  label="Válec645"
  Angle = 360
  AttacherType = Attacher::AttachEngine3D
  Height = 10
  Placement = pos=(10.5,0,0) rot=(0,0,1;0rad)
  Radius = 8
FEATURE [Part::Cylinder] Cylinder014005740  label="Válec646"
  Angle = 360
  AttacherType = Attacher::AttachEngine3D
  Height = 1.5
  Radius = 20
FEATURE [Part::Cut] Cut061247  label="Ring036"
  Base = -> Cylinder014005740
  Placement = pos=(0,0,-1.5) rot=(0,0,1;0rad)
  Tool = -> Cylinder014005738
FEATURE [Part::MultiFuse] Fusion472  label="Ring zaklad Fin018"
  Shapes = -> [Cut061272,Cut061283,Cut061247]
FEATURE [Part::Cylinder] Cylinder014005741  label="Válec647"
  Angle = 360
  AttacherType = Attacher::AttachEngine3D
  Height = 1.5
  Radius = 20
FEATURE [Part::Cylinder] Cylinder014005742  label="Válec648"
  Angle = 360
  AttacherType = Attacher::AttachEngine3D
  Height = 1.5
  Radius = 16
FEATURE [Part::Cut] Cut061276  label="Ring040"
  Base = -> Cylinder014005741
  Placement = pos=(0,0,5.5) rot=(0,0,1;0rad)
  Tool = -> Cylinder014005742
FEATURE [Part::Cylinder] Cylinder014005743  label="Válec649"
  Angle = 360
  AttacherType = Attacher::AttachEngine3D
  Height = 4
  Placement = pos=(0,0,7) rot=(0,0,1;0rad)
  Radius = 6.5
FEATURE [Part::Cylinder] Cylinder014005744  label="unasec stred020"
  Angle = 360
  AttacherType = Attacher::AttachEngine3D
  Height = 7
  Placement = pos=(0,0,-1.5) rot=(0,0,1;0rad)
  Radius = 13.5
FEATURE [Part::Cylinder] Cylinder014005745  label="Unasec vrch032"
  Angle = 360
  AttacherType = Attacher::AttachEngine3D
  Height = 1.5
  Placement = pos=(0,0,5.5) rot=(0,0,1;0rad)
  Radius = 15.5
FEATURE [Part::Cylinder] Cylinder014005746  label="Válec650"
  Angle = 360
  AttacherType = Attacher::AttachEngine3D
  Height = 1.5
  Radius = 20
FEATURE [Part::Cylinder] Cylinder014005747  label="Válec651"
  Angle = 360
  AttacherType = Attacher::AttachEngine3D
  Height = 18
  Radius = 2.6
FEATURE [Part::Cylinder] Cylinder014005748  label="Válec652"
  Angle = 360
  AttacherType = Attacher::AttachEngine3D
  Height = 6
  Placement = pos=(0,0,7) rot=(0,0,1;0rad)
  Radius = 6.5
FEATURE [Part::Cylinder] Cylinder014005749  label="Válec653"
  Angle = 360
  AttacherType = Attacher::AttachEngine3D
  Height = 1.5
  Radius = 16
FEATURE [Part::Cut] Cut061287  label="Ring042"
  Base = -> Cylinder014005708
  Placement = pos=(0,0,5.5) rot=(0,0,1;0rad)
  Tool = -> Cylinder014005749
FEATURE [Part::Cylinder] Cylinder014005750  label="unasec spodek042"
  Angle = 360
  AttacherType = Attacher::AttachEngine3D
  Height = 1.5
  Placement = pos=(0,0,-1.5) rot=(0,0,1;0rad)
  Radius = 15.5
FEATURE [Part::MultiFuse] Fusion414
  Shapes = -> [Cylinder014005744,Cylinder014005750]
FEATURE [Part::Cylinder] Cylinder014005751  label="Válec654"
  Angle = 360
  AttacherType = Attacher::AttachEngine3D
  Height = 4
  Placement = pos=(0,0,7) rot=(0,0,1;0rad)
  Radius = 6.5
FEATURE [Part::Box] Box128  label="Krychle115"
  AttacherType = Attacher::AttachEngine3D
  Height = 15
  Length = 50
  Placement = pos=(-25,-25,64) rot=(0,0,1;0rad)
  Width = 50
FEATURE [Part::Cylinder] Cylinder014005752  label="Válec655"
  Angle = 360
  AttacherType = Attacher::AttachEngine3D
  Height = 7
  Radius = 2.6
FEATURE [Part::Cylinder] Cylinder014005753  label="Válec656"
  Angle = 360
  AttacherType = Attacher::AttachEngine3D
  Height = 5.5
  Radius = 20
FEATURE [Part::Cut] Cut061251  label="ring 018"
  Base = -> Cylinder014005753
  Tool = -> InvoluteGear034
FEATURE [Part::MultiFuse] Fusion489  label="Ring zaklad Fin019"
  Shapes = -> [Cut061251,Cut061287,Cut061252]
FEATURE [Part::Cylinder] Cylinder014005754  label="Válec657"
  Angle = 360
  AttacherType = Attacher::AttachEngine3D
  Height = 6
  Placement = pos=(0,0,7) rot=(0,0,1;0rad)
  Radius = 6.5
FEATURE [Part::Cylinder] Cylinder014005755  label="Válec658"
  Angle = 360
  AttacherType = Attacher::AttachEngine3D
  Height = 10
  Placement = pos=(0,0,-3) rot=(0,0,1;0rad)
  Radius = 7
FEATURE [Part::Cylinder] Cylinder014005756  label="Válec659"
  Angle = 360
  AttacherType = Attacher::AttachEngine3D
  Height = 6
  Placement = pos=(0,0,7) rot=(0,0,1;0rad)
  Radius = 6.5
FEATURE [Part::Cylinder] Cylinder014005757  label="Válec660"
  Angle = 360
  AttacherType = Attacher::AttachEngine3D
  Height = 60
  Placement = pos=(-30,17,69) rot=(0,1,0;1.5708rad)
  Radius = 2.1
FEATURE [Part::Box] Box129  label="Krychle116"
  AttacherType = Attacher::AttachEngine3D
  Height = 15
  Length = 2
  Placement = pos=(-15.5,-26,61) rot=(0,0,1;0rad)
  Width = 52
FEATURE [Part::Cylinder] Cylinder014005758  label="Válec661"
  Angle = 360
  AttacherType = Attacher::AttachEngine3D
  Height = 2.5
  Placement = pos=(0,-12,71) rot=(0,0,1;0rad)
  Radius = 6
FEATURE [Part::Cylinder] Cylinder014005759  label="Válec662"
  Angle = 360
  AttacherType = Attacher::AttachEngine3D
  Height = 7
  Radius = 2.6
FEATURE [Part::Box] Box130  label="Krychle117"
  AttacherType = Attacher::AttachEngine3D
  Height = 2.5
  Length = 12
  Placement = pos=(-6,-25,71) rot=(0,0,1;0rad)
  Width = 13
FEATURE [Part::MultiFuse] Fusion396
  Placement = pos=(0,-4,1) rot=(0,0,1;0rad)
  Shapes = -> [Box130,Cylinder014005758]
FEATURE [Part::Cylinder] Cylinder014005760  label="Válec663"
  Angle = 360
  AttacherType = Attacher::AttachEngine3D
  Height = 55
  Placement = pos=(0,0,35) rot=(0,0,1;0rad)
  Radius = 2.7
FEATURE [Part::Cylinder] Cylinder014005761  label="Válec664"
  Angle = 360
  AttacherType = Attacher::AttachEngine3D
  Height = 8
  Placement = pos=(0,0,66) rot=(0,0,1;0rad)
  Radius = 4.5
FEATURE [Part::Cylinder] Cylinder014005762  label="Válec665"
  Angle = 360
  AttacherType = Attacher::AttachEngine3D
  Height = 2.5
  Placement = pos=(0,-12,71) rot=(0,0,1;0rad)
  Radius = 6
FEATURE [Part::Cylinder] Cylinder014005763  label="Válec666"
  Angle = 360
  AttacherType = Attacher::AttachEngine3D
  Height = 60
  Placement = pos=(-30,-17,69) rot=(0,1,0;1.5708rad)
  Radius = 2.1
FEATURE [Part::MultiFuse] Fusion470
  Shapes = -> [Cylinder014005757,Cylinder014005763,Nut037,Nut039]
FEATURE [Part::Cylinder] Cylinder014005764  label="Válec667"
  Angle = 360
  AttacherType = Attacher::AttachEngine3D
  Height = 7
  Radius = 2.6
FEATURE [Part::Cylinder] Cylinder014005765  label="Válec668"
  Angle = 360
  AttacherType = Attacher::AttachEngine3D
  Height = 10
  Placement = pos=(0,0,55) rot=(0,0,1;0rad)
  Radius = 12.5
FEATURE [Part::Cylinder] Cylinder014005766  label="Válec669"
  Angle = 360
  AttacherType = Attacher::AttachEngine3D
  Height = 22
  Radius = 2.6
FEATURE [Part::MultiFuse] Fusion466
  Shapes = -> [Cylinder014005766,Extrude080]
FEATURE [Part::Box] Box131  label="Krychle118"
  AttacherType = Attacher::AttachEngine3D
  Height = 2.5
  Length = 12
  Placement = pos=(-6,-25,71) rot=(0,0,1;0rad)
  Width = 13
FEATURE [Part::MultiFuse] Fusion397
  Placement = pos=(0,4,1) rot=(0,0,1;3.14159rad)
  Shapes = -> [Box131,Cylinder014005762]
FEATURE [Part::MultiFuse] Fusion402
  Shapes = -> [Fusion396,Fusion397]
FEATURE [Part::Cylinder] Cylinder014005767  label="Unasec vrch033"
  Angle = 360
  AttacherType = Attacher::AttachEngine3D
  Height = 1.5
  Placement = pos=(0,0,5.5) rot=(0,0,1;0rad)
  Radius = 15.5
FEATURE [Part::Cylinder] Cylinder014005768  label="Válec670"
  Angle = 360
  AttacherType = Attacher::AttachEngine3D
  Height = 7
  Radius = 2.6
FEATURE [Part::Cylinder] Cylinder014005769  label="Válec671"
  Angle = 360
  AttacherType = Attacher::AttachEngine3D
  Height = 50
  Placement = pos=(15.5,-15.5,0) rot=(0,0,1;0rad)
  Radius = 1.6
FEATURE [Part::Cylinder] Cylinder014005770  label="Válec672"
  Angle = 360
  AttacherType = Attacher::AttachEngine3D
  Height = 55
  Placement = pos=(0,0,-82) rot=(0,0,1;0rad)
  Radius = 2.7
FEATURE [Part::Cylinder] Cylinder014005771  label="  vale"
  Angle = 360
  AttacherType = Attacher::AttachEngine3D
  Height = 15
  Radius = 5.6
FEATURE [Part::Cylinder] Cylinder014005772  label="Válec673"
  Angle = 360
  AttacherType = Attacher::AttachEngine3D
  Height = 15
  Placement = pos=(0,0,55) rot=(0,0,1;0rad)
  Radius = 11
FEATURE [Part::Cylinder] Cylinder014005773  label="Válec674"
  Angle = 360
  AttacherType = Attacher::AttachEngine3D
  Height = 12.5
  Placement = pos=(0,0,-68) rot=(0,0,1;0rad)
  Radius = 12.5
FEATURE [Part::MultiFuse] Fusion482
  Shapes = -> [Cylinder014005771,Cylinder014005773,InvoluteGear038]
FEATURE [Part::Cylinder] Cylinder014005774  label="Válec675"
  Angle = 360
  AttacherType = Attacher::AttachEngine3D
  Height = 15
  Placement = pos=(0,0,52) rot=(0,0,1;0rad)
  Radius = 5.5
FEATURE [Part::Cylinder] Cylinder014005775  label="Válec676"
  Angle = 360
  AttacherType = Attacher::AttachEngine3D
  Height = 18
  Radius = 2.6
FEATURE [Part::Cylinder] Cylinder014005776  label="Lozisko011"
  Angle = 360
  AttacherType = Attacher::AttachEngine3D
  Height = 4
  Placement = pos=(0,0,48) rot=(0,0,1;0rad)
  Radius = 7
FEATURE [Part::Cylinder] Cylinder014005777  label="Válec677"
  Angle = 360
  AttacherType = Attacher::AttachEngine3D
  Height = 50
  Placement = pos=(-15.5,-15.5,0) rot=(0,0,1;0rad)
  Radius = 1.6
FEATURE [Part::Cylinder] Cylinder014005778  label="Válec678"
  Angle = 360
  AttacherType = Attacher::AttachEngine3D
  Height = 7
  Radius = 2.6
FEATURE [Part::Cylinder] Cylinder014005779  label="Válec679"
  Angle = 360
  AttacherType = Attacher::AttachEngine3D
  Height = 9
  Placement = pos=(0,0,-77) rot=(0,0,1;0rad)
  Radius = 4.5
FEATURE [Part::Cylinder] Cylinder014005780  label="Válec680"
  Angle = 360
  AttacherType = Attacher::AttachEngine3D
  Height = 50
  Placement = pos=(15.5,15.5,0) rot=(0,0,1;0rad)
  Radius = 1.6
FEATURE [Part::Cylinder] Cylinder014005781  label="Válec681"
  Angle = 360
  AttacherType = Attacher::AttachEngine3D
  Height = 1.5
  Radius = 16
FEATURE [Part::Cut] Cut061257  label="Ring038"
  Base = -> Cylinder014005746
  Placement = pos=(0,0,-1.5) rot=(0,0,1;0rad)
  Tool = -> Cylinder014005781
FEATURE [Part::MultiFuse] Fusion410  label="Ring zaklad Fin017"
  Shapes = -> [Cut061284,Cut061276,Cut061257]
FEATURE [Part::Cylinder] Cylinder014005782  label="Unasec vrch034"
  Angle = 360
  AttacherType = Attacher::AttachEngine3D
  Height = 1.5
  Placement = pos=(0,0,5.5) rot=(0,0,1;0rad)
  Radius = 15.5
FEATURE [Part::Cylinder] Cylinder014005783  label="Válec682"
  Angle = 360
  AttacherType = Attacher::AttachEngine3D
  Height = 22
  Radius = 2.6
FEATURE [Part::MultiFuse] Fusion405
  Shapes = -> [Cylinder014005783,Extrude079]
FEATURE [Part::Cylinder] Cylinder014005784  label="Válec683"
  Angle = 360
  AttacherType = Attacher::AttachEngine3D
  Height = 10
  Placement = pos=(10.5,0,0) rot=(0,0,1;0rad)
  Radius = 8
FEATURE [Part::Box] Box132  label="Krychle119"
  AttacherType = Attacher::AttachEngine3D
  Height = 112
  Length = 38
  Placement = pos=(-19,34,-52) rot=(0,0,1;0rad)
  Width = 6
FEATURE [Part::Box] Box133  label="Krychle120"
  AttacherType = Attacher::AttachEngine3D
  Height = 40
  Length = 41
  Placement = pos=(-20.5,-20.5,0) rot=(0,0,1;0rad)
  Width = 41
FEATURE [Part::Chamfer] Chamfer013
  Base = -> Box133
  Edges = 4 edges r=5: [Edge1,Edge3,Edge5,Edge7]
FEATURE [Part::Cylinder] Cylinder014005785  label="Válec684"
  Angle = 360
  AttacherType = Attacher::AttachEngine3D
  Height = 50
  Placement = pos=(-15.5,15.5,0) rot=(0,0,1;0rad)
  Radius = 1.6
FEATURE [Part::MultiFuse] Fusion476  label="diry013"
  Shapes = -> [Cylinder014005785,Cylinder014005780,Cylinder014005777,Cylinder014005769]
FEATURE [Part::Cut] Cut061255
  Base = -> Chamfer013
  Tool = -> Fusion476
FEATURE [App::Part] Part059  label="NEAM17  motor- 40mm003"
  Group = -> [Chamfer013,Fusion476,Box133,Cylinder014005785,Cylinder014005780,Cylinder014005777,Cylinder014005769,Cut061255]
  License = CC BY 3.0
  LicenseURL = http://creativecommons.org/licenses/by/3.0/
  Origin = -> Origin062
  Placement = pos=(0,0,-51.5) rot=(0,0,1;0rad)
FEATURE [Part::Cylinder] Cylinder014005786  label="unasec stred021"
  Angle = 360
  AttacherType = Attacher::AttachEngine3D
  Height = 7
  Placement = pos=(0,0,-1.5) rot=(0,0,1;0rad)
  Radius = 13.5
FEATURE [Part::Cylinder] Cylinder014005787  label="Válec685"
  Angle = 360
  AttacherType = Attacher::AttachEngine3D
  Height = 22
  Radius = 2.6
FEATURE [Part::MultiFuse] Fusion474
  Shapes = -> [Cylinder014005787,Extrude078]
FEATURE [Part::Box] Box134  label="Krychle121"
  AttacherType = Attacher::AttachEngine3D
  Height = 112
  Length = 38
  Placement = pos=(-19,32,-52) rot=(0,0,1;0rad)
  Width = 10
FEATURE [Part::Cut] Cut061296
  Base = -> Box134
  Tool = -> Box132
FEATURE [Part::MultiFuse] Fusion473  label="Arca plate base014"
  Placement = pos=(0,-6.5,115.5) rot=(-1,0,0;1.5708rad)
  Shapes = -> [Extrude076,Cut061296]
FEATURE [Part::Cut] Cut061259  label="Arca sw 009"
  Base = -> Box128
  Tool = -> Fusion473
FEATURE [Part::Cut] Cut061301
  Base = -> Cut061259
  Tool = -> Box129
FEATURE [Part::MultiFuse] Fusion428
  Shapes = -> [Cylinder014005765,Cut061301]
FEATURE [Part::Cylinder] Cylinder014005788  label="Unasec vrch035"
  Angle = 360
  AttacherType = Attacher::AttachEngine3D
  Height = 1.5
  Placement = pos=(0,0,5.5) rot=(0,0,1;0rad)
  Radius = 15.5
FEATURE [Part::Cylinder] Cylinder014005789  label="unasec spodek043"
  Angle = 360
  AttacherType = Attacher::AttachEngine3D
  Height = 1.5
  Placement = pos=(0,0,-1.5) rot=(0,0,1;0rad)
  Radius = 15.5
FEATURE [Part::MultiFuse] Fusion493
  Shapes = -> [Cylinder014005786,Cylinder014005789]
FEATURE [Part::Cylinder] Cylinder014005790  label="Válec686"
  Angle = 360
  AttacherType = Attacher::AttachEngine3D
  Height = 11.5
  Placement = pos=(0,0,-76.1) rot=(0,0,1;0rad)
  Radius = 11
FEATURE [Part::MultiFuse] Fusion488
  Shapes = -> [Cylinder014005790,InvoluteGear037]
FEATURE [Sketcher::SketchObject] Sketch043
  MapMode = 5
  Placement = pos=(0,0,-64.6) rot=(0,0,1;0rad)
  Support = -> [Fusion488]
  sketch-geometry (7):
    g0: LineSegment StartX=-3.8831 StartY=6.55674 StartZ=0 EndX=-7.61986 EndY=-0.0844932 EndZ=0
    g1: LineSegment StartX=-7.61986 StartY=-0.0844932 StartZ=0 EndX=-3.73676 EndY=-6.64124 EndZ=0
    g2: LineSegment StartX=-3.73676 StartY=-6.64124 StartZ=0 EndX=3.8831 EndY=-6.55674 EndZ=0
    g3: LineSegment StartX=3.8831 StartY=-6.55674 StartZ=0 EndX=7.61986 EndY=0.0844932 EndZ=0
    g4: LineSegment StartX=7.61986 StartY=0.0844932 StartZ=0 EndX=3.73676 EndY=6.64124 EndZ=0
    g5: LineSegment StartX=3.73676 StartY=6.64124 StartZ=0 EndX=-3.8831 EndY=6.55674 EndZ=0
    g6: Circle [constr] CenterX=0 CenterY=0 CenterZ=0 NormalX=0 NormalY=0 NormalZ=1 AngleXU=0 Radius=7.62033
  constraints (14):
    c: Coincident(g0,g1)
    c: Coincident(g1,g2)
    c: Coincident(g2,g3)
    c: Coincident(g3,g4)
    c: Coincident(g4,g5)
    c: Coincident(g5,g0)
    c: Equal(g0, g1-g5) x5
    c: PointOnObject(g0,g6)
    c: PointOnObject(g1,g6)
    c: PointOnObject(g2,g6)
    c: PointOnObject(g3,g6)
    c: PointOnObject(g4,g6)
    c: PointOnObject(g5,g6)
    c: Coincident(g6,g-1)
FEATURE [Part::Extrusion] Extrude083
  Base = -> Sketch043
  Dir = (0,0,1)
  DirMode = 2
  FaceMakerClass = Part::FaceMakerBullseye
  LengthFwd = 5
  LengthRev = 0
  Placement = pos=(0,0,-5) rot=(0,0,1;0rad)
  Solid = true
  Symmetric = false
FEATURE [Part::Cylinder] Cylinder014005791  label="Válec687"
  Angle = 360
  AttacherType = Attacher::AttachEngine3D
  Height = 200
  Placement = pos=(0,0,-100) rot=(0,0,1;0rad)
  Radius = 3.9
FEATURE [Part::MultiFuse] Fusion487
  Shapes = -> [Extrude083,Cylinder014005791]
FEATURE [Part::Cylinder] Cylinder014005792  label="Válec688"
  Angle = 360
  AttacherType = Attacher::AttachEngine3D
  Height = 25
  Placement = pos=(0,0,-85) rot=(0,0,1;0rad)
  Radius = 4.2
FEATURE [Part::Cylinder] Cylinder014005793  label="Válec689"
  Angle = 360
  AttacherType = Attacher::AttachEngine3D
  Height = 6
  Placement = pos=(0,0,-68.1) rot=(0,0,1;0rad)
  Radius = 19
FEATURE [Part::Feature] Cylinder014005794  label="Válec690"
  Placement = pos=(0,0,0) rot=(0,0,1;2.0944rad)
  shape: bbox 5 x 5 x 7 mm, 3 faces (baked)
FEATURE [Part::Feature] Screw_solid150  label="M2x4-Screw (Solid)150"
  Placement = pos=(0,0,0) rot=(0,0,-1;1.0472rad)
  shape: bbox 3.6 x 3.6 x 4 mm, 12 faces (baked)
FEATURE [Part::Feature] Cut008_solid055  label="Planet056"
  Placement = pos=(0,0,0) rot=(0,0,1;2.0944rad)
  shape: bbox 12.9 x 13.1 x 5 mm, 57 faces (baked)
FEATURE [Part::Feature] Screw_solid151  label="M2x4-Screw (Solid)151"
  Placement = pos=(0,0,0) rot=(0,0,-1;1.0472rad)
  shape: bbox 3.6 x 3.6 x 4 mm, 12 faces (baked)
FEATURE [Part::Feature] Screw_solid152  label="M2x4-Screw (Solid)152"
  Placement = pos=(0,0,0) rot=(0,0,1;1.0472rad)
  shape: bbox 3.6 x 3.6 x 4 mm, 12 faces (baked)
FEATURE [Part::Feature] Cylinder014005795  label="Válec691"
  Placement = pos=(0,0,0) rot=(0,0,1;4.18879rad)
  shape: bbox 5 x 5 x 7 mm, 3 faces (baked)
FEATURE [Part::Feature] Screw_solid153  label="M2x4-Screw (Solid)153"
  Placement = pos=(0,0,0) rot=(0,0,-1;1.0472rad)
  shape: bbox 3.6 x 3.6 x 4 mm, 12 faces (baked)
FEATURE [Part::Feature] Cut061308  label="Dov holder004"
  Placement = pos=(-0.5,42.5,-33) rot=(0,0,1;1.5708rad)
  shape: bbox 15 x 36 x 40 mm, 20 faces (baked)
FEATURE [Part::Feature] Cylinder014005796  label="Válec692"
  shape: bbox 5 x 5 x 7 mm, 3 faces (baked)
FEATURE [Part::Feature] Screw_solid154  label="M2x4-Screw (Solid)154"
  Placement = pos=(0,0,0) rot=(0,0,-1;1.0472rad)
  shape: bbox 3.6 x 3.6 x 4 mm, 12 faces (baked)
FEATURE [Part::Feature] Cylinder014005797  label="Válec693"
  Placement = pos=(0,0,0) rot=(0,0,1;2.0944rad)
  shape: bbox 5 x 5 x 7 mm, 3 faces (baked)
FEATURE [Part::Feature] Cylinder014005798  label="Válec694"
  Placement = pos=(0,0,0) rot=(0,0,1;2.0944rad)
  shape: bbox 5 x 5 x 7 mm, 3 faces (baked)
FEATURE [Part::Feature] Cut008_solid056  label="Planet057"
  shape: bbox 12.9 x 13.1 x 5 mm, 57 faces (baked)
FEATURE [Part::Feature] Cylinder014005799  label="Válec695"
  shape: bbox 5 x 5 x 7 mm, 3 faces (baked)
FEATURE [Part::Feature] Cylinder014005800  label="Válec696"
  Placement = pos=(0,0,0) rot=(0,0,1;2.0944rad)
  shape: bbox 16 x 16 x 10 mm, 3 faces (baked)
FEATURE [Part::Feature] Cylinder014005801  label="Válec697"
  Placement = pos=(0,0,0) rot=(0,0,1;4.18879rad)
  shape: bbox 5 x 5 x 7 mm, 3 faces (baked)
FEATURE [Part::MultiFuse] Fusion479
  Shapes = -> [Cylinder014005801,Cylinder014005799,Cylinder014005794]
FEATURE [Part::MultiFuse] Fusion484
  Placement = pos=(0,0,1) rot=(0,0,1;0rad)
  Shapes = -> [Fusion479,Cylinder014005764]
FEATURE [Part::Feature] Cylinder014005802  label="Válec698"
  Placement = pos=(0,0,0) rot=(0,0,1;4.18879rad)
  shape: bbox 5 x 5 x 7 mm, 3 faces (baked)
FEATURE [Part::Feature] Cylinder014005803  label="Válec699"
  Placement = pos=(0,0,0) rot=(0,0,1;2.0944rad)
  shape: bbox 5 x 5 x 7 mm, 3 faces (baked)
FEATURE [Part::Feature] Cylinder014005804  label="Válec700"
  Placement = pos=(0,0,0) rot=(0,0,1;4.18879rad)
  shape: bbox 5 x 5 x 7 mm, 3 faces (baked)
FEATURE [Part::MultiFuse] Fusion492
  Shapes = -> [Cylinder014005804,Cylinder014005796,Cylinder014005803]
FEATURE [Part::Feature] Cut007_solid029  label="Sun030"
  shape: bbox 12.9 x 13.1 x 5 mm, 57 faces (baked)
FEATURE [Part::Feature] Cylinder014005805  label="Válec701"
  Placement = pos=(0,0,0) rot=(0,0,1;4.18879rad)
  shape: bbox 5 x 5 x 7 mm, 3 faces (baked)
FEATURE [Part::Feature] Cylinder014005806  label="Válec702"
  Placement = pos=(0,0,0) rot=(0,0,1;4.18879rad)
  shape: bbox 5 x 5 x 7 mm, 3 faces (baked)
FEATURE [Part::Feature] Cut005_solid001_cs019
  Placement = pos=(0,0,-11.25) rot=(0,0,1;0rad)
  shape: bbox 41 x 41 x 3e-07 mm, 0 faces, 0 solids (baked)
FEATURE [Part::Extrusion] Extrude073  label="box018"
  Base = -> Cut005_solid001_cs019
  Dir = (0,0,1)
  DirMode = 2
  FaceMakerClass = Part::FaceMakerBullseye
  LengthFwd = 10.5
  LengthRev = 0
  Placement = pos=(0,0,-3) rot=(0,0,1;0rad)
  Solid = true
  Symmetric = false
FEATURE [Part::MultiFuse] Fusion453  label="teloII014"
  Shapes = -> [Fusion410,Extrude073]
FEATURE [Part::Feature] Cylinder014005807  label="Válec703"
  shape: bbox 5 x 5 x 7 mm, 3 faces (baked)
FEATURE [Part::Feature] Cylinder014005808  label="Válec704"
  Placement = pos=(0,0,0) rot=(0,0,1;2.0944rad)
  shape: bbox 5 x 5 x 7 mm, 3 faces (baked)
FEATURE [Part::Feature] Cut008_solid057  label="Planet058"
  shape: bbox 12.9 x 13.1 x 5 mm, 57 faces (baked)
FEATURE [Part::Feature] Cylinder014005809  label="Válec705"
  shape: bbox 5 x 5 x 7 mm, 3 faces (baked)
FEATURE [Part::MultiFuse] Fusion467
  Shapes = -> [Cylinder014005805,Cylinder014005809,Cylinder014005808]
FEATURE [Part::MultiFuse] Fusion413
  Placement = pos=(0,0,1) rot=(0,0,1;0rad)
  Shapes = -> [Fusion467,Cylinder014005768]
FEATURE [Part::Feature] Screw_solid155  label="M2x4-Screw (Solid)155"
  Placement = pos=(0,0,0) rot=(0,0,1;1.0472rad)
  shape: bbox 3.6 x 3.6 x 4 mm, 12 faces (baked)
FEATURE [Part::Feature] Screw_solid156  label="M2x4-Screw (Solid)156"
  Placement = pos=(0,0,0) rot=(0,0,1;3.14159rad)
  shape: bbox 3.6 x 3.6 x 4 mm, 12 faces (baked)
FEATURE [Part::MultiFuse] Fusion477  label="srouby057"
  Placement = pos=(0,0,0.5) rot=(0,0,1;0rad)
  Shapes = -> [Screw_solid155,Screw_solid151,Screw_solid156]
FEATURE [Part::Cut] Cut061299  label="unasec vrch035"
  Base = -> Cylinder014005788
  Tool = -> Fusion477
FEATURE [Part::Cut] Cut061286  label="Unasec Vrch zaklad034"
  Base = -> Cut061299
  Tool = -> Fusion484
FEATURE [Part::MultiFuse] Fusion490
  Shapes = -> [Cut061286,Cylinder014005754,Extrude075]
FEATURE [Part::Cut] Cut061300  label="unasec top011"
  Base = -> Fusion490
  Placement = pos=(0,0,42) rot=(0,0,1;0rad)
  Tool = -> Fusion474
FEATURE [Part::MultiFuse] Fusion481
  Shapes = -> [Cylinder014005760,Cut061300,Cylinder014005761]
FEATURE [Part::Cut] Cut061288
  Base = -> Fusion428
  Tool = -> Fusion481
FEATURE [Part::Cut] Cut061298
  Base = -> Cut061288
  Tool = -> Fusion470
FEATURE [Part::Cut] Cut061302  label="Swis Arca005"
  Base = -> Cut061298
  Tool = -> Fusion402
FEATURE [Part::MultiFuse] Fusion480
  Shapes = -> [Cylinder014005772,Cylinder014005774,Cut061302]
FEATURE [Part::Cut] Cut061293  label="Swiss Acra V004"
  Base = -> Fusion480
  Tool = -> Screw019
FEATURE [App::Part] Part058  label="Swiss arca A002"
  Group = -> [Extrude078,Extrude076,Extrude075,RegularPolygon010,Nut037,Nut039,Sketch044,Sketch045,Screw019,Fusion397,Fusion402,Fusion396,Fusion473,Fusion479,Fusion490,Fusion428,Fusion474,Fusion470,Fusion481,Fusion484,Fusion477,Cut061286,Cut061259,Cut061288,Cut061298,Cut061300,Cut061299,Cut061301,Cut061296,Screw_solid155,Screw_solid151,Cylinder014005799,Screw_solid156,Cylinder014005801,Cylinder014005794,Box132,+22 more]
  License = CC BY 3.0
  LicenseURL = http://creativecommons.org/licenses/by/3.0/
  Origin = -> Origin056
FEATURE [Part::Feature] Screw_solid157  label="M2x4-Screw (Solid)157"
  Placement = pos=(0,0,0) rot=(0,0,-1;1.0472rad)
  shape: bbox 3.6 x 3.6 x 4 mm, 12 faces (baked)
FEATURE [Part::Feature] Cut008_solid058  label="Planet059"
  Placement = pos=(0,0,0) rot=(0,0,1;4.18879rad)
  shape: bbox 12.9 x 13.1 x 5 mm, 57 faces (baked)
FEATURE [Part::Feature] Cylinder014005810  label="Válec706"
  shape: bbox 5 x 5 x 7 mm, 3 faces (baked)
FEATURE [Part::MultiFuse] Fusion403
  Shapes = -> [Cylinder014005802,Cylinder014005810,Cylinder014005798]
FEATURE [Part::MultiFuse] Fusion398
  Placement = pos=(0,0,1) rot=(0,0,1;0rad)
  Shapes = -> [Fusion403,Cylinder014005759]
FEATURE [Part::Feature] Screw_solid158  label="M2x4-Screw (Solid)158"
  Placement = pos=(0,0,0) rot=(0,0,1;1.0472rad)
  shape: bbox 3.6 x 3.6 x 4 mm, 12 faces (baked)
FEATURE [Part::Feature] Screw_solid159  label="M2x4-Screw (Solid)159"
  Placement = pos=(0,0,0) rot=(0,0,-1;1.0472rad)
  shape: bbox 3.6 x 3.6 x 4 mm, 12 faces (baked)
FEATURE [Part::Feature] Screw_solid160  label="M2x4-Screw (Solid)160"
  Placement = pos=(0,0,0) rot=(0,0,1;3.14159rad)
  shape: bbox 3.6 x 3.6 x 4 mm, 12 faces (baked)
FEATURE [Part::MultiFuse] Fusion443  label="srouby051"
  Placement = pos=(0,0,0.5) rot=(0,0,1;0rad)
  Shapes = -> [Screw_solid158,Screw_solid157,Screw_solid160]
FEATURE [Part::Cut] Cut061295  label="unasec vrch034"
  Base = -> Cylinder014005767
  Tool = -> Fusion443
FEATURE [Part::Cut] Cut061297  label="Unasec Vrch zaklad035"
  Base = -> Cut061295
  Tool = -> Fusion398
FEATURE [Part::MultiFuse] Fusion399
  Shapes = -> [Cut061297,Cylinder014005748,Extrude084]
FEATURE [Part::Cut] Cut061303  label="unasec top012"
  Base = -> Fusion399
  Placement = pos=(0,0,-42) rot=(1,0,0;3.14159rad)
  Tool = -> Fusion466
FEATURE [Part::MultiFuse] Fusion496
  Shapes = -> [Cylinder014005779,Cut061303,Cylinder014005770]
FEATURE [Part::Cut] Cut061290  label="Pinion002"
  Base = -> Fusion482
  Tool = -> Fusion496
FEATURE [App::Part] Part064  label="Pinion20 A002"
  Group = -> [Sketch046,Extrude080,RegularPolygon012,Extrude084,Cut061295,Cut061297,Cut061303,Cylinder014005759,Cylinder014005748,Cylinder014005779,Cylinder014005770,Cylinder014005767,Cylinder014005771,Cylinder014005773,Cylinder014005766,Screw_solid157,Screw_solid160,Cylinder014005802,Cylinder014005810,Screw_solid158,Cylinder014005798,Fusion399,Fusion466,Fusion496,Fusion403,Fusion398,Fusion443,InvoluteGear038,+2 more]
  License = CC BY 3.0
  LicenseURL = http://creativecommons.org/licenses/by/3.0/
  Origin = -> Origin064
  Placement = pos=(0,-29,0) rot=(0,0,1;0.017453rad)
FEATURE [Part::Feature] Cut061309  label="SUN I Final008"
  shape: bbox 24 x 24 x 12.25 mm, 99 faces (baked)
FEATURE [Part::Feature] Screw_solid161  label="M2x4-Screw (Solid)161"
  Placement = pos=(0,0,0) rot=(0,0,-1;1.0472rad)
  shape: bbox 3.6 x 3.6 x 4 mm, 12 faces (baked)
FEATURE [Part::Feature] Screw_solid162  label="M2x4-Screw (Solid)162"
  Placement = pos=(0,0,0) rot=(0,0,1;1.0472rad)
  shape: bbox 3.6 x 3.6 x 4 mm, 12 faces (baked)
FEATURE [Part::MultiFuse] Fusion427  label="srouby049"
  Placement = pos=(0,0,0.5) rot=(0,0,1;0rad)
  Shapes = -> [Screw_solid162,Screw_solid143,Screw_solid139]
FEATURE [Part::Cut] Cut061254  label="unasec vrch029"
  Base = -> Cylinder014005689
  Tool = -> Fusion427
FEATURE [Part::Feature] Screw_solid163  label="M2x4-Screw (Solid)163"
  Placement = pos=(0,0,0) rot=(0,0,1;1.0472rad)
  shape: bbox 3.6 x 3.6 x 4 mm, 12 faces (baked)
FEATURE [Part::Feature] Screw_solid164  label="M2x4-Screw (Solid)164"
  Placement = pos=(0,0,0) rot=(0,0,1;1.0472rad)
  shape: bbox 3.6 x 3.6 x 4 mm, 12 faces (baked)
FEATURE [Part::Feature] Cut005_solid001_cs020
  Placement = pos=(0,0,-11.25) rot=(0,0,1;0rad)
  shape: bbox 41 x 41 x 3e-07 mm, 0 faces, 0 solids (baked)
FEATURE [Part::Extrusion] Extrude074  label="box019"
  Base = -> Cut005_solid001_cs020
  Dir = (0,0,1)
  DirMode = 2
  FaceMakerClass = Part::FaceMakerBullseye
  LengthFwd = 10.5
  LengthRev = 0
  Placement = pos=(0,0,-3) rot=(0,0,1;0rad)
  Solid = true
  Symmetric = false
FEATURE [Part::MultiFuse] Fusion465  label="teloII016"
  Shapes = -> [Fusion489,Extrude074]
FEATURE [Part::Feature] Cut008_solid059  label="Planet060"
  shape: bbox 12.9 x 13.1 x 5 mm, 57 faces (baked)
FEATURE [Part::Feature] Cut008_solid060  label="Planet061"
  Placement = pos=(0,0,0) rot=(0,0,1;2.0944rad)
  shape: bbox 12.9 x 13.1 x 5 mm, 57 faces (baked)
FEATURE [Part::Feature] Cylinder014005811  label="Válec707"
  Placement = pos=(0,0,0) rot=(0,0,1;4.18879rad)
  shape: bbox 5 x 5 x 7 mm, 3 faces (baked)
FEATURE [Part::Feature] Cylinder014005812  label="Válec708"
  Placement = pos=(0,0,0) rot=(0,0,1;2.0944rad)
  shape: bbox 5 x 5 x 7 mm, 3 faces (baked)
FEATURE [Part::Feature] Cylinder014005813  label="Válec709"
  Placement = pos=(0,0,0) rot=(0,0,1;4.18879rad)
  shape: bbox 5 x 5 x 7 mm, 3 faces (baked)
FEATURE [Part::MultiFuse] Fusion461
  Shapes = -> [Cylinder014005813,Cylinder014005713,Cylinder014005714]
FEATURE [Part::Feature] Screw_solid165  label="M2x4-Screw (Solid)165"
  Placement = pos=(0,0,0) rot=(0,0,1;3.14159rad)
  shape: bbox 3.6 x 3.6 x 4 mm, 12 faces (baked)
FEATURE [Part::MultiFuse] Fusion412  label="srouby047"
  Placement = pos=(0,0,0.5) rot=(0,0,1;0rad)
  Shapes = -> [Screw_solid152,Screw_solid154,Screw_solid165]
FEATURE [Part::Cut] Cut061253  label="unasec vrch028"
  Base = -> Cylinder014005782
  Tool = -> Fusion412
FEATURE [Part::Feature] Cylinder014005814  label="Válec710"
  Placement = pos=(0,0,0) rot=(0,0,1;4.18879rad)
  shape: bbox 5 x 5 x 7 mm, 3 faces (baked)
FEATURE [Part::MultiFuse] Fusion483
  Shapes = -> [Cylinder014005814,Cylinder014005807,Cylinder014005812]
FEATURE [Part::Feature] Screw_solid166  label="M2x4-Screw (Solid)166"
  Placement = pos=(0,0,0) rot=(0,0,1;3.14159rad)
  shape: bbox 3.6 x 3.6 x 4 mm, 12 faces (baked)
FEATURE [Part::Feature] Screw_solid167  label="M2x4-Screw (Solid)167"
  Placement = pos=(0,0,0) rot=(0,0,1;3.14159rad)
  shape: bbox 3.6 x 3.6 x 4 mm, 12 faces (baked)
FEATURE [Part::Feature] Screw_solid168  label="M2x4-Screw (Solid)168"
  Placement = pos=(0,0,0) rot=(0,0,1;1.0472rad)
  shape: bbox 3.6 x 3.6 x 4 mm, 12 faces (baked)
FEATURE [Part::MultiFuse] Fusion471  label="srouby056"
  Placement = pos=(0,0,0.5) rot=(0,0,1;0rad)
  Shapes = -> [Screw_solid168,Screw_solid159,Screw_solid145]
FEATURE [Part::Cut] Cut061263  label="unasec vrch031"
  Base = -> Cylinder014005745
  Tool = -> Fusion471
FEATURE [Part::Cut] Cut061249  label="Unasec Vrch zaklad030"
  Base = -> Cut061263
  Tool = -> Fusion413
FEATURE [Part::MultiFuse] Fusion497
  Shapes = -> [Cut061249,Cylinder014005756,Extrude081]
FEATURE [Part::Cut] Cut061281  label="unasec top010"
  Base = -> Fusion497
  Tool = -> Fusion405
FEATURE [Part::Feature] Screw_solid169  label="M2x4-Screw (Solid)169"
  Placement = pos=(0,0,0) rot=(0,0,1;3.14159rad)
  shape: bbox 3.6 x 3.6 x 4 mm, 12 faces (baked)
FEATURE [Part::MultiFuse] Fusion421  label="srouby048"
  Shapes = -> [Screw_solid163,Screw_solid153,Screw_solid169]
FEATURE [Part::Feature] Cylinder014005815  label="Válec711"
  Placement = pos=(0,0,0) rot=(0,0,1;2.0944rad)
  shape: bbox 5 x 5 x 7 mm, 3 faces (baked)
FEATURE [Part::Feature] Screw_solid170  label="M2x4-Screw (Solid)170"
  Placement = pos=(0,0,0) rot=(0,0,1;1.0472rad)
  shape: bbox 3.6 x 3.6 x 4 mm, 12 faces (baked)
FEATURE [Part::MultiFuse] Fusion468  label="srouby055"
  Placement = pos=(0,0,0.5) rot=(0,0,1;0rad)
  Shapes = -> [Screw_solid170,Screw_solid147,Screw_solid166]
FEATURE [Part::Cut] Cut061279  label="unasec vrch033"
  Base = -> Cylinder014005706
  Tool = -> Fusion468
FEATURE [Part::Feature] Cylinder014005816  label="Válec712"
  Placement = pos=(0,0,0) rot=(0,0,1;4.18879rad)
  shape: bbox 16 x 16 x 10 mm, 3 faces (baked)
FEATURE [Part::MultiFuse] Fusion415
  Shapes = -> [Cylinder014005755,Cylinder014005784,Cylinder014005816,Cylinder014005800]
FEATURE [Part::Cut] Cut061268  label="unasec spodek036"
  Base = -> Fusion493
  Tool = -> Fusion415
FEATURE [Part::Feature] Cylinder014005817  label="Válec713"
  Placement = pos=(0,0,0) rot=(0,0,1;4.18879rad)
  shape: bbox 16 x 16 x 10 mm, 3 faces (baked)
FEATURE [Part::Feature] Cylinder014005818  label="Válec714"
  shape: bbox 5 x 5 x 7 mm, 3 faces (baked)
FEATURE [Part::MultiFuse] Fusion404
  Shapes = -> [Cylinder014005806,Cylinder014005818,Cylinder014005797]
FEATURE [Part::MultiFuse] Fusion485
  Placement = pos=(0,0,1) rot=(0,0,1;0rad)
  Shapes = -> [Fusion404,Cylinder014005778]
FEATURE [Part::Cut] Cut061274  label="Unasec Vrch zaklad032"
  Base = -> Cut061253
  Tool = -> Fusion485
FEATURE [Part::MultiFuse] Fusion478  label="unasec vrhch 021"
  Shapes = -> [Cut061274,Cut007_solid027,Cylinder014005751]
FEATURE [Part::Cut] Cut061265  label="Unasec + Sun005 old003"
  Base = -> Fusion478
  Tool = -> Cylinder014005775
FEATURE [Part::Feature] Cylinder014005819  label="Válec715"
  Placement = pos=(0,0,0) rot=(0,0,1;4.18879rad)
  shape: bbox 5 x 5 x 7 mm, 3 faces (baked)
FEATURE [Part::MultiFuse] Fusion433
  Shapes = -> [Cylinder014005819,Cylinder014005721,Cylinder014005720]
FEATURE [Part::MultiFuse] Fusion456  label="Unasec spdek final017"
  Shapes = -> [Cut061277,Fusion433]
FEATURE [Part::Feature] Cylinder014005820  label="Válec716"
  Placement = pos=(0,0,0) rot=(0,0,1;2.0944rad)
  shape: bbox 5 x 5 x 7 mm, 3 faces (baked)
FEATURE [Part::Feature] Cut008_solid061  label="Planet062"
  shape: bbox 12.9 x 13.1 x 5 mm, 57 faces (baked)
FEATURE [Part::Feature] Screw_solid171  label="M2x4-Screw (Solid)171"
  Placement = pos=(0,0,0) rot=(0,0,1;3.14159rad)
  shape: bbox 3.6 x 3.6 x 4 mm, 12 faces (baked)
FEATURE [Part::MultiFuse] Fusion452  label="srouby053"
  Shapes = -> [Screw_solid149,Screw_solid141,Screw_solid171]
FEATURE [Part::Cut] Cut061258  label="Uasec spodek018"
  Base = -> Cut061271
  Tool = -> Fusion452
FEATURE [Part::MultiFuse] Fusion459  label="Unasec spdek final019"
  Shapes = -> [Cut061258,Fusion461]
FEATURE [Part::Feature] Cylinder014005821  label="Válec717"
  Placement = pos=(0,0,0) rot=(0,0,1;2.0944rad)
  shape: bbox 5 x 5 x 7 mm, 3 faces (baked)
FEATURE [Part::MultiFuse] Fusion425
  Shapes = -> [Cylinder014005811,Cylinder014005724,Cylinder014005821]
FEATURE [Part::MultiFuse] Fusion454
  Placement = pos=(0,0,1) rot=(0,0,1;0rad)
  Shapes = -> [Fusion425,Cylinder014005752]
FEATURE [Part::Feature] Cylinder014005822  label="Válec718"
  shape: bbox 5 x 5 x 7 mm, 3 faces (baked)
FEATURE [Part::MultiFuse] Fusion419
  Shapes = -> [Cylinder014005795,Cylinder014005822,Cylinder014005820]
FEATURE [Part::MultiFuse] Fusion460
  Placement = pos=(0,0,1) rot=(0,0,1;0rad)
  Shapes = -> [Fusion419,Cylinder014005705]
FEATURE [Part::Cut] Cut061278  label="Unasec Vrch zaklad033"
  Base = -> Cut061254
  Tool = -> Fusion460
FEATURE [Part::MultiFuse] Fusion424  label="unasec vrhch 018"
  Shapes = -> [Cut061278,Cut007_solid025,Cylinder014005679]
FEATURE [Part::Cut] Cut061269  label="Unasec + Sun013"
  Base = -> Fusion424
  Tool = -> Cylinder014005730
FEATURE [App::Part] Part055  label="Part077"
  Group = -> [Cut061248,Cut061277,Cylinder014005681,Cylinder014005674,Cylinder014005702,Cylinder014005701,Cylinder014005722,Cylinder014005720,Cylinder014005725,Screw_solid140,Cylinder014005721,Screw_solid148,Cylinder014005819,Screw_solid138,Fusion445,Fusion420,Fusion464,Fusion433,Fusion456,Cut008_solid059,Cut008_solid048,Cut008_solid052,Screw_solid162,Cylinder014005822,Cylinder014005820,Screw_solid143,+27 more]
  License = CC BY 3.0
  LicenseURL = http://creativecommons.org/licenses/by/3.0/
  Origin = -> Origin055
  Placement = pos=(0,0,10.5) rot=(0,0,1;0rad)
FEATURE [Part::Feature] Screw_solid172  label="M2x4-Screw (Solid)172"
  Placement = pos=(0,0,0) rot=(0,0,1;3.14159rad)
  shape: bbox 3.6 x 3.6 x 4 mm, 12 faces (baked)
FEATURE [Part::MultiFuse] Fusion495  label="srouby058"
  Placement = pos=(0,0,0.5) rot=(0,0,1;0rad)
  Shapes = -> [Screw_solid164,Screw_solid150,Screw_solid172]
FEATURE [Part::Cut] Cut061260  label="unasec vrch030"
  Base = -> Cylinder014005729
  Tool = -> Fusion495
FEATURE [Part::Cut] Cut061270  label="Unasec Vrch zaklad031"
  Base = -> Cut061260
  Tool = -> Fusion454
FEATURE [Part::MultiFuse] Fusion446  label="unasec vrhch 019"
  Shapes = -> [Cut061270,Cut007_solid026,Cylinder014005736]
FEATURE [Part::Cut] Cut061285  label="Unasec + Sun015"
  Base = -> Fusion446
  Tool = -> Cylinder014005747
FEATURE [Part::Feature] Screw_solid173  label="M2x4-Screw (Solid)173"
  Placement = pos=(0,0,0) rot=(0,0,1;1.0472rad)
  shape: bbox 3.6 x 3.6 x 4 mm, 12 faces (baked)
FEATURE [Part::MultiFuse] Fusion430  label="srouby050"
  Shapes = -> [Screw_solid173,Screw_solid161,Screw_solid167]
FEATURE [Part::Cut] Cut061282  label="Uasec spodek021"
  Base = -> Cut061268
  Tool = -> Fusion430
FEATURE [Part::MultiFuse] Fusion455  label="Unasec spdek final016"
  Shapes = -> [Cut061282,Fusion492]
FEATURE [App::Part] Part062  label="Part080"
  Group = -> [Cut061268,Cut061282,Cylinder014005755,Cylinder014005789,Cylinder014005786,Cylinder014005784,Cylinder014005816,Cylinder014005803,Cylinder014005800,Screw_solid167,Cylinder014005796,Screw_solid173,Cylinder014005804,Screw_solid161,Fusion415,Fusion493,Fusion430,Fusion492,Fusion455,Cut008_solid057,Cut008_solid055,Cut008_solid058,Screw_solid152,Cylinder014005818,Cylinder014005797,Screw_solid154,+49 more]
  License = CC BY 3.0
  LicenseURL = http://creativecommons.org/licenses/by/3.0/
  Origin = -> Origin061
  Placement = pos=(0,0,42) rot=(0,0,1;0rad)
FEATURE [Part::Feature] Cut008_solid062  label="Planet063"
  Placement = pos=(0,0,0) rot=(0,0,1;2.0944rad)
  shape: bbox 12.9 x 13.1 x 5 mm, 57 faces (baked)
FEATURE [Part::Feature] Cylinder014005823  label="Válec719"
  Placement = pos=(0,0,0) rot=(0,0,1;4.18879rad)
  shape: bbox 5 x 5 x 7 mm, 3 faces (baked)
FEATURE [Part::Feature] Cylinder014005824  label="Válec720"
  Placement = pos=(0,0,0) rot=(0,0,1;2.0944rad)
  shape: bbox 16 x 16 x 10 mm, 3 faces (baked)
FEATURE [Part::MultiFuse] Fusion422
  Shapes = -> [Cylinder014005732,Cylinder014005739,Cylinder014005817,Cylinder014005824]
FEATURE [Part::Cut] Cut061294  label="unasec spodek038"
  Base = -> Fusion414
  Tool = -> Fusion422
FEATURE [Part::Cut] Cut061242  label="Uasec spodek017"
  Base = -> Cut061294
  Tool = -> Fusion421
FEATURE [Part::MultiFuse] Fusion469  label="Unasec spdek final020"
  Shapes = -> [Cut061242,Fusion483]
FEATURE [App::Part] Part061
  Group = -> [Cut061294,Cut061242,Cylinder014005732,Cylinder014005750,Cylinder014005744,Cylinder014005739,Cylinder014005817,Cylinder014005812,Cylinder014005824,Screw_solid169,Cylinder014005807,Screw_solid163,Cylinder014005814,Screw_solid153,Fusion422,Fusion414,Fusion421,Fusion483,Fusion469,Cut008_solid056,Cut008_solid060,Cut008_solid054,Screw_solid164,Cylinder014005724,Cylinder014005821,Screw_solid150,+27 more]
  License = CC BY 3.0
  LicenseURL = http://creativecommons.org/licenses/by/3.0/
  Origin = -> Origin063
  Placement = pos=(0,0,31.5) rot=(0,0,1;0rad)
FEATURE [Part::Feature] Cut005_solid001_cs021
  Placement = pos=(0,0,-11.25) rot=(0,0,1;0rad)
  shape: bbox 41 x 41 x 3e-07 mm, 0 faces, 0 solids (baked)
FEATURE [Part::Extrusion] Extrude071  label="box016"
  Base = -> Cut005_solid001_cs021
  Dir = (0,0,1)
  DirMode = 2
  FaceMakerClass = Part::FaceMakerBullseye
  LengthFwd = 10.5
  LengthRev = 0
  Placement = pos=(0,0,-3) rot=(0,0,1;0rad)
  Solid = true
  Symmetric = false
FEATURE [Part::MultiFuse] Fusion462  label="teloII015"
  Shapes = -> [Fusion472,Extrude071]
FEATURE [Part::Feature] Cylinder014005825  label="Válec721"
  shape: bbox 5 x 5 x 7 mm, 3 faces (baked)
FEATURE [Part::MultiFuse] Fusion458
  Shapes = -> [Cylinder014005823,Cylinder014005825,Cylinder014005815]
FEATURE [Part::MultiFuse] Fusion429
  Placement = pos=(0,0,1) rot=(0,0,1;0rad)
  Shapes = -> [Fusion458,Cylinder014005697]
FEATURE [Part::Cut] Cut061243  label="Unasec Vrch zaklad028"
  Base = -> Cut061279
  Tool = -> Fusion429
FEATURE [Part::MultiFuse] Fusion475  label="unasec vrhch 020"
  Shapes = -> [Cut061243,Cut007_solid028,Cylinder014005743]
FEATURE [Part::Cut] Cut061292  label="Unasec + Sun016"
  Base = -> Fusion475
  Tool = -> Cylinder014005734
FEATURE [App::Part] Part056  label="Part078"
  Group = -> [Cut061271,Cut061258,Cylinder014005698,Cylinder014005728,Cylinder014005707,Cylinder014005699,Cylinder014005716,Cylinder014005714,Cylinder014005726,Screw_solid171,Cylinder014005713,Screw_solid149,Cylinder014005813,Screw_solid141,Fusion432,Fusion463,Fusion452,Fusion461,Fusion459,Cut008_solid061,Cut008_solid062,Cut008_solid051,Screw_solid170,Cylinder014005825,Cylinder014005815,Screw_solid147,+27 more]
  License = CC BY 3.0
  LicenseURL = http://creativecommons.org/licenses/by/3.0/
  Origin = -> Origin059
  Placement = pos=(0,0,21) rot=(0,0,1;0rad)
FEATURE [App::Part] Part066  label="GearBOX 1024:1a002"
  Group = -> [Part060,Part055,Part056,Part061,Part062]
  License = CC BY 3.0
  LicenseURL = http://creativecommons.org/licenses/by/3.0/
  Origin = -> Origin058
FEATURE [App::Part] Part054  label="DriveA002"
  Group = -> [Part059,Part066]
  License = CC BY 3.0
  LicenseURL = http://creativecommons.org/licenses/by/3.0/
  Origin = -> Origin065
  Placement = pos=(0,-29,0) rot=(1,0,0;3.14159rad)
FEATURE [Part::Cut] Cut061310
  Base = -> Cut061309
  Placement = pos=(0,0,-76) rot=(0,0,1;0rad)
  Tool = -> Cut007_solid029
FEATURE [Part::Cut] Cut061311  label="Gear A006"
  Base = -> Fusion488
  Tool = -> Fusion487
FEATURE [Part::MultiFuse] Fusion486
  Shapes = -> [Cut061311,Cut061310]
FEATURE [Part::Cut] Cut061304  label="Gear27b004"
  Base = -> Fusion486
  Tool = -> Cylinder014005792
FEATURE [Part::Cut] Cut061291  label="Gear029"
  Base = -> Cut061304
  Tool = -> Cylinder014005793
FEATURE [App::Part] Part067  label="Gear27 A006"
  Group = -> [InvoluteGear037,Cylinder014005792,Sketch043,Fusion487,Fusion488,Fusion486,Cut061311,Extrude083,Cylinder014005791,Cylinder014005790,Cut007_solid029,Cut061309,Cut061310,Cut061304,Cylinder014005793,Cut061291]
  License = CC BY 3.0
  LicenseURL = http://creativecommons.org/licenses/by/3.0/
  Origin = -> Origin067
  Placement = pos=(0,0,0) rot=(0,0,-1;0.087266rad)
FEATURE [Part::FeaturePython] Nut042  label="M4-Nut018"  # Fasteners workbench fastener (typed FeaturePython)
  Placement = pos=(26,-22,0) rot=(0,0,1;0rad)
  diameter = 6
  invert = false
  matchOuter = false
  offset = 0
  thread = false
  type = 1
FEATURE [Sketcher::SketchObject] Sketch048
  MapMode = 5
  Placement = pos=(26,-22,0) rot=(1,0,0;3.14159rad)
  Support = -> [Nut042]
  sketch-geometry (7):
    g0: LineSegment StartX=2 StartY=3.50262 StartZ=0 EndX=-2.03336 EndY=3.48336 EndZ=0
    g1: LineSegment StartX=-2.03336 StartY=3.48336 StartZ=0 EndX=-4.03336 EndY=-0.0192577 EndZ=0
    g2: LineSegment StartX=-4.03336 StartY=-0.0192577 StartZ=0 EndX=-2 EndY=-3.50262 EndZ=0
    g3: LineSegment StartX=-2 StartY=-3.50262 StartZ=0 EndX=2.03336 EndY=-3.48336 EndZ=0
    g4: LineSegment StartX=2.03336 StartY=-3.48336 StartZ=0 EndX=4.03336 EndY=0.0192577 EndZ=0
    g5: LineSegment StartX=4.03336 StartY=0.0192577 StartZ=0 EndX=2 EndY=3.50262 EndZ=0
    g6: Circle [constr] CenterX=0 CenterY=0 CenterZ=0 NormalX=0 NormalY=0 NormalZ=1 AngleXU=0 Radius=4.0334
  constraints (14):
    c: Coincident(g0,g1)
    c: Coincident(g1,g2)
    c: Coincident(g2,g3)
    c: Coincident(g3,g4)
    c: Coincident(g4,g5)
    c: Coincident(g5,g0)
    c: Equal(g0, g1-g5) x5
    c: PointOnObject(g0,g6)
    c: PointOnObject(g1,g6)
    c: PointOnObject(g2,g6)
    c: PointOnObject(g3,g6)
    c: PointOnObject(g4,g6)
    c: PointOnObject(g5,g6)
    c: Coincident(g6,g-1)
FEATURE [Part::Extrusion] Extrude070
  Base = -> Sketch048
  Dir = (0,0,-1)
  DirMode = 2
  FaceMakerClass = Part::FaceMakerBullseye
  LengthFwd = -3.5
  LengthRev = 0
  Solid = true
  Symmetric = false
FEATURE [Part::FeaturePython] Screw  label="M5x50-Screw"  # Fasteners workbench fastener (typed FeaturePython)
  Placement = pos=(0,-29,-101) rot=(0,1,0;3.14159rad)
  diameter = 5
  invert = false
  length = 10
  matchOuter = false
  offset = 0
  thread = false
  type = 5
FEATURE [Part::Cylinder] Cylinder014005826  label="Válec722"
  Angle = 360
  AttacherType = Attacher::AttachEngine3D
  Height = 20
  Placement = pos=(0,0,-113) rot=(0,0,1;0rad)
  Radius = 19
FEATURE [Part::Box] Box135  label="Krychle122"
  AttacherType = Attacher::AttachEngine3D
  Height = 42
  Length = 34
  Placement = pos=(-17,-63,-59) rot=(0,0,1;0rad)
  Width = 14
FEATURE [Part::Chamfer] Chamfer015  label="Nastavba002"
  Base = -> Box135
  Edges = 2 edges r=7: [Edge1,Edge5]
FEATURE [Part::MultiFuse] Fusion438  label="celo"
  Placement = pos=(0,0,-54) rot=(0,0,1;0rad)
  Shapes = -> [Chamfer015,Chamfer019]
FEATURE [Part::Cylinder] Cylinder014005827  label="Válec723"
  Angle = 360
  AttacherType = Attacher::AttachEngine3D
  Height = 200
  Placement = pos=(0,-29,-200) rot=(0,0,1;0rad)
  Radius = 2.7
FEATURE [Part::Cylinder] Cylinder014005828  label="Válec724"
  Angle = 360
  AttacherType = Attacher::AttachEngine3D
  Height = 200
  Placement = pos=(0,-56,-200) rot=(0,0,1;0rad)
  Radius = 3.2
FEATURE [Part::Cylinder] Cylinder014005829  label="LOZISKO001"
  Angle = 360
  AttacherType = Attacher::AttachEngine3D
  Height = 4
  Placement = pos=(0,-29,-97) rot=(0,0,1;0rad)
  Radius = 5.6
FEATURE [Part::Cylinder] Cylinder014005830  label="LOZISKO"
  Angle = 360
  AttacherType = Attacher::AttachEngine3D
  Height = 4
  Placement = pos=(0,-29,-113) rot=(0,0,1;0rad)
  Radius = 5.6
FEATURE [Part::MultiFuse] Fusion442
  Shapes = -> [Cylinder014005830,Cylinder014005829,Cylinder014005827,Cylinder014005826,Cylinder014005828]
FEATURE [Part::Cut] Cut061241  label="Celo"
  Base = -> Fusion438
  Placement = pos=(0,0,12) rot=(0,0,1;0rad)
  Tool = -> Fusion442
FEATURE [Part::Box] Box136  label="Krychle123"
  AttacherType = Attacher::AttachEngine3D
  Height = 22
  Length = 9
  Placement = pos=(-30,-35,-81) rot=(0,0,1;0rad)
  Width = 28
FEATURE [Part::Box] Box137  label="Krychle124"
  AttacherType = Attacher::AttachEngine3D
  Height = 3.5
  Length = 5
  Placement = pos=(27,-25.5,0) rot=(0,0,1;0rad)
  Width = 7
FEATURE [Part::MultiFuse] Fusion437  label="Matka"
  Placement = pos=(0,0,-50) rot=(0,0,1;0rad)
  Shapes = -> [Box137,Nut035,Extrude069]
FEATURE [Part::Cylinder] Cylinder014005831  label="Válec725"
  Angle = 360
  AttacherType = Attacher::AttachEngine3D
  Height = 200
  Placement = pos=(-26,-22,-140) rot=(0,0,1;0rad)
  Radius = 2.2
FEATURE [Part::Box] Box138  label="Krychle125"
  AttacherType = Attacher::AttachEngine3D
  Height = 22
  Length = 9
  Placement = pos=(21,-35,-81) rot=(0,0,1;0rad)
  Width = 28
FEATURE [Part::MultiFuse] Fusion434
  Shapes = -> [Cut061241,Box138,Box136]
FEATURE [Part::Box] Box139  label="Krychle126"
  AttacherType = Attacher::AttachEngine3D
  Height = 3.5
  Length = 5
  Placement = pos=(27,-25.5,0) rot=(0,0,1;0rad)
  Width = 7
FEATURE [Part::MultiFuse] Fusion440  label="Matka001"
  Placement = pos=(0,-44,-50) rot=(0,0,1;3.14159rad)
  Shapes = -> [Box139,Nut042,Extrude070]
FEATURE [Part::Cylinder] Cylinder014005832  label="Válec726"
  Angle = 360
  AttacherType = Attacher::AttachEngine3D
  Height = 200
  Placement = pos=(-26,-22,-140) rot=(0,0,1;0rad)
  Radius = 2.2
FEATURE [Part::Cylinder] Cylinder014005833  label="Válec727"
  Angle = 360
  AttacherType = Attacher::AttachEngine3D
  Height = 200
  Placement = pos=(26,-22,-140) rot=(0,0,1;0rad)
  Radius = 2.2
FEATURE [Part::MultiFuse] Fusion435
  Shapes = -> [Cylinder014005833,Cylinder014005832]
FEATURE [Part::Cut] Cut061305  label="CeloFin"
  Base = -> Fusion434
  Tool = -> Fusion435
FEATURE [Part::Box] Box140  label="Krychle127"
  AttacherType = Attacher::AttachEngine3D
  Height = 9.5
  Length = 34
  Placement = pos=(-17,-63,-59) rot=(0,0,1;0rad)
  Width = 14
FEATURE [Part::Chamfer] Chamfer018  label="Nastavba"
  Base = -> Box140
  Edges = 2 edges r=7: [Edge1,Edge5]
FEATURE [Part::MultiFuse] Fusion441
  Shapes = -> [Chamfer018,Chamfer017]
FEATURE [Part::Cylinder] Cylinder014005834  label="Válec728"
  Angle = 360
  AttacherType = Attacher::AttachEngine3D
  Height = 200
  Placement = pos=(26,-22,-140) rot=(0,0,1;0rad)
  Radius = 2.2
FEATURE [Part::Cylinder] Cylinder014005835  label="Válec729"
  Angle = 360
  AttacherType = Attacher::AttachEngine3D
  Height = 200
  Placement = pos=(0,-56,-238) rot=(0,0,1;0rad)
  Radius = 3.2
FEATURE [Part::MultiFuse] Fusion436
  Shapes = -> [Cylinder014005834,Nut036,Cylinder014005835,Cylinder014005831,Fusion437,Fusion440]
FEATURE [Part::Cut] Cut061306  label="AXIS1"
  Base = -> Fusion441
  Tool = -> Fusion436
FEATURE [App::Part] Part063  label="Asix 1 RA001"
  Group = -> [Nut040,Nut038,Nut041,Screw,Box119,Chamfer015,Fusion434,Cut061241,Fusion435,Fusion438,Fusion442,Chamfer019,Cylinder014005826,Box135,Cylinder014005827,Cylinder014005828,Cylinder014005829,Cylinder014005830,Box136,Box138,Cylinder014005832,Cylinder014005833,Cut061305,Nut035,Fusion416,Fusion417,Fusion418,Fusion423,Fusion436,Fusion437,Nut036,Sketch041,Box120,Cylinder014005660,Cylinder014005661,+45 more]
  License = CC BY 3.0
  LicenseURL = http://creativecommons.org/licenses/by/3.0/
  Origin = -> Origin057
FEATURE [Part::Cylinder] Cylinder014005836  label="Válec730"
  Angle = 360
  AttacherType = Attacher::AttachEngine3D
  Height = 65
  Placement = pos=(-32,0,-27) rot=(0,1,0;1.5708rad)
  Radius = 1.35
FEATURE [Part::Cylinder] Cylinder014005837  label="Válec731"
  Angle = 360
  AttacherType = Attacher::AttachEngine3D
  Height = 65
  Placement = pos=(-32,15,-27) rot=(0,1,0;1.5708rad)
  Radius = 1.35
FEATURE [Part::Cylinder] Cylinder014005838  label="Válec732"
  Angle = 360
  AttacherType = Attacher::AttachEngine3D
  Height = 3
  Placement = pos=(23,0,-27) rot=(0,1,0;1.5708rad)
  Radius = 2.35
FEATURE [Part::Cylinder] Cylinder014005839  label="Válec733"
  Angle = 360
  AttacherType = Attacher::AttachEngine3D
  Height = 3
  Placement = pos=(23,15,-27) rot=(0,1,0;1.5708rad)
  Radius = 2.35
FEATURE [Part::MultiFuse] Fusion439
  Shapes = -> [Cylinder014005838,Cylinder014005836,Cylinder014005837,Cylinder014005839]
FEATURE [Part::Cut] Cut061240  label="Dovecot"
  Base = -> Cut061308
  Placement = pos=(10,-29,-15) rot=(0,0,1;0rad)
  Tool = -> Fusion439
FEATURE [App::Part] Part057  label="Dovecot001"
  Group = -> [Fusion439,Cut061308,Cylinder014005836,Cylinder014005837,Cylinder014005838,Cylinder014005839,Cut061240]
  License = CC BY 3.0
  LicenseURL = http://creativecommons.org/licenses/by/3.0/
  Origin = -> Origin054
FEATURE [App::Part] Part065  label="RA"
  Group = -> [Part064,Part058,Screw018,Part054,Part063,Part067,Part057,Fusion395,Cut061239,Cylinder014005655,Cylinder014005656,Box118,Cylinder014005659,Box117,Fillet006]
  License = CC BY 3.0
  LicenseURL = http://creativecommons.org/licenses/by/3.0/
  Origin = -> Origin066
  Placement = pos=(0,-20,0) rot=(0,0,1;3.14159rad)
FEATURE [Part::Box] Box141  label="Krychle128"
  AttacherType = Attacher::AttachEngine3D
  Height = 20
  Length = 60
  Placement = pos=(-30,-49,-59) rot=(0,0,1;0rad)
  Width = 52
FEATURE [Part::Chamfer] Chamfer022
  Base = -> Box141
  Edges = 4 edges r=10: [Edge1,Edge3,Edge5,Edge7]
FEATURE [Part::Box] Box142  label="deska013"
  AttacherType = Attacher::AttachEngine3D
  Height = 111
  Length = 43
  Placement = pos=(-21.5,21.5,-51.5) rot=(0,0,1;0rad)
  Width = 10
FEATURE [Part::Cylinder] Cylinder014005840  label="Válec734"
  Angle = 360
  AttacherType = Attacher::AttachEngine3D
  Height = 50
  Placement = pos=(15.5,15.5,0) rot=(0,0,1;0rad)
  Radius = 1.6
FEATURE [Part::Cylinder] Cylinder014005841  label="DIRA8,005"
  Angle = 360
  AttacherType = Attacher::AttachEngine3D
  Height = 200
  Placement = pos=(0,29,-100) rot=(0,0,1;0rad)
  Radius = 4.2
FEATURE [Part::Cylinder] Cylinder014005842  label="Válec735"
  Angle = 360
  AttacherType = Attacher::AttachEngine3D
  Height = 50
  Placement = pos=(15.5,-15.5,0) rot=(0,0,1;0rad)
  Radius = 1.6
FEATURE [Part::Cylinder] Cylinder014005843  label="Válec736"
  Angle = 360
  AttacherType = Attacher::AttachEngine3D
  Height = 10
  Placement = pos=(0,43,54.5) rot=(1,0,0;1.5708rad)
  Radius = 4
FEATURE [Part::Cylinder] Cylinder014005844  label="Válec737"
  Angle = 360
  AttacherType = Attacher::AttachEngine3D
  Height = 65
  Placement = pos=(-32,0,-27) rot=(0,1,0;1.5708rad)
  Radius = 1.35
FEATURE [Part::Cylinder] Cylinder014005845  label="dira stred006"
  Angle = 360
  AttacherType = Attacher::AttachEngine3D
  Height = 50
  Radius = 13
FEATURE [Part::Cylinder] Cylinder014005846  label="Válec738"
  Angle = 360
  AttacherType = Attacher::AttachEngine3D
  Height = 50
  Placement = pos=(-15.5,15.5,0) rot=(0,0,1;0rad)
  Radius = 1.6
FEATURE [Part::Cylinder] Cylinder014005847  label="Lozisko012"
  Angle = 360
  AttacherType = Attacher::AttachEngine3D
  Height = 4
  Placement = pos=(0,29,-52.1) rot=(0,0,1;0rad)
  Radius = 7
FEATURE [Part::Box] Box143  label="Krychle129"
  AttacherType = Attacher::AttachEngine3D
  Height = 112
  Length = 38
  Placement = pos=(-19,34,-52) rot=(0,0,1;0rad)
  Width = 6
FEATURE [Part::Box] Box144  label="Krychle130"
  AttacherType = Attacher::AttachEngine3D
  Height = 112
  Length = 38
  Placement = pos=(-19,32,-52) rot=(0,0,1;0rad)
  Width = 10
FEATURE [Part::Box] Box145  label="Krychle131"
  AttacherType = Attacher::AttachEngine3D
  Height = 2
  Length = 80
  Placement = pos=(-40,-30,-53) rot=(0,0,1;0rad)
  Width = 80
FEATURE [Part::Cylinder] Cylinder014005848  label="Válec739"
  Angle = 360
  AttacherType = Attacher::AttachEngine3D
  Height = 10
  Placement = pos=(0,43,-47) rot=(1,0,0;1.5708rad)
  Radius = 4
FEATURE [Part::Cylinder] Cylinder014005849  label="Válec740"
  Angle = 360
  AttacherType = Attacher::AttachEngine3D
  Height = 50
  Placement = pos=(-15.5,-15.5,0) rot=(0,0,1;0rad)
  Radius = 1.6
FEATURE [Part::MultiFuse] Fusion502  label="diry014"
  Shapes = -> [Cylinder014005846,Cylinder014005840,Cylinder014005845,Cylinder014005849,Cylinder014005842]
FEATURE [Part::Cylinder] Cylinder014005850  label="Válec741"
  Angle = 360
  AttacherType = Attacher::AttachEngine3D
  Height = 65
  Placement = pos=(-32,0,0) rot=(0,1,0;1.5708rad)
  Radius = 1.35
FEATURE [Part::Box] Box146  label="Krychle132"
  AttacherType = Attacher::AttachEngine3D
  Height = 10
  Length = 43
  Placement = pos=(-21.5,-20.5,0) rot=(0,0,1;0rad)
  Width = 42
FEATURE [Part::Chamfer] Chamfer024
  Base = -> Box146
  Edges = 2 edges r=5: [Edge1,Edge5]
FEATURE [Part::Box] Box147  label="deska014"
  AttacherType = Attacher::AttachEngine3D
  Height = 111
  Length = 9
  Placement = pos=(21.5,-14.5,-51.5) rot=(0,0,1;0rad)
  Width = 46
FEATURE [Part::Box] Box148  label="deska015"
  AttacherType = Attacher::AttachEngine3D
  Height = 111
  Length = 9
  Placement = pos=(-30.5,-14.5,-51.5) rot=(0,0,1;0rad)
  Width = 46
FEATURE [Part::Box] Box149  label="Krychle133"
  AttacherType = Attacher::AttachEngine3D
  Height = 2
  Length = 80
  Placement = pos=(-40,-30,59) rot=(0,0,1;0rad)
  Width = 80
FEATURE [Part::MultiFuse] Fusion503  label="Orez003"
  Shapes = -> [Box149,Box145]
FEATURE [Part::Cylinder] Cylinder014005851  label="Lozisko013"
  Angle = 360
  AttacherType = Attacher::AttachEngine3D
  Height = 4
  Placement = pos=(0,29,56) rot=(0,0,1;0rad)
  Radius = 7
FEATURE [Part::MultiFuse] Fusion504  label="DIRA OSA003"
  Shapes = -> [Cylinder014005841,Cylinder014005847,Cylinder014005851]
FEATURE [Part::Cylinder] Cylinder014005852  label="Válec742"
  Angle = 360
  AttacherType = Attacher::AttachEngine3D
  Height = 65
  Placement = pos=(-32,0,42) rot=(0,1,0;1.5708rad)
  Radius = 1.35
FEATURE [Part::Cylinder] Cylinder014005853  label="Válec743"
  Angle = 360
  AttacherType = Attacher::AttachEngine3D
  Height = 65
  Placement = pos=(-32,15,-27) rot=(0,1,0;1.5708rad)
  Radius = 1.35
FEATURE [Part::Cylinder] Cylinder014005854  label="Válec744"
  Angle = 360
  AttacherType = Attacher::AttachEngine3D
  Height = 65
  Placement = pos=(-32,15,42) rot=(0,1,0;1.5708rad)
  Radius = 1.35
FEATURE [Part::MultiFuse] Fusion505  label="diry 2,009"
  Shapes = -> [Cylinder014005854,Cylinder014005850,Cylinder014005852,Cylinder014005844,Cylinder014005853]
FEATURE [Part::MultiFuse] Fusion506  label="Diry orez003"
  Shapes = -> [Fusion505,Fusion504,Fusion503]
FEATURE [Part::Cut] Cut061313  label="Horni ucjyt004"
  Base = -> Chamfer024
  Placement = pos=(0,0,49.5) rot=(0,0,1;0rad)
  Tool = -> Fusion502
FEATURE [Part::MultiFuse] Fusion501  label="motor drazak004"
  Shapes = -> [Cut061313,Box147,Box142,Box148]
FEATURE [Part::Cut] Cut061315
  Base = -> Box144
  Tool = -> Box143
FEATURE [Part::FeaturePython] Nut043  label="M6-Nut012"  # Fasteners workbench fastener (typed FeaturePython)
  Placement = pos=(0,-56,-106) rot=(0,0,1;0rad)
  diameter = 8
  invert = false
  matchOuter = false
  offset = 0
  thread = false
  type = 1
FEATURE [Part::FeaturePython] Nut044  label="M4-Nut019"  # Fasteners workbench fastener (typed FeaturePython)
  Placement = pos=(26,-22,0) rot=(0,0,1;0rad)
  diameter = 6
  invert = false
  matchOuter = false
  offset = 0
  thread = false
  type = 1
FEATURE [Sketcher::SketchObject] Sketch050
  MapMode = 5
  Placement = pos=(26,-22,0) rot=(1,0,0;3.14159rad)
  Support = -> [Nut044]
  sketch-geometry (7):
    g0: LineSegment StartX=2 StartY=3.50262 StartZ=0 EndX=-2.03336 EndY=3.48336 EndZ=0
    g1: LineSegment StartX=-2.03336 StartY=3.48336 StartZ=0 EndX=-4.03336 EndY=-0.0192577 EndZ=0
    g2: LineSegment StartX=-4.03336 StartY=-0.0192577 StartZ=0 EndX=-2 EndY=-3.50262 EndZ=0
    g3: LineSegment StartX=-2 StartY=-3.50262 StartZ=0 EndX=2.03336 EndY=-3.48336 EndZ=0
    g4: LineSegment StartX=2.03336 StartY=-3.48336 StartZ=0 EndX=4.03336 EndY=0.0192577 EndZ=0
    g5: LineSegment StartX=4.03336 StartY=0.0192577 StartZ=0 EndX=2 EndY=3.50262 EndZ=0
    g6: Circle [constr] CenterX=0 CenterY=0 CenterZ=0 NormalX=0 NormalY=0 NormalZ=1 AngleXU=0 Radius=4.0334
  constraints (14):
    c: Coincident(g0,g1)
    c: Coincident(g1,g2)
    c: Coincident(g2,g3)
    c: Coincident(g3,g4)
    c: Coincident(g4,g5)
    c: Coincident(g5,g0)
    c: Equal(g0, g1-g5) x5
    c: PointOnObject(g0,g6)
    c: PointOnObject(g1,g6)
    c: PointOnObject(g2,g6)
    c: PointOnObject(g3,g6)
    c: PointOnObject(g4,g6)
    c: PointOnObject(g5,g6)
    c: Coincident(g6,g-1)
FEATURE [Part::FeaturePython] Nut045  label="M8-Nut009"  # Fasteners workbench fastener (typed FeaturePython)
  Placement = pos=(0,0,-90) rot=(0,0,1;0rad)
  diameter = 9
  invert = false
  matchOuter = false
  offset = 0
  thread = false
  type = 1
FEATURE [Part::FeaturePython] Nut046  label="M5-Nut001"  # Fasteners workbench fastener (typed FeaturePython)
  Placement = pos=(0,-29,-80) rot=(0,0,1;0rad)
  diameter = 7
  invert = false
  matchOuter = false
  offset = 0
  thread = false
  type = 1
FEATURE [Part::FeaturePython] Screw020  label="M5x50-Screw001"  # Fasteners workbench fastener (typed FeaturePython)
  Placement = pos=(0,-29,-101) rot=(0,1,0;3.14159rad)
  diameter = 5
  invert = false
  length = 10
  matchOuter = false
  offset = 0
  thread = false
  type = 5
FEATURE [Part::FeaturePython] Nut047  label="M4-Nut020"  # Fasteners workbench fastener (typed FeaturePython)
  Placement = pos=(26,-22,0) rot=(0,0,1;0rad)
  diameter = 6
  invert = false
  matchOuter = false
  offset = 0
  thread = false
  type = 1
FEATURE [Sketcher::SketchObject] Sketch049
  MapMode = 5
  Placement = pos=(26,-22,0) rot=(1,0,0;3.14159rad)
  Support = -> [Nut047]
  sketch-geometry (7):
    g0: LineSegment StartX=2 StartY=3.50262 StartZ=0 EndX=-2.03336 EndY=3.48336 EndZ=0
    g1: LineSegment StartX=-2.03336 StartY=3.48336 StartZ=0 EndX=-4.03336 EndY=-0.0192577 EndZ=0
    g2: LineSegment StartX=-4.03336 StartY=-0.0192577 StartZ=0 EndX=-2 EndY=-3.50262 EndZ=0
    g3: LineSegment StartX=-2 StartY=-3.50262 StartZ=0 EndX=2.03336 EndY=-3.48336 EndZ=0
    g4: LineSegment StartX=2.03336 StartY=-3.48336 StartZ=0 EndX=4.03336 EndY=0.0192577 EndZ=0
    g5: LineSegment StartX=4.03336 StartY=0.0192577 StartZ=0 EndX=2 EndY=3.50262 EndZ=0
    g6: Circle [constr] CenterX=0 CenterY=0 CenterZ=0 NormalX=0 NormalY=0 NormalZ=1 AngleXU=0 Radius=4.0334
  constraints (14):
    c: Coincident(g0,g1)
    c: Coincident(g1,g2)
    c: Coincident(g2,g3)
    c: Coincident(g3,g4)
    c: Coincident(g4,g5)
    c: Coincident(g5,g0)
    c: Equal(g0, g1-g5) x5
    c: PointOnObject(g0,g6)
    c: PointOnObject(g1,g6)
    c: PointOnObject(g2,g6)
    c: PointOnObject(g3,g6)
    c: PointOnObject(g4,g6)
    c: PointOnObject(g5,g6)
    c: Coincident(g6,g-1)
FEATURE [Part::FeaturePython] Nut048  label="M6-Nut013"  # Fasteners workbench fastener (typed FeaturePython)
  Placement = pos=(0,-56,-53) rot=(0,0,1;0rad)
  diameter = 8
  invert = false
  matchOuter = false
  offset = 0
  thread = false
  type = 1
FEATURE [Part::Extrusion] Extrude085
  Base = -> Sketch049
  Dir = (0,0,-1)
  DirMode = 2
  FaceMakerClass = Part::FaceMakerBullseye
  LengthFwd = -3.5
  LengthRev = 0
  Solid = true
  Symmetric = false
FEATURE [Part::Extrusion] Extrude086
  Base = -> Sketch050
  Dir = (0,0,-1)
  DirMode = 2
  FaceMakerClass = Part::FaceMakerBullseye
  LengthFwd = -3.5
  LengthRev = 0
  Solid = true
  Symmetric = false
FEATURE [Sketcher::SketchObject] Sketch051
  MapMode = 5
  Placement = pos=(0,0,60) rot=(0,0,1;0rad)
  sketch-geometry (6):
    g0: LineSegment StartX=-18.9734 StartY=34.0308 StartZ=0 EndX=-16.0253 EndY=36.9748 EndZ=0
    g1: LineSegment StartX=18.996 StartY=34.0308 StartZ=0 EndX=16.044 EndY=36.9748 EndZ=0
    g2: LineSegment StartX=18.996 StartY=34.0308 StartZ=0 EndX=-18.9734 EndY=34.0308 EndZ=0
    g3: LineSegment StartX=-18.9734 StartY=40.0311 StartZ=0 EndX=-16.0253 EndY=36.9748 EndZ=0
    g4: LineSegment StartX=16.044 StartY=36.9748 StartZ=0 EndX=18.9109 EndY=40.0311 EndZ=0
    g5: LineSegment StartX=-18.9734 StartY=40.0311 StartZ=0 EndX=18.9109 EndY=40.0311 EndZ=0
  constraints (7):
    c: Coincident(g2,g1)
    c: Coincident(g2,g0)
    c: Horizontal(g2)
    c: Coincident(g3,g0)
    c: Coincident(g5,g3)
    c: Coincident(g5,g4)
    c: Horizontal(g5)
FEATURE [Part::Extrusion] Extrude087
  Base = -> Sketch051
  Dir = (0,0,1)
  DirMode = 2
  FaceMakerClass = Part::FaceMakerBullseye
  LengthFwd = -112
  LengthRev = 0
  Solid = true
  Symmetric = false
FEATURE [Part::MultiFuse] Fusion508  label="Arca plate base015"
  Placement = pos=(0,-0.5,0) rot=(0,0,1;0rad)
  Shapes = -> [Extrude087,Cut061315]
FEATURE [Part::MultiFuse] Fusion507  label="drzak s arca004"
  Shapes = -> [Fusion501,Fusion508,Cylinder014005843,Cylinder014005848]
FEATURE [Part::Cut] Cut061314  label="Blok A003"
  Base = -> Fusion507
  Tool = -> Fusion506
FEATURE [Part::Chamfer] Chamfer021  label="Axis 005"
  Base = -> Cut061314
  Edges = 4 edges r=8: [Edge132,Edge133,Edge152,Edge153]
  Placement = pos=(0,-29,0) rot=(0,1,0;3.14159rad)
FEATURE [Part::Cylinder] Cylinder014005855  label="LOZISKO002"
  Angle = 360
  AttacherType = Attacher::AttachEngine3D
  Height = 4
  Placement = pos=(0,-29,-113) rot=(0,0,1;0rad)
  Radius = 5.6
FEATURE [Part::Box] Box150  label="Krychle134"
  AttacherType = Attacher::AttachEngine3D
  Height = 42
  Length = 34
  Placement = pos=(-17,-63,-59) rot=(0,0,1;0rad)
  Width = 14
FEATURE [Part::Chamfer] Chamfer023  label="Nastavba004"
  Base = -> Box150
  Edges = 2 edges r=7: [Edge1,Edge5]
FEATURE [Part::MultiFuse] Fusion509  label="celo001"
  Placement = pos=(0,0,-54) rot=(0,0,1;0rad)
  Shapes = -> [Chamfer023,Chamfer022]
FEATURE [Part::Box] Box151  label="Krychle135"
  AttacherType = Attacher::AttachEngine3D
  Height = 22
  Length = 9
  Placement = pos=(21,-35,-81) rot=(0,0,1;0rad)
  Width = 28
FEATURE [Part::Cylinder] Cylinder014005856  label="LOZISKO003"
  Angle = 360
  AttacherType = Attacher::AttachEngine3D
  Height = 4
  Placement = pos=(0,-29,-97) rot=(0,0,1;0rad)
  Radius = 5.6
FEATURE [Part::Cylinder] Cylinder014005857  label="Válec745"
  Angle = 360
  AttacherType = Attacher::AttachEngine3D
  Height = 200
  Placement = pos=(0,-29,-200) rot=(0,0,1;0rad)
  Radius = 2.7
FEATURE [Part::Cylinder] Cylinder014005858  label="Válec746"
  Angle = 360
  AttacherType = Attacher::AttachEngine3D
  Height = 200
  Placement = pos=(0,-56,-200) rot=(0,0,1;0rad)
  Radius = 3.2
FEATURE [Part::Cylinder] Cylinder014005859  label="Válec747"
  Angle = 360
  AttacherType = Attacher::AttachEngine3D
  Height = 20
  Placement = pos=(0,0,-113) rot=(0,0,1;0rad)
  Radius = 19
FEATURE [Part::MultiFuse] Fusion512
  Shapes = -> [Cylinder014005855,Cylinder014005856,Cylinder014005857,Cylinder014005859,Cylinder014005858]
FEATURE [Part::Cut] Cut061312  label="Celo001"
  Base = -> Fusion509
  Placement = pos=(0,0,12) rot=(0,0,1;0rad)
  Tool = -> Fusion512
FEATURE [Part::Box] Box152  label="Krychle136"
  AttacherType = Attacher::AttachEngine3D
  Height = 3.5
  Length = 5
  Placement = pos=(27,-25.5,0) rot=(0,0,1;0rad)
  Width = 7
FEATURE [Part::MultiFuse] Fusion513  label="Matka003"
  Placement = pos=(0,0,-50) rot=(0,0,1;0rad)
  Shapes = -> [Box152,Nut047,Extrude085]
FEATURE [Part::Box] Box153  label="Krychle137"
  AttacherType = Attacher::AttachEngine3D
  Height = 22
  Length = 9
  Placement = pos=(-30,-35,-81) rot=(0,0,1;0rad)
  Width = 28
FEATURE [Part::MultiFuse] Fusion498
  Shapes = -> [Cut061312,Box151,Box153]
FEATURE [Part::Cylinder] Cylinder014005860  label="Válec748"
  Angle = 360
  AttacherType = Attacher::AttachEngine3D
  Height = 200
  Placement = pos=(-26,-22,-140) rot=(0,0,1;0rad)
  Radius = 2.2
FEATURE [Part::Box] Box154  label="Krychle138"
  AttacherType = Attacher::AttachEngine3D
  Height = 3.5
  Length = 5
  Placement = pos=(27,-25.5,0) rot=(0,0,1;0rad)
  Width = 7
FEATURE [Part::MultiFuse] Fusion510  label="Matka002"
  Placement = pos=(0,-44,-50) rot=(0,0,1;3.14159rad)
  Shapes = -> [Box154,Nut044,Extrude086]
FEATURE [Part::Cylinder] Cylinder014005861  label="Válec749"
  Angle = 360
  AttacherType = Attacher::AttachEngine3D
  Height = 200
  Placement = pos=(0,-56,-238) rot=(0,0,1;0rad)
  Radius = 3.2
FEATURE [Part::Cylinder] Cylinder014005862  label="Válec750"
  Angle = 360
  AttacherType = Attacher::AttachEngine3D
  Height = 200
  Placement = pos=(26,-22,-140) rot=(0,0,1;0rad)
  Radius = 2.2
FEATURE [Part::Box] Box155  label="Krychle139"
  AttacherType = Attacher::AttachEngine3D
  Height = 9.5
  Length = 34
  Placement = pos=(-17,-63,-59) rot=(0,0,1;0rad)
  Width = 14
FEATURE [Part::Chamfer] Chamfer020  label="Nastavba003"
  Base = -> Box155
  Edges = 2 edges r=7: [Edge1,Edge5]
FEATURE [Part::MultiFuse] Fusion511
  Shapes = -> [Chamfer020,Chamfer021]
FEATURE [Part::Cylinder] Cylinder014005863  label="Válec751"
  Angle = 360
  AttacherType = Attacher::AttachEngine3D
  Height = 200
  Placement = pos=(26,-22,-140) rot=(0,0,1;0rad)
  Radius = 2.2
FEATURE [Part::MultiFuse] Fusion500
  Shapes = -> [Cylinder014005863,Nut048,Cylinder014005861,Cylinder014005860,Fusion513,Fusion510]
FEATURE [Part::Cut] Cut061316  label="AXIS002"
  Base = -> Fusion511
  Tool = -> Fusion500
FEATURE [Part::Cylinder] Cylinder014005864  label="Válec752"
  Angle = 360
  AttacherType = Attacher::AttachEngine3D
  Height = 200
  Placement = pos=(-26,-22,-140) rot=(0,0,1;0rad)
  Radius = 2.2
FEATURE [Part::MultiFuse] Fusion499
  Shapes = -> [Cylinder014005862,Cylinder014005864]
FEATURE [Part::Cut] Cut061317  label="CeloFin001"
  Base = -> Fusion498
  Tool = -> Fusion499
FEATURE [App::Part] Part069  label="Asix 1 RA002"
  Group = -> [Nut043,Nut045,Nut046,Screw020,Box141,Chamfer023,Fusion498,Cut061312,Fusion499,Fusion509,Fusion512,Chamfer022,Cylinder014005859,Box150,Cylinder014005857,Cylinder014005858,Cylinder014005856,Cylinder014005855,Box153,Box151,Cylinder014005864,Cylinder014005862,Cut061317,Nut047,Fusion505,Fusion506,Fusion507,Fusion508,Fusion500,Fusion513,Nut048,Sketch051,Box142,Cylinder014005840,Cylinder014005841,+45 more]
  License = CC BY 3.0
  LicenseURL = http://creativecommons.org/licenses/by/3.0/
  Origin = -> Origin069
FEATURE [Part::Cylinder] Cylinder014005865  label="Válec753"
  Angle = 360
  AttacherType = Attacher::AttachEngine3D
  Height = 20
  Placement = pos=(0,-1,0) rot=(0,0,1;0rad)
  Radius = 3.2
FEATURE [Part::Cylinder] Cylinder014005866  label="Válec754"
  Angle = 360
  AttacherType = Attacher::AttachEngine3D
  Height = 15
  Placement = pos=(7.5,7.5,7.5) rot=(1,0,0;1.5708rad)
  Radius = 1.7
FEATURE [Part::Box] Box156  label="Krychle140"
  AttacherType = Attacher::AttachEngine3D
  Height = 15
  Length = 26
  Placement = pos=(-13,-3.5,0) rot=(0,0,1;0rad)
  Width = 14
FEATURE [Part::Cylinder] Cylinder014005867  label="Válec755"
  Angle = 360
  AttacherType = Attacher::AttachEngine3D
  Height = 15
  Placement = pos=(-7.5,7.5,7.5) rot=(1,0,0;1.5708rad)
  Radius = 1.7
FEATURE [Part::MultiFuse] Fusion514
  Shapes = -> [Cylinder014005867,Cylinder014005866,Cylinder014005865,Box156]
FEATURE [Part::Box] Box157  label="Krychle141"
  AttacherType = Attacher::AttachEngine3D
  Height = 15
  Length = 26
  Placement = pos=(-13,-5.5,0) rot=(0,0,1;0rad)
  Width = 14
FEATURE [Part::Cut] Cut061318
  Base = -> Box157
  Tool = -> Fusion514
FEATURE [Part::Fillet] Fillet007  label="Kabel holder001"
  Base = -> Cut061318
  Edges = 4 edges r=1: [Edge4,Edge9,Edge16,Edge17]
FEATURE [App::Part] Part068  label="TMP"
  Group = -> [Part037,Part023,Fusion514,Cylinder014005866,Cylinder014005865,Box156,Cylinder014005867,Box157,Cut061318,Fillet007,Part049,Part025,Extrude028,Chamfer007,Fusion206,Fusion205,Sketch011,Box002,Cylinder001,Box001,Cylinder014005340,Cut061088,Cut001,Extrude025,RegularPolygon004,Extrude027,Extrude026,Sketch009,Fusion200,Fusion193,Fusion195,Fusion194,Fusion197,Fusion196,Fusion198,Fusion191,Fusion201,+60 more]
  License = CC BY 3.0
  LicenseURL = http://creativecommons.org/licenses/by/3.0/
  Origin = -> Origin068
FEATURE [Part::Cylinder] Cylinder014005868  label="Válec756"
  Angle = 360
  AttacherType = Attacher::AttachEngine3D
  Height = 20
  Placement = pos=(0,-1,0) rot=(0,0,1;0rad)
  Radius = 3.2
FEATURE [Part::Cylinder] Cylinder014005869  label="Válec757"
  Angle = 360
  AttacherType = Attacher::AttachEngine3D
  Height = 15
  Placement = pos=(7.5,7.5,7.5) rot=(1,0,0;1.5708rad)
  Radius = 1.7
FEATURE [Part::Box] Box158  label="Krychle142"
  AttacherType = Attacher::AttachEngine3D
  Height = 15
  Length = 26
  Placement = pos=(-13,-3.5,0) rot=(0,0,1;0rad)
  Width = 14
FEATURE [Part::Cylinder] Cylinder014005870  label="Válec758"
  Angle = 360
  AttacherType = Attacher::AttachEngine3D
  Height = 15
  Placement = pos=(-7.5,7.5,7.5) rot=(1,0,0;1.5708rad)
  Radius = 1.7
FEATURE [Part::MultiFuse] Fusion515
  Shapes = -> [Cylinder014005870,Cylinder014005869,Cylinder014005868,Box158]
FEATURE [Part::Box] Box159  label="Krychle143"
  AttacherType = Attacher::AttachEngine3D
  Height = 15
  Length = 26
  Placement = pos=(-13,-5.5,0) rot=(0,0,1;0rad)
  Width = 14
FEATURE [Part::Cut] Cut061319
  Base = -> Box159
  Tool = -> Fusion515
FEATURE [Part::Fillet] Fillet008  label="Kabel holder002"
  Base = -> Cut061319
  Edges = 4 edges r=1: [Edge4,Edge9,Edge16,Edge17]
  Placement = pos=(26,-21.5,-49.5) rot=(0,0,1;1.5708rad)
FEATURE [App::Part] Part026  label="DEC"
  Group = -> [Part022,Screw009,Part019,Part024,Part052,Part069,Cylinder014005868,Box158,Cylinder014005869,Cylinder014005870,Box159,Cut061319,Fusion515,Fillet008]
  License = CC BY 3.0
  LicenseURL = http://creativecommons.org/licenses/by/3.0/
  Origin = -> Origin026
  Placement = pos=(0,0,85) rot=(-1,0,0;1.5708rad)
FEATURE [App::Part] Part042  label="EQ-Mout"
  Group = -> [Part026,Part041,Part065]
  License = CC BY 3.0
  LicenseURL = http://creativecommons.org/licenses/by/3.0/
  Origin = -> Origin042
FEATURE [App::Part] Part044  label="Sestava"
  Group = -> [Part040,Part042]
  License = CC BY 3.0
  LicenseURL = http://creativecommons.org/licenses/by/3.0/
  Origin = -> Origin044
  Placement = pos=(0,0,71) rot=(1,0,0;1.0472rad)
